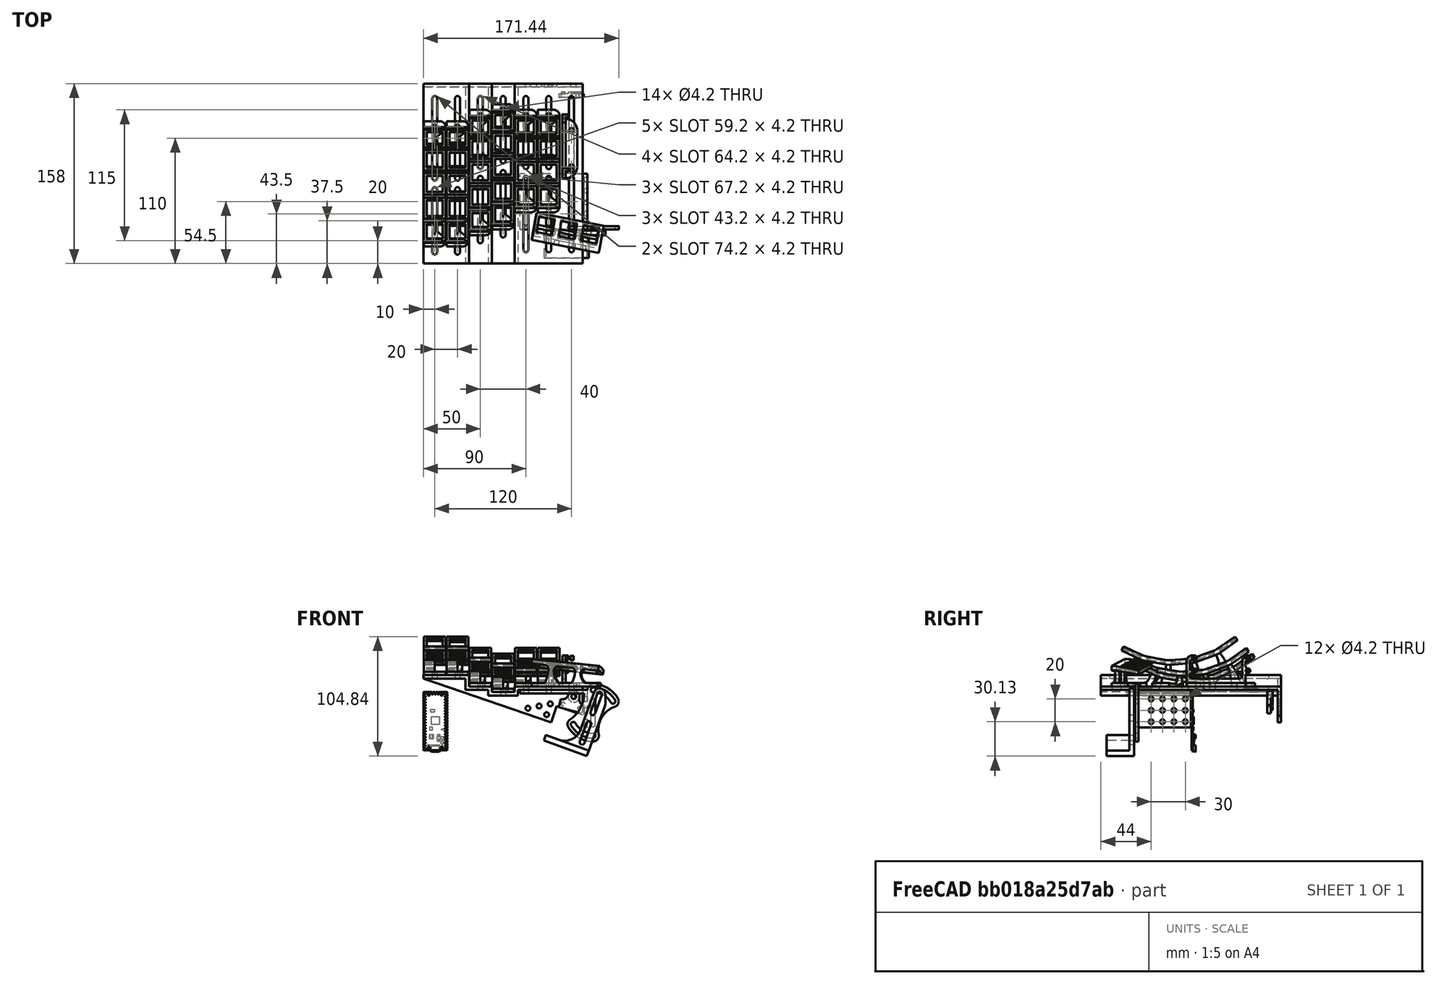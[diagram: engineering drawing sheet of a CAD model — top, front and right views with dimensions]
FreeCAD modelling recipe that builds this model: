
FCSTD DOCUMENT  (FreeCAD 0.20RUnknown)
Label: Dactyl Chimera V3
License: All rights reserved
LicenseURL: http://en.wikipedia.org/wiki/All_rights_reserved
objects: Sketcher::SketchObject×60, PartDesign::Pad×39, PartDesign::Pocket×21, PartDesign::Body×14, Part::Feature×14, App::Part×3, PartDesign::Plane×3, App::Link×3, App::DocumentObjectGroup×2, Part::Mirroring×2, Spreadsheet::Sheet×1, PartDesign::Line×1, Mesh::Feature×1
note: 214 computed .brp shape members not serialized (recipe doc carries the construction recipe); baked Part::Feature solids carry a one-line shape summary decoded from their .brp

FEATURE [Spreadsheet::Sheet] Spreadsheet
  cells = A1=Name; B1=Value; C1=Notes; A2=ModRowKey; B2(ModRowKey)==5mm; C2=The height of the keycaps in the row closest to you; A3=ZRowKey; B3(ZRowKey)==5mm; A4=ARowKey; B4(ARowKey)==5mm; A5=QRowKey; B5(QRowKey)==5mm; A6=TopRowKey; B6(TopRowKey)==5mm; A7=NutR; B7(NutR)==5mm; C7=The radius of the nut plus any clearance you want for your wrench.; A8=ScrewD; B8(ScrewD)==4.2mm; C8=The diameter of the screw shaft plus a bit extra so it fits nicely.; A9=Wiring; B9(Wiring)==6mm; C9=Minimum space under keys for hotswap sockets, PCBs, RGB, etc.; A10=ArchLength; B10(ArchLength)==45mm; C10=Set the distance of the screws in the arch feet. 
FEATURE [Sketcher::SketchObject] Sketch
  FullyConstrained = true
  MapMode = 5
  Placement = pos=(0,0,0) rot=(0.57735,0.57735,0.57735;2.0944rad)
  Support = -> [YZ_Plane]
  expr: Constraints[147] = <<Spreadsheet>>.ARowKey
  expr: Constraints[148] = <<Spreadsheet>>.ZRowKey
  expr: Constraints[155] = <<Spreadsheet>>.QRowKey
  expr: Constraints[159] = <<Spreadsheet>>.ModRowKey
  expr: Constraints[165] = <<Spreadsheet>>.TopRowKey
  expr: Constraints[171] = <<Spreadsheet>>.Wiring
  sketch-geometry (61):
    g0: LineSegment StartX=-50 StartY=9 StartZ=0 EndX=-50 EndY=3 EndZ=0
    g1: LineSegment StartX=-9.46385 StartY=12.9848 StartZ=0 EndX=0 EndY=13.8128 EndZ=0
    g2: LineSegment StartX=0 StartY=13.8128 StartZ=0 EndX=9.46385 EndY=14.6407 EndZ=0
    g3: LineSegment StartX=9.46385 StartY=14.6407 StartZ=0 EndX=11.8732 EndY=15.1749 EndZ=0
    g4: LineSegment StartX=11.8732 StartY=15.1749 StartZ=0 EndX=20.8002 EndY=18.4241 EndZ=0
    g5: LineSegment StartX=20.8002 StartY=18.4241 StartZ=0 EndX=29.7273 EndY=21.6733 EndZ=0
    g6: LineSegment StartX=29.7273 StartY=21.6733 StartZ=0 EndX=31.9163 EndY=22.8128 EndZ=0
    g7: LineSegment StartX=31.9163 StartY=22.8128 StartZ=0 EndX=39.6982 EndY=28.2617 EndZ=0
    g8: LineSegment StartX=39.6982 StartY=28.2617 StartZ=0 EndX=47.4802 EndY=33.7107 EndZ=0
    g9: LineSegment StartX=47.4802 StartY=33.7107 StartZ=0 EndX=49.7745 EndY=30.4341 EndZ=0
    g10: LineSegment StartX=49.7745 StartY=30.4341 StartZ=0 EndX=34.2106 EndY=19.5362 EndZ=0
    g11: LineSegment StartX=34.2106 StartY=19.5362 StartZ=0 EndX=31.0954 EndY=17.9145 EndZ=0
    g12: LineSegment StartX=31.0954 StartY=17.9145 StartZ=0 EndX=13.2412 EndY=11.4161 EndZ=0
    g13: LineSegment StartX=13.2412 StartY=11.4161 StartZ=0 EndX=9.81247 EndY=10.656 EndZ=0
    g14: LineSegment StartX=9.81247 StartY=10.656 StartZ=0 EndX=-9.11523 EndY=9 EndZ=0
    g15: LineSegment StartX=-9.11523 StartY=9 StartZ=0 EndX=-12.6239 EndY=9.15319 EndZ=0
    g16: LineSegment StartX=-12.6239 StartY=9.15319 StartZ=0 EndX=-31.3353 EndY=12.4525 EndZ=0
    g17: LineSegment StartX=-31.3353 StartY=12.4525 StartZ=0 EndX=-34.6847 EndY=13.5086 EndZ=0
    g18: LineSegment StartX=-34.6847 StartY=13.5086 StartZ=0 EndX=-51.9046 EndY=21.5383 EndZ=0
    g19: LineSegment StartX=-51.9046 StartY=21.5383 StartZ=0 EndX=-50.2141 EndY=25.1636 EndZ=0
    g20: LineSegment StartX=-50.2141 StartY=25.1636 StartZ=0 EndX=-41.6042 EndY=21.1487 EndZ=0
    g21: LineSegment StartX=-41.6042 StartY=21.1487 StartZ=0 EndX=-32.9942 EndY=17.1338 EndZ=0
    g22: LineSegment StartX=-32.9942 StartY=17.1338 StartZ=0 EndX=-30.6407 EndY=16.3917 EndZ=0
    g23: LineSegment StartX=-30.6407 StartY=16.3917 StartZ=0 EndX=-21.285 EndY=14.7421 EndZ=0
    g24: LineSegment StartX=-21.285 StartY=14.7421 StartZ=0 EndX=-11.9293 EndY=13.0924 EndZ=0
    g25: LineSegment StartX=-11.9293 StartY=13.0924 StartZ=0 EndX=-9.46385 EndY=12.9848 EndZ=0
    g26: LineSegment StartX=-34.6847 StartY=13.5086 StartZ=0 EndX=-32.9942 EndY=17.1338 EndZ=0
    g27: LineSegment StartX=-30.6407 StartY=16.3917 StartZ=0 EndX=-31.3353 EndY=12.4525 EndZ=0
    g28: LineSegment StartX=-12.6239 StartY=9.15319 StartZ=0 EndX=-11.9293 EndY=13.0924 EndZ=0
    g29: LineSegment StartX=-9.46385 StartY=12.9848 StartZ=0 EndX=-9.11523 EndY=9 EndZ=0
    g30: LineSegment StartX=9.46385 StartY=14.6407 StartZ=0 EndX=9.81247 EndY=10.656 EndZ=0
    g31: LineSegment StartX=11.8732 StartY=15.1749 StartZ=0 EndX=13.2412 EndY=11.4161 EndZ=0
    g32: LineSegment StartX=29.7273 StartY=21.6733 StartZ=0 EndX=31.0954 EndY=17.9145 EndZ=0
    g33: LineSegment StartX=31.9163 StartY=22.8128 StartZ=0 EndX=34.2106 EndY=19.5362 EndZ=0
    g34: LineSegment StartX=-41.6042 StartY=21.1487 StartZ=0 EndX=-39.4911 EndY=25.6802 EndZ=0
    g35: LineSegment StartX=-21.285 StartY=14.7421 StartZ=0 EndX=-20.4167 EndY=19.6661 EndZ=0
    g36: LineSegment StartX=0 StartY=13.8128 StartZ=0 EndX=-0.435779 EndY=18.7937 EndZ=0
    g37: LineSegment StartX=20.8002 StartY=18.4241 StartZ=0 EndX=19.0901 EndY=23.1225 EndZ=0
    g38: LineSegment StartX=39.6982 StartY=28.2617 StartZ=0 EndX=36.8304 EndY=32.3575 EndZ=0
    g39: LineSegment StartX=-39.4911 StartY=25.6802 StartZ=0 EndX=-36.7722 EndY=24.4124 EndZ=0
    g40: LineSegment StartX=-36.7722 StartY=24.4124 StartZ=0 EndX=-32.546 EndY=33.4755 EndZ=0
    g41: LineSegment StartX=-21.6347 StartY=30.0351 StartZ=0 EndX=-23.3712 EndY=20.1871 EndZ=0
    g42: LineSegment StartX=-23.3712 StartY=20.1871 StartZ=0 EndX=-20.4167 EndY=19.6661 EndZ=0
    g43: LineSegment StartX=-20.4167 StartY=19.6661 StartZ=0 EndX=-17.4623 EndY=19.1452 EndZ=0
    g44: LineSegment StartX=-17.4623 StartY=19.1452 StartZ=0 EndX=-15.7258 EndY=28.9933 EndZ=0
    g45: LineSegment StartX=-4.29592 StartY=28.4942 StartZ=0 EndX=-3.42436 EndY=18.5323 EndZ=0
    g46: LineSegment StartX=-3.42436 StartY=18.5323 StartZ=0 EndX=-0.435779 EndY=18.7937 EndZ=0
    g47: LineSegment StartX=-0.435779 StartY=18.7937 StartZ=0 EndX=2.55281 EndY=19.0552 EndZ=0
    g48: LineSegment StartX=2.55281 StartY=19.0552 StartZ=0 EndX=1.68125 EndY=29.0171 EndZ=0
    g49: LineSegment StartX=12.8509 StartY=31.4934 StartZ=0 EndX=16.2711 EndY=22.0965 EndZ=0
    g50: LineSegment StartX=16.2711 StartY=22.0965 StartZ=0 EndX=19.0901 EndY=23.1225 EndZ=0
    g51: LineSegment StartX=19.0901 StartY=23.1225 StartZ=0 EndX=21.9092 EndY=24.1486 EndZ=0
    g52: LineSegment StartX=21.9092 StartY=24.1486 StartZ=0 EndX=18.489 EndY=33.5455 EndZ=0
    g53: LineSegment StartX=28.6371 StartY=38.8283 StartZ=0 EndX=34.3729 EndY=30.6368 EndZ=0
    g54: LineSegment StartX=34.3729 StartY=30.6368 StartZ=0 EndX=36.8304 EndY=32.3575 EndZ=0
    g55: ArcOfCircle CenterX=-14.0244 CenterY=73.195 CenterZ=0 NormalX=0 NormalY=0 NormalZ=1 AngleXU=0 Radius=43.8257 StartAngle=4.27606 EndAngle=4.53786
    g56: ArcOfCircle CenterX=-8.11558 CenterY=72.1532 CenterZ=0 NormalX=0 NormalY=0 NormalZ=1 AngleXU=0 Radius=43.8257 StartAngle=4.53786 EndAngle=4.79966
    g57: ArcOfCircle CenterX=-2.13841 CenterY=72.6761 CenterZ=0 NormalX=0 NormalY=0 NormalZ=1 AngleXU=0 Radius=43.8257 StartAngle=4.79966 EndAngle=5.06145
    g58: ArcOfCircle CenterX=3.49974 CenterY=74.7282 CenterZ=0 NormalX=0 NormalY=0 NormalZ=1 AngleXU=0 Radius=43.8257 StartAngle=5.06145 EndAngle=5.32325
    g59: LineSegment StartX=-50 StartY=9 StartZ=0 EndX=-70 EndY=9 EndZ=0
    g60: LineSegment StartX=-50 StartY=9 StartZ=0 EndX=50 EndY=9 EndZ=0
  constraints (176):
    c: Vertical(g0)
    c: Coincident(g1,g2)
    c: Coincident(g2,g3)
    c: Coincident(g3,g4)
    c: Coincident(g4,g5)
    c: Coincident(g5,g6)
    c: Coincident(g6,g7)
    c: Coincident(g7,g8)
    c: Coincident(g8,g9)
    c: Coincident(g9,g10)
    c: Coincident(g10,g11)
    c: Coincident(g11,g12)
    c: Coincident(g12,g13)
    c: Coincident(g13,g14)
    c: Coincident(g14,g15)
    c: Coincident(g15,g16)
    c: Coincident(g16,g17)
    c: Coincident(g17,g18)
    c: Coincident(g18,g19)
    c: Coincident(g19,g20)
    c: Coincident(g20,g21)
    c: Coincident(g21,g22)
    c: Coincident(g22,g23)
    c: Coincident(g23,g24)
    c: Coincident(g24,g25)
    c: Coincident(g25,g1)
    c: Coincident(g26,g17)
    c: Coincident(g26,g21)
    c: Coincident(g27,g22)
    c: Coincident(g27,g16)
    c: Coincident(g28,g15)
    c: Coincident(g28,g24)
    c: Coincident(g29,g1)
    c: Coincident(g29,g14)
    c: Coincident(g30,g2)
    c: Coincident(g30,g13)
    c: Coincident(g31,g3)
    c: Coincident(g31,g12)
    c: Coincident(g32,g5)
    c: Coincident(g32,g11)
    c: Coincident(g33,g6)
    c: Coincident(g33,g10)
    c: Coincident(g34,g20)
    c: Coincident(g35,g23)
    c: Coincident(g36,g1)
    c: Coincident(g37,g4)
    c: Coincident(g38,g7)
    c: Parallel(g1,g2)
    c: Parallel(g4,g5)
    c: Parallel(g8,g7)
    c: Parallel(g21,g20)
    c: Parallel(g23,g24)
    c: Equal(g5,g4)
    c: Equal(g7,g8)
    c: Equal(g2,g1)
    c: Equal(g24,g23)
    c: Equal(g21,g20)
    c: Equal(g14,g16)
    c: Equal(g14,g12)
    c: Equal(g14,g10)
    c: Equal(g14,g18)
    c: Perpendicular(g26,g21)
    c: Perpendicular(g18,g26)
    c: Perpendicular(g19,g18)
    c: Perpendicular(g28,g24)
    c: Perpendicular(g16,g28)
    c: Perpendicular(g27,g16)
    c: Perpendicular(g14,g30)
    c: Perpendicular(g29,g14)
    c: Perpendicular(g31,g4)
    c: Perpendicular(g12,g31)
    c: Perpendicular(g32,g12)
    c: Perpendicular(g33,g7)
    c: Perpendicular(g10,g33)
    c: Perpendicular(g9,g10)
    c: Perpendicular(g8,g38)
    c: Perpendicular(g5,g37)
    c: Perpendicular(g1,g36)
    c: Perpendicular(g23,g35)
    c: Perpendicular(g20,g34)
    c: Equal(g29,g28)
    c: Equal(g27,g26)
    c: Equal(g30,g31)
    c: Equal(g32,g33)
    c: Coincident(g39,g40)
    c: Coincident(g41,g42)
    c: Coincident(g42,g35)
    c: Coincident(g42,g43)
    c: Coincident(g43,g44)
    c: Coincident(g45,g46)
    c: Coincident(g46,g36)
    c: Coincident(g46,g47)
    c: Coincident(g47,g48)
    c: Coincident(g49,g50)
    c: Coincident(g50,g37)
    c: Coincident(g50,g51)
    c: Coincident(g51,g52)
    c: Coincident(g53,g54)
    c: Coincident(g54,g38)
    c: Perpendicular(g54,g53)
    c: Perpendicular(g38,g54)
    c: Perpendicular(g51,g52)
    c: Perpendicular(g37,g51)
    c: Perpendicular(g50,g37)
    c: Perpendicular(g49,g50)
    c: Perpendicular(g47,g48)
    c: Perpendicular(g36,g47)
    c: Perpendicular(g46,g36)
    c: Perpendicular(g45,g46)
    c: Perpendicular(g43,g44)
    c: Perpendicular(g35,g43)
    c: Perpendicular(g42,g35)
    c: Perpendicular(g41,g42)
    c: Perpendicular(g39,g40)
    c: Perpendicular(g34,g39)
    c: Coincident(g55,g41)
    c: Coincident(g55,g40)
    c: Coincident(g56,g44)
    c: Coincident(g56,g45)
    c: Coincident(g57,g48)
    c: Coincident(g57,g49)
    c: Coincident(g58,g52)
    c: Coincident(g58,g53)
    c: Equal(g46,g47)
    c: Equal(g47,g50)
    c: Equal(g50,g51)
    c: Equal(g51,g54)
    c: Equal(g39,g42)
    c: Equal(g42,g43)
    c: Equal(g43,g46)
    c: Coincident(g39,g34)
    c: Distance(g14) = 19
    c: Distance(g35,g36) = 20
    c: Perpendicular(g56,g44)
    c: Perpendicular(g57,g48)
    c: Perpendicular(g57,g49)
    c: Angle(g35,g36) = 0.261799
    c: Perpendicular(g56,g45)
    c: Perpendicular(g58,g53)
    c: Perpendicular(g58,g52)
    c: Perpendicular(g55,g41)
    c: Perpendicular(g55,g40)
    c: Distance(g44) = 10
    c: Distance(g45) = 10
    c: Coincident(g59,g0)
    c: Horizontal(g59)
    c: Angle(g59,g36) = 1.65806
    c: Distance(g36) = 5
    c: Distance(g35) = 5
    c: Distance(g41) = 10
    c: Distance(g40) = 10
    c: Distance(g53) = 10
    c: Distance(g52) = 10
    c: Angle(g36,g37) = 0.261799
    c: Distance(g49) = 10
    c: Distance(g37) = 5
    c: Distance(g48) = 10
    c: Distance(g50) = 3
    c: Distance(g37,g36) = 20
    c: Distance(g34) = 5
    c: Angle(g34,g35) = 0.261799
    c: Distance(g35,g34) = 20
    c: Distance(g37,g38) = 20
    c: DistanceX(g0,g-1) = 50
    c: DistanceX(g59,g59) = 20
    c: Distance(g38) = 5
    c: Angle(g37,g38) = 0.261799
    c: Distance(g29) = 4
    c: Equal(g30,g29)
    c: Coincident(g60,g0)
    c: Horizontal(g60)
    c: DistanceY(g0,g0) = 6
    c: DistanceX(g60,g60) = 100
    c: DistanceY(g-1,g0) = 3
    c: PointOnObject(g14,g60)
    c: PointOnObject(g1,g-2)
FEATURE [PartDesign::Pad] Pad  label="OArch"
  Direction = (1,-2e-16,3e-16)
  Length = 19
  Length2 = 100
  Midplane = true
  Placement = pos=(0,0,0) rot=(0.57735,0.57735,0.57735;2.0944rad)
  Profile = -> Sketch
  Type = 0
FEATURE [Sketcher::SketchObject] Sketch001
  ExternalGeometry = -> [Pad]
  FullyConstrained = true
  MapMode = 5
  Placement = pos=(0,0,0) rot=(0.57735,0.57735,0.57735;2.0944rad)
  Support = -> [YZ_Plane]
  expr: Constraints[103] = <<Spreadsheet>>.Wiring
  expr: Constraints[104] = Spreadsheet.Wiring
  expr: Constraints[106] = <<Spreadsheet>>.Wiring
  expr: Constraints[107] = <<Spreadsheet>>.Wiring
  expr: Constraints[108] = <<Spreadsheet>>.Wiring
  expr: Constraints[109] = <<Spreadsheet>>.Wiring
  expr: Constraints[110] = <<Spreadsheet>>.Wiring
  expr: Constraints[111] = <<Spreadsheet>>.ArchLength * 2 - 10mm
  expr: Constraints[21] = <<Spreadsheet>>.ArchLength
  expr: Constraints[34] = <<Spreadsheet>>.ArchLength
  expr: Constraints[8] = <<Spreadsheet>>.Wiring + 4mm
  expr: Constraints[99] = <<Spreadsheet>>.Wiring
  sketch-geometry (44):
    g0: LineSegment StartX=-30.6407 StartY=16.3917 StartZ=0 EndX=-32.9942 EndY=17.1338 EndZ=0
    g1: LineSegment StartX=-11.9293 StartY=13.0924 StartZ=0 EndX=-9.46385 EndY=12.9848 EndZ=0
    g2: LineSegment StartX=11.8732 StartY=15.1749 StartZ=0 EndX=9.46385 EndY=14.6407 EndZ=0
    g3: LineSegment StartX=31.9163 StartY=22.8128 StartZ=0 EndX=29.7273 EndY=21.6733 EndZ=0
    g4: LineSegment StartX=-30.6407 StartY=16.3917 StartZ=0 EndX=-32.3771 EndY=6.54366 EndZ=0
    g5: LineSegment StartX=-11.9293 StartY=13.0924 StartZ=0 EndX=-13.6658 EndY=3.24435 EndZ=0
    g6: LineSegment StartX=-9.46385 StartY=12.9848 StartZ=0 EndX=-8.59229 EndY=3.02283 EndZ=0
    g7: LineSegment StartX=10.3354 StartY=4.67879 StartZ=0 EndX=9.46385 EndY=14.6407 EndZ=0
    g8: LineSegment StartX=11.8732 StartY=15.1749 StartZ=0 EndX=15.2934 EndY=5.77795 EndZ=0
    g9: LineSegment StartX=33.1475 StartY=12.2763 StartZ=0 EndX=29.7273 EndY=21.6733 EndZ=0
    g10: LineSegment StartX=31.9163 StartY=22.8128 StartZ=0 EndX=37.6521 EndY=14.6213 EndZ=0
    g11: LineSegment StartX=-37.2204 StartY=8.07075 StartZ=0 EndX=-32.9942 EndY=17.1338 EndZ=0
    g12: LineSegment StartX=-13.6658 StartY=0 StartZ=0 EndX=-8.59229 EndY=0 EndZ=0
    g13: LineSegment StartX=-45 StartY=3 StartZ=0 EndX=-45 EndY=0 EndZ=0
    g14: LineSegment StartX=-45 StartY=0 StartZ=0 EndX=-35 EndY=0 EndZ=0
    g15: LineSegment StartX=35 StartY=0 StartZ=0 EndX=45 EndY=0 EndZ=0
    g16: LineSegment StartX=45 StartY=3 StartZ=0 EndX=45 EndY=0 EndZ=0
    g17: LineSegment StartX=10.3354 StartY=0 StartZ=0 EndX=15.2934 EndY=0 EndZ=0
    g18: LineSegment StartX=-32.3771 StartY=6.54366 StartZ=0 EndX=-35 EndY=0 EndZ=0
    g19: LineSegment StartX=35 StartY=0 StartZ=0 EndX=33.1475 EndY=12.2763 EndZ=0
    g20-g23: Circle x4 (B-spline internal-alignment scaffolding for g24; pole/knot coordinates omitted)
    g24: BSplineCurve PolesCount=4 KnotsCount=2 Degree=3 IsPeriodic=0
    g25: GeomPoint X=-37.2204 Y=8.07075 Z=0
    g26: GeomPoint X=-45 Y=3 Z=0
    g27-g30: Circle x4 (B-spline internal-alignment scaffolding for g31; pole/knot coordinates omitted)
    g31: BSplineCurve PolesCount=4 KnotsCount=2 Degree=3 IsPeriodic=0
    g32: GeomPoint X=37.6521 Y=14.6213 Z=0
    g33: GeomPoint X=45 Y=3 Z=0
    g34: LineSegment StartX=45 StartY=3 StartZ=0 EndX=40 EndY=3 EndZ=0
    g35: LineSegment StartX=-45 StartY=3 StartZ=0 EndX=-40 EndY=3 EndZ=0
    g36: LineSegment StartX=42.2622 StartY=8.03741 StartZ=0 EndX=37.6521 EndY=14.6213 EndZ=0
    g37: LineSegment StartX=-37.2204 StartY=8.07075 StartZ=0 EndX=-39.0097 EndY=4.23371 EndZ=0
    g38: LineSegment StartX=-39.0097 StartY=0 StartZ=0 EndX=-39.0097 EndY=4.23371 EndZ=0
    g39: LineSegment StartX=42.2622 StartY=8.03741 StartZ=0 EndX=42.2622 EndY=0 EndZ=0
    g40: LineSegment StartX=-13.6658 StartY=3.24435 StartZ=0 EndX=-13.6658 EndY=0 EndZ=0
    g41: LineSegment StartX=-8.59229 StartY=3.02283 StartZ=0 EndX=-8.59229 EndY=0 EndZ=0
    g42: LineSegment StartX=10.3354 StartY=4.67879 StartZ=0 EndX=10.3354 EndY=0 EndZ=0
    g43: LineSegment StartX=15.2934 StartY=5.77795 StartZ=0 EndX=15.2934 EndY=0 EndZ=0
  constraints (107):
    c: Coincident(g-6,g2)
    c: Coincident(g2,g-6)
    c: Coincident(g0,g-10)
    c: Coincident(g0,g-10)
    c: Coincident(g1,g-7)
    c: Coincident(g1,g-7)
    c: Coincident(g-3,g3)
    c: Coincident(g3,g-3)
    c: Distance(g0,g11) = 10
    c: Coincident(g4,g0)
    c: Coincident(g5,g1)
    c: Coincident(g6,g1)
    c: Coincident(g8,g2)
    c: Coincident(g9,g3)
    c: Coincident(g10,g3)
    c: Coincident(g11,g0)
    c: Equal(g11,g4)
    c: Equal(g9,g10)
    c: Coincident(g7,g2)
    c: PointOnObject(g12,g-1)
    c: PointOnObject(g12,g-1)
    c: DistanceX(g-11,g16) = 45
    c: PointOnObject(g13,g-1)
    c: Vertical(g13)
    c: Coincident(g13,g14)
    c: Horizontal(g14)
    c: DistanceY(g13,g13) = 3
    c: PointOnObject(g17,g-1)
    c: Horizontal(g15)
    c: Coincident(g16,g15)
    c: Vertical(g16)
    c: Equal(g13,g16)
    c: PointOnObject(g15,g-1)
    c: Horizontal(g17)
    c: DistanceX(g13,g-11) = 45
    c: Coincident(g18,g4)
    c: Coincident(g18,g14)
    c: Coincident(g19,g15)
    c: Coincident(g19,g9)
    c: Coincident(g24,g11)
    c: Weight(g20) = 1
    c: Equal(g20,g21)
    c: Equal(g20,g22)
    c: Equal(g20,g23)
    c: Coincident(g24,g13)
    c: InternalAlignment(g20-g23 -> g24) x4
    c: InternalAlignment(g25,g24)
    c: InternalAlignment(g26,g24)
    c: Coincident(g31,g10)
    c: Weight(g27) = 1
    c: Equal(g27,g28)
    c: Equal(g27,g29)
    c: Equal(g27,g30)
    c: Coincident(g31,g16)
    c: InternalAlignment(g27-g30 -> g31) x4
    c: InternalAlignment(g32,g31)
    c: InternalAlignment(g33,g31)
    c: Coincident(g34,g29)
    c: Coincident(g35,g13)
    c: Coincident(g35,g22)
    c: Coincident(g36,g28)
    c: Coincident(g36,g10)
    c: Coincident(g37,g11)
    c: Coincident(g37,g21)
    c: PointOnObject(g38,g-1)
    c: Coincident(g38,g21)
    c: Equal(g37,g38)
    c: Parallel(g37,g11)
    c: DistanceX(g35,g35) = 5
    c: Coincident(g34,g16)
    c: Equal(g34,g35)
    c: Coincident(g39,g28)
    c: PointOnObject(g39,g-1)
    c: Equal(g36,g39)
    c: Parallel(g36,g10)
    c: Vertical(g38)
    c: Vertical(g39)
    c: Equal(g15,g14)
    c: DistanceX(g14,g14) = 10
    c: Distance(g10) = 10
    c: Equal(g9,g4)
    c: Coincident(g40,g5)
    c: Coincident(g40,g12)
    c: Coincident(g41,g6)
    c: Coincident(g41,g12)
    c: Vertical(g41)
    c: Vertical(g40)
    c: Coincident(g42,g7)
    c: Coincident(g42,g17)
    c: Coincident(g43,g8)
    c: Coincident(g43,g17)
    c: Vertical(g43)
    c: Vertical(g42)
    c: Distance(g-8,g5) = 6
    c: Equal(g6,g5)
    c: Equal(g5,g7)
    c: Equal(g7,g8)
    c: Distance(g-9,g11) = 6
    c: Distance(g-9,g4) = 6
    c: Equal(g5,g11)
    c: Distance(g-5,g7) = 6
    c: Distance(g-5,g8) = 6
    c: Distance(g-4,g9) = 6
    c: Distance(g10,g-4) = 6
    c: Distance(g6,g-8) = 6
    c: DistanceX(g22,g29) = 80
    c: Horizontal(g35)
FEATURE [PartDesign::Pad] Pad001  label="OLegs"
  BaseFeature = -> Pad
  Direction = (1,-2e-16,3e-16)
  Length = 9.5
  Length2 = 100
  Placement = pos=(0,0,0) rot=(0.57735,0.57735,0.57735;2.0944rad)
  Profile = -> Sketch001
  Reversed = true
  Type = 0
FEATURE [Sketcher::SketchObject] Sketch002
  ExternalGeometry = -> [Sketch001]
  FullyConstrained = true
  MapMode = 5
  Support = -> [XY_Plane]
  expr: Constraints[14] = <<Spreadsheet>>.NutR
  expr: Constraints[15] = <<Spreadsheet>>.NutR
  expr: Constraints[26] = <<Spreadsheet>>.ScrewD
  expr: Constraints[27] = <<Spreadsheet>>.NutR
  expr: Constraints[28] = Spreadsheet.NutR
  expr: Constraints[8] = <<Spreadsheet>>.ScrewD
  sketch-geometry (22):
    g0: LineSegment StartX=-1e-14 StartY=-45 StartZ=0 EndX=-9.5 EndY=-45 EndZ=0
    g1: LineSegment StartX=-9.5 StartY=-45 StartZ=0 EndX=-9.5 EndY=-55 EndZ=0
    g2: LineSegment StartX=-9.5 StartY=-55 StartZ=0 EndX=4.5 EndY=-55 EndZ=0
    g3: LineSegment StartX=-1e-14 StartY=-45 StartZ=0 EndX=-1e-14 EndY=-40 EndZ=0
    g4: Circle CenterX=0 CenterY=-50 CenterZ=0 NormalX=0 NormalY=0 NormalZ=1 AngleXU=0 Radius=2.1
    g5: ArcOfCircle CenterX=4.5 CenterY=-50 CenterZ=0 NormalX=0 NormalY=0 NormalZ=1 AngleXU=0 Radius=5 StartAngle=4.71239 EndAngle=7.17949
    g6: LineSegment StartX=0 StartY=-50 StartZ=0 EndX=4.5 EndY=-50 EndZ=0
    g7: LineSegment StartX=9.8e-15 StartY=40 StartZ=0 EndX=9.8e-15 EndY=45 EndZ=0
    g8: LineSegment StartX=9.8e-15 StartY=45 StartZ=0 EndX=-9.5 EndY=45 EndZ=0
    g9: LineSegment StartX=-9.5 StartY=45 StartZ=0 EndX=-9.5 EndY=55 EndZ=0
    g10: LineSegment StartX=-9.5 StartY=55 StartZ=0 EndX=4.5 EndY=55 EndZ=0
    g11: ArcOfCircle CenterX=4.5 CenterY=50 CenterZ=0 NormalX=0 NormalY=0 NormalZ=1 AngleXU=0 Radius=5 StartAngle=5.38688 EndAngle=7.85398
    g12: Circle CenterX=0 CenterY=50 CenterZ=0 NormalX=0 NormalY=0 NormalZ=1 AngleXU=0 Radius=2.1
    g13: LineSegment StartX=0 StartY=50 StartZ=0 EndX=4.5 EndY=50 EndZ=0
    g14: LineSegment StartX=7.6225 StartY=46.0949 StartZ=0 EndX=9.8e-15 EndY=40 EndZ=0
    g15: LineSegment StartX=-1e-14 StartY=-40 StartZ=0 EndX=7.6225 EndY=-46.0949 EndZ=0
    g16: LineSegment StartX=9.5 StartY=55 StartZ=0 EndX=9.5 EndY=50 EndZ=0
    g17: LineSegment StartX=-9.5 StartY=55 StartZ=0 EndX=0 EndY=50 EndZ=0
    g18: LineSegment StartX=9.5 StartY=55 StartZ=0 EndX=0 EndY=50 EndZ=0
    g19: LineSegment StartX=9.5 StartY=-50 StartZ=0 EndX=9.5 EndY=-55 EndZ=0
    g20: LineSegment StartX=9.5 StartY=-55 StartZ=0 EndX=0 EndY=-50 EndZ=0
    g21: LineSegment StartX=0 StartY=-50 StartZ=0 EndX=-9.5 EndY=-55 EndZ=0
  constraints (58):
    c: Coincident(g0,g-3)
    c: Horizontal(g0)
    c: Coincident(g1,g0)
    c: Vertical(g1)
    c: Coincident(g2,g1)
    c: Horizontal(g2)
    c: Coincident(g3,g0)
    c: DistanceY(g3,g3) = 5
    c: Diameter(g4) = 4.2
    c: Tangent(g5,g2) = -1.5708
    c: Coincident(g6,g4)
    c: Coincident(g6,g5)
    c: Horizontal(g6)
    c: PointOnObject(g4,g-2)
    c: DistanceY(g4,g0) = 5
    c: DistanceY(g1,g4) = 5
    c: Vertical(g7)
    c: Coincident(g7,g8)
    c: Horizontal(g8)
    c: Coincident(g8,g9)
    c: Vertical(g9)
    c: Coincident(g9,g10)
    c: Horizontal(g10)
    c: Tangent(g11,g10) = 1.5708
    c: DistanceY(g7,g7) = 5
    c: PointOnObject(g12,g-2)
    c: Diameter(g12) = 4.2
    c: DistanceY(g8,g12) = 5
    c: DistanceY(g12,g9) = 5
    c: Coincident(g13,g12)
    c: Coincident(g13,g11)
    c: Horizontal(g13)
    c: Coincident(g14,g7)
    c: Vertical(g3)
    c: Coincident(g15,g3)
    c: Coincident(g7,g-4)
    c: Tangent(g14,g11) = 1.5708
    c: Vertical(g16)
    c: Tangent(g16,g11)
    c: PointOnObject(g16,g11)
    c: Horizontal(g16,g10)
    c: DistanceX(g9,g16) = 19
    c: Coincident(g17,g9)
    c: Coincident(g17,g12)
    c: Coincident(g18,g16)
    c: Coincident(g18,g12)
    c: Equal(g18,g17)
    c: Tangent(g15,g5) = 1.5708
    c: Vertical(g19)
    c: Tangent(g19,g5)
    c: Coincident(g19,g20)
    c: Coincident(g20,g4)
    c: Coincident(g20,g21)
    c: Coincident(g21,g1)
    c: Horizontal(g19,g2)
    c: PointOnObject(g19,g5)
    c: Equal(g20,g21)
    c: DistanceX(g1,g19) = 19
FEATURE [PartDesign::Pad] Pad002  label="OFeet"
  BaseFeature = -> Pad001
  Direction = (0,0,1)
  Length = 3
  Length2 = 100
  Placement = pos=(0,0,0) rot=(0.57735,0.57735,0.57735;2.0944rad)
  Profile = -> Sketch002
  Type = 0
FEATURE [Sketcher::SketchObject] Sketch003
  ExternalGeometry = -> [Sketch]
  FullyConstrained = true
  MapMode = 5
  Placement = pos=(0,0,0) rot=(0.57735,0.57735,0.57735;2.0944rad)
  Support = -> [YZ_Plane]
  sketch-geometry (75):
    g0: LineSegment StartX=-41.6042 StartY=21.1487 StartZ=0 EndX=-47.9483 EndY=24.107 EndZ=0
    g1: LineSegment StartX=-41.6042 StartY=21.1487 StartZ=0 EndX=-35.26 EndY=18.1904 EndZ=0
    g2: LineSegment StartX=-41.6042 StartY=21.1487 StartZ=0 EndX=-43.2946 EndY=17.5235 EndZ=0
    g3: LineSegment StartX=-35.7723 StartY=14.0157 StartZ=0 EndX=-43.2946 EndY=17.5235 EndZ=0
    g4: LineSegment StartX=-43.2946 StartY=17.5235 StartZ=0 EndX=-50.817 EndY=21.0312 EndZ=0
    g5: LineSegment StartX=-50.817 StartY=21.0312 StartZ=0 EndX=-49.7182 EndY=23.3876 EndZ=0
    g6: LineSegment StartX=-47.9483 StartY=24.107 StartZ=0 EndX=-49.6388 EndY=20.4818 EndZ=0
    g7: LineSegment StartX=-49.7182 StartY=23.3876 StartZ=0 EndX=-48.54 EndY=22.8382 EndZ=0
    g8: LineSegment StartX=-48.54 StartY=22.8382 StartZ=0 EndX=-47.9483 EndY=24.107 EndZ=0
    g9: LineSegment StartX=-35.26 StartY=18.1904 StartZ=0 EndX=-35.8517 EndY=16.9215 EndZ=0
    g10: LineSegment StartX=-35.8517 StartY=16.9215 StartZ=0 EndX=-34.6735 EndY=16.3721 EndZ=0
    g11: LineSegment StartX=-35.7723 StartY=14.0157 StartZ=0 EndX=-34.6735 EndY=16.3721 EndZ=0
    g12: LineSegment StartX=-35.26 StartY=18.1904 StartZ=0 EndX=-36.9505 EndY=14.5651 EndZ=0
    g13: LineSegment StartX=-35.7723 StartY=14.0157 StartZ=0 EndX=-34.0818 EndY=17.641 EndZ=0
    g14: LineSegment StartX=-21.285 StartY=14.7421 StartZ=0 EndX=-21.9796 EndY=10.8028 EndZ=0
    g15: LineSegment StartX=0 StartY=13.8128 StartZ=0 EndX=0.348623 EndY=9.82798 EndZ=0
    g16: LineSegment StartX=20.8002 StartY=18.4241 StartZ=0 EndX=22.1683 EndY=14.6653 EndZ=0
    g17: LineSegment StartX=39.6982 StartY=28.2617 StartZ=0 EndX=41.9925 EndY=24.9851 EndZ=0
    g18: LineSegment StartX=-28.1786 StartY=15.9576 StartZ=0 EndX=-21.285 EndY=14.7421 EndZ=0
    g19: LineSegment StartX=-21.285 StartY=14.7421 StartZ=0 EndX=-14.3913 EndY=13.5265 EndZ=0
    g20: LineSegment StartX=-6.97336 StartY=13.2027 StartZ=0 EndX=0 EndY=13.8128 EndZ=0
    g21: LineSegment StartX=0 StartY=13.8128 StartZ=0 EndX=6.97336 EndY=14.4228 EndZ=0
    g22: LineSegment StartX=14.2224 StartY=16.0299 StartZ=0 EndX=20.8002 EndY=18.4241 EndZ=0
    g23: LineSegment StartX=20.8002 StartY=18.4241 StartZ=0 EndX=27.3781 EndY=20.8182 EndZ=0
    g24: LineSegment StartX=33.9642 StartY=24.2467 StartZ=0 EndX=39.6982 EndY=28.2617 EndZ=0
    g25: LineSegment StartX=39.6982 StartY=28.2617 StartZ=0 EndX=45.4323 EndY=32.2768 EndZ=0
    g26: LineSegment StartX=-30.1535 StartY=12.2441 StartZ=0 EndX=-21.9796 EndY=10.8028 EndZ=0
    g27: LineSegment StartX=-21.9796 StartY=10.8028 StartZ=0 EndX=-13.8057 EndY=9.36157 EndZ=0
    g28: LineSegment StartX=-7.91979 StartY=9.10459 StartZ=0 EndX=0.348623 EndY=9.82798 EndZ=0
    g29: LineSegment StartX=0.348623 StartY=9.82798 StartZ=0 EndX=8.61704 EndY=10.5514 EndZ=0
    g30: LineSegment StartX=14.3689 StartY=11.8265 StartZ=0 EndX=22.1683 EndY=14.6653 EndZ=0
    g31: LineSegment StartX=22.1683 StartY=14.6653 StartZ=0 EndX=29.9678 EndY=17.5041 EndZ=0
    g32: LineSegment StartX=-28.1786 StartY=15.9576 StartZ=0 EndX=-28.8732 EndY=12.0184 EndZ=0
    g33: LineSegment StartX=-14.3913 StartY=13.5265 StartZ=0 EndX=-15.0859 EndY=9.58731 EndZ=0
    g34: LineSegment StartX=-13.8057 StartY=9.36157 StartZ=0 EndX=-13.1111 EndY=13.3008 EndZ=0
    g35: LineSegment StartX=-6.97336 StartY=13.2027 StartZ=0 EndX=-6.62474 EndY=9.21789 EndZ=0
    g36: LineSegment StartX=-7.91979 StartY=9.10459 StartZ=0 EndX=-8.26842 EndY=13.0894 EndZ=0
    g37: LineSegment StartX=6.97336 StartY=14.4228 StartZ=0 EndX=7.32199 EndY=10.4381 EndZ=0
    g38: LineSegment StartX=8.61704 StartY=10.5514 StartZ=0 EndX=8.26842 EndY=14.5362 EndZ=0
    g39: LineSegment StartX=14.3689 StartY=11.8265 StartZ=0 EndX=13.0008 EndY=15.5853 EndZ=0
    g40: LineSegment StartX=14.2224 StartY=16.0299 StartZ=0 EndX=15.5905 EndY=12.2711 EndZ=0
    g41: LineSegment StartX=27.3781 StartY=20.8182 StartZ=0 EndX=28.7462 EndY=17.0594 EndZ=0
    g42: LineSegment StartX=29.9678 StartY=17.5041 StartZ=0 EndX=28.5997 EndY=21.2628 EndZ=0
    g43: LineSegment StartX=35.1936 StartY=20.2244 StartZ=0 EndX=32.8993 EndY=23.5011 EndZ=0
    g44: LineSegment StartX=33.9642 StartY=24.2467 StartZ=0 EndX=36.2585 EndY=20.9701 EndZ=0
    g45: LineSegment StartX=45.4323 StartY=32.2768 StartZ=0 EndX=47.7266 EndY=29.0002 EndZ=0
    g46: LineSegment StartX=48.7915 StartY=29.7458 StartZ=0 EndX=46.4972 EndY=33.0224 EndZ=0
    g47: LineSegment StartX=-30.1535 StartY=12.2441 StartZ=0 EndX=-29.4589 EndY=16.1834 EndZ=0
    g48: LineSegment StartX=-30.1535 StartY=12.2441 StartZ=0 EndX=-29.702 EndY=14.8046 EndZ=0
    g49: LineSegment StartX=-29.702 StartY=14.8046 StartZ=0 EndX=-28.4218 EndY=14.5789 EndZ=0
    g50: LineSegment StartX=-28.4218 StartY=14.5789 StartZ=0 EndX=-28.1786 EndY=15.9576 EndZ=0
    g51: LineSegment StartX=-13.8057 StartY=9.36157 StartZ=0 EndX=-13.3542 EndY=11.9221 EndZ=0
    g52: LineSegment StartX=-13.3542 StartY=11.9221 StartZ=0 EndX=-14.6344 EndY=12.1478 EndZ=0
    g53: LineSegment StartX=-14.6344 StartY=12.1478 StartZ=0 EndX=-14.3913 EndY=13.5265 EndZ=0
    g54: LineSegment StartX=-7.91979 StartY=9.10459 StartZ=0 EndX=-8.14639 EndY=11.6947 EndZ=0
    g55: LineSegment StartX=-8.14639 StartY=11.6947 StartZ=0 EndX=-6.85134 EndY=11.808 EndZ=0
    g56: LineSegment StartX=-6.85134 StartY=11.808 StartZ=0 EndX=-6.97336 EndY=13.2027 EndZ=0
    g57: LineSegment StartX=6.97336 StartY=14.4228 StartZ=0 EndX=7.09538 EndY=13.0282 EndZ=0
    g58: LineSegment StartX=7.09538 StartY=13.0282 StartZ=0 EndX=8.39044 EndY=13.1415 EndZ=0
    g59: LineSegment StartX=8.39044 StartY=13.1415 StartZ=0 EndX=8.61704 EndY=10.5514 EndZ=0
    g60: LineSegment StartX=14.3689 StartY=11.8265 StartZ=0 EndX=13.4796 EndY=14.2697 EndZ=0
    g61: LineSegment StartX=13.4796 StartY=14.2697 StartZ=0 EndX=14.7012 EndY=14.7144 EndZ=0
    g62: LineSegment StartX=14.7012 StartY=14.7144 StartZ=0 EndX=14.2224 EndY=16.0299 EndZ=0
    g63: LineSegment StartX=29.9678 StartY=17.5041 StartZ=0 EndX=29.0785 EndY=19.9473 EndZ=0
    g64: LineSegment StartX=29.0785 StartY=19.9473 StartZ=0 EndX=27.8569 EndY=19.5026 EndZ=0
    g65: LineSegment StartX=27.8569 StartY=19.5026 StartZ=0 EndX=27.3781 EndY=20.8182 EndZ=0
    g66: LineSegment StartX=35.1936 StartY=20.2244 StartZ=0 EndX=33.7023 EndY=22.3542 EndZ=0
    g67: LineSegment StartX=33.7023 StartY=22.3542 StartZ=0 EndX=34.7672 EndY=23.0999 EndZ=0
    g68: LineSegment StartX=34.7672 StartY=23.0999 StartZ=0 EndX=33.9642 EndY=24.2467 EndZ=0
    g69: LineSegment StartX=48.7915 StartY=29.7458 StartZ=0 EndX=47.3002 EndY=31.8756 EndZ=0
    g70: LineSegment StartX=47.3002 StartY=31.8756 StartZ=0 EndX=46.2353 EndY=31.13 EndZ=0
    g71: LineSegment StartX=46.2353 StartY=31.13 StartZ=0 EndX=45.4323 EndY=32.2768 EndZ=0
    g72: LineSegment StartX=-50.817 StartY=21.0312 StartZ=0 EndX=-49.1265 EndY=24.6564 EndZ=0
    g73: LineSegment StartX=48.7915 StartY=29.7458 StartZ=0 EndX=42.5661 EndY=24.166 EndZ=0
    g74: LineSegment StartX=42.5661 StartY=24.166 StartZ=0 EndX=35.1936 EndY=20.2244 EndZ=0
  constraints (216):
    c: Coincident(g0,g-10)
    c: PointOnObject(g0,g-9)
    c: Coincident(g1,g0)
    c: PointOnObject(g1,g-10)
    c: Distance(g0,g1) = 14
    c: Equal(g1,g0)
    c: Coincident(g2,g0)
    c: PointOnObject(g2,g-11)
    c: Perpendicular(g2,g0)
    c: Coincident(g3,g2)
    c: Coincident(g3,g4)
    c: PointOnObject(g4,g-11)
    c: PointOnObject(g3,g-11)
    c: Equal(g3,g4)
    c: Distance(g3,g4) = 16.6
    c: Coincident(g5,g4)
    c: Coincident(g6,g0)
    c: PointOnObject(g6,g4)
    c: Perpendicular(g0,g6)
    c: Distance(g5) = 2.6
    c: Coincident(g5,g7)
    c: Coincident(g7,g8)
    c: Coincident(g8,g0)
    c: Distance(g8) = 1.4
    c: Distance(g7,g6) = 2.6
    c: Coincident(g9,g1)
    c: Coincident(g10,g9)
    c: Coincident(g11,g3)
    c: Coincident(g10,g11)
    c: Coincident(g12,g1)
    c: PointOnObject(g12,g3)
    c: Coincident(g13,g3)
    c: PointOnObject(g13,g-10)
    c: Perpendicular(g1,g12)
    c: Perpendicular(g3,g13)
    c: Distance(g9,g12) = 2.6
    c: Distance(g10,g13) = 1.4
    c: Distance(g9) = 1.4
    c: Distance(g11) = 2.6
    c: Coincident(g14,g-13)
    c: PointOnObject(g14,g-17)
    c: Coincident(g15,g-15)
    c: PointOnObject(g15,g-16)
    c: Coincident(g16,g-5)
    c: PointOnObject(g16,g-3)
    c: Coincident(g17,g-8)
    c: PointOnObject(g17,g-6)
    c: PointOnObject(g18,g-12)
    c: Coincident(g18,g14)
    c: Coincident(g18,g19)
    c: PointOnObject(g19,g-13)
    c: PointOnObject(g20,g-14)
    c: Coincident(g20,g15)
    c: Coincident(g20,g21)
    c: PointOnObject(g21,g-15)
    c: PointOnObject(g22,g-4)
    c: Coincident(g22,g23)
    c: PointOnObject(g24,g-7)
    c: Coincident(g24,g17)
    c: Coincident(g24,g25)
    c: PointOnObject(g25,g-8)
    c: Coincident(g22,g16)
    c: PointOnObject(g23,g-5)
    c: Equal(g18,g19)
    c: Equal(g21,g20)
    c: Equal(g22,g23)
    c: Equal(g24,g25)
    c: Perpendicular(g14,g18)
    c: Perpendicular(g15,g20)
    c: Perpendicular(g22,g16)
    c: Perpendicular(g24,g17)
    c: Distance(g18,g19) = 14
    c: Distance(g20,g21) = 14
    c: Distance(g22,g23) = 14
    c: Distance(g24,g25) = 14
    c: PointOnObject(g26,g-17)
    c: Coincident(g26,g14)
    c: Coincident(g26,g27)
    c: PointOnObject(g27,g-17)
    c: PointOnObject(g28,g-16)
    c: Coincident(g28,g15)
    c: Coincident(g28,g29)
    c: PointOnObject(g29,g-16)
    c: PointOnObject(g30,g-3)
    c: Coincident(g30,g16)
    c: Coincident(g30,g31)
    c: PointOnObject(g31,g-3)
    c: PointOnObject(g46,g-6)
    c: PointOnObject(g43,g-6)
    c: Distance(g26,g27) = 16.6
    c: Equal(g27,g26)
    c: Equal(g28,g29)
    c: Equal(g30,g31)
    c: Distance(g28,g29) = 16.6
    c: Distance(g30,g31) = 16.6
    c: Distance(g43,g46) = 16.6
    c: Coincident(g32,g18)
    c: PointOnObject(g32,g26)
    c: Coincident(g33,g19)
    c: PointOnObject(g33,g27)
    c: Coincident(g34,g27)
    c: PointOnObject(g34,g-13)
    c: Coincident(g35,g20)
    c: PointOnObject(g35,g28)
    c: Coincident(g36,g28)
    c: PointOnObject(g36,g-14)
    c: Coincident(g37,g21)
    c: PointOnObject(g37,g29)
    c: Coincident(g38,g29)
    c: PointOnObject(g38,g-15)
    c: Coincident(g39,g30)
    c: PointOnObject(g39,g-4)
    c: Coincident(g41,g23)
    c: PointOnObject(g41,g31)
    c: Coincident(g42,g31)
    c: PointOnObject(g42,g-5)
    c: PointOnObject(g43,g-7)
    c: Coincident(g44,g24)
    c: Coincident(g45,g25)
    c: Coincident(g47,g26)
    c: PointOnObject(g47,g-12)
    c: Perpendicular(g26,g47)
    c: Perpendicular(g32,g18)
    c: Perpendicular(g33,g19)
    c: Perpendicular(g34,g27)
    c: Perpendicular(g28,g36)
    c: Perpendicular(g20,g35)
    c: Perpendicular(g21,g37)
    c: Perpendicular(g38,g29)
    c: Perpendicular(g30,g39)
    c: Perpendicular(g22,g40)
    c: Perpendicular(g23,g41)
    c: Perpendicular(g31,g42)
    c: Perpendicular(g24,g44)
    c: Perpendicular(g25,g45)
    c: Coincident(g26,g48)
    c: Coincident(g48,g49)
    c: Coincident(g49,g50)
    c: Coincident(g50,g18)
    c: Coincident(g27,g51)
    c: Coincident(g51,g52)
    c: Coincident(g52,g53)
    c: Coincident(g53,g19)
    c: Coincident(g54,g55)
    c: Coincident(g55,g56)
    c: Coincident(g56,g20)
    c: Coincident(g21,g57)
    c: Coincident(g57,g58)
    c: Coincident(g58,g59)
    c: Coincident(g59,g29)
    c: PointOnObject(g40,g30)
    c: Coincident(g40,g22)
    c: Coincident(g30,g60)
    c: Coincident(g60,g61)
    c: Coincident(g61,g62)
    c: Coincident(g62,g22)
    c: Coincident(g31,g63)
    c: Coincident(g63,g64)
    c: Coincident(g64,g65)
    c: Coincident(g65,g23)
    c: Coincident(g66,g67)
    c: Coincident(g67,g68)
    c: Coincident(g68,g24)
    c: Coincident(g69,g70)
    c: Coincident(g70,g71)
    c: Coincident(g71,g25)
    c: Distance(g50) = 1.4
    c: Distance(g53) = 1.4
    c: Distance(g56) = 1.4
    c: Distance(g57) = 1.4
    c: Distance(g62) = 1.4
    c: Distance(g65) = 1.4
    c: Distance(g68) = 1.4
    c: Distance(g71) = 1.4
    c: Distance(g69) = 2.6
    c: Distance(g66) = 2.6
    c: Distance(g63) = 2.6
    c: Distance(g60) = 2.6
    c: Distance(g59) = 2.6
    c: Distance(g54) = 2.6
    c: Distance(g51) = 2.6
    c: Distance(g48) = 2.6
    c: Distance(g48,g47) = 1.4
    c: Distance(g51,g34) = 1.4
    c: Distance(g54,g36) = 1.4
    c: Distance(g38,g58) = 1.4
    c: Distance(g60,g39) = 1.4
    c: Distance(g63,g42) = 1.4
    c: Distance(g66,g43) = 1.4
    c: PointOnObject(g46,g-8)
    c: Distance(g69,g46) = 1.4
    c: Distance(g70,g45) = 2.6
    c: Distance(g67,g44) = 2.6
    c: Distance(g64,g41) = 2.6
    c: Distance(g61,g40) = 2.6
    c: Distance(g57,g37) = 2.6
    c: Distance(g55,g28) = 2.6
    c: Distance(g52,g27) = 2.6
    c: Distance(g49,g26) = 2.6
    c: Coincident(g54,g28)
    c: Coincident(g72,g4)
    c: PointOnObject(g72,g-9)
    c: Distance(g5,g72) = 1.4
    c: Perpendicular(g72,g4)
    c: Coincident(g69,g73)
    c: Coincident(g73,g74)
    c: Coincident(g74,g66)
    c: Distance(g17,g73) = 1
    c: Distance(g73,g24) = 5
    c: PointOnObject(g44,g-6)
    c: Perpendicular(g-6,g43)
    c: Coincident(g66,g43)
    c: Perpendicular(g-6,g46)
    c: Coincident(g69,g46)
    c: Equal(g73,g74)
    c: PointOnObject(g45,g-6)
FEATURE [PartDesign::Pocket] Pocket  label="OMX sockets"
  BaseFeature = -> Pad002
  Direction = (-1,2e-16,-3e-16)
  Length = 14
  Length2 = 100
  Midplane = true
  Placement = pos=(0,0,0) rot=(0.57735,0.57735,0.57735;2.0944rad)
  Profile = -> Sketch003
  Type = 0
FEATURE [Sketcher::SketchObject] Sketch004
  ExternalGeometry = -> [Sketch003]
  FullyConstrained = true
  MapMode = 5
  Placement = pos=(0,0,0) rot=(0.57735,0.57735,0.57735;2.0944rad)
  Support = -> [YZ_Plane]
  sketch-geometry (40):
    g0: LineSegment StartX=-48.4555 StartY=23.0195 StartZ=0 EndX=-35.7672 EndY=17.1028 EndZ=0
    g1: LineSegment StartX=-35.7672 StartY=17.1028 StartZ=0 EndX=-35.8517 EndY=16.9215 EndZ=0
    g2: LineSegment StartX=-34.6735 StartY=16.3721 StartZ=0 EndX=-35.0116 EndY=15.6471 EndZ=0
    g3: LineSegment StartX=-35.0116 StartY=15.6471 StartZ=0 EndX=-50.0563 EndY=22.6626 EndZ=0
    g4: LineSegment StartX=-50.0563 StartY=22.6626 StartZ=0 EndX=-49.7182 EndY=23.3876 EndZ=0
    g5: LineSegment StartX=-48.54 StartY=22.8382 StartZ=0 EndX=-48.4555 EndY=23.0195 EndZ=0
    g6: LineSegment StartX=-49.7182 StartY=23.3876 StartZ=0 EndX=-48.54 EndY=22.8382 EndZ=0
    g7: LineSegment StartX=-34.6735 StartY=16.3721 StartZ=0 EndX=-35.8517 EndY=16.9215 EndZ=0
    g8: LineSegment StartX=-29.702 StartY=14.8046 StartZ=0 EndX=-29.8409 EndY=14.0168 EndZ=0
    g9: LineSegment StartX=-29.8409 StartY=14.0168 StartZ=0 EndX=-13.4931 EndY=11.1342 EndZ=0
    g10: LineSegment StartX=-13.4931 StartY=11.1342 StartZ=0 EndX=-13.3542 EndY=11.9221 EndZ=0
    g11: LineSegment StartX=-13.3542 StartY=11.9221 StartZ=0 EndX=-14.6344 EndY=12.1478 EndZ=0
    g12: LineSegment StartX=-14.6344 StartY=12.1478 StartZ=0 EndX=-14.5997 EndY=12.3448 EndZ=0
    g13: LineSegment StartX=-14.5997 StartY=12.3448 StartZ=0 EndX=-28.387 EndY=14.7759 EndZ=0
    g14: LineSegment StartX=-28.387 StartY=14.7759 StartZ=0 EndX=-28.4218 EndY=14.5789 EndZ=0
    g15: LineSegment StartX=-6.86877 StartY=12.0072 StartZ=0 EndX=-6.85134 EndY=11.808 EndZ=0
    g16: LineSegment StartX=-6.85134 StartY=11.808 StartZ=0 EndX=-8.14639 EndY=11.6947 EndZ=0
    g17: LineSegment StartX=-8.14639 StartY=11.6947 StartZ=0 EndX=-8.07666 EndY=10.8977 EndZ=0
    g18: LineSegment StartX=-8.07666 StartY=10.8977 StartZ=0 EndX=8.46017 EndY=12.3445 EndZ=0
    g19: LineSegment StartX=8.46017 StartY=12.3445 StartZ=0 EndX=8.39044 EndY=13.1415 EndZ=0
    g20: LineSegment StartX=8.39044 StartY=13.1415 StartZ=0 EndX=7.09538 EndY=13.0282 EndZ=0
    g21: LineSegment StartX=7.09538 StartY=13.0282 StartZ=0 EndX=7.07795 EndY=13.2274 EndZ=0
    g22: LineSegment StartX=7.07795 StartY=13.2274 StartZ=0 EndX=-6.86877 EndY=12.0072 EndZ=0
    g23: LineSegment StartX=14.6328 StartY=14.9023 StartZ=0 EndX=14.7012 EndY=14.7144 EndZ=0
    g24: LineSegment StartX=14.7012 StartY=14.7144 StartZ=0 EndX=13.4796 EndY=14.2697 EndZ=0
    g25: LineSegment StartX=13.4796 StartY=14.2697 StartZ=0 EndX=13.7533 EndY=13.518 EndZ=0
    g26: LineSegment StartX=13.7533 StartY=13.518 StartZ=0 EndX=29.3521 EndY=19.1955 EndZ=0
    g27: LineSegment StartX=29.3521 StartY=19.1955 StartZ=0 EndX=29.0785 EndY=19.9473 EndZ=0
    g28: LineSegment StartX=29.0785 StartY=19.9473 StartZ=0 EndX=27.8569 EndY=19.5026 EndZ=0
    g29: LineSegment StartX=27.8569 StartY=19.5026 StartZ=0 EndX=27.7885 EndY=19.6906 EndZ=0
    g30: LineSegment StartX=27.7885 StartY=19.6906 StartZ=0 EndX=14.6328 EndY=14.9023 EndZ=0
    g31: LineSegment StartX=34.7672 StartY=23.0999 StartZ=0 EndX=33.7023 EndY=22.3542 EndZ=0
    g32: LineSegment StartX=33.7023 StartY=22.3542 StartZ=0 EndX=34.1612 EndY=21.6989 EndZ=0
    g33: LineSegment StartX=34.1612 StartY=21.6989 StartZ=0 EndX=47.7591 EndY=31.2203 EndZ=0
    g34: LineSegment StartX=47.7591 StartY=31.2203 StartZ=0 EndX=47.3002 EndY=31.8756 EndZ=0
    g35: LineSegment StartX=47.3002 StartY=31.8756 StartZ=0 EndX=46.2353 EndY=31.13 EndZ=0
    g36: LineSegment StartX=46.2353 StartY=31.13 StartZ=0 EndX=46.1206 EndY=31.2938 EndZ=0
    g37: LineSegment StartX=46.1206 StartY=31.2938 StartZ=0 EndX=34.6525 EndY=23.2637 EndZ=0
    g38: LineSegment StartX=34.6525 StartY=23.2637 StartZ=0 EndX=34.7672 EndY=23.0999 EndZ=0
    g39: LineSegment StartX=-29.702 StartY=14.8046 StartZ=0 EndX=-28.4218 EndY=14.5789 EndZ=0
  constraints (100):
    c: Coincident(g0,g1)
    c: Coincident(g5,g0)
    c: Distance(g5) = 0.2
    c: Distance(g1) = 0.2
    c: Coincident(g3,g2)
    c: Coincident(g4,g3)
    c: Distance(g4) = 0.8
    c: Distance(g2) = 0.8
    c: Coincident(g6,g4)
    c: Coincident(g6,g5)
    c: Coincident(g7,g2)
    c: Coincident(g7,g1)
    c: Coincident(g8,g9)
    c: Coincident(g9,g10)
    c: Coincident(g10,g11)
    c: Coincident(g11,g12)
    c: Coincident(g12,g13)
    c: Coincident(g13,g14)
    c: Coincident(g15,g16)
    c: Coincident(g16,g17)
    c: Coincident(g17,g18)
    c: Coincident(g18,g19)
    c: Coincident(g19,g20)
    c: Coincident(g20,g21)
    c: Coincident(g21,g22)
    c: Coincident(g22,g15)
    c: Coincident(g23,g24)
    c: Coincident(g25,g26)
    c: Coincident(g26,g27)
    c: Coincident(g27,g28)
    c: Coincident(g28,g29)
    c: Coincident(g29,g30)
    c: Coincident(g30,g23)
    c: Coincident(g31,g32)
    c: Coincident(g32,g33)
    c: Coincident(g33,g34)
    c: Coincident(g35,g36)
    c: Coincident(g36,g37)
    c: Coincident(g37,g38)
    c: Coincident(g39,g8)
    c: Coincident(g39,g14)
    c: Distance(g14) = 0.2
    c: Distance(g12) = 0.2
    c: Distance(g15) = 0.2
    c: Distance(g21) = 0.2
    c: Distance(g23) = 0.2
    c: Distance(g29) = 0.2
    c: Distance(g36) = 0.2
    c: Distance(g34) = 0.8
    c: Distance(g32) = 0.8
    c: Distance(g27) = 0.8
    c: Distance(g19) = 0.8
    c: Distance(g17) = 0.8
    c: Distance(g10) = 0.8
    c: Distance(g8) = 0.8
    c: Distance(g26,g-18) = 1.8
    c: Distance(g18,g-14) = 1.8
    c: Distance(g17,g-12) = 1.8
    c: Distance(g9,g-10) = 1.8
    c: Distance(g-8,g8) = 1.8
    c: Distance(g13,g-7) = 1.2
    c: Distance(g12,g-9) = 1.2
    c: Distance(g15,g-11) = 1.2
    c: Distance(g21,g-13) = 1.2
    c: Distance(g23,g-16) = 1.2
    c: Distance(g29,g-17) = 1.2
    c: Distance(g2,g-4) = 1.8
    c: Distance(g3,g-3) = 1.8
    c: Distance(g-5,g0) = 1.2
    c: Distance(g0,g-6) = 1.2
    c: Coincident(g28,g-17)
    c: Coincident(g27,g-18)
    c: Coincident(g24,g-15)
    c: Coincident(g24,g25)
    c: Distance(g25) = 0.8
    c: Distance(g25,g-15) = 1.8
    c: Coincident(g23,g-16)
    c: Coincident(g19,g-14)
    c: Coincident(g20,g-13)
    c: Coincident(g16,g-12)
    c: Coincident(g15,g-11)
    c: Coincident(g11,g-9)
    c: Coincident(g10,g-10)
    c: Coincident(g8,g-8)
    c: Coincident(g14,g-7)
    c: Coincident(g1,g-6)
    c: Coincident(g2,g-4)
    c: Coincident(g4,g-3)
    c: Coincident(g5,g-5)
    c: Coincident(g34,g-21)
    c: Coincident(g35,g-20)
    c: Coincident(g35,g34)
    c: Distance(g33,g-21) = 1.8
    c: Distance(g36,g-20) = 1.2
    c: Distance(g38) = 0.2
    c: Distance(g37,g-22) = 1.2
    c: Coincident(g31,g-22)
    c: Coincident(g31,g-19)
    c: Distance(g32,g-19) = 1.8
    c: Coincident(g38,g31)
FEATURE [PartDesign::Pocket] Pocket001  label="OChoc sockets"
  BaseFeature = -> Pocket
  Direction = (-1,2e-16,-3e-16)
  Length = 14.6
  Length2 = 100
  Midplane = true
  Placement = pos=(0,0,0) rot=(0.57735,0.57735,0.57735;2.0944rad)
  Profile = -> Sketch004
  Type = 0
FEATURE [Sketcher::SketchObject] Sketch006
  FullyConstrained = true
  MapMode = 5
  Placement = pos=(0,0,0) rot=(0.57735,0.57735,0.57735;2.0944rad)
  Support = -> [YZ_Plane001]
  expr: Constraints[124] = <<Spreadsheet>>.ModRowKey
  expr: Constraints[125] = <<Spreadsheet>>.ZRowKey
  expr: Constraints[132] = <<Spreadsheet>>.ARowKey
  expr: Constraints[157] = <<Spreadsheet>>.QRowKey
  expr: Constraints[158] = <<Spreadsheet>>.TopRowKey
  expr: Constraints[169] = <<Spreadsheet>>.Wiring
  sketch-geometry (61):
    g0: LineSegment StartX=-32.9942 StartY=17.1338 StartZ=0 EndX=-30.6407 EndY=16.3917 EndZ=0
    g1: LineSegment StartX=-11.9293 StartY=13.0924 StartZ=0 EndX=-9.46385 EndY=12.9848 EndZ=0
    g2: LineSegment StartX=9.46385 StartY=14.6407 StartZ=0 EndX=11.8732 EndY=15.1749 EndZ=0
    g3: LineSegment StartX=29.7273 StartY=21.6733 StartZ=0 EndX=31.9163 EndY=22.8128 EndZ=0
    g4: LineSegment StartX=47.4802 StartY=33.7107 StartZ=0 EndX=49.7745 EndY=30.4341 EndZ=0
    g5: LineSegment StartX=49.7745 StartY=30.4341 StartZ=0 EndX=34.2106 EndY=19.5362 EndZ=0
    g6: LineSegment StartX=34.2106 StartY=19.5362 StartZ=0 EndX=31.0954 EndY=17.9145 EndZ=0
    g7: LineSegment StartX=31.0954 StartY=17.9145 StartZ=0 EndX=13.2412 EndY=11.4161 EndZ=0
    g8: LineSegment StartX=13.2412 StartY=11.4161 StartZ=0 EndX=9.81247 EndY=10.656 EndZ=0
    g9: LineSegment StartX=9.81247 StartY=10.656 StartZ=0 EndX=-9.11523 EndY=9 EndZ=0
    g10: LineSegment StartX=-9.11523 StartY=9 StartZ=0 EndX=-12.6239 EndY=9.15319 EndZ=0
    g11: LineSegment StartX=-12.6239 StartY=9.15319 StartZ=0 EndX=-31.3353 EndY=12.4525 EndZ=0
    g12: LineSegment StartX=-31.3353 StartY=12.4525 StartZ=0 EndX=-34.6847 EndY=13.5086 EndZ=0
    g13: LineSegment StartX=-34.6847 StartY=13.5086 StartZ=0 EndX=-51.9046 EndY=21.5383 EndZ=0
    g14: LineSegment StartX=-51.9046 StartY=21.5383 StartZ=0 EndX=-50.2141 EndY=25.1636 EndZ=0
    g15: LineSegment StartX=47.4802 StartY=33.7107 StartZ=0 EndX=39.6982 EndY=28.2617 EndZ=0
    g16: LineSegment StartX=39.6982 StartY=28.2617 StartZ=0 EndX=31.9163 EndY=22.8128 EndZ=0
    g17: LineSegment StartX=29.7273 StartY=21.6733 StartZ=0 EndX=20.8002 EndY=18.4241 EndZ=0
    g18: LineSegment StartX=20.8002 StartY=18.4241 StartZ=0 EndX=11.8732 EndY=15.1749 EndZ=0
    g19: LineSegment StartX=9.46385 StartY=14.6407 StartZ=0 EndX=0 EndY=13.8128 EndZ=0
    g20: LineSegment StartX=0 StartY=13.8128 StartZ=0 EndX=-9.46385 EndY=12.9848 EndZ=0
    g21: LineSegment StartX=-11.9293 StartY=13.0924 StartZ=0 EndX=-21.285 EndY=14.7421 EndZ=0
    g22: LineSegment StartX=-21.285 StartY=14.7421 StartZ=0 EndX=-30.6407 EndY=16.3917 EndZ=0
    g23: LineSegment StartX=-32.9942 StartY=17.1338 StartZ=0 EndX=-41.6042 EndY=21.1487 EndZ=0
    g24: LineSegment StartX=-41.6042 StartY=21.1487 StartZ=0 EndX=-50.2141 EndY=25.1636 EndZ=0
    g25: LineSegment StartX=-41.6042 StartY=21.1487 StartZ=0 EndX=-39.4911 EndY=25.6802 EndZ=0
    g26: LineSegment StartX=-39.4911 StartY=25.6802 StartZ=0 EndX=-36.7722 EndY=24.4124 EndZ=0
    g27: LineSegment StartX=-36.7722 StartY=24.4124 StartZ=0 EndX=-32.546 EndY=33.4755 EndZ=0
    g28: LineSegment StartX=-21.6347 StartY=30.0351 StartZ=0 EndX=-23.3712 EndY=20.1871 EndZ=0
    g29: LineSegment StartX=-23.3712 StartY=20.1871 StartZ=0 EndX=-20.4167 EndY=19.6661 EndZ=0
    g30: LineSegment StartX=-20.4167 StartY=19.6661 StartZ=0 EndX=-21.285 EndY=14.7421 EndZ=0
    g31: LineSegment StartX=-20.4167 StartY=19.6661 StartZ=0 EndX=-17.4623 EndY=19.1452 EndZ=0
    g32: LineSegment StartX=-17.4623 StartY=19.1452 StartZ=0 EndX=-15.7258 EndY=28.9933 EndZ=0
    g33: LineSegment StartX=-4.29592 StartY=28.4942 StartZ=0 EndX=-3.42436 EndY=18.5323 EndZ=0
    g34: LineSegment StartX=-3.42436 StartY=18.5323 StartZ=0 EndX=-0.435779 EndY=18.7937 EndZ=0
    g35: LineSegment StartX=-0.435779 StartY=18.7937 StartZ=0 EndX=0 EndY=13.8128 EndZ=0
    g36: LineSegment StartX=-0.435779 StartY=18.7937 StartZ=0 EndX=2.55281 EndY=19.0552 EndZ=0
    g37: LineSegment StartX=2.55281 StartY=19.0552 StartZ=0 EndX=1.68125 EndY=29.0171 EndZ=0
    g38: LineSegment StartX=12.8509 StartY=31.4934 StartZ=0 EndX=16.2711 EndY=22.0965 EndZ=0
    g39: LineSegment StartX=16.2711 StartY=22.0965 StartZ=0 EndX=19.0901 EndY=23.1225 EndZ=0
    g40: LineSegment StartX=19.0901 StartY=23.1225 StartZ=0 EndX=20.8002 EndY=18.4241 EndZ=0
    g41: LineSegment StartX=19.0901 StartY=23.1225 StartZ=0 EndX=21.9092 EndY=24.1486 EndZ=0
    g42: LineSegment StartX=21.9092 StartY=24.1486 StartZ=0 EndX=18.489 EndY=33.5455 EndZ=0
    g43: LineSegment StartX=28.6371 StartY=38.8283 StartZ=0 EndX=34.3729 EndY=30.6368 EndZ=0
    g44: LineSegment StartX=34.3729 StartY=30.6368 StartZ=0 EndX=36.8304 EndY=32.3575 EndZ=0
    g45: LineSegment StartX=36.8304 StartY=32.3575 StartZ=0 EndX=39.6982 EndY=28.2617 EndZ=0
    g46: ArcOfCircle CenterX=-14.0244 CenterY=73.195 CenterZ=0 NormalX=0 NormalY=0 NormalZ=1 AngleXU=0 Radius=43.8257 StartAngle=4.27606 EndAngle=4.53786
    g47: ArcOfCircle CenterX=-8.11558 CenterY=72.1532 CenterZ=0 NormalX=0 NormalY=0 NormalZ=1 AngleXU=0 Radius=43.8257 StartAngle=4.53786 EndAngle=4.79966
    g48: ArcOfCircle CenterX=-2.13841 CenterY=72.6761 CenterZ=0 NormalX=0 NormalY=0 NormalZ=1 AngleXU=0 Radius=43.8257 StartAngle=4.79966 EndAngle=5.06145
    g49: ArcOfCircle CenterX=3.49974 CenterY=74.7282 CenterZ=0 NormalX=0 NormalY=0 NormalZ=1 AngleXU=0 Radius=43.8257 StartAngle=5.06145 EndAngle=5.32325
    g50: LineSegment StartX=-32.9942 StartY=17.1338 StartZ=0 EndX=-34.6847 EndY=13.5086 EndZ=0
    g51: LineSegment StartX=-30.6407 StartY=16.3917 StartZ=0 EndX=-31.3353 EndY=12.4525 EndZ=0
    g52: LineSegment StartX=-12.6239 StartY=9.15319 StartZ=0 EndX=-11.9293 EndY=13.0924 EndZ=0
    g53: LineSegment StartX=-9.46385 StartY=12.9848 StartZ=0 EndX=-9.11523 EndY=9 EndZ=0
    g54: LineSegment StartX=9.46385 StartY=14.6407 StartZ=0 EndX=9.81247 EndY=10.656 EndZ=0
    g55: LineSegment StartX=11.8732 StartY=15.1749 StartZ=0 EndX=13.2412 EndY=11.4161 EndZ=0
    g56: LineSegment StartX=31.9163 StartY=22.8128 StartZ=0 EndX=34.2106 EndY=19.5362 EndZ=0
    g57: LineSegment StartX=29.7273 StartY=21.6733 StartZ=0 EndX=31.0954 EndY=17.9145 EndZ=0
    g58: LineSegment StartX=-50 StartY=3 StartZ=0 EndX=-50 EndY=9 EndZ=0
    g59: LineSegment StartX=-50 StartY=9 StartZ=0 EndX=-70 EndY=9 EndZ=0
    g60: LineSegment StartX=-50 StartY=9 StartZ=0 EndX=50 EndY=9 EndZ=0
  constraints (176):
    c: Coincident(g4,g5)
    c: Coincident(g5,g6)
    c: Coincident(g6,g7)
    c: Coincident(g7,g8)
    c: Coincident(g8,g9)
    c: Coincident(g9,g10)
    c: Coincident(g10,g11)
    c: Coincident(g11,g12)
    c: Coincident(g12,g13)
    c: Coincident(g13,g14)
    c: Coincident(g4,g15)
    c: Coincident(g15,g16)
    c: Coincident(g16,g3)
    c: Coincident(g3,g17)
    c: Coincident(g17,g18)
    c: Coincident(g18,g2)
    c: Coincident(g2,g19)
    c: Coincident(g19,g20)
    c: Coincident(g20,g1)
    c: Coincident(g1,g21)
    c: Coincident(g21,g22)
    c: Coincident(g22,g0)
    c: Coincident(g0,g23)
    c: Coincident(g23,g24)
    c: Coincident(g24,g14)
    c: Coincident(g23,g25)
    c: Coincident(g25,g26)
    c: Coincident(g26,g27)
    c: Coincident(g28,g29)
    c: Coincident(g29,g30)
    c: Coincident(g30,g21)
    c: Coincident(g29,g31)
    c: Coincident(g31,g32)
    c: Coincident(g33,g34)
    c: Coincident(g34,g35)
    c: Coincident(g35,g19)
    c: Coincident(g34,g36)
    c: Coincident(g36,g37)
    c: Coincident(g38,g39)
    c: Coincident(g39,g40)
    c: Coincident(g40,g17)
    c: Coincident(g39,g41)
    c: Coincident(g41,g42)
    c: Coincident(g43,g44)
    c: Coincident(g44,g45)
    c: Coincident(g45,g15)
    c: Coincident(g46,g27)
    c: Coincident(g46,g28)
    c: Coincident(g47,g32)
    c: Coincident(g47,g33)
    c: Coincident(g48,g37)
    c: Coincident(g48,g38)
    c: Coincident(g49,g42)
    c: Coincident(g49,g43)
    c: Distance(g9) = 19
    c: Perpendicular(g13,g14)
    c: Equal(g9,g11)
    c: Equal(g11,g13)
    c: Equal(g13,g7)
    c: Equal(g7,g5)
    c: Distance(g43) = 10
    c: Distance(g42) = 10
    c: Distance(g38) = 10
    c: Distance(g37) = 10
    c: Distance(g32) = 10
    c: Distance(g28) = 10
    c: Distance(g27) = 10
    c: Perpendicular(g46,g27)
    c: Perpendicular(g46,g28)
    c: Perpendicular(g47,g32)
    c: Perpendicular(g47,g33)
    c: Perpendicular(g48,g37)
    c: Perpendicular(g48,g38)
    c: Perpendicular(g49,g42)
    c: Perpendicular(g49,g43)
    c: Coincident(g50,g0)
    c: Coincident(g50,g12)
    c: Coincident(g51,g0)
    c: Coincident(g51,g11)
    c: Coincident(g52,g10)
    c: Coincident(g52,g1)
    c: Coincident(g53,g1)
    c: Coincident(g53,g9)
    c: Distance(g33) = 10
    c: Equal(g24,g23)
    c: Equal(g22,g21)
    c: Equal(g20,g19)
    c: Equal(g18,g17)
    c: Equal(g16,g15)
    c: Parallel(g24,g23)
    c: Parallel(g22,g21)
    c: Parallel(g20,g19)
    c: Parallel(g18,g17)
    c: Parallel(g16,g15)
    c: Coincident(g54,g2)
    c: Coincident(g54,g8)
    c: Coincident(g55,g7)
    c: Coincident(g2,g55)
    c: Coincident(g56,g3)
    c: Coincident(g56,g5)
    c: Coincident(g57,g3)
    c: Coincident(g57,g6)
    c: Perpendicular(g23,g50)
    c: Perpendicular(g13,g50)
    c: Perpendicular(g11,g51)
    c: Perpendicular(g52,g11)
    c: Perpendicular(g21,g52)
    c: Perpendicular(g53,g9)
    c: Perpendicular(g9,g54)
    c: Perpendicular(g35,g20)
    c: Equal(g54,g53)
    c: Distance(g25,g29) = 20
    c: Distance(g29,g34) = 20
    c: Distance(g34,g39) = 20
    c: Distance(g39,g44) = 20
    c: Perpendicular(g26,g27)
    c: Perpendicular(g29,g28)
    c: Perpendicular(g31,g32)
    c: Perpendicular(g36,g37)
    c: Perpendicular(g38,g39)
    c: Perpendicular(g41,g42)
    c: Perpendicular(g43,g44)
    c: Perpendicular(g24,g25)
    c: Perpendicular(g22,g30)
    c: Distance(g25) = 5
    c: Distance(g30) = 5
    c: Perpendicular(g26,g25)
    c: Perpendicular(g30,g31)
    c: Perpendicular(g30,g29)
    c: Equal(g53,g52)
    c: Equal(g50,g51)
    c: Equal(g55,g54)
    c: Distance(g35) = 5
    c: Perpendicular(g36,g35)
    c: Distance(g53) = 4
    c: Perpendicular(g34,g35)
    c: Perpendicular(g33,g34)
    c: Perpendicular(g18,g40)
    c: Equal(g57,g56)
    c: Perpendicular(g55,g7)
    c: Perpendicular(g55,g18)
    c: Perpendicular(g17,g57)
    c: Perpendicular(g40,g41)
    c: Perpendicular(g56,g5)
    c: Perpendicular(g15,g4)
    c: Perpendicular(g5,g4)
    c: Perpendicular(g16,g45)
    c: Equal(g26,g29)
    c: Equal(g31,g29)
    c: Equal(g34,g36)
    c: Equal(g31,g34)
    c: Equal(g36,g39)
    c: Perpendicular(g40,g39)
    c: Equal(g44,g41)
    c: Angle(g25,g30) = 0.261799
    c: Angle(g30,g35) = 0.261799
    c: Angle(g35,g40) = 0.261799
    c: Distance(g40) = 5
    c: Distance(g45) = 5
    c: Perpendicular(g44,g45)
    c: Angle(g40,g45) = 0.261799
    c: Vertical(g58)
    c: Coincident(g59,g58)
    c: Horizontal(g59)
    c: Coincident(g60,g58)
    c: Horizontal(g60)
    c: DistanceX(g59,g59) = 20
    c: DistanceX(g58,g-1) = 50
    c: DistanceX(g60,g60) = 100
    c: DistanceY(g58,g58) = 6
    c: DistanceY(g-1,g58) = 3
    c: Angle(g59,g35) = 1.65806
    c: Equal(g39,g41)
    c: Distance(g39) = 3
    c: PointOnObject(g19,g-2)
    c: PointOnObject(g9,g60)
FEATURE [PartDesign::Pad] Pad004  label="PArch"
  Direction = (1,-2e-16,3e-16)
  Length = 19
  Length2 = 100
  Midplane = true
  Placement = pos=(0,0,0) rot=(0.57735,0.57735,0.57735;2.0944rad)
  Profile = -> Sketch006
  Type = 0
FEATURE [Sketcher::SketchObject] Sketch007
  ExternalGeometry = -> [Sketch006]
  FullyConstrained = true
  MapMode = 5
  Placement = pos=(0,0,0) rot=(0.57735,0.57735,0.57735;2.0944rad)
  Support = -> [YZ_Plane001]
  sketch-geometry (85):
    g0: LineSegment StartX=-49.1265 StartY=24.6564 StartZ=0 EndX=-50.817 EndY=21.0312 EndZ=0
    g1: LineSegment StartX=-49.6388 StartY=20.4818 StartZ=0 EndX=-47.9483 EndY=24.107 EndZ=0
    g2: LineSegment StartX=-41.6042 StartY=21.1487 StartZ=0 EndX=-43.2946 EndY=17.5235 EndZ=0
    g3: LineSegment StartX=-35.26 StartY=18.1904 StartZ=0 EndX=-36.9505 EndY=14.5651 EndZ=0
    g4: LineSegment StartX=-35.7723 StartY=14.0157 StartZ=0 EndX=-34.0818 EndY=17.641 EndZ=0
    g5: LineSegment StartX=-29.4589 StartY=16.1834 StartZ=0 EndX=-30.1535 EndY=12.2441 EndZ=0
    g6: LineSegment StartX=-28.8732 StartY=12.0184 StartZ=0 EndX=-28.1786 EndY=15.9576 EndZ=0
    g7: LineSegment StartX=-21.285 StartY=14.7421 StartZ=0 EndX=-21.9796 EndY=10.8028 EndZ=0
    g8: LineSegment StartX=-15.0859 StartY=9.58731 StartZ=0 EndX=-14.3913 EndY=13.5265 EndZ=0
    g9: LineSegment StartX=-13.1111 StartY=13.3008 StartZ=0 EndX=-13.8057 EndY=9.36157 EndZ=0
    g10: LineSegment StartX=-8.26842 StartY=13.0894 StartZ=0 EndX=-7.91979 EndY=9.10459 EndZ=0
    g11: LineSegment StartX=-6.62474 StartY=9.21789 StartZ=0 EndX=-6.97336 EndY=13.2027 EndZ=0
    g12: LineSegment StartX=0 StartY=13.8128 StartZ=0 EndX=0.348623 EndY=9.82798 EndZ=0
    g13: LineSegment StartX=7.32199 StartY=10.4381 StartZ=0 EndX=6.97336 EndY=14.4228 EndZ=0
    g14: LineSegment StartX=8.26842 StartY=14.5362 StartZ=0 EndX=8.61704 EndY=10.5514 EndZ=0
    g15: LineSegment StartX=14.3689 StartY=11.8265 StartZ=0 EndX=13.0008 EndY=15.5853 EndZ=0
    g16: LineSegment StartX=14.2224 StartY=16.0299 StartZ=0 EndX=15.5905 EndY=12.2711 EndZ=0
    g17: LineSegment StartX=20.8002 StartY=18.4241 StartZ=0 EndX=22.1683 EndY=14.6653 EndZ=0
    g18: LineSegment StartX=28.7462 StartY=17.0594 StartZ=0 EndX=27.3781 EndY=20.8182 EndZ=0
    g19: LineSegment StartX=28.5997 StartY=21.2628 StartZ=0 EndX=29.9678 EndY=17.5041 EndZ=0
    g20: LineSegment StartX=35.1936 StartY=20.2244 StartZ=0 EndX=32.8993 EndY=23.5011 EndZ=0
    g21: LineSegment StartX=33.9642 StartY=24.2467 StartZ=0 EndX=36.2585 EndY=20.9701 EndZ=0
    g22: LineSegment StartX=39.6982 StartY=28.2617 StartZ=0 EndX=41.9925 EndY=24.9851 EndZ=0
    g23: LineSegment StartX=45.4323 StartY=32.2768 StartZ=0 EndX=47.7266 EndY=29.0002 EndZ=0
    g24: LineSegment StartX=48.7915 StartY=29.7458 StartZ=0 EndX=46.4972 EndY=33.0224 EndZ=0
    g25: LineSegment StartX=-47.9483 StartY=24.107 StartZ=0 EndX=-41.6042 EndY=21.1487 EndZ=0
    g26: LineSegment StartX=-41.6042 StartY=21.1487 StartZ=0 EndX=-35.26 EndY=18.1904 EndZ=0
    g27: LineSegment StartX=-35.26 StartY=18.1904 StartZ=0 EndX=-35.8517 EndY=16.9215 EndZ=0
    g28: LineSegment StartX=-35.8517 StartY=16.9215 StartZ=0 EndX=-34.6735 EndY=16.3721 EndZ=0
    g29: LineSegment StartX=-34.6735 StartY=16.3721 StartZ=0 EndX=-36.9505 EndY=14.5651 EndZ=0
    g30: LineSegment StartX=-49.6388 StartY=20.4818 StartZ=0 EndX=-49.7182 EndY=23.3876 EndZ=0
    g31: LineSegment StartX=-49.7182 StartY=23.3876 StartZ=0 EndX=-48.54 EndY=22.8382 EndZ=0
    g32: LineSegment StartX=-48.54 StartY=22.8382 StartZ=0 EndX=-47.9483 EndY=24.107 EndZ=0
    g33: LineSegment StartX=-29.702 StartY=14.8046 StartZ=0 EndX=-28.4217 EndY=14.5789 EndZ=0
    g34: LineSegment StartX=-28.4217 StartY=14.5789 StartZ=0 EndX=-28.1786 EndY=15.9576 EndZ=0
    g35: LineSegment StartX=-28.1786 StartY=15.9576 StartZ=0 EndX=-21.285 EndY=14.7421 EndZ=0
    g36: LineSegment StartX=-21.285 StartY=14.7421 StartZ=0 EndX=-14.3913 EndY=13.5265 EndZ=0
    g37: LineSegment StartX=-14.3913 StartY=13.5265 StartZ=0 EndX=-14.6344 EndY=12.1478 EndZ=0
    g38: LineSegment StartX=-14.6344 StartY=12.1478 StartZ=0 EndX=-13.3542 EndY=11.9221 EndZ=0
    g39: LineSegment StartX=-13.3542 StartY=11.9221 StartZ=0 EndX=-15.0859 EndY=9.58731 EndZ=0
    g40: LineSegment StartX=-15.0859 StartY=9.58731 StartZ=0 EndX=-21.9796 EndY=10.8028 EndZ=0
    g41: LineSegment StartX=-21.9796 StartY=10.8028 StartZ=0 EndX=-28.8732 EndY=12.0184 EndZ=0
    g42: LineSegment StartX=-28.8732 StartY=12.0184 StartZ=0 EndX=-29.702 EndY=14.8046 EndZ=0
    g43: LineSegment StartX=-6.62474 StartY=9.21789 StartZ=0 EndX=-8.14638 EndY=11.6947 EndZ=0
    g44: LineSegment StartX=-8.14638 StartY=11.6947 StartZ=0 EndX=-6.85133 EndY=11.808 EndZ=0
    g45: LineSegment StartX=-6.85133 StartY=11.808 StartZ=0 EndX=-6.97336 EndY=13.2027 EndZ=0
    g46: LineSegment StartX=-6.97336 StartY=13.2027 StartZ=0 EndX=0 EndY=13.8128 EndZ=0
    g47: LineSegment StartX=0 StartY=13.8128 StartZ=0 EndX=6.97336 EndY=14.4228 EndZ=0
    g48: LineSegment StartX=6.97336 StartY=14.4228 StartZ=0 EndX=7.0954 EndY=13.0282 EndZ=0
    g49: LineSegment StartX=7.0954 StartY=13.0282 StartZ=0 EndX=8.39044 EndY=13.1415 EndZ=0
    g50: LineSegment StartX=8.39044 StartY=13.1415 StartZ=0 EndX=7.32199 EndY=10.4381 EndZ=0
    g51: LineSegment StartX=7.32199 StartY=10.4381 StartZ=0 EndX=0.348623 EndY=9.82798 EndZ=0
    g52: LineSegment StartX=0.348623 StartY=9.82798 StartZ=0 EndX=-6.62474 EndY=9.21789 EndZ=0
    g53: LineSegment StartX=15.5905 StartY=12.2711 StartZ=0 EndX=13.4796 EndY=14.2697 EndZ=0
    g54: LineSegment StartX=13.4796 StartY=14.2697 StartZ=0 EndX=14.7012 EndY=14.7144 EndZ=0
    g55: LineSegment StartX=14.7012 StartY=14.7144 StartZ=0 EndX=14.2224 EndY=16.0299 EndZ=0
    g56: LineSegment StartX=14.2224 StartY=16.0299 StartZ=0 EndX=20.8002 EndY=18.4241 EndZ=0
    g57: LineSegment StartX=20.8002 StartY=18.4241 StartZ=0 EndX=27.3781 EndY=20.8182 EndZ=0
    g58: LineSegment StartX=27.3781 StartY=20.8182 StartZ=0 EndX=27.8569 EndY=19.5026 EndZ=0
    g59: LineSegment StartX=27.8569 StartY=19.5026 StartZ=0 EndX=29.0785 EndY=19.9473 EndZ=0
    g60: LineSegment StartX=29.0785 StartY=19.9473 StartZ=0 EndX=28.7462 EndY=17.0594 EndZ=0
    g61: LineSegment StartX=28.7462 StartY=17.0594 StartZ=0 EndX=22.1683 EndY=14.6653 EndZ=0
    g62: LineSegment StartX=22.1683 StartY=14.6653 StartZ=0 EndX=15.5905 EndY=12.2711 EndZ=0
    g63: LineSegment StartX=33.7023 StartY=22.3542 StartZ=0 EndX=34.7672 EndY=23.0999 EndZ=0
    g64: LineSegment StartX=34.7672 StartY=23.0999 StartZ=0 EndX=33.9642 EndY=24.2467 EndZ=0
    g65: LineSegment StartX=33.9642 StartY=24.2467 StartZ=0 EndX=39.6982 EndY=28.2617 EndZ=0
    g66: LineSegment StartX=39.6982 StartY=28.2617 StartZ=0 EndX=45.4323 EndY=32.2768 EndZ=0
    g67: LineSegment StartX=45.4323 StartY=32.2768 StartZ=0 EndX=46.2353 EndY=31.13 EndZ=0
    g68: LineSegment StartX=46.2353 StartY=31.13 StartZ=0 EndX=47.3002 EndY=31.8756 EndZ=0
    g69: LineSegment StartX=47.7266 StartY=29.0002 StartZ=0 EndX=41.9925 EndY=24.9851 EndZ=0
    g70: LineSegment StartX=41.9925 StartY=24.9851 StartZ=0 EndX=36.2585 EndY=20.9701 EndZ=0
    g71: LineSegment StartX=-49.6388 StartY=20.4818 StartZ=0 EndX=-43.2946 EndY=17.5235 EndZ=0
    g72: LineSegment StartX=-43.2946 StartY=17.5235 StartZ=0 EndX=-36.9505 EndY=14.5651 EndZ=0
    g73: LineSegment StartX=48.7915 StartY=29.7458 StartZ=0 EndX=47.7266 EndY=29.0002 EndZ=0
    g74: LineSegment StartX=36.2585 StartY=20.9701 StartZ=0 EndX=35.1936 EndY=20.2244 EndZ=0
    g75: LineSegment StartX=47.3002 StartY=31.8756 StartZ=0 EndX=47.7266 EndY=29.0002 EndZ=0
    g76: LineSegment StartX=33.7023 StartY=22.3542 StartZ=0 EndX=36.2585 EndY=20.9701 EndZ=0
    g77: LineSegment StartX=29.9678 StartY=17.5041 StartZ=0 EndX=28.7462 EndY=17.0594 EndZ=0
    g78: LineSegment StartX=15.5905 StartY=12.2711 StartZ=0 EndX=14.3689 EndY=11.8265 EndZ=0
    g79: LineSegment StartX=-6.62474 StartY=9.21789 StartZ=0 EndX=-7.91979 EndY=9.10459 EndZ=0
    g80: LineSegment StartX=7.32199 StartY=10.4381 StartZ=0 EndX=8.61704 EndY=10.5514 EndZ=0
    g81: LineSegment StartX=-30.1535 StartY=12.2441 StartZ=0 EndX=-28.8732 EndY=12.0184 EndZ=0
    g82: LineSegment StartX=-15.0859 StartY=9.58731 StartZ=0 EndX=-13.8057 EndY=9.36157 EndZ=0
    g83: LineSegment StartX=-50.817 StartY=21.0312 StartZ=0 EndX=-49.6388 EndY=20.4818 EndZ=0
    g84: LineSegment StartX=-36.9505 StartY=14.5651 StartZ=0 EndX=-35.7723 EndY=14.0157 EndZ=0
  constraints (235):
    c: PointOnObject(g0,g-3)
    c: PointOnObject(g0,g-5)
    c: PointOnObject(g1,g-5)
    c: PointOnObject(g1,g-3)
    c: Coincident(g2,g-4)
    c: PointOnObject(g2,g-5)
    c: PointOnObject(g3,g-4)
    c: PointOnObject(g3,g-5)
    c: PointOnObject(g4,g-5)
    c: PointOnObject(g4,g-4)
    c: PointOnObject(g5,g-6)
    c: PointOnObject(g5,g-8)
    c: PointOnObject(g6,g-8)
    c: PointOnObject(g6,g-6)
    c: Coincident(g7,g-7)
    c: PointOnObject(g7,g-8)
    c: PointOnObject(g8,g-8)
    c: PointOnObject(g8,g-7)
    c: PointOnObject(g9,g-7)
    c: PointOnObject(g9,g-8)
    c: PointOnObject(g10,g-9)
    c: PointOnObject(g10,g-11)
    c: PointOnObject(g11,g-11)
    c: PointOnObject(g11,g-9)
    c: Coincident(g12,g-10)
    c: PointOnObject(g12,g-11)
    c: PointOnObject(g13,g-11)
    c: PointOnObject(g13,g-10)
    c: PointOnObject(g14,g-10)
    c: PointOnObject(g14,g-11)
    c: PointOnObject(g15,g-12)
    c: PointOnObject(g15,g-14)
    c: PointOnObject(g16,g-14)
    c: PointOnObject(g16,g-12)
    c: Coincident(g17,g-14)
    c: PointOnObject(g17,g-12)
    c: PointOnObject(g18,g-12)
    c: PointOnObject(g18,g-13)
    c: PointOnObject(g19,g-13)
    c: PointOnObject(g19,g-12)
    c: PointOnObject(g20,g-17)
    c: PointOnObject(g20,g-15)
    c: PointOnObject(g21,g-15)
    c: PointOnObject(g21,g-17)
    c: Coincident(g22,g-16)
    c: PointOnObject(g22,g-17)
    c: PointOnObject(g23,g-16)
    c: PointOnObject(g23,g-17)
    c: PointOnObject(g24,g-17)
    c: PointOnObject(g24,g-16)
    c: Perpendicular(g-16,g23)
    c: Perpendicular(g-15,g22)
    c: Perpendicular(g-15,g21)
    c: Perpendicular(g-17,g20)
    c: Perpendicular(g-12,g19)
    c: Perpendicular(g-13,g18)
    c: Perpendicular(g-14,g17)
    c: Perpendicular(g-14,g16)
    c: Perpendicular(g-12,g15)
    c: Perpendicular(g-11,g14)
    c: Perpendicular(g-10,g13)
    c: Perpendicular(g-9,g12)
    c: Perpendicular(g-9,g11)
    c: Perpendicular(g-11,g10)
    c: Perpendicular(g-8,g9)
    c: Perpendicular(g-7,g8)
    c: Perpendicular(g-6,g7)
    c: Perpendicular(g-6,g6)
    c: Perpendicular(g-8,g5)
    c: Perpendicular(g-5,g4)
    c: Perpendicular(g-4,g3)
    c: Perpendicular(g-3,g2)
    c: Perpendicular(g-5,g0)
    c: Perpendicular(g-3,g1)
    c: Coincident(g1,g25)
    c: Coincident(g25,g2)
    c: Coincident(g25,g26)
    c: Coincident(g26,g3)
    c: Coincident(g26,g27)
    c: Coincident(g27,g28)
    c: Coincident(g28,g29)
    c: Coincident(g30,g31)
    c: Coincident(g31,g32)
    c: Coincident(g32,g25)
    c: Coincident(g33,g34)
    c: Coincident(g34,g6)
    c: Coincident(g34,g35)
    c: Coincident(g35,g7)
    c: Coincident(g35,g36)
    c: Coincident(g36,g8)
    c: Coincident(g36,g37)
    c: Coincident(g37,g38)
    c: Coincident(g38,g39)
    c: Coincident(g40,g7)
    c: Coincident(g40,g41)
    c: Coincident(g42,g33)
    c: Coincident(g43,g44)
    c: Coincident(g44,g45)
    c: Coincident(g45,g11)
    c: Coincident(g45,g46)
    c: Coincident(g46,g12)
    c: Coincident(g46,g47)
    c: Coincident(g47,g13)
    c: Coincident(g47,g48)
    c: Coincident(g48,g49)
    c: Coincident(g49,g50)
    c: Coincident(g51,g12)
    c: Coincident(g51,g52)
    c: Coincident(g53,g54)
    c: Coincident(g54,g55)
    c: Coincident(g55,g16)
    c: Coincident(g55,g56)
    c: Coincident(g56,g17)
    c: Coincident(g56,g57)
    c: Coincident(g57,g18)
    c: Coincident(g57,g58)
    c: Coincident(g58,g59)
    c: Coincident(g59,g60)
    c: Coincident(g61,g17)
    c: Coincident(g61,g62)
    c: Coincident(g63,g64)
    c: Coincident(g64,g21)
    c: Coincident(g64,g65)
    c: Coincident(g65,g22)
    c: Coincident(g65,g66)
    c: Coincident(g66,g23)
    c: Coincident(g66,g67)
    c: Coincident(g67,g68)
    c: Coincident(g69,g22)
    c: Coincident(g69,g70)
    c: Distance(g67) = 1.4
    c: Distance(g64) = 1.4
    c: Distance(g58) = 1.4
    c: Distance(g55) = 1.4
    c: Distance(g48) = 1.4
    c: Distance(g45) = 1.4
    c: Distance(g37) = 1.4
    c: Distance(g34) = 1.4
    c: Distance(g27) = 1.4
    c: Distance(g32) = 1.4
    c: Distance(g25,g26) = 14
    c: Distance(g34,g36) = 14
    c: Distance(g45,g47) = 14
    c: Distance(g55,g57) = 14
    c: Distance(g64,g66) = 14
    c: Equal(g25,g26)
    c: Equal(g35,g36)
    c: Equal(g46,g47)
    c: Equal(g56,g57)
    c: Equal(g65,g66)
    c: Coincident(g71,g2)
    c: Coincident(g71,g72)
    c: Distance(g30,g0) = 1.4
    c: Distance(g28,g4) = 1.4
    c: Distance(g33,g5) = 1.4
    c: Distance(g38,g9) = 1.4
    c: Distance(g43,g10) = 1.4
    c: Distance(g49,g14) = 1.4
    c: Distance(g53,g15) = 1.4
    c: Distance(g59,g19) = 1.4
    c: Distance(g63,g20) = 1.4
    c: Distance(g68,g24) = 1.4
    c: Distance(g24,g20) = 16.6
    c: Distance(g63,g21) = 2.6
    c: Distance(g63,g20) = 2.6
    c: Coincident(g73,g24)
    c: Coincident(g73,g69)
    c: Coincident(g74,g70)
    c: Coincident(g74,g20)
    c: Equal(g74,g73)
    c: Coincident(g70,g21)
    c: Perpendicular(g-17,g24)
    c: Coincident(g69,g23)
    c: Coincident(g75,g68)
    c: Coincident(g75,g69)
    c: Distance(g68,g24) = 2.6
    c: Distance(g67,g69) = 2.6
    c: Coincident(g76,g63)
    c: Coincident(g76,g70)
    c: Distance(g54,g16) = 2.6
    c: Distance(g58,g18) = 2.6
    c: Coincident(g61,g18)
    c: Coincident(g62,g16)
    c: Coincident(g77,g19)
    c: Coincident(g77,g61)
    c: Coincident(g78,g62)
    c: Coincident(g78,g15)
    c: Coincident(g60,g61)
    c: Distance(g59,g19) = 2.6
    c: Coincident(g53,g62)
    c: Equal(g78,g77)
    c: Distance(g15,g19) = 16.6
    c: Distance(g15,g53) = 2.6
    c: Coincident(g52,g43)
    c: Coincident(g52,g11)
    c: Coincident(g50,g13)
    c: Coincident(g50,g51)
    c: Distance(g49,g14) = 2.6
    c: Distance(g48,g50) = 2.6
    c: Distance(g14,g10) = 16.6
    c: Coincident(g79,g43)
    c: Coincident(g79,g10)
    c: Coincident(g80,g50)
    c: Coincident(g80,g14)
    c: Equal(g80,g79)
    c: Distance(g44,g43) = 2.6
    c: Distance(g43,g10) = 2.6
    c: Coincident(g8,g40)
    c: Coincident(g8,g39)
    c: Coincident(g41,g6)
    c: Coincident(g41,g42)
    c: Coincident(g81,g5)
    c: Coincident(g81,g41)
    c: Coincident(g82,g39)
    c: Coincident(g82,g9)
    c: Equal(g81,g82)
    c: Distance(g5,g9) = 16.6
    c: Distance(g38,g9) = 2.6
    c: Distance(g37,g39) = 2.6
    c: Distance(g33,g41) = 2.6
    c: Distance(g33,g5) = 2.6
    c: Coincident(g71,g1)
    c: Coincident(g71,g30)
    c: Coincident(g3,g72)
    c: Coincident(g3,g29)
    c: Coincident(g83,g0)
    c: Coincident(g83,g30)
    c: Coincident(g84,g29)
    c: Coincident(g84,g4)
    c: Distance(g30,g0) = 2.6
    c: Distance(g31,g30) = 2.6
    c: Distance(g0,g4) = 16.6
    c: Distance(g4,g28) = 2.6
    c: Distance(g27,g29) = 2.6
    c: Equal(g84,g83)
FEATURE [PartDesign::Pocket] Pocket002  label="PMX Sockets"
  BaseFeature = -> Pad004
  Direction = (-1,2e-16,-3e-16)
  Length = 14
  Length2 = 100
  Midplane = true
  Placement = pos=(0,0,0) rot=(0.57735,0.57735,0.57735;2.0944rad)
  Profile = -> Sketch007
  Type = 0
FEATURE [Sketcher::SketchObject] Sketch008
  ExternalGeometry = -> [Sketch007]
  FullyConstrained = true
  MapMode = 5
  Placement = pos=(0,0,0) rot=(0.57735,0.57735,0.57735;2.0944rad)
  Support = -> [YZ_Plane001]
  sketch-geometry (20):
    g0: LineSegment StartX=-35.7672 StartY=17.1028 StartZ=0 EndX=-36.1898 EndY=16.1965 EndZ=0
    g1: LineSegment StartX=-36.1898 StartY=16.1965 StartZ=0 EndX=-48.8781 EndY=22.1132 EndZ=0
    g2: LineSegment StartX=-48.8781 StartY=22.1132 StartZ=0 EndX=-48.4555 EndY=23.0195 EndZ=0
    g3: LineSegment StartX=-48.4555 StartY=23.0195 StartZ=0 EndX=-35.7672 EndY=17.1028 EndZ=0
    g4: LineSegment StartX=-28.387 StartY=14.7758 StartZ=0 EndX=-28.5607 EndY=13.791 EndZ=0
    g5: LineSegment StartX=-28.5607 StartY=13.791 StartZ=0 EndX=-14.7734 EndY=11.36 EndZ=0
    g6: LineSegment StartX=-14.7734 StartY=11.36 StartZ=0 EndX=-14.5997 EndY=12.3448 EndZ=0
    g7: LineSegment StartX=-14.5997 StartY=12.3448 StartZ=0 EndX=-28.387 EndY=14.7758 EndZ=0
    g8: LineSegment StartX=-6.86876 StartY=12.0072 StartZ=0 EndX=-6.78161 EndY=11.011 EndZ=0
    g9: LineSegment StartX=-6.78161 StartY=11.011 StartZ=0 EndX=7.16511 EndY=12.2312 EndZ=0
    g10: LineSegment StartX=7.16511 StartY=12.2312 StartZ=0 EndX=7.07796 EndY=13.2274 EndZ=0
    g11: LineSegment StartX=7.07796 StartY=13.2274 StartZ=0 EndX=-6.86876 EndY=12.0072 EndZ=0
    g12: LineSegment StartX=14.6328 StartY=14.9023 StartZ=0 EndX=14.9748 EndY=13.9626 EndZ=0
    g13: LineSegment StartX=14.9748 StartY=13.9626 StartZ=0 EndX=28.1305 EndY=18.7509 EndZ=0
    g14: LineSegment StartX=28.1305 StartY=18.7509 StartZ=0 EndX=27.7885 EndY=19.6906 EndZ=0
    g15: LineSegment StartX=27.7885 StartY=19.6906 StartZ=0 EndX=14.6328 EndY=14.9023 EndZ=0
    g16: LineSegment StartX=34.6525 StartY=23.2637 StartZ=0 EndX=35.226 EndY=22.4446 EndZ=0
    g17: LineSegment StartX=35.226 StartY=22.4446 StartZ=0 EndX=46.6942 EndY=30.4746 EndZ=0
    g18: LineSegment StartX=46.6942 StartY=30.4746 StartZ=0 EndX=46.1206 EndY=31.2938 EndZ=0
    g19: LineSegment StartX=46.1206 StartY=31.2938 StartZ=0 EndX=34.6525 EndY=23.2637 EndZ=0
  constraints (60):
    c: Coincident(g0,g1)
    c: Coincident(g2,g1)
    c: Distance(g0,g-20) = 1.8
    c: Distance(g1,g-19) = 1.8
    c: Distance(g-22,g2) = 0.2
    c: Distance(g2,g-22) = 1.2
    c: Distance(g-22,g1) = 0.8
    c: Distance(g-21,g0) = 0.2
    c: Distance(g-21,g0) = 0.8
    c: Distance(g0,g-21) = 1.2
    c: Coincident(g3,g2)
    c: Coincident(g3,g0)
    c: Coincident(g4,g5)
    c: Coincident(g5,g6)
    c: Coincident(g6,g7)
    c: Coincident(g7,g4)
    c: Coincident(g8,g9)
    c: Coincident(g9,g10)
    c: Coincident(g10,g11)
    c: Coincident(g11,g8)
    c: Coincident(g12,g13)
    c: Coincident(g13,g14)
    c: Coincident(g14,g15)
    c: Coincident(g15,g12)
    c: Coincident(g16,g17)
    c: Coincident(g17,g18)
    c: Coincident(g18,g19)
    c: Coincident(g19,g16)
    c: Distance(g-6,g4) = 0.2
    c: Distance(g-6,g4) = 1.2
    c: Distance(g4,g-5) = 1.8
    c: Distance(g4,g-6) = 0.8
    c: Distance(g6,g-3) = 1.2
    c: Distance(g6,g-3) = 0.2
    c: Distance(g5,g-4) = 1.8
    c: Distance(g-3,g5) = 0.8
    c: Distance(g8,g-10) = 1.2
    c: Distance(g8,g-10) = 0.2
    c: Distance(g8,g-9) = 1.8
    c: Distance(g8,g-10) = 0.8
    c: Distance(g10,g-7) = 1.2
    c: Distance(g10,g-7) = 0.2
    c: Distance(g9,g-8) = 1.8
    c: Distance(g-7,g9) = 0.8
    c: Distance(g12,g-12) = 1.2
    c: Distance(g12,g-12) = 0.2
    c: Distance(g12,g-13) = 1.8
    c: Distance(g12,g-12) = 0.8
    c: Distance(g14,g-11) = 1.2
    c: Distance(g14,g-11) = 0.2
    c: Distance(g13,g-14) = 1.8
    c: Distance(g13,g-11) = 0.8
    c: Distance(g18,g-17) = 0.2
    c: Distance(g17,g-17) = 0.8
    c: Distance(g17,g-18) = 1.8
    c: Distance(g18,g-17) = 1.2
    c: Distance(g-15,g16) = 1.8
    c: Distance(g16,g-16) = 0.8
    c: Distance(g16,g-16) = 0.2
    c: Distance(g16,g-16) = 1.2
FEATURE [PartDesign::Pocket] Pocket003  label="PChoc Sockets"
  BaseFeature = -> Pocket002
  Direction = (-1,2e-16,-3e-16)
  Length = 14.6
  Length2 = 100
  Midplane = true
  Placement = pos=(0,0,0) rot=(0.57735,0.57735,0.57735;2.0944rad)
  Profile = -> Sketch008
  Type = 0
FEATURE [Sketcher::SketchObject] Sketch009
  ExternalGeometry = -> [Sketch006]
  FullyConstrained = true
  MapMode = 5
  Placement = pos=(0,0,0) rot=(0.57735,0.57735,0.57735;2.0944rad)
  Support = -> [YZ_Plane001]
  expr: Constraints[24] = <<Spreadsheet>>.Wiring
  expr: Constraints[25] = <<Spreadsheet>>.Wiring
  expr: Constraints[26] = <<Spreadsheet>>.Wiring
  expr: Constraints[27] = <<Spreadsheet>>.Wiring
  sketch-geometry (12):
    g0: LineSegment StartX=-11.9293 StartY=13.0924 StartZ=0 EndX=-9.46385 EndY=12.9848 EndZ=0
    g1: LineSegment StartX=-9.46385 StartY=12.9848 StartZ=0 EndX=-8.59231 EndY=3.02283 EndZ=0
    g2: LineSegment StartX=-8.59231 StartY=3.02283 StartZ=0 EndX=-8.59231 EndY=0 EndZ=0
    g3: LineSegment StartX=-8.59231 StartY=0 StartZ=0 EndX=-13.6658 EndY=0 EndZ=0
    g4: LineSegment StartX=-13.6658 StartY=0 StartZ=0 EndX=-13.6658 EndY=3.24435 EndZ=0
    g5: LineSegment StartX=-13.6658 StartY=3.24435 StartZ=0 EndX=-11.9293 EndY=13.0924 EndZ=0
    g6: LineSegment StartX=9.46385 StartY=14.6407 StartZ=0 EndX=11.8732 EndY=15.1749 EndZ=0
    g7: LineSegment StartX=11.8732 StartY=15.1749 StartZ=0 EndX=15.2933 EndY=5.77794 EndZ=0
    g8: LineSegment StartX=15.2933 StartY=5.77794 StartZ=0 EndX=15.2933 EndY=0 EndZ=0
    g9: LineSegment StartX=15.2933 StartY=0 StartZ=0 EndX=10.3354 EndY=0 EndZ=0
    g10: LineSegment StartX=10.3354 StartY=0 StartZ=0 EndX=10.3354 EndY=4.67879 EndZ=0
    g11: LineSegment StartX=10.3354 StartY=4.67879 StartZ=0 EndX=9.46385 EndY=14.6407 EndZ=0
  constraints (32):
    c: Coincident(g0,g-6)
    c: Coincident(g0,g-6)
    c: Coincident(g0,g1)
    c: Coincident(g1,g2)
    c: PointOnObject(g2,g-1)
    c: Vertical(g2)
    c: Coincident(g2,g3)
    c: Horizontal(g3)
    c: Coincident(g3,g4)
    c: Vertical(g4)
    c: Coincident(g4,g5)
    c: Coincident(g5,g0)
    c: Coincident(g-4,g6)
    c: Coincident(g6,g-4)
    c: Coincident(g6,g7)
    c: Coincident(g7,g8)
    c: PointOnObject(g8,g-1)
    c: Vertical(g8)
    c: Coincident(g8,g9)
    c: Horizontal(g9)
    c: Coincident(g9,g10)
    c: Vertical(g10)
    c: Coincident(g10,g11)
    c: Coincident(g11,g6)
    c: Distance(g-3,g7) = 6
    c: Distance(g-3,g10) = 6
    c: Distance(g-5,g1) = 6
    c: Distance(g-5,g4) = 6
    c: Equal(g5,g1)
    c: Equal(g1,g11)
    c: Equal(g11,g7)
    c: Distance(g5) = 10
FEATURE [PartDesign::Pad] Pad005  label="PInner Legs"
  BaseFeature = -> Pocket003
  Direction = (1,-2e-16,3e-16)
  Length = 4.1
  Length2 = 9.5
  Placement = pos=(0,0,0) rot=(0.57735,0.57735,0.57735;2.0944rad)
  Profile = -> Sketch009
  Type = 4
  expr: Length = <<Spreadsheet>>.ScrewD / 2 + 2mm
FEATURE [Sketcher::SketchObject] Sketch010
  ExternalGeometry = -> [Sketch006]
  FullyConstrained = true
  MapMode = 5
  Placement = pos=(0,0,0) rot=(0.57735,0.57735,0.57735;2.0944rad)
  Support = -> [YZ_Plane001]
  expr: Constraints[11] = <<Spreadsheet>>.Wiring + 4mm
  expr: Constraints[12] = <<Spreadsheet>>.Wiring
  expr: Constraints[13] = <<Spreadsheet>>.Wiring
  expr: Constraints[14] = <<Spreadsheet>>.Wiring
  expr: Constraints[15] = <<Spreadsheet>>.Wiring
  expr: Constraints[76] = <<Spreadsheet>>.ArchLength
  expr: Constraints[77] = <<Spreadsheet>>.ArchLength
  expr: Constraints[78] = <<Spreadsheet>>.ArchLength * 2 - 10mm
  sketch-geometry (32):
    g0: LineSegment StartX=-37.2205 StartY=8.07076 StartZ=0 EndX=-32.9942 EndY=17.1338 EndZ=0
    g1: LineSegment StartX=-32.9942 StartY=17.1338 StartZ=0 EndX=-30.6407 EndY=16.3917 EndZ=0
    g2: LineSegment StartX=-30.6407 StartY=16.3917 StartZ=0 EndX=-32.3772 EndY=6.54366 EndZ=0
    g3: LineSegment StartX=33.1475 StartY=12.2763 StartZ=0 EndX=29.7273 EndY=21.6733 EndZ=0
    g4: LineSegment StartX=29.7273 StartY=21.6733 StartZ=0 EndX=31.9163 EndY=22.8128 EndZ=0
    g5: LineSegment StartX=31.9163 StartY=22.8128 StartZ=0 EndX=37.6521 EndY=14.6212 EndZ=0
    g6: LineSegment StartX=37.6521 StartY=14.6212 StartZ=0 EndX=42.2621 EndY=8.03739 EndZ=0
    g7: LineSegment StartX=42.2621 StartY=8.03739 StartZ=0 EndX=42.2621 EndY=0 EndZ=0
    g8: LineSegment StartX=-37.2205 StartY=8.07076 StartZ=0 EndX=-39.0097 EndY=4.23371 EndZ=0
    g9: LineSegment StartX=-39.0097 StartY=4.23371 StartZ=0 EndX=-39.0097 EndY=0 EndZ=0
    g10: LineSegment StartX=-32.3772 StartY=6.54366 StartZ=0 EndX=-35 EndY=0 EndZ=0
    g11: LineSegment StartX=-35 StartY=0 StartZ=0 EndX=-45 EndY=0 EndZ=0
    g12: LineSegment StartX=-45 StartY=0 StartZ=0 EndX=-45 EndY=3 EndZ=0
    g13: LineSegment StartX=-45 StartY=3 StartZ=0 EndX=-40 EndY=3 EndZ=0
    g14-g17: Circle x4 (B-spline internal-alignment scaffolding for g18; pole/knot coordinates omitted)
    g18: BSplineCurve PolesCount=4 KnotsCount=2 Degree=3 IsPeriodic=0
    g19: GeomPoint X=-37.2205 Y=8.07076 Z=0
    g20: GeomPoint X=-45 Y=3 Z=0
    g21: LineSegment StartX=33.1475 StartY=12.2763 StartZ=0 EndX=35 EndY=0 EndZ=0
    g22: LineSegment StartX=35 StartY=0 StartZ=0 EndX=45 EndY=0 EndZ=0
    g23: LineSegment StartX=45 StartY=0 StartZ=0 EndX=45 EndY=3 EndZ=0
    g24: LineSegment StartX=45 StartY=3 StartZ=0 EndX=40 EndY=3 EndZ=0
    g25-g28: Circle x4 (B-spline internal-alignment scaffolding for g29; pole/knot coordinates omitted)
    g29: BSplineCurve PolesCount=4 KnotsCount=2 Degree=3 IsPeriodic=0
    g30: GeomPoint X=37.6521 Y=14.6212 Z=0
    g31: GeomPoint X=45 Y=3 Z=0
  constraints (74):
    c: Coincident(g0,g-5)
    c: Coincident(g0,g1)
    c: Coincident(g1,g-5)
    c: Coincident(g1,g2)
    c: Coincident(g3,g-4)
    c: Coincident(g3,g4)
    c: Coincident(g4,g-4)
    c: Coincident(g4,g5)
    c: Equal(g2,g0)
    c: Equal(g0,g3)
    c: Equal(g3,g5)
    c: Distance(g0) = 10
    c: Distance(g-6,g0) = 6
    c: Distance(g-6,g2) = 6
    c: Distance(g-3,g3) = 6
    c: Distance(g-3,g5) = 6
    c: Coincident(g5,g6)
    c: Coincident(g6,g7)
    c: Vertical(g7)
    c: Coincident(g0,g8)
    c: Coincident(g8,g9)
    c: Vertical(g9)
    c: Parallel(g6,g5)
    c: Parallel(g0,g8)
    c: Equal(g8,g9)
    c: Equal(g7,g6)
    c: PointOnObject(g7,g-1)
    c: PointOnObject(g9,g-1)
    c: Coincident(g2,g10)
    c: PointOnObject(g10,g-1)
    c: Coincident(g10,g11)
    c: PointOnObject(g11,g-1)
    c: Coincident(g11,g12)
    c: Vertical(g12)
    c: Coincident(g13,g12)
    c: Horizontal(g13)
    c: DistanceY(g12,g12) = 3
    c: Coincident(g18,g0)
    c: Weight(g14) = 1
    c: Equal(g14,g15)
    c: Coincident(g15,g8)
    c: Equal(g14,g16)
    c: Coincident(g16,g13)
    c: Equal(g14,g17)
    c: Coincident(g18,g12)
    c: InternalAlignment(g14-g17 -> g18) x4
    c: InternalAlignment(g19,g18)
    c: InternalAlignment(g20,g18)
    c: Coincident(g3,g21)
    c: PointOnObject(g21,g-1)
    c: Coincident(g21,g22)
    c: Horizontal(g22)
    c: Coincident(g22,g23)
    c: Vertical(g23)
    c: DistanceY(g23,g23) = 3
    c: Coincident(g24,g23)
    c: Horizontal(g24)
    c: Coincident(g29,g5)
    c: Weight(g25) = 1
    c: Equal(g25,g26)
    c: Coincident(g26,g6)
    c: Equal(g25,g27)
    c: Coincident(g27,g24)
    c: Equal(g25,g28)
    c: Coincident(g29,g23)
    c: InternalAlignment(g25-g28 -> g29) x4
    c: InternalAlignment(g30,g29)
    c: InternalAlignment(g31,g29)
    c: Equal(g22,g11)
    c: DistanceX(g11,g11) = 10
    c: DistanceX(g-7,g22) = 45
    c: DistanceX(g11,g-7) = 45
    c: DistanceX(g13,g24) = 80
    c: Equal(g24,g13)
FEATURE [PartDesign::Pad] Pad006  label="POuter Legs"
  BaseFeature = -> Pad005
  Direction = (1,-2e-16,3e-16)
  Length = 9.5
  Length2 = 100
  Placement = pos=(0,0,0) rot=(0.57735,0.57735,0.57735;2.0944rad)
  Profile = -> Sketch010
  Reversed = true
  Type = 0
FEATURE [Sketcher::SketchObject] Sketch011
  ExternalGeometry = -> [Sketch010]
  FullyConstrained = true
  MapMode = 5
  Support = -> [XY_Plane001]
  expr: Constraints[25] = <<Spreadsheet>>.NutR
  expr: Constraints[26] = <<Spreadsheet>>.NutR
  expr: Constraints[27] = <<Spreadsheet>>.ScrewD
  expr: Constraints[40] = <<Spreadsheet>>.ScrewD
  expr: Constraints[54] = <<Spreadsheet>>.NutR
  expr: Constraints[55] = <<Spreadsheet>>.NutR
  sketch-geometry (22):
    g0: LineSegment StartX=9.8e-15 StartY=45 StartZ=0 EndX=-9.5 EndY=45 EndZ=0
    g1: LineSegment StartX=-9.5 StartY=45 StartZ=0 EndX=-9.5 EndY=55 EndZ=0
    g2: LineSegment StartX=-9.5 StartY=55 StartZ=0 EndX=4.5 EndY=55 EndZ=0
    g3: ArcOfCircle CenterX=4.5 CenterY=50 CenterZ=0 NormalX=0 NormalY=0 NormalZ=1 AngleXU=0 Radius=5 StartAngle=5.38688 EndAngle=7.85398
    g4: LineSegment StartX=7.6225 StartY=46.0949 StartZ=0 EndX=9.8e-15 EndY=40 EndZ=0
    g5: LineSegment StartX=9.8e-15 StartY=40 StartZ=0 EndX=9.8e-15 EndY=45 EndZ=0
    g6: Circle CenterX=0 CenterY=50 CenterZ=0 NormalX=0 NormalY=0 NormalZ=1 AngleXU=0 Radius=2.1
    g7: LineSegment StartX=0 StartY=50 StartZ=0 EndX=4.5 EndY=50 EndZ=0
    g8: LineSegment StartX=9.5 StartY=50 StartZ=0 EndX=9.5 EndY=55 EndZ=0
    g9: LineSegment StartX=-9.5 StartY=55 StartZ=0 EndX=0 EndY=50 EndZ=0
    g10: LineSegment StartX=0 StartY=50 StartZ=0 EndX=9.5 EndY=55 EndZ=0
    g11: LineSegment StartX=-9.8e-15 StartY=-40 StartZ=0 EndX=-9.8e-15 EndY=-45 EndZ=0
    g12: LineSegment StartX=-9.8e-15 StartY=-45 StartZ=0 EndX=-9.5 EndY=-45 EndZ=0
    g13: LineSegment StartX=-9.5 StartY=-45 StartZ=0 EndX=-9.5 EndY=-55 EndZ=0
    g14: LineSegment StartX=-9.5 StartY=-55 StartZ=0 EndX=4.5 EndY=-55 EndZ=0
    g15: ArcOfCircle CenterX=4.5 CenterY=-50 CenterZ=0 NormalX=0 NormalY=0 NormalZ=1 AngleXU=0 Radius=5 StartAngle=4.71239 EndAngle=7.17949
    g16: LineSegment StartX=7.6225 StartY=-46.0949 StartZ=0 EndX=-9.8e-15 EndY=-40 EndZ=0
    g17: Circle CenterX=0 CenterY=-50 CenterZ=0 NormalX=0 NormalY=0 NormalZ=1 AngleXU=0 Radius=2.1
    g18: LineSegment StartX=9.5 StartY=-50 StartZ=0 EndX=9.5 EndY=-55 EndZ=0
    g19: LineSegment StartX=9.5 StartY=-55 StartZ=0 EndX=0 EndY=-50 EndZ=0
    g20: LineSegment StartX=0 StartY=-50 StartZ=0 EndX=-9.5 EndY=-55 EndZ=0
    g21: LineSegment StartX=0 StartY=-50 StartZ=0 EndX=4.5 EndY=-50 EndZ=0
  constraints (58):
    c: Coincident(g0,g-3)
    c: Horizontal(g0)
    c: Coincident(g0,g1)
    c: Vertical(g1)
    c: Coincident(g1,g2)
    c: Horizontal(g2)
    c: Tangent(g2,g3) = 1.5708
    c: Tangent(g3,g4) = 1.5708
    c: Coincident(g4,g5)
    c: Coincident(g5,g0)
    c: Vertical(g5)
    c: PointOnObject(g6,g-2)
    c: Coincident(g7,g6)
    c: Coincident(g7,g3)
    c: PointOnObject(g8,g3)
    c: Vertical(g8)
    c: Horizontal(g2,g8)
    c: Coincident(g1,g9)
    c: Coincident(g9,g7)
    c: Coincident(g9,g10)
    c: Coincident(g10,g8)
    c: Horizontal(g7)
    c: Equal(g10,g9)
    c: DistanceX(g9,g8) = 19
    c: DistanceY(g5,g5) = 5
    c: DistanceY(g7,g9) = 5
    c: DistanceY(g0,g7) = 5
    c: Diameter(g6) = 4.2
    c: Tangent(g8,g3)
    c: Vertical(g11)
    c: Coincident(g11,g12)
    c: Horizontal(g12)
    c: Coincident(g12,g13)
    c: Vertical(g13)
    c: Coincident(g13,g14)
    c: Horizontal(g14)
    c: Tangent(g14,g15) = -1.5708
    c: Tangent(g15,g16) = -1.5708
    c: DistanceY(g11,g11) = 5
    c: PointOnObject(g17,g-2)
    c: Diameter(g17) = 4.2
    c: PointOnObject(g18,g15)
    c: Vertical(g18)
    c: Tangent(g18,g15)
    c: Coincident(g18,g19)
    c: Coincident(g19,g17)
    c: Coincident(g19,g20)
    c: Coincident(g20,g13)
    c: DistanceX(g20,g18) = 19
    c: Equal(g19,g20)
    c: Horizontal(g18,g14)
    c: Coincident(g21,g19)
    c: Coincident(g21,g15)
    c: Horizontal(g21)
    c: DistanceY(g20,g19) = 5
    c: DistanceY(g19,g12) = 5
    c: Coincident(g16,g11)
    c: Coincident(g11,g-4)
FEATURE [PartDesign::Pad] Pad007  label="PFeet"
  BaseFeature = -> Pad006
  Direction = (0,0,1)
  Length = 3
  Length2 = 100
  Placement = pos=(0,0,0) rot=(0.57735,0.57735,0.57735;2.0944rad)
  Profile = -> Sketch011
  Type = 0
FEATURE [PartDesign::Body] Body001  label="PinkieArch"
  Group = -> [Sketch006,Pad004,Sketch007,Pocket002,Sketch008,Pocket003,Sketch009,Pad005,Sketch010,Pad006,Sketch011,Pad007]
  Origin = -> Origin001
  Placement = pos=(30,-10,15) rot=(0,0,1;0rad)
  Tip = -> Pad007
  expr: .Placement.Base.y = <<OuterArch>>.Placement.Base.y
  expr: .Placement.Base.z = <<OuterArch>>.Placement.Base.z
FEATURE [Sketcher::SketchObject] Sketch012
  FullyConstrained = true
  MapMode = 5
  Placement = pos=(0,0,0) rot=(0.57735,0.57735,0.57735;2.0944rad)
  Support = -> [YZ_Plane002]
  expr: Constraints[147] = <<Spreadsheet>>.ModRowKey
  expr: Constraints[148] = <<Spreadsheet>>.ZRowKey
  expr: Constraints[149] = <<Spreadsheet>>.ARowKey
  expr: Constraints[150] = <<Spreadsheet>>.QRowKey
  expr: Constraints[151] = <<Spreadsheet>>.TopRowKey
  expr: Constraints[161] = <<Spreadsheet>>.Wiring
  sketch-geometry (61):
    g0: LineSegment StartX=-50.2141 StartY=25.1636 StartZ=0 EndX=-41.6042 EndY=21.1487 EndZ=0
    g1: LineSegment StartX=-41.6042 StartY=21.1487 StartZ=0 EndX=-32.9942 EndY=17.1338 EndZ=0
    g2: LineSegment StartX=-32.9942 StartY=17.1338 StartZ=0 EndX=-30.6407 EndY=16.3917 EndZ=0
    g3: LineSegment StartX=-30.6407 StartY=16.3917 StartZ=0 EndX=-21.285 EndY=14.7421 EndZ=0
    g4: LineSegment StartX=-21.285 StartY=14.7421 StartZ=0 EndX=-11.9293 EndY=13.0924 EndZ=0
    g5: LineSegment StartX=-11.9293 StartY=13.0924 StartZ=0 EndX=-9.46385 EndY=12.9848 EndZ=0
    g6: LineSegment StartX=-9.46385 StartY=12.9848 StartZ=0 EndX=0 EndY=13.8128 EndZ=0
    g7: LineSegment StartX=0 StartY=13.8128 StartZ=0 EndX=9.46385 EndY=14.6407 EndZ=0
    g8: LineSegment StartX=9.46385 StartY=14.6407 StartZ=0 EndX=11.8732 EndY=15.1749 EndZ=0
    g9: LineSegment StartX=11.8732 StartY=15.1749 StartZ=0 EndX=20.8002 EndY=18.4241 EndZ=0
    g10: LineSegment StartX=20.8002 StartY=18.4241 StartZ=0 EndX=29.7273 EndY=21.6733 EndZ=0
    g11: LineSegment StartX=29.7273 StartY=21.6733 StartZ=0 EndX=31.9163 EndY=22.8128 EndZ=0
    g12: LineSegment StartX=31.9163 StartY=22.8128 StartZ=0 EndX=39.6982 EndY=28.2617 EndZ=0
    g13: LineSegment StartX=39.6982 StartY=28.2617 StartZ=0 EndX=47.4802 EndY=33.7107 EndZ=0
    g14: LineSegment StartX=47.4802 StartY=33.7107 StartZ=0 EndX=49.7745 EndY=30.4341 EndZ=0
    g15: LineSegment StartX=49.7745 StartY=30.4341 StartZ=0 EndX=34.2106 EndY=19.5362 EndZ=0
    g16: LineSegment StartX=34.2106 StartY=19.5362 StartZ=0 EndX=31.0954 EndY=17.9145 EndZ=0
    g17: LineSegment StartX=31.0954 StartY=17.9145 StartZ=0 EndX=13.2412 EndY=11.4161 EndZ=0
    g18: LineSegment StartX=13.2412 StartY=11.4161 StartZ=0 EndX=9.81247 EndY=10.656 EndZ=0
    g19: LineSegment StartX=9.81247 StartY=10.656 StartZ=0 EndX=-9.11523 EndY=9 EndZ=0
    g20: LineSegment StartX=-9.11523 StartY=9 StartZ=0 EndX=-12.6239 EndY=9.15319 EndZ=0
    g21: LineSegment StartX=-12.6239 StartY=9.15319 StartZ=0 EndX=-31.3353 EndY=12.4525 EndZ=0
    g22: LineSegment StartX=-31.3353 StartY=12.4525 StartZ=0 EndX=-34.6847 EndY=13.5086 EndZ=0
    g23: LineSegment StartX=-34.6847 StartY=13.5086 StartZ=0 EndX=-51.9046 EndY=21.5383 EndZ=0
    g24: LineSegment StartX=-51.9046 StartY=21.5383 StartZ=0 EndX=-50.2141 EndY=25.1636 EndZ=0
    g25: LineSegment StartX=-34.6847 StartY=13.5086 StartZ=0 EndX=-32.9942 EndY=17.1338 EndZ=0
    g26: LineSegment StartX=-30.6407 StartY=16.3917 StartZ=0 EndX=-31.3353 EndY=12.4525 EndZ=0
    g27: LineSegment StartX=-11.9293 StartY=13.0924 StartZ=0 EndX=-12.6239 EndY=9.15319 EndZ=0
    g28: LineSegment StartX=-9.11523 StartY=9 StartZ=0 EndX=-9.46385 EndY=12.9848 EndZ=0
    g29: LineSegment StartX=9.46385 StartY=14.6407 StartZ=0 EndX=9.81247 EndY=10.656 EndZ=0
    g30: LineSegment StartX=13.2412 StartY=11.4161 StartZ=0 EndX=11.8732 EndY=15.1749 EndZ=0
    g31: LineSegment StartX=29.7273 StartY=21.6733 StartZ=0 EndX=31.0954 EndY=17.9145 EndZ=0
    g32: LineSegment StartX=34.2106 StartY=19.5362 StartZ=0 EndX=31.9163 EndY=22.8128 EndZ=0
    g33: LineSegment StartX=-41.6042 StartY=21.1487 StartZ=0 EndX=-39.4911 EndY=25.6802 EndZ=0
    g34: LineSegment StartX=-39.4911 StartY=25.6802 StartZ=0 EndX=-36.7722 EndY=24.4124 EndZ=0
    g35: LineSegment StartX=-36.7722 StartY=24.4124 StartZ=0 EndX=-32.546 EndY=33.4755 EndZ=0
    g36: LineSegment StartX=-21.6347 StartY=30.0351 StartZ=0 EndX=-23.3712 EndY=20.1871 EndZ=0
    g37: LineSegment StartX=-23.3712 StartY=20.1871 StartZ=0 EndX=-20.4167 EndY=19.6661 EndZ=0
    g38: LineSegment StartX=-20.4167 StartY=19.6661 StartZ=0 EndX=-17.4623 EndY=19.1452 EndZ=0
    g39: LineSegment StartX=-17.4623 StartY=19.1452 StartZ=0 EndX=-15.7258 EndY=28.9933 EndZ=0
    g40: LineSegment StartX=-4.29592 StartY=28.4942 StartZ=0 EndX=-3.42436 EndY=18.5323 EndZ=0
    g41: LineSegment StartX=-3.42436 StartY=18.5323 StartZ=0 EndX=-0.435779 EndY=18.7937 EndZ=0
    g42: LineSegment StartX=-0.435779 StartY=18.7937 StartZ=0 EndX=2.55281 EndY=19.0552 EndZ=0
    g43: LineSegment StartX=2.55281 StartY=19.0552 StartZ=0 EndX=1.68125 EndY=29.0171 EndZ=0
    g44: LineSegment StartX=12.8509 StartY=31.4934 StartZ=0 EndX=16.2711 EndY=22.0965 EndZ=0
    g45: LineSegment StartX=16.2711 StartY=22.0965 StartZ=0 EndX=19.0901 EndY=23.1225 EndZ=0
    g46: LineSegment StartX=19.0901 StartY=23.1225 StartZ=0 EndX=21.9092 EndY=24.1486 EndZ=0
    g47: LineSegment StartX=21.9092 StartY=24.1486 StartZ=0 EndX=18.489 EndY=33.5455 EndZ=0
    g48: LineSegment StartX=28.6371 StartY=38.8283 StartZ=0 EndX=34.3729 EndY=30.6368 EndZ=0
    g49: LineSegment StartX=34.3729 StartY=30.6368 StartZ=0 EndX=36.8304 EndY=32.3575 EndZ=0
    g50: ArcOfCircle CenterX=3.49974 CenterY=74.7282 CenterZ=0 NormalX=0 NormalY=0 NormalZ=1 AngleXU=0 Radius=43.8257 StartAngle=5.06145 EndAngle=5.32325
    g51: ArcOfCircle CenterX=-2.13841 CenterY=72.6761 CenterZ=0 NormalX=0 NormalY=0 NormalZ=1 AngleXU=0 Radius=43.8257 StartAngle=4.79966 EndAngle=5.06145
    g52: ArcOfCircle CenterX=-8.11558 CenterY=72.1532 CenterZ=0 NormalX=0 NormalY=0 NormalZ=1 AngleXU=0 Radius=43.8257 StartAngle=4.53786 EndAngle=4.79966
    g53: ArcOfCircle CenterX=-14.0244 CenterY=73.195 CenterZ=0 NormalX=0 NormalY=0 NormalZ=1 AngleXU=0 Radius=43.8257 StartAngle=4.27606 EndAngle=4.53786
    g54: LineSegment StartX=-20.4167 StartY=19.6661 StartZ=0 EndX=-21.285 EndY=14.7421 EndZ=0
    g55: LineSegment StartX=0 StartY=13.8128 StartZ=0 EndX=-0.435779 EndY=18.7937 EndZ=0
    g56: LineSegment StartX=19.0901 StartY=23.1225 StartZ=0 EndX=20.8002 EndY=18.4241 EndZ=0
    g57: LineSegment StartX=36.8304 StartY=32.3575 StartZ=0 EndX=39.6982 EndY=28.2617 EndZ=0
    g58: LineSegment StartX=-50 StartY=9 StartZ=0 EndX=-50 EndY=3 EndZ=0
    g59: LineSegment StartX=-50 StartY=9 StartZ=0 EndX=50 EndY=9 EndZ=0
    g60: LineSegment StartX=-70 StartY=9 StartZ=0 EndX=-50 EndY=9 EndZ=0
  constraints (176):
    c: Coincident(g0,g1)
    c: Coincident(g1,g2)
    c: Coincident(g2,g3)
    c: Coincident(g3,g4)
    c: Coincident(g4,g5)
    c: Coincident(g5,g6)
    c: Coincident(g6,g7)
    c: Coincident(g7,g8)
    c: Coincident(g8,g9)
    c: Coincident(g9,g10)
    c: Coincident(g10,g11)
    c: Coincident(g11,g12)
    c: Coincident(g12,g13)
    c: Coincident(g13,g14)
    c: Coincident(g14,g15)
    c: Coincident(g15,g16)
    c: Coincident(g16,g17)
    c: Coincident(g17,g18)
    c: Coincident(g18,g19)
    c: Coincident(g19,g20)
    c: Coincident(g20,g21)
    c: Coincident(g21,g22)
    c: Coincident(g22,g23)
    c: Coincident(g23,g24)
    c: Coincident(g24,g0)
    c: Coincident(g25,g22)
    c: Coincident(g25,g1)
    c: Coincident(g26,g2)
    c: Coincident(g26,g21)
    c: Coincident(g27,g4)
    c: Coincident(g27,g20)
    c: Coincident(g28,g19)
    c: Coincident(g28,g5)
    c: Coincident(g29,g7)
    c: Coincident(g29,g18)
    c: Coincident(g30,g17)
    c: Coincident(g30,g8)
    c: Coincident(g31,g10)
    c: Coincident(g31,g16)
    c: Coincident(g32,g15)
    c: Coincident(g32,g11)
    c: Equal(g32,g31)
    c: Equal(g30,g29)
    c: Equal(g28,g27)
    c: Equal(g26,g25)
    c: Perpendicular(g24,g23)
    c: Perpendicular(g23,g25)
    c: Perpendicular(g21,g26)
    c: Perpendicular(g27,g21)
    c: Perpendicular(g19,g28)
    c: Perpendicular(g29,g19)
    c: Perpendicular(g17,g30)
    c: Perpendicular(g31,g17)
    c: Perpendicular(g15,g32)
    c: Perpendicular(g14,g15)
    c: Perpendicular(g24,g0)
    c: Perpendicular(g26,g3)
    c: Perpendicular(g28,g6)
    c: Perpendicular(g30,g9)
    c: Perpendicular(g32,g12)
    c: Parallel(g13,g12)
    c: Parallel(g10,g9)
    c: Parallel(g7,g6)
    c: Parallel(g4,g3)
    c: Parallel(g1,g0)
    c: Coincident(g0,g33)
    c: Coincident(g33,g34)
    c: Coincident(g34,g35)
    c: Coincident(g36,g37)
    c: Coincident(g37,g38)
    c: Coincident(g38,g39)
    c: Coincident(g40,g41)
    c: Coincident(g41,g42)
    c: Coincident(g42,g43)
    c: Coincident(g44,g45)
    c: Coincident(g45,g46)
    c: Coincident(g46,g47)
    c: Coincident(g48,g49)
    c: Coincident(g50,g47)
    c: Coincident(g50,g48)
    c: Coincident(g51,g43)
    c: Coincident(g51,g44)
    c: Coincident(g52,g39)
    c: Coincident(g52,g40)
    c: Coincident(g53,g35)
    c: Coincident(g53,g36)
    c: Coincident(g54,g37)
    c: Coincident(g54,g3)
    c: Coincident(g55,g6)
    c: Coincident(g55,g41)
    c: Coincident(g56,g45)
    c: Coincident(g56,g9)
    c: Coincident(g57,g49)
    c: Coincident(g57,g12)
    c: Equal(g34,g37)
    c: Equal(g37,g38)
    c: Equal(g38,g41)
    c: Equal(g41,g42)
    c: Equal(g42,g45)
    c: Equal(g45,g46)
    c: Equal(g46,g49)
    c: Perpendicular(g1,g33)
    c: Perpendicular(g4,g54)
    c: Perpendicular(g7,g55)
    c: Perpendicular(g10,g56)
    c: Perpendicular(g13,g57)
    c: Perpendicular(g49,g57)
    c: Perpendicular(g46,g56)
    c: Perpendicular(g56,g45)
    c: Perpendicular(g55,g42)
    c: Perpendicular(g41,g55)
    c: Perpendicular(g54,g38)
    c: Perpendicular(g37,g54)
    c: Perpendicular(g33,g34)
    c: Perpendicular(g35,g34)
    c: Perpendicular(g53,g35)
    c: Perpendicular(g53,g36)
    c: Perpendicular(g37,g36)
    c: Perpendicular(g39,g38)
    c: Perpendicular(g52,g39)
    c: Perpendicular(g52,g40)
    c: Perpendicular(g41,g40)
    c: Perpendicular(g43,g42)
    c: Perpendicular(g51,g43)
    c: Perpendicular(g51,g44)
    c: Perpendicular(g45,g44)
    c: Perpendicular(g47,g46)
    c: Perpendicular(g50,g47)
    c: Perpendicular(g50,g48)
    c: Perpendicular(g49,g48)
    c: Distance(g33,g37) = 20
    c: Distance(g41,g37) = 20
    c: Distance(g41,g45) = 20
    c: Distance(g49,g45) = 20
    c: Equal(g13,g12)
    c: Equal(g10,g9)
    c: Equal(g7,g6)
    c: Equal(g4,g3)
    c: Equal(g1,g0)
    c: Distance(g35) = 10
    c: Distance(g36) = 10
    c: Distance(g39) = 10
    c: Distance(g40) = 10
    c: Distance(g43) = 10
    c: Distance(g44) = 10
    c: Distance(g47) = 10
    c: Distance(g48) = 10
    c: Distance(g33) = 5
    c: Distance(g54) = 5
    c: Distance(g55) = 5
    c: Distance(g56) = 5
    c: Distance(g57) = 5
    c: Distance(g19) = 19
    c: Distance(g28) = 4
    c: Equal(g23,g21)
    c: Equal(g21,g19)
    c: Equal(g19,g17)
    c: Equal(g17,g15)
    c: Vertical(g58)
    c: Coincident(g59,g58)
    c: Horizontal(g59)
    c: DistanceY(g58,g58) = 6
    c: DistanceX(g59,g59) = 100
    c: DistanceX(g58,g-1) = 50
    c: DistanceY(g-1,g58) = 3
    c: Distance(g42) = 3
    c: Horizontal(g60)
    c: Angle(g60,g55) = 1.65806
    c: Coincident(g60,g58)
    c: DistanceX(g60,g60) = 20
    c: Angle(g56,g57) = 0.261799
    c: Angle(g55,g56) = 0.261799
    c: Angle(g54,g55) = 0.261799
    c: Angle(g33,g54) = 0.261799
    c: PointOnObject(g6,g-2)
    c: PointOnObject(g19,g59)
FEATURE [PartDesign::Pad] Pad008  label="RArch"
  Direction = (1,-2e-16,3e-16)
  Length = 19
  Length2 = 100
  Midplane = true
  Placement = pos=(0,0,0) rot=(0.57735,0.57735,0.57735;2.0944rad)
  Profile = -> Sketch012
  ReferenceAxis = -> Sketch012 [N_Axis]
  Type = 0
FEATURE [Sketcher::SketchObject] Sketch013
  ExternalGeometry = -> [Sketch012]
  FullyConstrained = true
  MapMode = 5
  Placement = pos=(0,0,0) rot=(0.57735,0.57735,0.57735;2.0944rad)
  Support = -> [YZ_Plane002]
  sketch-geometry (75):
    g0: LineSegment StartX=-49.1265 StartY=24.6564 StartZ=0 EndX=-50.817 EndY=21.0312 EndZ=0
    g1: LineSegment StartX=-49.6388 StartY=20.4818 StartZ=0 EndX=-47.9483 EndY=24.107 EndZ=0
    g2: LineSegment StartX=-35.26 StartY=18.1904 StartZ=0 EndX=-36.9505 EndY=14.5651 EndZ=0
    g3: LineSegment StartX=-35.7723 StartY=14.0157 StartZ=0 EndX=-34.0818 EndY=17.641 EndZ=0
    g4: LineSegment StartX=-41.6042 StartY=21.1487 StartZ=0 EndX=-43.2946 EndY=17.5235 EndZ=0
    g5: LineSegment StartX=-29.4589 StartY=16.1834 StartZ=0 EndX=-30.1535 EndY=12.2441 EndZ=0
    g6: LineSegment StartX=-28.8732 StartY=12.0184 StartZ=0 EndX=-28.1786 EndY=15.9576 EndZ=0
    g7: LineSegment StartX=-21.285 StartY=14.7421 StartZ=0 EndX=-21.9796 EndY=10.8028 EndZ=0
    g8: LineSegment StartX=-15.0859 StartY=9.58731 StartZ=0 EndX=-14.3913 EndY=13.5265 EndZ=0
    g9: LineSegment StartX=-13.1111 StartY=13.3008 StartZ=0 EndX=-13.8057 EndY=9.36157 EndZ=0
    g10: LineSegment StartX=-8.26842 StartY=13.0894 StartZ=0 EndX=-7.91979 EndY=9.10459 EndZ=0
    g11: LineSegment StartX=-6.62474 StartY=9.21789 StartZ=0 EndX=-6.97336 EndY=13.2027 EndZ=0
    g12: LineSegment StartX=0 StartY=13.8128 StartZ=0 EndX=0.348623 EndY=9.82798 EndZ=0
    g13: LineSegment StartX=7.32199 StartY=10.4381 StartZ=0 EndX=6.97336 EndY=14.4228 EndZ=0
    g14: LineSegment StartX=8.26842 StartY=14.5362 StartZ=0 EndX=8.61704 EndY=10.5514 EndZ=0
    g15: LineSegment StartX=14.3689 StartY=11.8265 StartZ=0 EndX=13.0008 EndY=15.5853 EndZ=0
    g16: LineSegment StartX=14.2224 StartY=16.0299 StartZ=0 EndX=15.5905 EndY=12.2711 EndZ=0
    g17: LineSegment StartX=22.1683 StartY=14.6653 StartZ=0 EndX=20.8002 EndY=18.4241 EndZ=0
    g18: LineSegment StartX=27.3781 StartY=20.8182 StartZ=0 EndX=28.7462 EndY=17.0594 EndZ=0
    g19: LineSegment StartX=29.9678 StartY=17.5041 StartZ=0 EndX=28.5997 EndY=21.2628 EndZ=0
    g20: LineSegment StartX=32.8993 StartY=23.5011 StartZ=0 EndX=35.1936 EndY=20.2244 EndZ=0
    g21: LineSegment StartX=36.2585 StartY=20.9701 StartZ=0 EndX=33.9642 EndY=24.2467 EndZ=0
    g22: LineSegment StartX=39.6982 StartY=28.2617 StartZ=0 EndX=41.9925 EndY=24.9851 EndZ=0
    g23: LineSegment StartX=47.7266 StartY=29.0002 StartZ=0 EndX=45.4323 EndY=32.2768 EndZ=0
    g24: LineSegment StartX=46.4972 StartY=33.0224 StartZ=0 EndX=48.7915 EndY=29.7458 EndZ=0
    g25: LineSegment StartX=45.4323 StartY=32.2768 StartZ=0 EndX=39.6982 EndY=28.2617 EndZ=0
    g26: LineSegment StartX=39.6982 StartY=28.2617 StartZ=0 EndX=33.9642 EndY=24.2467 EndZ=0
    g27: LineSegment StartX=33.9642 StartY=24.2467 StartZ=0 EndX=34.7672 EndY=23.0999 EndZ=0
    g28: LineSegment StartX=34.7672 StartY=23.0999 StartZ=0 EndX=33.7023 EndY=22.3542 EndZ=0
    g29: LineSegment StartX=33.7023 StartY=22.3542 StartZ=0 EndX=35.1936 EndY=20.2244 EndZ=0
    g30: LineSegment StartX=35.1936 StartY=20.2244 StartZ=0 EndX=41.9925 EndY=24.9851 EndZ=0
    g31: LineSegment StartX=41.9925 StartY=24.9851 StartZ=0 EndX=48.7915 EndY=29.7458 EndZ=0
    g32: LineSegment StartX=48.7915 StartY=29.7458 StartZ=0 EndX=47.3002 EndY=31.8756 EndZ=0
    g33: LineSegment StartX=47.3002 StartY=31.8756 StartZ=0 EndX=46.2353 EndY=31.13 EndZ=0
    g34: LineSegment StartX=46.2353 StartY=31.13 StartZ=0 EndX=45.4323 EndY=32.2768 EndZ=0
    g35: LineSegment StartX=27.3781 StartY=20.8182 StartZ=0 EndX=20.8002 EndY=18.4241 EndZ=0
    g36: LineSegment StartX=20.8002 StartY=18.4241 StartZ=0 EndX=14.2224 EndY=16.0299 EndZ=0
    g37: LineSegment StartX=14.2224 StartY=16.0299 StartZ=0 EndX=14.7012 EndY=14.7144 EndZ=0
    g38: LineSegment StartX=14.7012 StartY=14.7144 StartZ=0 EndX=13.4796 EndY=14.2697 EndZ=0
    g39: LineSegment StartX=13.4796 StartY=14.2697 StartZ=0 EndX=14.3689 EndY=11.8265 EndZ=0
    g40: LineSegment StartX=14.3689 StartY=11.8265 StartZ=0 EndX=22.1683 EndY=14.6653 EndZ=0
    g41: LineSegment StartX=22.1683 StartY=14.6653 StartZ=0 EndX=29.9678 EndY=17.5041 EndZ=0
    g42: LineSegment StartX=29.9678 StartY=17.5041 StartZ=0 EndX=29.0785 EndY=19.9473 EndZ=0
    g43: LineSegment StartX=29.0785 StartY=19.9473 StartZ=0 EndX=27.8569 EndY=19.5026 EndZ=0
    g44: LineSegment StartX=27.8569 StartY=19.5026 StartZ=0 EndX=27.3781 EndY=20.8182 EndZ=0
    g45: LineSegment StartX=-6.97336 StartY=13.2027 StartZ=0 EndX=-6.85134 EndY=11.808 EndZ=0
    g46: LineSegment StartX=-6.85134 StartY=11.808 StartZ=0 EndX=-8.14639 EndY=11.6947 EndZ=0
    g47: LineSegment StartX=-8.14639 StartY=11.6947 StartZ=0 EndX=-7.91979 EndY=9.10459 EndZ=0
    g48: LineSegment StartX=8.61704 StartY=10.5514 StartZ=0 EndX=8.39044 EndY=13.1415 EndZ=0
    g49: LineSegment StartX=8.39044 StartY=13.1415 StartZ=0 EndX=7.09538 EndY=13.0282 EndZ=0
    g50: LineSegment StartX=7.09538 StartY=13.0282 StartZ=0 EndX=6.97336 EndY=14.4228 EndZ=0
    g51: LineSegment StartX=6.97336 StartY=14.4228 StartZ=0 EndX=0 EndY=13.8128 EndZ=0
    g52: LineSegment StartX=0 StartY=13.8128 StartZ=0 EndX=-6.97336 EndY=13.2027 EndZ=0
    g53: LineSegment StartX=-7.91979 StartY=9.10459 StartZ=0 EndX=0.348623 EndY=9.82798 EndZ=0
    g54: LineSegment StartX=0.348623 StartY=9.82798 StartZ=0 EndX=8.61704 EndY=10.5514 EndZ=0
    g55: LineSegment StartX=-21.285 StartY=14.7421 StartZ=0 EndX=-28.1786 EndY=15.9576 EndZ=0
    g56: LineSegment StartX=-28.1786 StartY=15.9576 StartZ=0 EndX=-28.4218 EndY=14.5789 EndZ=0
    g57: LineSegment StartX=-28.4218 StartY=14.5789 StartZ=0 EndX=-29.702 EndY=14.8046 EndZ=0
    g58: LineSegment StartX=-29.702 StartY=14.8046 StartZ=0 EndX=-30.1535 EndY=12.2441 EndZ=0
    g59: LineSegment StartX=-30.1535 StartY=12.2441 StartZ=0 EndX=-21.9796 EndY=10.8028 EndZ=0
    g60: LineSegment StartX=-21.9796 StartY=10.8028 StartZ=0 EndX=-13.8057 EndY=9.36157 EndZ=0
    g61: LineSegment StartX=-13.8057 StartY=9.36157 StartZ=0 EndX=-13.3542 EndY=11.9221 EndZ=0
    g62: LineSegment StartX=-13.3542 StartY=11.9221 StartZ=0 EndX=-14.6345 EndY=12.1478 EndZ=0
    g63: LineSegment StartX=-14.6345 StartY=12.1478 StartZ=0 EndX=-14.3913 EndY=13.5265 EndZ=0
    g64: LineSegment StartX=-14.3913 StartY=13.5265 StartZ=0 EndX=-21.285 EndY=14.7421 EndZ=0
    g65: LineSegment StartX=-41.6042 StartY=21.1487 StartZ=0 EndX=-47.9483 EndY=24.107 EndZ=0
    g66: LineSegment StartX=-47.9483 StartY=24.107 StartZ=0 EndX=-48.54 EndY=22.8382 EndZ=0
    g67: LineSegment StartX=-48.54 StartY=22.8382 StartZ=0 EndX=-49.7182 EndY=23.3876 EndZ=0
    g68: LineSegment StartX=-49.7182 StartY=23.3876 StartZ=0 EndX=-50.817 EndY=21.0312 EndZ=0
    g69: LineSegment StartX=-50.817 StartY=21.0312 StartZ=0 EndX=-43.2946 EndY=17.5235 EndZ=0
    g70: LineSegment StartX=-43.2946 StartY=17.5235 StartZ=0 EndX=-35.7723 EndY=14.0157 EndZ=0
    g71: LineSegment StartX=-35.7723 StartY=14.0157 StartZ=0 EndX=-34.6735 EndY=16.3721 EndZ=0
    g72: LineSegment StartX=-34.6735 StartY=16.3721 StartZ=0 EndX=-35.8517 EndY=16.9215 EndZ=0
    g73: LineSegment StartX=-35.8517 StartY=16.9215 StartZ=0 EndX=-35.26 EndY=18.1904 EndZ=0
    g74: LineSegment StartX=-35.26 StartY=18.1904 StartZ=0 EndX=-41.6042 EndY=21.1487 EndZ=0
  constraints (215):
    c: PointOnObject(g0,g-16)
    c: PointOnObject(g0,g-17)
    c: PointOnObject(g1,g-17)
    c: PointOnObject(g1,g-16)
    c: PointOnObject(g2,g-15)
    c: PointOnObject(g2,g-17)
    c: PointOnObject(g3,g-17)
    c: PointOnObject(g3,g-15)
    c: Coincident(g4,g-16)
    c: PointOnObject(g4,g-17)
    c: PointOnObject(g5,g-14)
    c: PointOnObject(g5,g-12)
    c: PointOnObject(g6,g-12)
    c: PointOnObject(g6,g-14)
    c: Coincident(g7,g-14)
    c: PointOnObject(g7,g-12)
    c: PointOnObject(g8,g-12)
    c: PointOnObject(g8,g-13)
    c: PointOnObject(g9,g-13)
    c: PointOnObject(g9,g-12)
    c: PointOnObject(g10,g-10)
    c: PointOnObject(g10,g-11)
    c: PointOnObject(g11,g-11)
    c: PointOnObject(g11,g-10)
    c: Coincident(g12,g-10)
    c: PointOnObject(g12,g-11)
    c: PointOnObject(g13,g-9)
    c: PointOnObject(g14,g-9)
    c: PointOnObject(g14,g-11)
    c: PointOnObject(g15,g-6)
    c: PointOnObject(g15,g-8)
    c: PointOnObject(g16,g-8)
    c: PointOnObject(g16,g-6)
    c: PointOnObject(g17,g-6)
    c: Coincident(g17,g-8)
    c: PointOnObject(g18,g-7)
    c: PointOnObject(g18,g-6)
    c: PointOnObject(g19,g-6)
    c: PointOnObject(g19,g-7)
    c: PointOnObject(g20,g-4)
    c: PointOnObject(g20,g-5)
    c: PointOnObject(g21,g-5)
    c: PointOnObject(g21,g-4)
    c: Coincident(g22,g-4)
    c: PointOnObject(g22,g-5)
    c: PointOnObject(g23,g-5)
    c: PointOnObject(g23,g-3)
    c: PointOnObject(g24,g-3)
    c: PointOnObject(g24,g-5)
    c: Perpendicular(g-3,g24)
    c: Perpendicular(g23,g-3)
    c: Perpendicular(g22,g-5)
    c: Perpendicular(g21,g-4)
    c: Perpendicular(g20,g-4)
    c: Perpendicular(g-7,g19)
    c: Perpendicular(g-6,g17)
    c: Perpendicular(g-8,g16)
    c: Perpendicular(g15,g-8)
    c: Perpendicular(g-9,g14)
    c: Perpendicular(g13,g-9)
    c: Perpendicular(g12,g-11)
    c: Perpendicular(g-10,g11)
    c: Perpendicular(g-10,g10)
    c: Perpendicular(g-13,g9)
    c: Perpendicular(g-13,g8)
    c: Perpendicular(g-12,g7)
    c: Perpendicular(g-14,g6)
    c: Perpendicular(g-14,g5)
    c: Perpendicular(g-15,g3)
    c: Perpendicular(g2,g-15)
    c: Perpendicular(g-17,g4)
    c: Perpendicular(g-16,g1)
    c: Perpendicular(g-16,g0)
    c: Distance(g2,g1) = 14
    c: Distance(g3,g0) = 16.6
    c: Distance(g6,g8) = 14
    c: Distance(g9,g5) = 16.6
    c: Distance(g13,g11) = 14
    c: Distance(g14,g10) = 16.6
    c: Distance(g15,g19) = 16.6
    c: Distance(g16,g18) = 14
    c: Perpendicular(g-7,g18)
    c: Distance(g24,g20) = 16.6
    c: Distance(g23,g21) = 14
    c: Coincident(g23,g25)
    c: Coincident(g25,g22)
    c: Coincident(g25,g26)
    c: Coincident(g26,g21)
    c: Coincident(g26,g27)
    c: Coincident(g27,g28)
    c: Coincident(g28,g29)
    c: Coincident(g29,g20)
    c: Coincident(g29,g30)
    c: Coincident(g30,g22)
    c: Coincident(g30,g31)
    c: Coincident(g31,g24)
    c: Coincident(g31,g32)
    c: Coincident(g32,g33)
    c: Coincident(g33,g34)
    c: Coincident(g34,g25)
    c: Equal(g25,g26)
    c: Equal(g31,g30)
    c: Distance(g26,g27) = 1.4
    c: Distance(g27,g21) = 2.6
    c: Distance(g29,g28) = 2.6
    c: Distance(g28,g20) = 1.4
    c: Distance(g33,g25) = 1.4
    c: Distance(g32,g24) = 1.4
    c: Distance(g32,g31) = 2.6
    c: Distance(g33,g23) = 2.6
    c: Coincident(g18,g35)
    c: Coincident(g35,g17)
    c: Coincident(g35,g36)
    c: Coincident(g36,g16)
    c: Coincident(g36,g37)
    c: Coincident(g37,g38)
    c: Coincident(g38,g39)
    c: Coincident(g39,g15)
    c: Coincident(g39,g40)
    c: Coincident(g40,g17)
    c: Coincident(g40,g41)
    c: Coincident(g41,g19)
    c: Coincident(g41,g42)
    c: Coincident(g42,g43)
    c: Coincident(g43,g44)
    c: Coincident(g44,g35)
    c: Coincident(g45,g46)
    c: Coincident(g46,g47)
    c: Coincident(g47,g10)
    c: Coincident(g48,g49)
    c: Coincident(g49,g50)
    c: Coincident(g50,g51)
    c: Coincident(g51,g12)
    c: Coincident(g51,g52)
    c: Coincident(g52,g45)
    c: Equal(g52,g51)
    c: Coincident(g45,g11)
    c: Coincident(g50,g13)
    c: Distance(g50,g49) = 1.4
    c: Distance(g13,g49) = 2.6
    c: Distance(g14,g48) = 1.4
    c: Distance(g48,g14) = 2.6
    c: Coincident(g47,g53)
    c: Coincident(g53,g12)
    c: Coincident(g53,g54)
    c: Coincident(g54,g48)
    c: Coincident(g48,g14)
    c: Equal(g54,g53)
    c: PointOnObject(g13,g-11)
    c: Distance(g45,g45) = 1.4
    c: Distance(g45,g11) = 2.6
    c: Distance(g10,g46) = 1.4
    c: Distance(g46,g47) = 2.6
    c: Coincident(g7,g55)
    c: Coincident(g55,g56)
    c: Coincident(g56,g57)
    c: Coincident(g57,g58)
    c: Coincident(g58,g5)
    c: Coincident(g58,g59)
    c: Coincident(g59,g60)
    c: Coincident(g60,g9)
    c: Coincident(g60,g61)
    c: Coincident(g61,g62)
    c: Coincident(g62,g63)
    c: Coincident(g63,g8)
    c: Coincident(g63,g64)
    c: Coincident(g64,g55)
    c: Coincident(g55,g6)
    c: Equal(g55,g64)
    c: Coincident(g59,g7)
    c: Equal(g59,g60)
    c: Distance(g61,g60) = 2.6
    c: Distance(g62,g8) = 2.6
    c: Distance(g57,g5) = 1.4
    c: Distance(g55,g56) = 1.4
    c: Distance(g6,g56) = 2.6
    c: Distance(g57,g58) = 2.6
    c: Distance(g62,g63) = 1.4
    c: Distance(g61,g9) = 1.4
    c: Coincident(g4,g65)
    c: Coincident(g65,g1)
    c: Coincident(g65,g66)
    c: Coincident(g66,g67)
    c: Coincident(g67,g68)
    c: Coincident(g68,g0)
    c: Coincident(g68,g69)
    c: Coincident(g69,g4)
    c: Coincident(g69,g70)
    c: Coincident(g70,g3)
    c: Coincident(g70,g71)
    c: Coincident(g71,g72)
    c: Coincident(g72,g73)
    c: Coincident(g73,g2)
    c: Coincident(g73,g74)
    c: Coincident(g74,g65)
    c: Equal(g74,g65)
    c: Equal(g70,g69)
    c: Distance(g73,g72) = 1.4
    c: Distance(g71,g3) = 1.4
    c: Distance(g72,g2) = 2.6
    c: Distance(g70,g71) = 2.6
    c: Distance(g66,g65) = 1.4
    c: Distance(g0,g67) = 1.4
    c: Distance(g67,g68) = 2.6
    c: Distance(g66,g1) = 2.6
    c: Equal(g36,g35)
    c: Equal(g41,g40)
    c: Distance(g41,g42) = 2.6
    c: Distance(g42,g19) = 1.4
    c: Distance(g43,g35) = 1.4
    c: Distance(g43,g18) = 2.6
    c: Distance(g37,g36) = 1.4
    c: Distance(g38,g15) = 1.4
    c: Distance(g38,g39) = 2.6
    c: Distance(g37,g16) = 2.6
FEATURE [PartDesign::Pocket] Pocket004  label="RMX sockets"
  BaseFeature = -> Pad008
  Direction = (-1,2e-16,-3e-16)
  Length = 14
  Length2 = 100
  Midplane = true
  Placement = pos=(0,0,0) rot=(0.57735,0.57735,0.57735;2.0944rad)
  Profile = -> Sketch013
  Type = 0
FEATURE [Sketcher::SketchObject] Sketch014
  ExternalGeometry = -> [Sketch013]
  FullyConstrained = true
  MapMode = 5
  Placement = pos=(0,0,0) rot=(0.57735,0.57735,0.57735;2.0944rad)
  Support = -> [YZ_Plane002]
  sketch-geometry (55):
    g0: LineSegment StartX=27.8569 StartY=19.5026 StartZ=0 EndX=27.7885 EndY=19.6906 EndZ=0
    g1: LineSegment StartX=27.7885 StartY=19.6906 StartZ=0 EndX=14.6328 EndY=14.9023 EndZ=0
    g2: LineSegment StartX=14.6328 StartY=14.9023 StartZ=0 EndX=14.7012 EndY=14.7144 EndZ=0
    g3: LineSegment StartX=14.7012 StartY=14.7144 StartZ=0 EndX=13.4796 EndY=14.2697 EndZ=0
    g4: LineSegment StartX=13.4796 StartY=14.2697 StartZ=0 EndX=13.7532 EndY=13.518 EndZ=0
    g5: LineSegment StartX=13.7532 StartY=13.518 StartZ=0 EndX=29.3521 EndY=19.1955 EndZ=0
    g6: LineSegment StartX=29.3521 StartY=19.1955 StartZ=0 EndX=29.0785 EndY=19.9473 EndZ=0
    g7: LineSegment StartX=29.0785 StartY=19.9473 StartZ=0 EndX=27.8569 EndY=19.5026 EndZ=0
    g8: LineSegment StartX=7.07795 StartY=13.2274 StartZ=0 EndX=7.09538 EndY=13.0282 EndZ=0
    g9: LineSegment StartX=7.09538 StartY=13.0282 StartZ=0 EndX=8.39044 EndY=13.1415 EndZ=0
    g10: LineSegment StartX=8.39044 StartY=13.1415 StartZ=0 EndX=8.46016 EndY=12.3445 EndZ=0
    g11: LineSegment StartX=8.46016 StartY=12.3445 StartZ=0 EndX=-8.07667 EndY=10.8977 EndZ=0
    g12: LineSegment StartX=-8.07667 StartY=10.8977 StartZ=0 EndX=-8.14639 EndY=11.6947 EndZ=0
    g13: LineSegment StartX=-8.14639 StartY=11.6947 StartZ=0 EndX=-6.85134 EndY=11.808 EndZ=0
    g14: LineSegment StartX=-6.85134 StartY=11.808 StartZ=0 EndX=-6.86877 EndY=12.0072 EndZ=0
    g15: LineSegment StartX=-6.86877 StartY=12.0072 StartZ=0 EndX=7.07795 EndY=13.2274 EndZ=0
    g16: LineSegment StartX=0 StartY=13.8128 StartZ=0 EndX=0.104587 EndY=12.6173 EndZ=0
    g17: LineSegment StartX=0.104587 StartY=12.6173 StartZ=0 EndX=0.191743 EndY=11.6211 EndZ=0
    g18: LineSegment StartX=0.191743 StartY=11.6211 StartZ=0 EndX=0.348623 EndY=9.82798 EndZ=0
    g19: LineSegment StartX=20.8002 StartY=18.4241 StartZ=0 EndX=21.2107 EndY=17.2964 EndZ=0
    g20: LineSegment StartX=21.2107 StartY=17.2964 StartZ=0 EndX=21.5527 EndY=16.3567 EndZ=0
    g21: LineSegment StartX=21.5527 StartY=16.3567 StartZ=0 EndX=22.1683 EndY=14.6653 EndZ=0
    g22: LineSegment StartX=39.6982 StartY=28.2617 StartZ=0 EndX=40.3865 EndY=27.2788 EndZ=0
    g23: LineSegment StartX=40.3865 StartY=27.2788 StartZ=0 EndX=40.9601 EndY=26.4596 EndZ=0
    g24: LineSegment StartX=40.9601 StartY=26.4596 StartZ=0 EndX=41.9925 EndY=24.9851 EndZ=0
    g25: LineSegment StartX=34.6525 StartY=23.2637 StartZ=0 EndX=46.1206 EndY=31.2938 EndZ=0
    g26: LineSegment StartX=46.1206 StartY=31.2938 StartZ=0 EndX=46.2353 EndY=31.13 EndZ=0
    g27: LineSegment StartX=46.2353 StartY=31.13 StartZ=0 EndX=47.3002 EndY=31.8756 EndZ=0
    g28: LineSegment StartX=47.3002 StartY=31.8756 StartZ=0 EndX=47.7591 EndY=31.2203 EndZ=0
    g29: LineSegment StartX=47.7591 StartY=31.2203 StartZ=0 EndX=34.1611 EndY=21.6989 EndZ=0
    g30: LineSegment StartX=34.1611 StartY=21.6989 StartZ=0 EndX=33.7023 EndY=22.3542 EndZ=0
    g31: LineSegment StartX=33.7023 StartY=22.3542 StartZ=0 EndX=34.7672 EndY=23.0999 EndZ=0
    g32: LineSegment StartX=34.7672 StartY=23.0999 StartZ=0 EndX=34.6525 EndY=23.2637 EndZ=0
    g33: LineSegment StartX=-48.54 StartY=22.8382 StartZ=0 EndX=-49.7182 EndY=23.3876 EndZ=0
    g34: LineSegment StartX=-49.7182 StartY=23.3876 StartZ=0 EndX=-50.0563 EndY=22.6626 EndZ=0
    g35: LineSegment StartX=-50.0563 StartY=22.6626 StartZ=0 EndX=-35.0116 EndY=15.6471 EndZ=0
    g36: LineSegment StartX=-35.0116 StartY=15.6471 StartZ=0 EndX=-34.6735 EndY=16.3721 EndZ=0
    g37: LineSegment StartX=-34.6735 StartY=16.3721 StartZ=0 EndX=-35.8517 EndY=16.9215 EndZ=0
    g38: LineSegment StartX=-35.8517 StartY=16.9215 StartZ=0 EndX=-35.7672 EndY=17.1028 EndZ=0
    g39: LineSegment StartX=-35.7672 StartY=17.1028 StartZ=0 EndX=-48.4555 EndY=23.0195 EndZ=0
    g40: LineSegment StartX=-48.4555 StartY=23.0195 StartZ=0 EndX=-48.54 EndY=22.8382 EndZ=0
    g41: LineSegment StartX=-41.6042 StartY=21.1487 StartZ=0 EndX=-42.1113 EndY=20.0611 EndZ=0
    g42: LineSegment StartX=-42.1113 StartY=20.0611 StartZ=0 EndX=-42.5339 EndY=19.1548 EndZ=0
    g43: LineSegment StartX=-42.5339 StartY=19.1548 StartZ=0 EndX=-43.2946 EndY=17.5235 EndZ=0
    g44: LineSegment StartX=-28.387 StartY=14.7758 StartZ=0 EndX=-28.4218 EndY=14.5789 EndZ=0
    g45: LineSegment StartX=-28.4218 StartY=14.5789 StartZ=0 EndX=-29.702 EndY=14.8046 EndZ=0
    g46: LineSegment StartX=-29.702 StartY=14.8046 StartZ=0 EndX=-29.8409 EndY=14.0168 EndZ=0
    g47: LineSegment StartX=-29.8409 StartY=14.0168 StartZ=0 EndX=-13.4931 EndY=11.1342 EndZ=0
    g48: LineSegment StartX=-13.4931 StartY=11.1342 StartZ=0 EndX=-13.3542 EndY=11.9221 EndZ=0
    g49: LineSegment StartX=-13.3542 StartY=11.9221 StartZ=0 EndX=-14.6345 EndY=12.1478 EndZ=0
    g50: LineSegment StartX=-14.6345 StartY=12.1478 StartZ=0 EndX=-14.5997 EndY=12.3448 EndZ=0
    g51: LineSegment StartX=-14.5997 StartY=12.3448 StartZ=0 EndX=-28.387 EndY=14.7758 EndZ=0
    g52: LineSegment StartX=-21.285 StartY=14.7421 StartZ=0 EndX=-21.4934 EndY=13.5603 EndZ=0
    g53: LineSegment StartX=-21.4934 StartY=13.5603 StartZ=0 EndX=-21.667 EndY=12.5755 EndZ=0
    g54: LineSegment StartX=-21.667 StartY=12.5755 StartZ=0 EndX=-21.9796 EndY=10.8028 EndZ=0
  constraints (140):
    c: Coincident(g-3,g0)
    c: Coincident(g0,g1)
    c: Coincident(g1,g2)
    c: Coincident(g2,g3)
    c: Coincident(g3,g4)
    c: Coincident(g4,g5)
    c: Coincident(g5,g6)
    c: Coincident(g6,g-4)
    c: Coincident(g6,g7)
    c: Coincident(g7,g0)
    c: Coincident(g3,g-6)
    c: Coincident(g2,g-5)
    c: Coincident(g8,g-7)
    c: Coincident(g8,g9)
    c: Coincident(g9,g-8)
    c: Coincident(g9,g10)
    c: Coincident(g10,g11)
    c: Coincident(g11,g12)
    c: Coincident(g12,g-9)
    c: Coincident(g12,g13)
    c: Coincident(g13,g-10)
    c: Coincident(g13,g14)
    c: Coincident(g14,g15)
    c: Coincident(g15,g8)
    c: PointOnObject(g10,g-8)
    c: PointOnObject(g1,g-5)
    c: PointOnObject(g0,g-3)
    c: PointOnObject(g5,g-4)
    c: PointOnObject(g4,g-6)
    c: PointOnObject(g8,g-7)
    c: PointOnObject(g11,g-9)
    c: PointOnObject(g14,g-10)
    c: Coincident(g16,g-11)
    c: PointOnObject(g16,g15)
    c: Coincident(g17,g16)
    c: PointOnObject(g17,g11)
    c: Coincident(g18,g-12)
    c: Angle(g16,g17) = 3.14159
    c: Angle(g17,g18) = 3.14159
    c: Coincident(g17,g18)
    c: Perpendicular(g16,g15)
    c: Perpendicular(g18,g11)
    c: Distance(g16) = 1.2
    c: Distance(g18) = 1.8
    c: Coincident(g19,g-13)
    c: PointOnObject(g19,g1)
    c: Coincident(g19,g20)
    c: PointOnObject(g20,g5)
    c: Coincident(g20,g21)
    c: Coincident(g21,g-14)
    c: Angle(g21,g20) = 3.14159
    c: Angle(g19,g20) = 3.14159
    c: Perpendicular(g21,g5)
    c: Perpendicular(g1,g19)
    c: Distance(g19) = 1.2
    c: Distance(g21) = 1.8
    c: Coincident(g22,g-16)
    c: Coincident(g22,g23)
    c: Coincident(g23,g24)
    c: Coincident(g24,g-15)
    c: PointOnObject(g25,g-17)
    c: PointOnObject(g25,g-20)
    c: Coincident(g25,g26)
    c: Coincident(g26,g-20)
    c: Coincident(g26,g27)
    c: Coincident(g27,g-19)
    c: Coincident(g27,g28)
    c: PointOnObject(g28,g-19)
    c: Coincident(g28,g29)
    c: PointOnObject(g29,g-18)
    c: Coincident(g29,g30)
    c: Coincident(g30,g-18)
    c: Coincident(g30,g31)
    c: Coincident(g31,g-17)
    c: Coincident(g31,g32)
    c: Coincident(g32,g25)
    c: PointOnObject(g22,g25)
    c: PointOnObject(g23,g29)
    c: Angle(g23,g24) = 3.14159
    c: Angle(g23,g22) = 3.14159
    c: Distance(g22) = 1.2
    c: Distance(g24) = 1.8
    c: Perpendicular(g23,g29)
    c: Perpendicular(g23,g25)
    c: Coincident(g-29,g33)
    c: Coincident(g33,g-30)
    c: Coincident(g33,g34)
    c: PointOnObject(g34,g-30)
    c: Coincident(g34,g35)
    c: PointOnObject(g35,g-27)
    c: Coincident(g35,g36)
    c: Coincident(g36,g-27)
    c: Coincident(g36,g37)
    c: Coincident(g37,g-28)
    c: Coincident(g37,g38)
    c: PointOnObject(g38,g-28)
    c: Coincident(g38,g39)
    c: PointOnObject(g39,g-29)
    c: Coincident(g39,g40)
    c: Coincident(g40,g33)
    c: Coincident(g-32,g41)
    c: PointOnObject(g41,g39)
    c: Coincident(g41,g42)
    c: PointOnObject(g42,g35)
    c: Coincident(g42,g43)
    c: Coincident(g-31,g43)
    c: Angle(g42,g41) = 3.14159
    c: Angle(g43,g42) = 3.14159
    c: Distance(g41) = 1.2
    c: Distance(g42) = 1
    c: Perpendicular(g42,g39)
    c: Perpendicular(g43,g35)
    c: PointOnObject(g44,g-24)
    c: Coincident(g44,g-24)
    c: Coincident(g44,g45)
    c: Coincident(g45,g-25)
    c: Coincident(g45,g46)
    c: PointOnObject(g46,g-25)
    c: Coincident(g46,g47)
    c: PointOnObject(g47,g-22)
    c: Coincident(g47,g48)
    c: Coincident(g48,g49)
    c: Coincident(g49,g-23)
    c: Coincident(g49,g50)
    c: Coincident(g50,g51)
    c: Coincident(g51,g44)
    c: Coincident(g-22,g48)
    c: PointOnObject(g50,g-23)
    c: Coincident(g-26,g52)
    c: PointOnObject(g52,g51)
    c: Coincident(g52,g53)
    c: PointOnObject(g53,g47)
    c: Coincident(g53,g54)
    c: Coincident(g54,g-21)
    c: Angle(g52,g53) = 3.14159
    c: Angle(g54,g53) = 3.14159
    c: Distance(g52) = 1.2
    c: Distance(g53) = 1
    c: Perpendicular(g51,g52)
    c: Perpendicular(g47,g54)
FEATURE [PartDesign::Pocket] Pocket005  label="RChoc sockets"
  BaseFeature = -> Pocket004
  Direction = (-1,2e-16,-3e-16)
  Length = 14.6
  Length2 = 100
  Midplane = true
  Placement = pos=(0,0,0) rot=(0.57735,0.57735,0.57735;2.0944rad)
  Profile = -> Sketch014
  Type = 0
FEATURE [Sketcher::SketchObject] Sketch017
  ExternalGeometry = -> [Sketch012]
  FullyConstrained = true
  MapMode = 5
  Placement = pos=(0,0,0) rot=(0.57735,0.57735,0.57735;2.0944rad)
  Support = -> [YZ_Plane002]
  expr: Constraints[39] = <<Spreadsheet>>.Wiring
  sketch-geometry (16):
    g0: LineSegment StartX=-13.6658 StartY=3.24435 StartZ=0 EndX=-12.6239 EndY=9.15319 EndZ=0
    g1: LineSegment StartX=-12.6239 StartY=9.15319 StartZ=0 EndX=-11.9293 EndY=13.0924 EndZ=0
    g2: LineSegment StartX=-11.9293 StartY=13.0924 StartZ=0 EndX=-9.46385 EndY=12.9848 EndZ=0
    g3: LineSegment StartX=-9.46385 StartY=12.9848 StartZ=0 EndX=-9.11523 EndY=9 EndZ=0
    g4: LineSegment StartX=-9.11523 StartY=9 StartZ=0 EndX=-8.59229 EndY=3.02283 EndZ=0
    g5: LineSegment StartX=-8.59229 StartY=3.02283 StartZ=0 EndX=-8.59229 EndY=0 EndZ=0
    g6: LineSegment StartX=-8.59229 StartY=0 StartZ=0 EndX=-13.6658 EndY=0 EndZ=0
    g7: LineSegment StartX=-13.6658 StartY=0 StartZ=0 EndX=-13.6658 EndY=3.24435 EndZ=0
    g8: LineSegment StartX=15.2934 StartY=0 StartZ=0 EndX=10.3354 EndY=0 EndZ=0
    g9: LineSegment StartX=10.3354 StartY=0 StartZ=0 EndX=10.3354 EndY=4.67879 EndZ=0
    g10: LineSegment StartX=10.3354 StartY=4.67879 StartZ=0 EndX=9.81247 EndY=10.656 EndZ=0
    g11: LineSegment StartX=9.81247 StartY=10.656 StartZ=0 EndX=9.46385 EndY=14.6407 EndZ=0
    g12: LineSegment StartX=9.46385 StartY=14.6407 StartZ=0 EndX=11.8732 EndY=15.1749 EndZ=0
    g13: LineSegment StartX=11.8732 StartY=15.1749 StartZ=0 EndX=13.2412 EndY=11.4161 EndZ=0
    g14: LineSegment StartX=13.2412 StartY=11.4161 StartZ=0 EndX=15.2934 EndY=5.77794 EndZ=0
    g15: LineSegment StartX=15.2934 StartY=5.77794 StartZ=0 EndX=15.2934 EndY=0 EndZ=0
  constraints (40):
    c: Coincident(g0,g-4)
    c: Coincident(g0,g1)
    c: Coincident(g1,g-3)
    c: Coincident(g1,g2)
    c: Coincident(g2,g-3)
    c: Coincident(g2,g3)
    c: Coincident(g3,g-4)
    c: Coincident(g3,g4)
    c: Coincident(g4,g5)
    c: PointOnObject(g5,g-1)
    c: Vertical(g5)
    c: Coincident(g5,g6)
    c: PointOnObject(g6,g-1)
    c: Coincident(g6,g7)
    c: Coincident(g7,g0)
    c: Vertical(g7)
    c: Angle(g4,g3) = 3.14159
    c: Angle(g1,g0) = 3.14159
    c: PointOnObject(g8,g-1)
    c: PointOnObject(g8,g-1)
    c: Coincident(g8,g9)
    c: Vertical(g9)
    c: Coincident(g9,g10)
    c: Coincident(g10,g-6)
    c: Coincident(g10,g11)
    c: Coincident(g11,g-5)
    c: Coincident(g11,g12)
    c: Coincident(g12,g-5)
    c: Coincident(g12,g13)
    c: Coincident(g13,g-6)
    c: Coincident(g13,g14)
    c: Coincident(g14,g15)
    c: Coincident(g15,g8)
    c: Vertical(g15)
    c: Equal(g0,g4)
    c: Equal(g4,g10)
    c: Equal(g10,g14)
    c: Angle(g11,g10) = 3.14159
    c: Angle(g13,g14) = 3.14159
    c: Distance(g0) = 6
FEATURE [PartDesign::Pad] Pad009  label="RInner legs"
  BaseFeature = -> Pocket005
  Direction = (1,-2e-16,3e-16)
  Length = 4.1
  Length2 = 9.5
  Placement = pos=(0,0,0) rot=(0.57735,0.57735,0.57735;2.0944rad)
  Profile = -> Sketch017
  Type = 4
  expr: Length = <<Spreadsheet>>.ScrewD / 2 + 2mm
FEATURE [Sketcher::SketchObject] Sketch018
  ExternalGeometry = -> [Sketch012]
  FullyConstrained = true
  MapMode = 5
  Placement = pos=(0,0,0) rot=(0.57735,0.57735,0.57735;2.0944rad)
  Support = -> [YZ_Plane002]
  expr: Constraints[53] = <<Spreadsheet>>.ArchLength
  expr: Constraints[54] = <<Spreadsheet>>.ArchLength - 5mm
  expr: Constraints[56] = <<Spreadsheet>>.ArchLength - 10mm
  expr: Constraints[57] = <<Spreadsheet>>.ArchLength
  expr: Constraints[58] = <<Spreadsheet>>.ArchLength - 5mm
  expr: Constraints[73] = <<Spreadsheet>>.ArchLength - 10mm
  sketch-geometry (36):
    g0: LineSegment StartX=-37.2204 StartY=8.07075 StartZ=0 EndX=-34.6847 EndY=13.5086 EndZ=0
    g1: LineSegment StartX=-34.6847 StartY=13.5086 StartZ=0 EndX=-32.9942 EndY=17.1338 EndZ=0
    g2: LineSegment StartX=-32.9942 StartY=17.1338 StartZ=0 EndX=-30.6407 EndY=16.3917 EndZ=0
    g3: LineSegment StartX=-30.6407 StartY=16.3917 StartZ=0 EndX=-31.3353 EndY=12.4525 EndZ=0
    g4: LineSegment StartX=-31.3353 StartY=12.4525 StartZ=0 EndX=-32.3771 EndY=6.54366 EndZ=0
    g5: LineSegment StartX=33.1475 StartY=12.2763 StartZ=0 EndX=31.0954 EndY=17.9145 EndZ=0
    g6: LineSegment StartX=31.0954 StartY=17.9145 StartZ=0 EndX=29.7273 EndY=21.6733 EndZ=0
    g7: LineSegment StartX=29.7273 StartY=21.6733 StartZ=0 EndX=31.9163 EndY=22.8128 EndZ=0
    g8: LineSegment StartX=31.9163 StartY=22.8128 StartZ=0 EndX=34.2106 EndY=19.5362 EndZ=0
    g9: LineSegment StartX=34.2106 StartY=19.5362 StartZ=0 EndX=37.6521 EndY=14.6212 EndZ=0
    g10: LineSegment StartX=-37.2204 StartY=8.07075 StartZ=0 EndX=-39.0097 EndY=4.23371 EndZ=0
    g11: LineSegment StartX=-39.0097 StartY=4.23371 StartZ=0 EndX=-39.0097 EndY=0 EndZ=0
    g12: LineSegment StartX=37.6521 StartY=14.6212 StartZ=0 EndX=42.2621 EndY=8.03739 EndZ=0
    g13: LineSegment StartX=42.2621 StartY=8.03739 StartZ=0 EndX=42.2621 EndY=0 EndZ=0
    g14: LineSegment StartX=-32.3771 StartY=6.54366 StartZ=0 EndX=-35 EndY=0 EndZ=0
    g15: LineSegment StartX=-35 StartY=0 StartZ=0 EndX=-45 EndY=0 EndZ=0
    g16: LineSegment StartX=-45 StartY=0 StartZ=0 EndX=-45 EndY=3 EndZ=0
    g17: LineSegment StartX=-45 StartY=3 StartZ=0 EndX=-40 EndY=3 EndZ=0
    g18: LineSegment StartX=40 StartY=3 StartZ=0 EndX=45 EndY=3 EndZ=0
    g19: LineSegment StartX=45 StartY=3 StartZ=0 EndX=45 EndY=0 EndZ=0
    g20: LineSegment StartX=45 StartY=0 StartZ=0 EndX=35 EndY=0 EndZ=0
    g21: LineSegment StartX=35 StartY=0 StartZ=0 EndX=33.1475 EndY=12.2763 EndZ=0
    g22-g25: Circle x4 (B-spline internal-alignment scaffolding for g26; pole/knot coordinates omitted)
    g26: BSplineCurve PolesCount=4 KnotsCount=2 Degree=3 IsPeriodic=0
    g27: GeomPoint X=-37.2204 Y=8.07075 Z=0
    g28: GeomPoint X=-45 Y=3 Z=0
    g29-g32: Circle x4 (B-spline internal-alignment scaffolding for g33; pole/knot coordinates omitted)
    g33: BSplineCurve PolesCount=4 KnotsCount=2 Degree=3 IsPeriodic=0
    g34: GeomPoint X=37.6521 Y=14.6212 Z=0
    g35: GeomPoint X=45 Y=3 Z=0
  constraints (82):
    c: Coincident(g0,g-6)
    c: Coincident(g0,g1)
    c: Coincident(g1,g-5)
    c: Coincident(g1,g2)
    c: Coincident(g2,g-5)
    c: Coincident(g2,g3)
    c: Coincident(g3,g-6)
    c: Coincident(g3,g4)
    c: Coincident(g5,g-3)
    c: Coincident(g5,g6)
    c: Coincident(g6,g-4)
    c: Coincident(g6,g7)
    c: Coincident(g7,g-4)
    c: Coincident(g7,g8)
    c: Coincident(g8,g-3)
    c: Coincident(g8,g9)
    c: Angle(g9,g8) = 3.14159
    c: Angle(g5,g6) = 3.14159
    c: Distance(g9) = 6
    c: Equal(g9,g5)
    c: Equal(g5,g4)
    c: Equal(g4,g0)
    c: Angle(g3,g4) = 3.14159
    c: Angle(g1,g0) = 3.14159
    c: Coincident(g10,g0)
    c: Coincident(g11,g10)
    c: PointOnObject(g11,g-1)
    c: Vertical(g11)
    c: Coincident(g12,g9)
    c: Coincident(g13,g12)
    c: PointOnObject(g13,g-1)
    c: Vertical(g13)
    c: Equal(g12,g13)
    c: Equal(g10,g11)
    c: Angle(g0,g10) = 3.14159
    c: Angle(g12,g9) = 3.14159
    c: Coincident(g4,g14)
    c: PointOnObject(g14,g-1)
    c: Coincident(g14,g15)
    c: PointOnObject(g15,g-1)
    c: Coincident(g15,g16)
    c: Vertical(g16)
    c: DistanceY(g16,g16) = 3
    c: Coincident(g17,g16)
    c: Horizontal(g17)
    c: Horizontal(g18)
    c: Coincident(g18,g19)
    c: PointOnObject(g19,g-1)
    c: Vertical(g19)
    c: Coincident(g19,g20)
    c: PointOnObject(g20,g-1)
    c: Coincident(g20,g21)
    c: Coincident(g21,g5)
    c: DistanceX(g-7,g19) = 45
    c: DistanceX(g-7,g18) = 40
    c: Equal(g19,g16)
    c: DistanceX(g14,g-7) = 35
    c: DistanceX(g16,g-7) = 45
    c: DistanceX(g17,g-7) = 40
    c: Coincident(g26,g0)
    c: Weight(g22) = 1
    c: Equal(g22,g23)
    c: Coincident(g23,g10)
    c: Equal(g22,g24)
    c: Coincident(g24,g17)
    c: Equal(g22,g25)
    c: Coincident(g26,g16)
    c: InternalAlignment(g22-g25 -> g26) x4
    c: InternalAlignment(g27,g26)
    c: InternalAlignment(g28,g26)
    c: DistanceX(g-7,g20) = 35
    c: Coincident(g33,g9)
    c: Weight(g29) = 1
    c: Equal(g29,g30)
    c: Coincident(g30,g12)
    c: Equal(g29,g31)
    c: Coincident(g31,g18)
    c: Equal(g29,g32)
    c: Coincident(g33,g19)
    c: InternalAlignment(g29-g32 -> g33) x4
    c: InternalAlignment(g34,g33)
    c: InternalAlignment(g35,g33)
FEATURE [PartDesign::Pad] Pad010  label="ROuter Legs"
  BaseFeature = -> Pad009
  Direction = (1,-2e-16,3e-16)
  Length = 9.5
  Length2 = 100
  Placement = pos=(0,0,0) rot=(0.57735,0.57735,0.57735;2.0944rad)
  Profile = -> Sketch018
  Reversed = true
  Type = 0
FEATURE [Sketcher::SketchObject] Sketch019
  ExternalGeometry = -> [Sketch018]
  FullyConstrained = true
  MapMode = 5
  Support = -> [XY_Plane002]
  expr: Constraints[15] = <<Spreadsheet>>.NutR
  expr: Constraints[16] = <<Spreadsheet>>.NutR
  expr: Constraints[28] = <<Spreadsheet>>.ScrewD
  expr: Constraints[53] = <<Spreadsheet>>.NutR
  expr: Constraints[54] = <<Spreadsheet>>.NutR
  expr: Constraints[57] = <<Spreadsheet>>.ScrewD
  sketch-geometry (22):
    g0: LineSegment StartX=7.6225 StartY=46.0949 StartZ=0 EndX=0 EndY=40 EndZ=0
    g1: LineSegment StartX=0 StartY=40 StartZ=0 EndX=1e-14 EndY=45 EndZ=0
    g2: LineSegment StartX=1e-14 StartY=45 StartZ=0 EndX=-9.5 EndY=45 EndZ=0
    g3: LineSegment StartX=-9.5 StartY=45 StartZ=0 EndX=-9.5 EndY=55 EndZ=0
    g4: LineSegment StartX=-9.5 StartY=55 StartZ=0 EndX=4.5 EndY=55 EndZ=0
    g5: ArcOfCircle CenterX=4.5 CenterY=50 CenterZ=0 NormalX=0 NormalY=0 NormalZ=1 AngleXU=0 Radius=5 StartAngle=5.38688 EndAngle=7.85398
    g6: LineSegment StartX=4.5 StartY=50 StartZ=0 EndX=0 EndY=50 EndZ=0
    g7: Circle CenterX=0 CenterY=50 CenterZ=0 NormalX=0 NormalY=0 NormalZ=1 AngleXU=0 Radius=2.1
    g8: LineSegment StartX=9.5 StartY=50 StartZ=0 EndX=9.5 EndY=55 EndZ=0
    g9: LineSegment StartX=9.5 StartY=55 StartZ=0 EndX=0 EndY=50 EndZ=0
    g10: LineSegment StartX=-9.5 StartY=55 StartZ=0 EndX=0 EndY=50 EndZ=0
    g11: LineSegment StartX=-1.07e-14 StartY=-45 StartZ=0 EndX=0 EndY=-40 EndZ=0
    g12: LineSegment StartX=0 StartY=-40 StartZ=0 EndX=7.6225 EndY=-46.0949 EndZ=0
    g13: ArcOfCircle CenterX=4.5 CenterY=-50 CenterZ=0 NormalX=0 NormalY=0 NormalZ=1 AngleXU=0 Radius=5 StartAngle=4.71239 EndAngle=7.17949
    g14: LineSegment StartX=4.5 StartY=-55 StartZ=0 EndX=-9.5 EndY=-55 EndZ=0
    g15: LineSegment StartX=-9.5 StartY=-55 StartZ=0 EndX=-9.5 EndY=-45 EndZ=0
    g16: LineSegment StartX=-9.5 StartY=-45 StartZ=0 EndX=-1.07e-14 EndY=-45 EndZ=0
    g17: LineSegment StartX=-9.5 StartY=-55 StartZ=0 EndX=0 EndY=-50 EndZ=0
    g18: LineSegment StartX=0 StartY=-50 StartZ=0 EndX=9.5 EndY=-55 EndZ=0
    g19: LineSegment StartX=9.5 StartY=-55 StartZ=0 EndX=9.5 EndY=-50 EndZ=0
    g20: LineSegment StartX=4.5 StartY=-50 StartZ=0 EndX=0 EndY=-50 EndZ=0
    g21: Circle CenterX=0 CenterY=-50 CenterZ=0 NormalX=0 NormalY=0 NormalZ=1 AngleXU=0 Radius=2.1
  constraints (58):
    c: PointOnObject(g0,g-2)
    c: Coincident(g0,g1)
    c: Coincident(g1,g-3)
    c: Coincident(g1,g2)
    c: Horizontal(g2)
    c: Coincident(g2,g3)
    c: Vertical(g3)
    c: Coincident(g3,g4)
    c: Horizontal(g4)
    c: Tangent(g4,g5) = 1.5708
    c: Tangent(g5,g0) = 1.5708
    c: Coincident(g6,g5)
    c: PointOnObject(g6,g-2)
    c: Horizontal(g6)
    c: Coincident(g7,g6)
    c: DistanceY(g7,g3) = 5
    c: DistanceY(g2,g7) = 5
    c: PointOnObject(g8,g5)
    c: Vertical(g8)
    c: Horizontal(g8,g5)
    c: Coincident(g9,g8)
    c: Coincident(g9,g7)
    c: Coincident(g10,g3)
    c: Coincident(g10,g7)
    c: Equal(g10,g9)
    c: Horizontal(g8,g4)
    c: DistanceX(g3,g8) = 19
    c: DistanceY(g1,g1) = 5
    c: Diameter(g7) = 4.2
    c: Coincident(g11,g-4)
    c: PointOnObject(g11,g-2)
    c: Coincident(g11,g12)
    c: Tangent(g12,g13) = 1.5708
    c: Tangent(g13,g14) = 1.5708
    c: Coincident(g14,g15)
    c: Vertical(g15)
    c: Coincident(g15,g16)
    c: Coincident(g16,g11)
    c: Horizontal(g16)
    c: Horizontal(g14)
    c: Equal(g11,g1)
    c: Coincident(g14,g17)
    c: PointOnObject(g17,g-2)
    c: Coincident(g17,g18)
    c: Coincident(g18,g19)
    c: PointOnObject(g19,g13)
    c: Vertical(g19)
    c: Coincident(g20,g13)
    c: Horizontal(g20)
    c: Coincident(g17,g20)
    c: Horizontal(g18,g13)
    c: DistanceX(g14,g18) = 19
    c: Equal(g18,g17)
    c: DistanceY(g17,g15) = 5
    c: DistanceY(g14,g17) = 5
    c: Horizontal(g19,g13)
    c: Coincident(g21,g17)
    c: Diameter(g21) = 4.2
FEATURE [PartDesign::Pad] Pad011  label="RFeet"
  BaseFeature = -> Pad010
  Direction = (0,0,1)
  Length = 3
  Length2 = 100
  Placement = pos=(0,0,0) rot=(0.57735,0.57735,0.57735;2.0944rad)
  Profile = -> Sketch019
  Type = 0
FEATURE [PartDesign::Body] Body002  label="RingArch"
  Group = -> [Sketch012,Pad008,Sketch013,Pocket004,Sketch014,Pocket005,Sketch017,Pad009,Sketch018,Pad010,Sketch019,Pad011]
  Origin = -> Origin002
  Placement = pos=(50,0,5) rot=(0,0,1;0rad)
  Tip = -> Pad011
FEATURE [Sketcher::SketchObject] Sketch020
  FullyConstrained = true
  MapMode = 5
  Placement = pos=(0,0,0) rot=(0.57735,0.57735,0.57735;2.0944rad)
  Support = -> [YZ_Plane003]
  expr: Constraints[114] = <<Spreadsheet>>.ARowKey
  expr: Constraints[115] = <<Spreadsheet>>.ZRowKey
  expr: Constraints[134] = <<Spreadsheet>>.QRowKey
  expr: Constraints[153] = <<Spreadsheet>>.TopRowKey
  expr: Constraints[172] = <<Spreadsheet>>.Wiring
  expr: Constraints[90] = <<Spreadsheet>>.ModRowKey
  sketch-geometry (62):
    g0: LineSegment StartX=-50.2141 StartY=25.1636 StartZ=0 EndX=-41.6042 EndY=21.1487 EndZ=0
    g1: LineSegment StartX=-41.6042 StartY=21.1487 StartZ=0 EndX=-32.9942 EndY=17.1338 EndZ=0
    g2: LineSegment StartX=-32.9942 StartY=17.1338 StartZ=0 EndX=-30.6407 EndY=16.3917 EndZ=0
    g3: LineSegment StartX=-30.6407 StartY=16.3917 StartZ=0 EndX=-21.285 EndY=14.7421 EndZ=0
    g4: LineSegment StartX=-21.285 StartY=14.7421 StartZ=0 EndX=-11.9293 EndY=13.0924 EndZ=0
    g5: LineSegment StartX=-11.9293 StartY=13.0924 StartZ=0 EndX=-9.46385 EndY=12.9848 EndZ=0
    g6: LineSegment StartX=-9.46385 StartY=12.9848 StartZ=0 EndX=0 EndY=13.8128 EndZ=0
    g7: LineSegment StartX=-1e-16 StartY=13.8128 StartZ=0 EndX=9.46385 EndY=14.6407 EndZ=0
    g8: LineSegment StartX=9.46385 StartY=14.6407 StartZ=0 EndX=11.8732 EndY=15.1749 EndZ=0
    g9: LineSegment StartX=11.8732 StartY=15.1749 StartZ=0 EndX=20.8002 EndY=18.4241 EndZ=0
    g10: LineSegment StartX=20.8002 StartY=18.4241 StartZ=0 EndX=29.7273 EndY=21.6733 EndZ=0
    g11: LineSegment StartX=29.7273 StartY=21.6733 StartZ=0 EndX=31.9163 EndY=22.8128 EndZ=0
    g12: LineSegment StartX=31.9163 StartY=22.8128 StartZ=0 EndX=39.6982 EndY=28.2617 EndZ=0
    g13: LineSegment StartX=39.6982 StartY=28.2617 StartZ=0 EndX=47.4802 EndY=33.7107 EndZ=0
    g14: LineSegment StartX=47.4802 StartY=33.7107 StartZ=0 EndX=49.7745 EndY=30.4341 EndZ=0
    g15: LineSegment StartX=49.7745 StartY=30.4341 StartZ=0 EndX=34.2106 EndY=19.5362 EndZ=0
    g16: LineSegment StartX=34.2106 StartY=19.5362 StartZ=0 EndX=31.0954 EndY=17.9145 EndZ=0
    g17: LineSegment StartX=31.0954 StartY=17.9145 StartZ=0 EndX=13.2412 EndY=11.4161 EndZ=0
    g18: LineSegment StartX=13.2412 StartY=11.4161 StartZ=0 EndX=9.81247 EndY=10.656 EndZ=0
    g19: LineSegment StartX=9.81247 StartY=10.656 StartZ=0 EndX=-9.11523 EndY=9 EndZ=0
    g20: LineSegment StartX=-9.11523 StartY=9 StartZ=0 EndX=-12.6239 EndY=9.15319 EndZ=0
    g21: LineSegment StartX=-12.6239 StartY=9.15319 StartZ=0 EndX=-31.3353 EndY=12.4525 EndZ=0
    g22: LineSegment StartX=-31.3353 StartY=12.4525 StartZ=0 EndX=-34.6847 EndY=13.5086 EndZ=0
    g23: LineSegment StartX=-34.6847 StartY=13.5086 StartZ=0 EndX=-51.9046 EndY=21.5383 EndZ=0
    g24: LineSegment StartX=-51.9046 StartY=21.5383 StartZ=0 EndX=-50.2141 EndY=25.1636 EndZ=0
    g25: LineSegment StartX=-32.9942 StartY=17.1338 StartZ=0 EndX=-34.6847 EndY=13.5086 EndZ=0
    g26: LineSegment StartX=-31.3353 StartY=12.4525 StartZ=0 EndX=-30.6407 EndY=16.3917 EndZ=0
    g27: LineSegment StartX=-11.9293 StartY=13.0924 StartZ=0 EndX=-12.6239 EndY=9.15319 EndZ=0
    g28: LineSegment StartX=-9.11523 StartY=9 StartZ=0 EndX=-9.46385 EndY=12.9848 EndZ=0
    g29: LineSegment StartX=9.46385 StartY=14.6407 StartZ=0 EndX=9.81247 EndY=10.656 EndZ=0
    g30: LineSegment StartX=13.2412 StartY=11.4161 StartZ=0 EndX=11.8732 EndY=15.1749 EndZ=0
    g31: LineSegment StartX=29.7273 StartY=21.6733 StartZ=0 EndX=31.0954 EndY=17.9145 EndZ=0
    g32: LineSegment StartX=34.2106 StartY=19.5362 StartZ=0 EndX=31.9163 EndY=22.8128 EndZ=0
    g33: LineSegment StartX=36.8304 StartY=32.3575 StartZ=0 EndX=34.3729 EndY=30.6368 EndZ=0
    g34: LineSegment StartX=34.3729 StartY=30.6368 StartZ=0 EndX=28.6371 EndY=38.8283 EndZ=0
    g35: LineSegment StartX=18.489 StartY=33.5455 StartZ=0 EndX=21.9092 EndY=24.1486 EndZ=0
    g36: LineSegment StartX=21.9092 StartY=24.1486 StartZ=0 EndX=19.0901 EndY=23.1225 EndZ=0
    g37: LineSegment StartX=19.0901 StartY=23.1225 StartZ=0 EndX=16.2711 EndY=22.0965 EndZ=0
    g38: LineSegment StartX=16.2711 StartY=22.0965 StartZ=0 EndX=12.8509 EndY=31.4934 EndZ=0
    g39: LineSegment StartX=1.68125 StartY=29.0171 StartZ=0 EndX=2.55281 EndY=19.0552 EndZ=0
    g40: LineSegment StartX=2.55281 StartY=19.0552 StartZ=0 EndX=-0.435779 EndY=18.7937 EndZ=0
    g41: LineSegment StartX=-3.42436 StartY=18.5323 StartZ=0 EndX=-0.435779 EndY=18.7937 EndZ=0
    g42: LineSegment StartX=-15.7258 StartY=28.9933 StartZ=0 EndX=-17.4623 EndY=19.1452 EndZ=0
    g43: LineSegment StartX=-17.4623 StartY=19.1452 StartZ=0 EndX=-20.4167 EndY=19.6661 EndZ=0
    g44: LineSegment StartX=-20.4167 StartY=19.6661 StartZ=0 EndX=-23.3712 EndY=20.1871 EndZ=0
    g45: LineSegment StartX=-23.3712 StartY=20.1871 StartZ=0 EndX=-21.6347 EndY=30.0351 EndZ=0
    g46: LineSegment StartX=-32.546 StartY=33.4755 StartZ=0 EndX=-36.7722 EndY=24.4124 EndZ=0
    g47: LineSegment StartX=-36.7722 StartY=24.4124 StartZ=0 EndX=-39.4911 EndY=25.6802 EndZ=0
    g48: LineSegment StartX=-39.4911 StartY=25.6802 StartZ=0 EndX=-41.6042 EndY=21.1487 EndZ=0
    g49: LineSegment StartX=-20.4167 StartY=19.6661 StartZ=0 EndX=-21.285 EndY=14.7421 EndZ=0
    g50: LineSegment StartX=-0.435779 StartY=18.7937 StartZ=0 EndX=-1e-16 EndY=13.8128 EndZ=0
    g51: LineSegment StartX=20.8002 StartY=18.4241 StartZ=0 EndX=19.0901 EndY=23.1225 EndZ=0
    g52: ArcOfCircle CenterX=-14.0244 CenterY=73.195 CenterZ=0 NormalX=0 NormalY=0 NormalZ=1 AngleXU=0 Radius=43.8257 StartAngle=4.27606 EndAngle=4.53786
    g53: ArcOfCircle CenterX=-2.13841 CenterY=72.6761 CenterZ=0 NormalX=0 NormalY=0 NormalZ=1 AngleXU=0 Radius=43.8257 StartAngle=4.79966 EndAngle=5.06145
    g54: ArcOfCircle CenterX=3.49974 CenterY=74.7282 CenterZ=0 NormalX=0 NormalY=0 NormalZ=1 AngleXU=0 Radius=43.8257 StartAngle=5.06145 EndAngle=5.32325
    g55: LineSegment StartX=-3.42436 StartY=18.5323 StartZ=0 EndX=-4.29592 EndY=28.4942 EndZ=0
    g56: ArcOfCircle CenterX=-8.11558 CenterY=72.1532 CenterZ=0 NormalX=0 NormalY=0 NormalZ=1 AngleXU=0 Radius=43.8257 StartAngle=4.53786 EndAngle=4.79966
    g57: LineSegment StartX=36.8304 StartY=32.3575 StartZ=0 EndX=39.6982 EndY=28.2617 EndZ=0
    g58: LineSegment StartX=-50 StartY=3 StartZ=0 EndX=-70 EndY=3 EndZ=0
    g59: LineSegment StartX=-50 StartY=0 StartZ=0 EndX=-50 EndY=3 EndZ=0
    g60: LineSegment StartX=-50 StartY=3 StartZ=0 EndX=-50 EndY=9 EndZ=0
    g61: LineSegment StartX=-50 StartY=9 StartZ=0 EndX=50 EndY=9 EndZ=0
  constraints (179):
    c: Coincident(g0,g1)
    c: Coincident(g1,g2)
    c: Coincident(g2,g3)
    c: Coincident(g3,g4)
    c: Coincident(g4,g5)
    c: Coincident(g5,g6)
    c: Coincident(g8,g9)
    c: Coincident(g9,g10)
    c: Coincident(g10,g11)
    c: Coincident(g11,g12)
    c: Coincident(g13,g14)
    c: Coincident(g14,g15)
    c: Coincident(g15,g16)
    c: Coincident(g16,g17)
    c: Coincident(g17,g18)
    c: Coincident(g18,g19)
    c: Coincident(g19,g20)
    c: Coincident(g20,g21)
    c: Coincident(g21,g22)
    c: Coincident(g22,g23)
    c: Coincident(g23,g24)
    c: Coincident(g24,g0)
    c: Coincident(g25,g1)
    c: Coincident(g25,g22)
    c: Coincident(g26,g21)
    c: Coincident(g26,g2)
    c: Coincident(g27,g4)
    c: Coincident(g27,g20)
    c: Coincident(g28,g19)
    c: Coincident(g28,g5)
    c: Coincident(g29,g18)
    c: Coincident(g30,g17)
    c: Coincident(g30,g8)
    c: Coincident(g31,g10)
    c: Coincident(g31,g16)
    c: Coincident(g32,g15)
    c: Coincident(g32,g11)
    c: Coincident(g33,g34)
    c: Coincident(g35,g36)
    c: Coincident(g36,g37)
    c: Coincident(g37,g38)
    c: Coincident(g39,g40)
    c: Coincident(g42,g43)
    c: Coincident(g43,g44)
    c: Coincident(g44,g45)
    c: Coincident(g46,g47)
    c: Coincident(g47,g48)
    c: Coincident(g48,g0)
    c: Coincident(g49,g3)
    c: Coincident(g50,g40)
    c: Coincident(g50,g6)
    c: Coincident(g51,g9)
    c: Coincident(g51,g36)
    c: Coincident(g7,g29)
    c: Coincident(g49,g43)
    c: Coincident(g52,g46)
    c: Coincident(g52,g45)
    c: Coincident(g53,g39)
    c: Coincident(g53,g38)
    c: Perpendicular(g43,g42)
    c: Parallel(g3,g4)
    c: Equal(g1,g0)
    c: Perpendicular(g1,g48)
    c: Parallel(g1,g0)
    c: Distance(g47,g43) = 20
    c: Perpendicular(g4,g49)
    c: Perpendicular(g49,g43)
    c: Coincident(g7,g6)
    c: Coincident(g41,g40)
    c: Parallel(g13,g12)
    c: Distance(g36,g40) = 20
    c: Distance(g19) = 19
    c: Distance(g40,g43) = 20
    c: Equal(g4,g3)
    c: Perpendicular(g6,g50)
    c: Parallel(g7,g6)
    c: Equal(g6,g7)
    c: Coincident(g55,g41)
    c: Coincident(g56,g42)
    c: Coincident(g56,g55)
    c: Perpendicular(g49,g44)
    c: Perpendicular(g1,g25)
    c: Perpendicular(g23,g25)
    c: Perpendicular(g23,g24)
    c: Equal(g23,g21)
    c: Equal(g19,g21)
    c: Perpendicular(g26,g3)
    c: Perpendicular(g21,g27)
    c: Perpendicular(g27,g4)
    c: Perpendicular(g29,g7)
    c: Distance(g48) = 5
    c: Distance(g46) = 10
    c: Distance(g45) = 10
    c: Equal(g44,g43)
    c: Equal(g41,g43)
    c: Equal(g40,g41)
    c: Equal(g37,g36)
    c: Equal(g36,g40)
    c: Equal(g36,g33)
    c: Perpendicular(g51,g36)
    c: Perpendicular(g51,g37)
    c: Perpendicular(g50,g40)
    c: Perpendicular(g52,g45)
    c: Perpendicular(g52,g46)
    c: Equal(g26,g25)
    c: Perpendicular(g45,g44)
    c: Perpendicular(g47,g46)
    c: Perpendicular(g48,g47)
    c: Equal(g28,g27)
    c: Perpendicular(g6,g28)
    c: Distance(g28) = 4
    c: Distance(g42) = 10
    c: Distance(g55) = 10
    c: Distance(g39) = 10
    c: Distance(g50) = 5
    c: Distance(g49) = 5
    c: Perpendicular(g56,g42)
    c: Equal(g47,g44)
    c: Distance(g41) = 3
    c: Perpendicular(g50,g41)
    c: Perpendicular(g41,g55)
    c: Perpendicular(g56,g55)
    c: Perpendicular(g40,g39)
    c: Perpendicular(g19,g29)
    c: Coincident(g8,g7)
    c: Parallel(g9,g10)
    c: Equal(g9,g10)
    c: Equal(g17,g19)
    c: Perpendicular(g17,g31)
    c: Perpendicular(g17,g30)
    c: Perpendicular(g9,g30)
    c: Equal(g29,g30)
    c: Perpendicular(g51,g9)
    c: Distance(g38) = 10
    c: Distance(g51) = 5
    c: Perpendicular(g37,g38)
    c: Distance(g35) = 10
    c: Coincident(g35,g54)
    c: Perpendicular(g54,g35)
    c: Coincident(g34,g54)
    c: Perpendicular(g54,g34)
    c: Perpendicular(g34,g33)
    c: Coincident(g57,g33)
    c: Coincident(g57,g12)
    c: Perpendicular(g14,g15)
    c: Equal(g32,g31)
    c: Coincident(g13,g12)
    c: Equal(g12,g13)
    c: Perpendicular(g13,g14)
    c: Perpendicular(g33,g57)
    c: Perpendicular(g12,g32)
    c: Equal(g15,g17)
    c: Distance(g34) = 10
    c: Distance(g57) = 5
    c: Distance(g36,g33) = 20
    c: Perpendicular(g36,g35)
    c: Perpendicular(g53,g38)
    c: Perpendicular(g53,g39)
    c: Perpendicular(g57,g12)
    c: Angle(g51,g57) = 0.261799
    c: Angle(g50,g51) = 0.261799
    c: Angle(g49,g50) = 0.261799
    c: Angle(g48,g49) = 0.261799
    c: Angle(g58,g50) = 1.65806
    c: Horizontal(g58)
    c: PointOnObject(g59,g-1)
    c: Vertical(g59)
    c: Coincident(g60,g59)
    c: Vertical(g60)
    c: Coincident(g61,g60)
    c: Horizontal(g61)
    c: Coincident(g58,g59)
    c: DistanceY(g60,g60) = 6
    c: DistanceY(g59,g59) = 3
    c: DistanceX(g58,g58) = 20
    c: DistanceX(g61,g61) = 100
    c: DistanceX(g59,g-1) = 50
    c: PointOnObject(g6,g-2)
    c: PointOnObject(g19,g61)
FEATURE [PartDesign::Pad] Pad012  label="MArch"
  Direction = (1,-2e-16,3e-16)
  Length = 19
  Length2 = 100
  Midplane = true
  Placement = pos=(0,0,0) rot=(0.57735,0.57735,0.57735;2.0944rad)
  Profile = -> Sketch020
  Type = 0
FEATURE [Sketcher::SketchObject] Sketch021
  ExternalGeometry = -> [Sketch020]
  FullyConstrained = true
  MapMode = 5
  Placement = pos=(0,0,0) rot=(0.57735,0.57735,0.57735;2.0944rad)
  Support = -> [YZ_Plane003]
  sketch-geometry (75):
    g0: LineSegment StartX=-47.9483 StartY=24.107 StartZ=0 EndX=-41.6042 EndY=21.1487 EndZ=0
    g1: LineSegment StartX=-41.6042 StartY=21.1487 StartZ=0 EndX=-35.26 EndY=18.1904 EndZ=0
    g2: LineSegment StartX=-35.26 StartY=18.1904 StartZ=0 EndX=-35.8517 EndY=16.9215 EndZ=0
    g3: LineSegment StartX=-35.8517 StartY=16.9215 StartZ=0 EndX=-34.6735 EndY=16.3721 EndZ=0
    g4: LineSegment StartX=-34.6735 StartY=16.3721 StartZ=0 EndX=-35.7723 EndY=14.0157 EndZ=0
    g5: LineSegment StartX=-50.817 StartY=21.0312 StartZ=0 EndX=-49.7182 EndY=23.3876 EndZ=0
    g6: LineSegment StartX=-49.7182 StartY=23.3876 StartZ=0 EndX=-48.54 EndY=22.8382 EndZ=0
    g7: LineSegment StartX=-48.54 StartY=22.8382 StartZ=0 EndX=-47.9483 EndY=24.107 EndZ=0
    g8: LineSegment StartX=-35.8517 StartY=16.9215 StartZ=0 EndX=-36.9505 EndY=14.5651 EndZ=0
    g9: LineSegment StartX=-48.54 StartY=22.8382 StartZ=0 EndX=-49.6388 EndY=20.4818 EndZ=0
    g10: LineSegment StartX=-49.7182 StartY=23.3876 StartZ=0 EndX=-49.1265 EndY=24.6564 EndZ=0
    g11: LineSegment StartX=-34.6735 StartY=16.3721 StartZ=0 EndX=-34.0818 EndY=17.641 EndZ=0
    g12: LineSegment StartX=-50.817 StartY=21.0312 StartZ=0 EndX=-43.2946 EndY=17.5235 EndZ=0
    g13: LineSegment StartX=-43.2946 StartY=17.5235 StartZ=0 EndX=-35.7723 EndY=14.0157 EndZ=0
    g14: LineSegment StartX=-41.6042 StartY=21.1487 StartZ=0 EndX=-43.2946 EndY=17.5235 EndZ=0
    g15: LineSegment StartX=-30.1535 StartY=12.2441 StartZ=0 EndX=-29.702 EndY=14.8046 EndZ=0
    g16: LineSegment StartX=-29.702 StartY=14.8046 StartZ=0 EndX=-28.4217 EndY=14.5789 EndZ=0
    g17: LineSegment StartX=-28.4217 StartY=14.5789 StartZ=0 EndX=-28.1786 EndY=15.9576 EndZ=0
    g18: LineSegment StartX=-28.1786 StartY=15.9576 StartZ=0 EndX=-21.285 EndY=14.7421 EndZ=0
    g19: LineSegment StartX=-21.285 StartY=14.7421 StartZ=0 EndX=-14.3913 EndY=13.5265 EndZ=0
    g20: LineSegment StartX=-14.3913 StartY=13.5265 StartZ=0 EndX=-14.6344 EndY=12.1478 EndZ=0
    g21: LineSegment StartX=-14.6344 StartY=12.1478 StartZ=0 EndX=-13.3542 EndY=11.9221 EndZ=0
    g22: LineSegment StartX=-13.3542 StartY=11.9221 StartZ=0 EndX=-13.8057 EndY=9.36157 EndZ=0
    g23: LineSegment StartX=-13.8057 StartY=9.36157 StartZ=0 EndX=-21.9796 EndY=10.8028 EndZ=0
    g24: LineSegment StartX=-21.9796 StartY=10.8028 StartZ=0 EndX=-30.1535 EndY=12.2441 EndZ=0
    g25: LineSegment StartX=-29.702 StartY=14.8046 StartZ=0 EndX=-29.4589 EndY=16.1834 EndZ=0
    g26: LineSegment StartX=-21.285 StartY=14.7421 StartZ=0 EndX=-21.9796 EndY=10.8028 EndZ=0
    g27: LineSegment StartX=-13.3542 StartY=11.9221 StartZ=0 EndX=-13.1111 EndY=13.3008 EndZ=0
    g28: LineSegment StartX=-14.6344 StartY=12.1478 StartZ=0 EndX=-15.0859 EndY=9.58731 EndZ=0
    g29: LineSegment StartX=-28.8732 StartY=12.0184 StartZ=0 EndX=-28.4217 EndY=14.5789 EndZ=0
    g30: LineSegment StartX=-8.1464 StartY=11.6947 StartZ=0 EndX=-6.85134 EndY=11.808 EndZ=0
    g31: LineSegment StartX=-6.85134 StartY=11.808 StartZ=0 EndX=-6.97336 EndY=13.2027 EndZ=0
    g32: LineSegment StartX=-6.97336 StartY=13.2027 StartZ=0 EndX=0 EndY=13.8128 EndZ=0
    g33: LineSegment StartX=0 StartY=13.8128 StartZ=0 EndX=6.97336 EndY=14.4228 EndZ=0
    g34: LineSegment StartX=6.97336 StartY=14.4228 StartZ=0 EndX=7.09538 EndY=13.0282 EndZ=0
    g35: LineSegment StartX=7.09538 StartY=13.0282 StartZ=0 EndX=8.39043 EndY=13.1415 EndZ=0
    g36: LineSegment StartX=8.39043 StartY=13.1415 StartZ=0 EndX=8.61704 EndY=10.5514 EndZ=0
    g37: LineSegment StartX=8.61704 StartY=10.5514 StartZ=0 EndX=0.348623 EndY=9.82798 EndZ=0
    g38: LineSegment StartX=0.348623 StartY=9.82798 StartZ=0 EndX=-7.91979 EndY=9.10459 EndZ=0
    g39: LineSegment StartX=-7.91979 StartY=9.10459 StartZ=0 EndX=-8.1464 EndY=11.6947 EndZ=0
    g40: LineSegment StartX=-8.1464 StartY=11.6947 StartZ=0 EndX=-8.26842 EndY=13.0894 EndZ=0
    g41: LineSegment StartX=0 StartY=13.8128 StartZ=0 EndX=0.348623 EndY=9.82798 EndZ=0
    g42: LineSegment StartX=7.32199 StartY=10.4381 StartZ=0 EndX=7.09538 EndY=13.0282 EndZ=0
    g43: LineSegment StartX=8.39043 StartY=13.1415 StartZ=0 EndX=8.26842 EndY=14.5362 EndZ=0
    g44: LineSegment StartX=-6.85134 StartY=11.808 StartZ=0 EndX=-6.62474 EndY=9.21789 EndZ=0
    g45: LineSegment StartX=14.2224 StartY=16.0299 StartZ=0 EndX=20.8002 EndY=18.4241 EndZ=0
    g46: LineSegment StartX=20.8002 StartY=18.4241 StartZ=0 EndX=27.3781 EndY=20.8182 EndZ=0
    g47: LineSegment StartX=27.3781 StartY=20.8182 StartZ=0 EndX=27.8569 EndY=19.5026 EndZ=0
    g48: LineSegment StartX=27.8569 StartY=19.5026 StartZ=0 EndX=29.0785 EndY=19.9473 EndZ=0
    g49: LineSegment StartX=29.0785 StartY=19.9473 StartZ=0 EndX=29.9678 EndY=17.5041 EndZ=0
    g50: LineSegment StartX=29.9678 StartY=17.5041 StartZ=0 EndX=22.1683 EndY=14.6653 EndZ=0
    g51: LineSegment StartX=22.1683 StartY=14.6653 StartZ=0 EndX=14.3689 EndY=11.8265 EndZ=0
    g52: LineSegment StartX=14.3689 StartY=11.8265 StartZ=0 EndX=13.4796 EndY=14.2697 EndZ=0
    g53: LineSegment StartX=13.4796 StartY=14.2697 StartZ=0 EndX=14.7012 EndY=14.7144 EndZ=0
    g54: LineSegment StartX=14.7012 StartY=14.7144 StartZ=0 EndX=14.2224 EndY=16.0299 EndZ=0
    g55: LineSegment StartX=20.8002 StartY=18.4241 StartZ=0 EndX=22.1683 EndY=14.6653 EndZ=0
    g56: LineSegment StartX=29.0785 StartY=19.9473 StartZ=0 EndX=28.5997 EndY=21.2628 EndZ=0
    g57: LineSegment StartX=27.8569 StartY=19.5026 StartZ=0 EndX=28.7462 EndY=17.0594 EndZ=0
    g58: LineSegment StartX=14.7012 StartY=14.7144 StartZ=0 EndX=15.5905 EndY=12.2711 EndZ=0
    g59: LineSegment StartX=13.4796 StartY=14.2697 StartZ=0 EndX=13.0008 EndY=15.5853 EndZ=0
    g60: LineSegment StartX=33.7023 StartY=22.3542 StartZ=0 EndX=34.7672 EndY=23.0999 EndZ=0
    g61: LineSegment StartX=34.7672 StartY=23.0999 StartZ=0 EndX=33.9642 EndY=24.2467 EndZ=0
    g62: LineSegment StartX=33.9642 StartY=24.2467 StartZ=0 EndX=39.6982 EndY=28.2617 EndZ=0
    g63: LineSegment StartX=39.6982 StartY=28.2617 StartZ=0 EndX=45.4323 EndY=32.2768 EndZ=0
    g64: LineSegment StartX=45.4323 StartY=32.2768 StartZ=0 EndX=46.2353 EndY=31.13 EndZ=0
    g65: LineSegment StartX=46.2353 StartY=31.13 StartZ=0 EndX=47.3002 EndY=31.8756 EndZ=0
    g66: LineSegment StartX=47.3002 StartY=31.8756 StartZ=0 EndX=48.7915 EndY=29.7458 EndZ=0
    g67: LineSegment StartX=48.7915 StartY=29.7458 StartZ=0 EndX=41.9925 EndY=24.9851 EndZ=0
    g68: LineSegment StartX=41.9925 StartY=24.9851 StartZ=0 EndX=35.1936 EndY=20.2244 EndZ=0
    g69: LineSegment StartX=35.1936 StartY=20.2244 StartZ=0 EndX=33.7023 EndY=22.3542 EndZ=0
    g70: LineSegment StartX=33.7023 StartY=22.3542 StartZ=0 EndX=32.8993 EndY=23.5011 EndZ=0
    g71: LineSegment StartX=46.4972 StartY=33.0224 StartZ=0 EndX=47.3002 EndY=31.8756 EndZ=0
    g72: LineSegment StartX=39.6982 StartY=28.2617 StartZ=0 EndX=41.9925 EndY=24.9851 EndZ=0
    g73: LineSegment StartX=36.2585 StartY=20.9701 StartZ=0 EndX=34.7672 EndY=23.0999 EndZ=0
    g74: LineSegment StartX=46.2353 StartY=31.13 StartZ=0 EndX=47.7266 EndY=29.0002 EndZ=0
  constraints (215):
    c: PointOnObject(g0,g-4)
    c: Coincident(g0,g-4)
    c: Coincident(g0,g1)
    c: PointOnObject(g1,g-3)
    c: Coincident(g1,g2)
    c: Coincident(g2,g3)
    c: Coincident(g3,g4)
    c: PointOnObject(g4,g-5)
    c: PointOnObject(g5,g-5)
    c: Coincident(g5,g6)
    c: Coincident(g6,g7)
    c: Coincident(g7,g0)
    c: Perpendicular(g-5,g5)
    c: Perpendicular(g-5,g4)
    c: Coincident(g8,g2)
    c: Coincident(g9,g6)
    c: Coincident(g10,g5)
    c: PointOnObject(g10,g-4)
    c: Coincident(g11,g3)
    c: PointOnObject(g11,g-3)
    c: Angle(g4,g11) = 3.14159
    c: Angle(g8,g2) = 3.14159
    c: Angle(g9,g7) = 3.14159
    c: Angle(g5,g10) = 3.14159
    c: Perpendicular(g-3,g2)
    c: Perpendicular(g-4,g7)
    c: Equal(g11,g2)
    c: Equal(g2,g7)
    c: Equal(g7,g10)
    c: Distance(g2) = 1.4
    c: Distance(g0,g1) = 14
    c: Equal(g0,g1)
    c: Coincident(g5,g12)
    c: PointOnObject(g12,g-5)
    c: Coincident(g12,g13)
    c: Coincident(g13,g4)
    c: Coincident(g14,g0)
    c: Coincident(g14,g12)
    c: Perpendicular(g-5,g14)
    c: Equal(g12,g13)
    c: Distance(g4,g5) = 16.6
    c: PointOnObject(g8,g-5)
    c: PointOnObject(g9,g-5)
    c: PointOnObject(g15,g-8)
    c: Coincident(g15,g16)
    c: Coincident(g16,g17)
    c: PointOnObject(g17,g-6)
    c: Coincident(g17,g18)
    c: Coincident(g18,g-7)
    c: Coincident(g18,g19)
    c: PointOnObject(g19,g-7)
    c: Coincident(g19,g20)
    c: Coincident(g20,g21)
    c: Coincident(g21,g22)
    c: PointOnObject(g22,g-8)
    c: Coincident(g22,g23)
    c: PointOnObject(g23,g-8)
    c: Coincident(g23,g24)
    c: Coincident(g15,g24)
    c: Coincident(g25,g15)
    c: PointOnObject(g25,g-6)
    c: Coincident(g26,g18)
    c: Coincident(g26,g23)
    c: Coincident(g27,g21)
    c: PointOnObject(g27,g-7)
    c: Coincident(g28,g20)
    c: PointOnObject(g28,g23)
    c: PointOnObject(g29,g24)
    c: Coincident(g29,g16)
    c: Angle(g25,g15) = 3.14159
    c: Angle(g17,g29) = 3.14159
    c: Angle(g20,g28) = 3.14159
    c: Angle(g22,g27) = 3.14159
    c: Perpendicular(g-7,g20)
    c: Perpendicular(g-8,g22)
    c: Perpendicular(g-8,g15)
    c: Perpendicular(g17,g-6)
    c: Perpendicular(g-8,g26)
    c: Equal(g23,g24)
    c: Equal(g18,g19)
    c: Equal(g27,g20)
    c: Equal(g20,g17)
    c: Equal(g17,g25)
    c: Distance(g20) = 1.4
    c: Distance(g19,g17) = 14
    c: Distance(g22,g15) = 16.6
    c: Coincident(g30,g31)
    c: PointOnObject(g31,g-9)
    c: Coincident(g31,g32)
    c: Coincident(g32,g-10)
    c: Coincident(g32,g33)
    c: PointOnObject(g33,g-10)
    c: Coincident(g33,g34)
    c: Coincident(g34,g35)
    c: Coincident(g35,g36)
    c: PointOnObject(g36,g-11)
    c: Coincident(g36,g37)
    c: PointOnObject(g37,g-11)
    c: Coincident(g37,g38)
    c: PointOnObject(g38,g-11)
    c: Coincident(g38,g39)
    c: Coincident(g39,g30)
    c: Coincident(g40,g30)
    c: PointOnObject(g40,g-9)
    c: Coincident(g41,g32)
    c: Coincident(g41,g37)
    c: PointOnObject(g42,g37)
    c: Coincident(g42,g34)
    c: Coincident(g43,g35)
    c: PointOnObject(g43,g-10)
    c: Angle(g36,g43) = 3.14159
    c: Angle(g42,g34) = 3.14159
    c: Angle(g39,g40) = 3.14159
    c: Coincident(g44,g30)
    c: PointOnObject(g44,g38)
    c: Angle(g31,g44) = 3.14159
    c: Equal(g40,g31)
    c: Equal(g31,g34)
    c: Equal(g34,g43)
    c: Perpendicular(g-10,g43)
    c: Perpendicular(g-10,g34)
    c: Perpendicular(g-9,g31)
    c: Perpendicular(g-9,g40)
    c: Perpendicular(g-11,g41)
    c: Distance(g33,g31) = 14
    c: Distance(g38,g36) = 16.6
    c: Distance(g34) = 1.4
    c: Equal(g33,g32)
    c: Equal(g38,g37)
    c: PointOnObject(g45,g-13)
    c: Coincident(g45,g-14)
    c: Coincident(g45,g46)
    c: PointOnObject(g46,g-14)
    c: Coincident(g46,g47)
    c: Coincident(g47,g48)
    c: Coincident(g48,g49)
    c: PointOnObject(g49,g-12)
    c: Coincident(g49,g50)
    c: PointOnObject(g50,g-12)
    c: Coincident(g50,g51)
    c: PointOnObject(g51,g-12)
    c: Coincident(g51,g52)
    c: Coincident(g52,g53)
    c: Coincident(g53,g54)
    c: Coincident(g54,g45)
    c: Coincident(g55,g45)
    c: Coincident(g55,g50)
    c: Coincident(g56,g48)
    c: PointOnObject(g56,g-14)
    c: Coincident(g57,g47)
    c: PointOnObject(g57,g50)
    c: Coincident(g58,g53)
    c: PointOnObject(g58,g51)
    c: PointOnObject(g59,g-13)
    c: Coincident(g59,g52)
    c: Angle(g52,g59) = 3.14159
    c: Angle(g58,g54) = 3.14159
    c: Angle(g47,g57) = 3.14159
    c: Angle(g56,g49) = 3.14159
    c: Distance(g46,g45) = 14
    c: Distance(g51,g49) = 16.6
    c: Distance(g47) = 1.4
    c: Equal(g56,g47)
    c: Equal(g47,g54)
    c: Equal(g54,g59)
    c: Equal(g45,g46)
    c: Equal(g51,g50)
    c: Perpendicular(g-12,g55)
    c: Perpendicular(g-12,g52)
    c: Perpendicular(g-13,g54)
    c: Perpendicular(g-14,g47)
    c: Perpendicular(g49,g-12)
    c: Coincident(g60,g61)
    c: PointOnObject(g61,g-15)
    c: Coincident(g61,g62)
    c: Coincident(g62,g-17)
    c: Coincident(g62,g63)
    c: PointOnObject(g63,g-17)
    c: Coincident(g63,g64)
    c: Coincident(g64,g65)
    c: Coincident(g65,g66)
    c: PointOnObject(g66,g-16)
    c: Coincident(g66,g67)
    c: PointOnObject(g67,g-16)
    c: Coincident(g67,g68)
    c: PointOnObject(g68,g-16)
    c: Coincident(g68,g69)
    c: Coincident(g69,g60)
    c: Coincident(g70,g60)
    c: PointOnObject(g70,g-15)
    c: PointOnObject(g71,g-17)
    c: Coincident(g71,g65)
    c: Coincident(g72,g62)
    c: Coincident(g72,g67)
    c: PointOnObject(g73,g68)
    c: Coincident(g73,g60)
    c: PointOnObject(g74,g67)
    c: Coincident(g64,g74)
    c: Angle(g66,g71) = 3.14159
    c: Angle(g74,g64) = 3.14159
    c: Angle(g61,g73) = 3.14159
    c: Angle(g70,g69) = 3.14159
    c: Perpendicular(g-16,g69)
    c: Perpendicular(g-15,g61)
    c: Perpendicular(g-17,g64)
    c: Perpendicular(g-16,g66)
    c: Equal(g64,g71)
    c: Equal(g71,g61)
    c: Equal(g61,g70)
    c: Equal(g62,g63)
    c: Equal(g67,g68)
    c: Perpendicular(g-15,g72)
    c: Distance(g64) = 1.4
    c: Distance(g63,g61) = 14
    c: Distance(g66,g68) = 16.6
FEATURE [PartDesign::Pocket] Pocket006  label="MMX Sockets"
  BaseFeature = -> Pad012
  Direction = (-1,2e-16,-3e-16)
  Length = 14
  Length2 = 100
  Midplane = true
  Placement = pos=(0,0,0) rot=(0.57735,0.57735,0.57735;2.0944rad)
  Profile = -> Sketch021
  Type = 0
FEATURE [Sketcher::SketchObject] Sketch022
  ExternalGeometry = -> [Sketch021]
  FullyConstrained = true
  MapMode = 5
  Placement = pos=(0,0,0) rot=(0.57735,0.57735,0.57735;2.0944rad)
  Support = -> [YZ_Plane003]
  sketch-geometry (55):
    g0: LineSegment StartX=-48.4555 StartY=23.0195 StartZ=0 EndX=-35.7672 EndY=17.1028 EndZ=0
    g1: LineSegment StartX=-35.7672 StartY=17.1028 StartZ=0 EndX=-35.8517 EndY=16.9215 EndZ=0
    g2: LineSegment StartX=-35.8517 StartY=16.9215 StartZ=0 EndX=-34.6735 EndY=16.3721 EndZ=0
    g3: LineSegment StartX=-34.6735 StartY=16.3721 StartZ=0 EndX=-35.0116 EndY=15.6471 EndZ=0
    g4: LineSegment StartX=-35.0116 StartY=15.6471 StartZ=0 EndX=-50.0563 EndY=22.6626 EndZ=0
    g5: LineSegment StartX=-50.0563 StartY=22.6626 StartZ=0 EndX=-49.7182 EndY=23.3876 EndZ=0
    g6: LineSegment StartX=-49.7182 StartY=23.3876 StartZ=0 EndX=-48.54 EndY=22.8382 EndZ=0
    g7: LineSegment StartX=-48.54 StartY=22.8382 StartZ=0 EndX=-48.4555 EndY=23.0195 EndZ=0
    g8: LineSegment StartX=-41.6042 StartY=21.1487 StartZ=0 EndX=-42.1113 EndY=20.0611 EndZ=0
    g9: LineSegment StartX=-42.1113 StartY=20.0611 StartZ=0 EndX=-42.5339 EndY=19.1548 EndZ=0
    g10: LineSegment StartX=-42.5339 StartY=19.1548 StartZ=0 EndX=-43.2946 EndY=17.5235 EndZ=0
    g11: LineSegment StartX=-28.387 StartY=14.7758 StartZ=0 EndX=-14.5997 EndY=12.3448 EndZ=0
    g12: LineSegment StartX=-14.5997 StartY=12.3448 StartZ=0 EndX=-14.6344 EndY=12.1478 EndZ=0
    g13: LineSegment StartX=-14.6344 StartY=12.1478 StartZ=0 EndX=-13.3542 EndY=11.9221 EndZ=0
    g14: LineSegment StartX=-13.3542 StartY=11.9221 StartZ=0 EndX=-13.4931 EndY=11.1342 EndZ=0
    g15: LineSegment StartX=-13.4931 StartY=11.1342 StartZ=0 EndX=-29.8409 EndY=14.0168 EndZ=0
    g16: LineSegment StartX=-29.8409 StartY=14.0168 StartZ=0 EndX=-29.702 EndY=14.8046 EndZ=0
    g17: LineSegment StartX=-29.702 StartY=14.8046 StartZ=0 EndX=-28.4217 EndY=14.5789 EndZ=0
    g18: LineSegment StartX=-28.4217 StartY=14.5789 StartZ=0 EndX=-28.387 EndY=14.7758 EndZ=0
    g19: LineSegment StartX=-21.285 StartY=14.7421 StartZ=0 EndX=-21.4934 EndY=13.5603 EndZ=0
    g20: LineSegment StartX=-21.667 StartY=12.5755 StartZ=0 EndX=-21.4934 EndY=13.5603 EndZ=0
    g21: LineSegment StartX=-21.667 StartY=12.5755 StartZ=0 EndX=-21.9796 EndY=10.8028 EndZ=0
    g22: LineSegment StartX=-6.86878 StartY=12.0072 StartZ=0 EndX=7.07795 EndY=13.2274 EndZ=0
    g23: LineSegment StartX=7.07795 StartY=13.2274 StartZ=0 EndX=7.09538 EndY=13.0282 EndZ=0
    g24: LineSegment StartX=7.09538 StartY=13.0282 StartZ=0 EndX=8.39043 EndY=13.1415 EndZ=0
    g25: LineSegment StartX=8.39043 StartY=13.1415 StartZ=0 EndX=8.46016 EndY=12.3445 EndZ=0
    g26: LineSegment StartX=8.46016 StartY=12.3445 StartZ=0 EndX=-8.07667 EndY=10.8977 EndZ=0
    g27: LineSegment StartX=-8.07667 StartY=10.8977 StartZ=0 EndX=-8.1464 EndY=11.6947 EndZ=0
    g28: LineSegment StartX=-8.1464 StartY=11.6947 StartZ=0 EndX=-6.85134 EndY=11.808 EndZ=0
    g29: LineSegment StartX=-6.85134 StartY=11.808 StartZ=0 EndX=-6.86878 EndY=12.0072 EndZ=0
    g30: LineSegment StartX=5.8389e-12 StartY=13.8128 StartZ=0 EndX=0.104587 EndY=12.6173 EndZ=0
    g31: LineSegment StartX=0.104587 StartY=12.6173 StartZ=0 EndX=0.191743 EndY=11.6211 EndZ=0
    g32: LineSegment StartX=0.191743 StartY=11.6211 StartZ=0 EndX=0.348623 EndY=9.82798 EndZ=0
    g33: LineSegment StartX=14.6328 StartY=14.9023 StartZ=0 EndX=27.7885 EndY=19.6906 EndZ=0
    g34: LineSegment StartX=27.7885 StartY=19.6906 StartZ=0 EndX=27.8569 EndY=19.5026 EndZ=0
    g35: LineSegment StartX=27.8569 StartY=19.5026 StartZ=0 EndX=29.0785 EndY=19.9473 EndZ=0
    g36: LineSegment StartX=29.0785 StartY=19.9473 StartZ=0 EndX=29.3521 EndY=19.1955 EndZ=0
    g37: LineSegment StartX=29.3521 StartY=19.1955 StartZ=0 EndX=13.7532 EndY=13.518 EndZ=0
    g38: LineSegment StartX=13.7532 StartY=13.518 StartZ=0 EndX=13.4796 EndY=14.2697 EndZ=0
    g39: LineSegment StartX=13.4796 StartY=14.2697 StartZ=0 EndX=14.7012 EndY=14.7144 EndZ=0
    g40: LineSegment StartX=14.7012 StartY=14.7144 StartZ=0 EndX=14.6328 EndY=14.9023 EndZ=0
    g41: LineSegment StartX=20.8002 StartY=18.4241 StartZ=0 EndX=21.2107 EndY=17.2964 EndZ=0
    g42: LineSegment StartX=21.2107 StartY=17.2964 StartZ=0 EndX=21.5527 EndY=16.3567 EndZ=0
    g43: LineSegment StartX=21.5527 StartY=16.3567 StartZ=0 EndX=22.1683 EndY=14.6653 EndZ=0
    g44: LineSegment StartX=34.6525 StartY=23.2637 StartZ=0 EndX=46.1206 EndY=31.2938 EndZ=0
    g45: LineSegment StartX=46.1206 StartY=31.2938 StartZ=0 EndX=46.2353 EndY=31.13 EndZ=0
    g46: LineSegment StartX=46.2353 StartY=31.13 StartZ=0 EndX=47.3002 EndY=31.8756 EndZ=0
    g47: LineSegment StartX=47.3002 StartY=31.8756 StartZ=0 EndX=47.7591 EndY=31.2203 EndZ=0
    g48: LineSegment StartX=47.7591 StartY=31.2203 StartZ=0 EndX=34.1611 EndY=21.6989 EndZ=0
    g49: LineSegment StartX=34.1611 StartY=21.6989 StartZ=0 EndX=33.7023 EndY=22.3542 EndZ=0
    g50: LineSegment StartX=33.7023 StartY=22.3542 StartZ=0 EndX=34.7672 EndY=23.0999 EndZ=0
    g51: LineSegment StartX=34.7672 StartY=23.0999 StartZ=0 EndX=34.6525 EndY=23.2637 EndZ=0
    g52: LineSegment StartX=39.6982 StartY=28.2617 StartZ=0 EndX=40.3865 EndY=27.2788 EndZ=0
    g53: LineSegment StartX=40.3865 StartY=27.2788 StartZ=0 EndX=40.9601 EndY=26.4596 EndZ=0
    g54: LineSegment StartX=40.9601 StartY=26.4596 StartZ=0 EndX=41.9925 EndY=24.9851 EndZ=0
  constraints (140):
    c: PointOnObject(g0,g-5)
    c: Coincident(g0,g1)
    c: Coincident(g1,g-5)
    c: Coincident(g1,g2)
    c: Coincident(g2,g-6)
    c: Coincident(g2,g3)
    c: PointOnObject(g3,g-6)
    c: Coincident(g3,g4)
    c: PointOnObject(g4,g-4)
    c: Coincident(g4,g5)
    c: Coincident(g5,g-4)
    c: Coincident(g5,g6)
    c: Coincident(g6,g-3)
    c: Coincident(g6,g7)
    c: Coincident(g7,g0)
    c: PointOnObject(g0,g-3)
    c: Coincident(g8,g-23)
    c: PointOnObject(g8,g0)
    c: Coincident(g8,g9)
    c: PointOnObject(g9,g4)
    c: Coincident(g9,g10)
    c: Coincident(g10,g-24)
    c: Angle(g9,g8) = 3.14159
    c: Distance(g8) = 1.2
    c: Distance(g9) = 1
    c: Perpendicular(g0,g8)
    c: Perpendicular(g9,g4)
    c: Angle(g9,g10) = 3.14159
    c: PointOnObject(g11,g-7)
    c: PointOnObject(g11,g-9)
    c: Coincident(g11,g12)
    c: Coincident(g12,g-9)
    c: Coincident(g12,g13)
    c: Coincident(g13,g14)
    c: PointOnObject(g14,g-10)
    c: Coincident(g14,g15)
    c: PointOnObject(g15,g-8)
    c: Coincident(g15,g16)
    c: Coincident(g16,g-8)
    c: Coincident(g16,g17)
    c: Coincident(g17,g-7)
    c: Coincident(g17,g18)
    c: Coincident(g18,g11)
    c: Coincident(g-10,g13)
    c: Coincident(g19,g-25)
    c: PointOnObject(g19,g11)
    c: PointOnObject(g20,g15)
    c: Coincident(g20,g19)
    c: Coincident(g21,g-26)
    c: Coincident(g21,g20)
    c: Angle(g21,g20) = 3.14159
    c: Angle(g19,g20) = 3.14159
    c: Distance(g19) = 1.2
    c: Distance(g20) = 1
    c: Perpendicular(g19,g11)
    c: Perpendicular(g21,g15)
    c: PointOnObject(g22,g-11)
    c: PointOnObject(g22,g-13)
    c: Coincident(g22,g23)
    c: Coincident(g23,g-13)
    c: Coincident(g23,g24)
    c: Coincident(g24,g-14)
    c: Coincident(g24,g25)
    c: PointOnObject(g25,g-14)
    c: Coincident(g25,g26)
    c: PointOnObject(g26,g-12)
    c: Coincident(g26,g27)
    c: Coincident(g27,g-12)
    c: Coincident(g27,g28)
    c: Coincident(g28,g-11)
    c: Coincident(g28,g29)
    c: Coincident(g29,g22)
    c: Coincident(g-28,g30)
    c: PointOnObject(g30,g22)
    c: Coincident(g30,g31)
    c: PointOnObject(g31,g26)
    c: Coincident(g31,g32)
    c: Angle(g32,g31) = 3.14159
    c: Angle(g31,g30) = 3.14159
    c: Perpendicular(g22,g31)
    c: Perpendicular(g26,g31)
    c: Distance(g30) = 1.2
    c: Distance(g31) = 1
    c: Coincident(g32,g-27)
    c: PointOnObject(g33,g-16)
    c: PointOnObject(g33,g-17)
    c: Coincident(g33,g34)
    c: Coincident(g34,g-17)
    c: Coincident(g34,g35)
    c: Coincident(g35,g-18)
    c: Coincident(g35,g36)
    c: PointOnObject(g36,g-18)
    c: Coincident(g36,g37)
    c: PointOnObject(g37,g-15)
    c: Coincident(g37,g38)
    c: Coincident(g38,g-15)
    c: Coincident(g38,g39)
    c: Coincident(g39,g-16)
    c: Coincident(g39,g40)
    c: Coincident(g40,g33)
    c: Coincident(g41,g-29)
    c: PointOnObject(g41,g33)
    c: Coincident(g41,g42)
    c: PointOnObject(g42,g37)
    c: Coincident(g42,g43)
    c: Coincident(g43,g-30)
    c: Angle(g42,g43) = 3.14159
    c: Angle(g41,g42) = 3.14159
    c: Distance(g41) = 1.2
    c: Distance(g42) = 1
    c: Perpendicular(g41,g33)
    c: Perpendicular(g42,g37)
    c: PointOnObject(g44,g-20)
    c: PointOnObject(g44,g-21)
    c: Coincident(g44,g45)
    c: Coincident(g45,g-21)
    c: Coincident(g45,g46)
    c: Coincident(g46,g-22)
    c: Coincident(g46,g47)
    c: PointOnObject(g47,g-22)
    c: Coincident(g47,g48)
    c: PointOnObject(g48,g-19)
    c: Coincident(g48,g49)
    c: Coincident(g49,g-19)
    c: Coincident(g49,g50)
    c: Coincident(g50,g-20)
    c: Coincident(g50,g51)
    c: Coincident(g51,g44)
    c: Coincident(g52,g-31)
    c: PointOnObject(g52,g44)
    c: Coincident(g52,g53)
    c: PointOnObject(g53,g48)
    c: Coincident(g53,g54)
    c: Coincident(g54,g-32)
    c: Angle(g53,g54) = 3.14159
    c: Angle(g53,g52) = 3.14159
    c: Distance(g52) = 1.2
    c: Distance(g53) = 1
    c: Perpendicular(g52,g44)
    c: Perpendicular(g48,g53)
FEATURE [PartDesign::Pocket] Pocket007  label="MChoc Sockets"
  BaseFeature = -> Pocket006
  Direction = (-1,2e-16,-3e-16)
  Length = 14.6
  Length2 = 100
  Midplane = true
  Placement = pos=(0,0,0) rot=(0.57735,0.57735,0.57735;2.0944rad)
  Profile = -> Sketch022
  Type = 0
FEATURE [Sketcher::SketchObject] Sketch023
  ExternalGeometry = -> [Sketch020]
  FullyConstrained = true
  MapMode = 5
  Placement = pos=(0,0,0) rot=(0.57735,0.57735,0.57735;2.0944rad)
  Support = -> [YZ_Plane003]
  expr: Constraints[39] = <<Spreadsheet>>.Wiring
  sketch-geometry (16):
    g0: LineSegment StartX=-11.9293 StartY=13.0924 StartZ=0 EndX=-9.46385 EndY=12.9848 EndZ=0
    g1: LineSegment StartX=-9.46385 StartY=12.9848 StartZ=0 EndX=-9.11523 EndY=9 EndZ=0
    g2: LineSegment StartX=-9.11523 StartY=9 StartZ=0 EndX=-8.59229 EndY=3.02283 EndZ=0
    g3: LineSegment StartX=-8.59229 StartY=3.02283 StartZ=0 EndX=-8.59229 EndY=0 EndZ=0
    g4: LineSegment StartX=-8.59229 StartY=0 StartZ=0 EndX=-13.6658 EndY=0 EndZ=0
    g5: LineSegment StartX=-13.6658 StartY=0 StartZ=0 EndX=-13.6658 EndY=3.24435 EndZ=0
    g6: LineSegment StartX=-13.6658 StartY=3.24435 StartZ=0 EndX=-12.6239 EndY=9.15319 EndZ=0
    g7: LineSegment StartX=-12.6239 StartY=9.15319 StartZ=0 EndX=-11.9293 EndY=13.0924 EndZ=0
    g8: LineSegment StartX=9.81247 StartY=10.656 StartZ=0 EndX=9.46385 EndY=14.6407 EndZ=0
    g9: LineSegment StartX=9.46385 StartY=14.6407 StartZ=0 EndX=11.8732 EndY=15.1749 EndZ=0
    g10: LineSegment StartX=11.8732 StartY=15.1749 StartZ=0 EndX=13.2412 EndY=11.4161 EndZ=0
    g11: LineSegment StartX=13.2412 StartY=11.4161 StartZ=0 EndX=15.2934 EndY=5.77794 EndZ=0
    g12: LineSegment StartX=15.2934 StartY=5.77794 StartZ=0 EndX=15.2934 EndY=0 EndZ=0
    g13: LineSegment StartX=15.2934 StartY=0 StartZ=0 EndX=10.3354 EndY=0 EndZ=0
    g14: LineSegment StartX=10.3354 StartY=0 StartZ=0 EndX=10.3354 EndY=4.67879 EndZ=0
    g15: LineSegment StartX=10.3354 StartY=4.67879 StartZ=0 EndX=9.81247 EndY=10.656 EndZ=0
  constraints (40):
    c: Coincident(g-3,g0)
    c: Coincident(g0,g-3)
    c: Coincident(g0,g1)
    c: Coincident(g1,g-4)
    c: Coincident(g1,g2)
    c: Coincident(g2,g3)
    c: PointOnObject(g3,g-1)
    c: Vertical(g3)
    c: Coincident(g3,g4)
    c: PointOnObject(g4,g-1)
    c: Coincident(g4,g5)
    c: Vertical(g5)
    c: Coincident(g5,g6)
    c: Coincident(g6,g-4)
    c: Coincident(g6,g7)
    c: Coincident(g7,g0)
    c: Angle(g1,g2) = 3.14159
    c: Angle(g6,g7) = 3.14159
    c: Coincident(g-6,g8)
    c: Coincident(g8,g-5)
    c: Coincident(g8,g9)
    c: Coincident(g9,g-5)
    c: Coincident(g9,g10)
    c: Coincident(g10,g-6)
    c: Coincident(g10,g11)
    c: Coincident(g11,g12)
    c: PointOnObject(g12,g-1)
    c: Coincident(g12,g13)
    c: PointOnObject(g13,g-1)
    c: Coincident(g13,g14)
    c: Vertical(g14)
    c: Coincident(g14,g15)
    c: Coincident(g15,g8)
    c: Vertical(g12)
    c: Angle(g10,g11) = 3.14159
    c: Angle(g8,g15) = 3.14159
    c: Equal(g11,g15)
    c: Equal(g15,g2)
    c: Equal(g2,g6)
    c: Distance(g6) = 6
FEATURE [PartDesign::Pad] Pad013  label="MInner Legs"
  BaseFeature = -> Pocket007
  Direction = (1,-2e-16,3e-16)
  Length = 4.1
  Length2 = 9.5
  Placement = pos=(0,0,0) rot=(0.57735,0.57735,0.57735;2.0944rad)
  Profile = -> Sketch023
  ReferenceAxis = -> Sketch023 [N_Axis]
  Type = 4
  expr: Length = <<Spreadsheet>>.ScrewD / 2 + 2mm
FEATURE [Sketcher::SketchObject] Sketch024
  ExternalGeometry = -> [Sketch020]
  FullyConstrained = true
  MapMode = 5
  Placement = pos=(0,0,0) rot=(0.57735,0.57735,0.57735;2.0944rad)
  Support = -> [YZ_Plane003]
  expr: Constraints[27] = <<Spreadsheet>>.Wiring
  expr: Constraints[36] = <<Spreadsheet>>.ArchLength - 5mm
  expr: Constraints[37] = <<Spreadsheet>>.ArchLength
  expr: Constraints[38] = <<Spreadsheet>>.ArchLength - 5mm
  expr: Constraints[39] = <<Spreadsheet>>.ArchLength
  expr: Constraints[40] = <<Spreadsheet>>.ArchLength - 10mm
  expr: Constraints[41] = <<Spreadsheet>>.ArchLength - 10mm
  sketch-geometry (36):
    g0: LineSegment StartX=-35 StartY=0 StartZ=0 EndX=-32.3771 EndY=6.54366 EndZ=0
    g1: LineSegment StartX=-32.3771 StartY=6.54366 StartZ=0 EndX=-31.3353 EndY=12.4525 EndZ=0
    g2: LineSegment StartX=-31.3353 StartY=12.4525 StartZ=0 EndX=-30.6407 EndY=16.3917 EndZ=0
    g3: LineSegment StartX=-30.6407 StartY=16.3917 StartZ=0 EndX=-32.9942 EndY=17.1338 EndZ=0
    g4: LineSegment StartX=-32.9942 StartY=17.1338 StartZ=0 EndX=-34.6847 EndY=13.5086 EndZ=0
    g5: LineSegment StartX=-34.6847 StartY=13.5086 StartZ=0 EndX=-37.2204 EndY=8.07075 EndZ=0
    g6: LineSegment StartX=45 StartY=3 StartZ=0 EndX=45 EndY=0 EndZ=0
    g7: LineSegment StartX=45 StartY=0 StartZ=0 EndX=35 EndY=0 EndZ=0
    g8: LineSegment StartX=35 StartY=0 StartZ=0 EndX=33.1475 EndY=12.2763 EndZ=0
    g9: LineSegment StartX=33.1475 StartY=12.2763 StartZ=0 EndX=31.0954 EndY=17.9145 EndZ=0
    g10: LineSegment StartX=31.0954 StartY=17.9145 StartZ=0 EndX=29.7273 EndY=21.6733 EndZ=0
    g11: LineSegment StartX=29.7273 StartY=21.6733 StartZ=0 EndX=31.9163 EndY=22.8128 EndZ=0
    g12: LineSegment StartX=31.9163 StartY=22.8128 StartZ=0 EndX=34.2106 EndY=19.5362 EndZ=0
    g13: LineSegment StartX=34.2106 StartY=19.5362 StartZ=0 EndX=37.6521 EndY=14.6212 EndZ=0
    g14: LineSegment StartX=-35 StartY=0 StartZ=0 EndX=-45 EndY=0 EndZ=0
    g15: LineSegment StartX=-45 StartY=0 StartZ=0 EndX=-45 EndY=3 EndZ=0
    g16: LineSegment StartX=-45 StartY=3 StartZ=0 EndX=-40 EndY=3 EndZ=0
    g17: LineSegment StartX=40 StartY=3 StartZ=0 EndX=45 EndY=3 EndZ=0
    g18: LineSegment StartX=37.6521 StartY=14.6212 StartZ=0 EndX=42.2621 EndY=8.03739 EndZ=0
    g19: LineSegment StartX=42.2621 StartY=8.03739 StartZ=0 EndX=42.2621 EndY=0 EndZ=0
    g20: LineSegment StartX=-37.2204 StartY=8.07075 StartZ=0 EndX=-39.0097 EndY=4.23371 EndZ=0
    g21: LineSegment StartX=-39.0097 StartY=4.23371 StartZ=0 EndX=-39.0097 EndY=0 EndZ=0
    g22-g25: Circle x4 (B-spline internal-alignment scaffolding for g26; pole/knot coordinates omitted)
    g26: BSplineCurve PolesCount=4 KnotsCount=2 Degree=3 IsPeriodic=0
    g27: GeomPoint X=-37.2204 Y=8.07075 Z=0
    g28: GeomPoint X=-45 Y=3 Z=0
    g29-g32: Circle x4 (B-spline internal-alignment scaffolding for g33; pole/knot coordinates omitted)
    g33: BSplineCurve PolesCount=4 KnotsCount=2 Degree=3 IsPeriodic=0
    g34: GeomPoint X=37.6521 Y=14.6212 Z=0
    g35: GeomPoint X=45 Y=3 Z=0
  constraints (82):
    c: PointOnObject(g0,g-1)
    c: Coincident(g0,g1)
    c: Coincident(g1,g-5)
    c: Coincident(g1,g2)
    c: Coincident(g2,g-6)
    c: Coincident(g2,g3)
    c: Coincident(g3,g-6)
    c: Coincident(g3,g4)
    c: Coincident(g4,g-5)
    c: Coincident(g4,g5)
    c: PointOnObject(g6,g-1)
    c: Vertical(g6)
    c: Coincident(g6,g7)
    c: PointOnObject(g7,g-1)
    c: Coincident(g7,g8)
    c: Coincident(g8,g9)
    c: Coincident(g9,g-4)
    c: Coincident(g9,g10)
    c: Coincident(g10,g-3)
    c: Coincident(g10,g11)
    c: Coincident(g11,g-3)
    c: Coincident(g11,g12)
    c: Coincident(g12,g-4)
    c: Coincident(g12,g13)
    c: Equal(g13,g9)
    c: Equal(g9,g1)
    c: Equal(g1,g5)
    c: Distance(g5) = 6
    c: Coincident(g14,g0)
    c: PointOnObject(g14,g-1)
    c: Coincident(g15,g14)
    c: Vertical(g15)
    c: Coincident(g16,g15)
    c: Horizontal(g16)
    c: Coincident(g17,g6)
    c: Horizontal(g17)
    c: DistanceX(g-7,g17) = 40
    c: DistanceX(g-7,g6) = 45
    c: DistanceX(g16,g-7) = 40
    c: DistanceX(g15,g-7) = 45
    c: DistanceX(g-7,g7) = 35
    c: DistanceX(g0,g-7) = 35
    c: Angle(g1,g2) = 3.14159
    c: Angle(g5,g4) = 3.14159
    c: Angle(g13,g12) = 3.14159
    c: Angle(g9,g10) = 3.14159
    c: Coincident(g13,g18)
    c: Coincident(g18,g19)
    c: PointOnObject(g19,g-1)
    c: Vertical(g19)
    c: Coincident(g5,g20)
    c: Coincident(g20,g21)
    c: PointOnObject(g21,g-1)
    c: Vertical(g21)
    c: Equal(g20,g21)
    c: Equal(g18,g19)
    c: Angle(g18,g13) = 3.14159
    c: DistanceY(g6,g6) = 3
    c: Equal(g15,g6)
    c: Angle(g5,g20) = 3.14159
    c: Coincident(g26,g5)
    c: Weight(g22) = 1
    c: Equal(g22,g23)
    c: Coincident(g23,g20)
    c: Equal(g22,g24)
    c: Coincident(g24,g16)
    c: Equal(g22,g25)
    c: Coincident(g26,g15)
    c: InternalAlignment(g22-g25 -> g26) x4
    c: InternalAlignment(g27,g26)
    c: InternalAlignment(g28,g26)
    c: Coincident(g33,g13)
    c: Weight(g29) = 1
    c: Equal(g29,g30)
    c: Coincident(g30,g18)
    c: Equal(g29,g31)
    c: Coincident(g31,g17)
    c: Equal(g29,g32)
    c: Coincident(g33,g6)
    c: InternalAlignment(g29-g32 -> g33) x4
    c: InternalAlignment(g34,g33)
    c: InternalAlignment(g35,g33)
FEATURE [PartDesign::Pad] Pad014  label="MOuterLegs"
  BaseFeature = -> Pad013
  Direction = (1,-2e-16,3e-16)
  Length = 9.5
  Length2 = 100
  Placement = pos=(0,0,0) rot=(0.57735,0.57735,0.57735;2.0944rad)
  Profile = -> Sketch024
  Reversed = true
  Type = 0
FEATURE [Sketcher::SketchObject] Sketch025
  ExternalGeometry = -> [Sketch024]
  FullyConstrained = true
  MapMode = 5
  Support = -> [XY_Plane003]
  expr: Constraints[21] = <<Spreadsheet>>.NutR
  expr: Constraints[22] = <<Spreadsheet>>.NutR
  expr: Constraints[28] = <<Spreadsheet>>.ScrewD
  expr: Constraints[54] = <<Spreadsheet>>.NutR
  expr: Constraints[55] = <<Spreadsheet>>.NutR
  expr: Constraints[57] = <<Spreadsheet>>.ScrewD
  sketch-geometry (22):
    g0: LineSegment StartX=1.33e-14 StartY=45 StartZ=0 EndX=-9.5 EndY=45 EndZ=0
    g1: LineSegment StartX=-9.5 StartY=45 StartZ=0 EndX=-9.5 EndY=55 EndZ=0
    g2: LineSegment StartX=-9.5 StartY=55 StartZ=0 EndX=4.5 EndY=55 EndZ=0
    g3: ArcOfCircle CenterX=4.5 CenterY=50 CenterZ=0 NormalX=0 NormalY=0 NormalZ=1 AngleXU=0 Radius=5 StartAngle=5.38688 EndAngle=7.85398
    g4: LineSegment StartX=9.5 StartY=50 StartZ=0 EndX=9.5 EndY=55 EndZ=0
    g5: LineSegment StartX=9.5 StartY=55 StartZ=0 EndX=0 EndY=50 EndZ=0
    g6: LineSegment StartX=0 StartY=50 StartZ=0 EndX=-9.5 EndY=55 EndZ=0
    g7: LineSegment StartX=1.33e-14 StartY=45 StartZ=0 EndX=9e-16 EndY=40 EndZ=0
    g8: LineSegment StartX=7.6225 StartY=46.0949 StartZ=0 EndX=9e-16 EndY=40 EndZ=0
    g9: Circle CenterX=0 CenterY=50 CenterZ=0 NormalX=0 NormalY=0 NormalZ=1 AngleXU=0 Radius=2.1
    g10: LineSegment StartX=0 StartY=50 StartZ=0 EndX=9.5 EndY=50 EndZ=0
    g11: LineSegment StartX=-9.8e-15 StartY=-45 StartZ=0 EndX=-9.5 EndY=-45 EndZ=0
    g12: LineSegment StartX=-9.5 StartY=-45 StartZ=0 EndX=-9.5 EndY=-55 EndZ=0
    g13: LineSegment StartX=-9.5 StartY=-55 StartZ=0 EndX=4.5 EndY=-55 EndZ=0
    g14: ArcOfCircle CenterX=4.5 CenterY=-50 CenterZ=0 NormalX=0 NormalY=0 NormalZ=1 AngleXU=0 Radius=5 StartAngle=4.71239 EndAngle=7.17949
    g15: LineSegment StartX=7.6225 StartY=-46.0949 StartZ=0 EndX=-9.8e-15 EndY=-40 EndZ=0
    g16: LineSegment StartX=-9.8e-15 StartY=-40 StartZ=0 EndX=-9.8e-15 EndY=-45 EndZ=0
    g17: LineSegment StartX=9.5 StartY=-50 StartZ=0 EndX=9.5 EndY=-55 EndZ=0
    g18: LineSegment StartX=9.5 StartY=-55 StartZ=0 EndX=0 EndY=-50 EndZ=0
    g19: LineSegment StartX=0 StartY=-50 StartZ=0 EndX=-9.5 EndY=-55 EndZ=0
    g20: LineSegment StartX=0 StartY=-50 StartZ=0 EndX=9.5 EndY=-50 EndZ=0
    g21: Circle CenterX=0 CenterY=-50 CenterZ=0 NormalX=0 NormalY=0 NormalZ=1 AngleXU=0 Radius=2.1
  constraints (58):
    c: Coincident(g0,g-3)
    c: Horizontal(g0)
    c: Coincident(g0,g1)
    c: Vertical(g1)
    c: Coincident(g1,g2)
    c: Tangent(g2,g3) = 1.5708
    c: Horizontal(g2)
    c: PointOnObject(g4,g3)
    c: Vertical(g4)
    c: Coincident(g4,g5)
    c: PointOnObject(g5,g-2)
    c: Coincident(g5,g6)
    c: Coincident(g6,g1)
    c: Coincident(g7,g0)
    c: PointOnObject(g7,g-2)
    c: Coincident(g8,g7)
    c: Tangent(g8,g3) = 1.5708
    c: Equal(g5,g6)
    c: Horizontal(g4,g2)
    c: DistanceX(g1,g4) = 19
    c: Coincident(g9,g5)
    c: DistanceY(g9,g1) = 5
    c: DistanceY(g0,g9) = 5
    c: DistanceY(g7,g7) = 5
    c: Coincident(g10,g9)
    c: Coincident(g10,g4)
    c: Horizontal(g10)
    c: PointOnObject(g3,g10)
    c: Diameter(g9) = 4.2
    c: Coincident(g11,g-4)
    c: Horizontal(g11)
    c: Coincident(g11,g12)
    c: Vertical(g12)
    c: Coincident(g12,g13)
    c: Horizontal(g13)
    c: Tangent(g13,g14) = -1.5708
    c: Tangent(g14,g15) = -1.5708
    c: Coincident(g15,g16)
    c: Coincident(g16,g11)
    c: Vertical(g16)
    c: DistanceY(g16,g16) = 5
    c: PointOnObject(g17,g14)
    c: Coincident(g17,g18)
    c: PointOnObject(g18,g-2)
    c: Coincident(g18,g19)
    c: Coincident(g19,g12)
    c: Equal(g19,g18)
    c: Vertical(g17)
    c: DistanceX(g12,g17) = 19
    c: Horizontal(g17,g13)
    c: Coincident(g20,g18)
    c: Coincident(g20,g17)
    c: Horizontal(g20)
    c: PointOnObject(g14,g20)
    c: DistanceY(g18,g11) = 5
    c: DistanceY(g12,g18) = 5
    c: Coincident(g21,g18)
    c: Diameter(g21) = 4.2
FEATURE [PartDesign::Pad] Pad015  label="Mfeet"
  BaseFeature = -> Pad014
  Direction = (0,0,1)
  Length = 3
  Length2 = 100
  Placement = pos=(0,0,0) rot=(0.57735,0.57735,0.57735;2.0944rad)
  Profile = -> Sketch025
  Type = 0
FEATURE [PartDesign::Body] Body003  label="MiddleArch"
  Group = -> [Sketch020,Pad012,Sketch021,Pocket006,Sketch022,Pocket007,Sketch023,Pad013,Sketch024,Pad014,Sketch025,Pad015]
  Origin = -> Origin003
  Placement = pos=(70,5,0) rot=(0,0,1;0rad)
  Tip = -> Pad015
FEATURE [Sketcher::SketchObject] Sketch026
  FullyConstrained = true
  MapMode = 5
  Placement = pos=(0,0,0) rot=(0.57735,0.57735,0.57735;2.0944rad)
  Support = -> [YZ_Plane004]
  expr: Constraints[136] = <<Spreadsheet>>.Wiring
  expr: Constraints[56] = <<Spreadsheet>>.ZRowKey
  expr: Constraints[57] = <<Spreadsheet>>.ARowKey
  expr: Constraints[58] = <<Spreadsheet>>.QRowKey
  expr: Constraints[59] = <<Spreadsheet>>.TopRowKey
  sketch-geometry (49):
    g0: LineSegment StartX=47.4802 StartY=33.7107 StartZ=0 EndX=39.6982 EndY=28.2617 EndZ=0
    g1: LineSegment StartX=39.6982 StartY=28.2617 StartZ=0 EndX=31.9163 EndY=22.8128 EndZ=0
    g2: LineSegment StartX=31.9163 StartY=22.8128 StartZ=0 EndX=29.7273 EndY=21.6733 EndZ=0
    g3: LineSegment StartX=29.7273 StartY=21.6733 StartZ=0 EndX=20.8002 EndY=18.4241 EndZ=0
    g4: LineSegment StartX=20.8002 StartY=18.4241 StartZ=0 EndX=11.8732 EndY=15.1749 EndZ=0
    g5: LineSegment StartX=11.8732 StartY=15.1749 StartZ=0 EndX=9.46385 EndY=14.6407 EndZ=0
    g6: LineSegment StartX=9.46385 StartY=14.6407 StartZ=0 EndX=0 EndY=13.8128 EndZ=0
    g7: LineSegment StartX=0 StartY=13.8128 StartZ=0 EndX=-9.46385 EndY=12.9848 EndZ=0
    g8: LineSegment StartX=-9.46385 StartY=12.9848 StartZ=0 EndX=-11.9293 EndY=13.0924 EndZ=0
    g9: LineSegment StartX=-11.9293 StartY=13.0924 StartZ=0 EndX=-21.285 EndY=14.7421 EndZ=0
    g10: LineSegment StartX=-21.285 StartY=14.7421 StartZ=0 EndX=-30.6407 EndY=16.3917 EndZ=0
    g11: LineSegment StartX=-30.6407 StartY=16.3917 StartZ=0 EndX=-31.3353 EndY=12.4525 EndZ=0
    g12: LineSegment StartX=-31.3353 StartY=12.4525 StartZ=0 EndX=-12.6239 EndY=9.15319 EndZ=0
    g13: LineSegment StartX=-12.6239 StartY=9.15319 StartZ=0 EndX=-9.11523 EndY=9 EndZ=0
    g14: LineSegment StartX=13.2412 StartY=11.4161 StartZ=0 EndX=31.0954 EndY=17.9145 EndZ=0
    g15: LineSegment StartX=31.0954 StartY=17.9145 StartZ=0 EndX=34.2106 EndY=19.5362 EndZ=0
    g16: LineSegment StartX=-9.11523 StartY=9 StartZ=0 EndX=9.81247 EndY=10.656 EndZ=0
    g17: LineSegment StartX=9.81247 StartY=10.656 StartZ=0 EndX=13.2412 EndY=11.4161 EndZ=0
    g18: LineSegment StartX=34.2106 StartY=19.5362 StartZ=0 EndX=49.7745 EndY=30.4341 EndZ=0
    g19: LineSegment StartX=49.7745 StartY=30.4341 StartZ=0 EndX=47.4802 EndY=33.7107 EndZ=0
    g20: LineSegment StartX=31.9163 StartY=22.8128 StartZ=0 EndX=34.2106 EndY=19.5362 EndZ=0
    g21: LineSegment StartX=29.7273 StartY=21.6733 StartZ=0 EndX=31.0954 EndY=17.9145 EndZ=0
    g22: LineSegment StartX=11.8732 StartY=15.1749 StartZ=0 EndX=13.2412 EndY=11.4161 EndZ=0
    g23: LineSegment StartX=9.81247 StartY=10.656 StartZ=0 EndX=9.46385 EndY=14.6407 EndZ=0
    g24: LineSegment StartX=-9.46385 StartY=12.9848 StartZ=0 EndX=-9.11523 EndY=9 EndZ=0
    g25: LineSegment StartX=-12.6239 StartY=9.15319 StartZ=0 EndX=-11.9293 EndY=13.0924 EndZ=0
    g26: LineSegment StartX=-21.285 StartY=14.7421 StartZ=0 EndX=-20.4167 EndY=19.6661 EndZ=0
    g27: LineSegment StartX=-20.4167 StartY=19.6661 StartZ=0 EndX=-17.4623 EndY=19.1452 EndZ=0
    g28: LineSegment StartX=-17.4623 StartY=19.1452 StartZ=0 EndX=-15.7258 EndY=28.9933 EndZ=0
    g29: LineSegment StartX=-4.29592 StartY=28.4942 StartZ=0 EndX=-3.42436 EndY=18.5323 EndZ=0
    g30: LineSegment StartX=-3.42436 StartY=18.5323 StartZ=0 EndX=-0.435779 EndY=18.7937 EndZ=0
    g31: LineSegment StartX=-0.435779 StartY=18.7937 StartZ=0 EndX=0 EndY=13.8128 EndZ=0
    g32: LineSegment StartX=-0.435779 StartY=18.7937 StartZ=0 EndX=2.55281 EndY=19.0552 EndZ=0
    g33: LineSegment StartX=2.55281 StartY=19.0552 StartZ=0 EndX=1.68125 EndY=29.0171 EndZ=0
    g34: LineSegment StartX=12.8509 StartY=31.4934 StartZ=0 EndX=16.2711 EndY=22.0965 EndZ=0
    g35: LineSegment StartX=16.2711 StartY=22.0965 StartZ=0 EndX=19.0901 EndY=23.1225 EndZ=0
    g36: LineSegment StartX=19.0901 StartY=23.1225 StartZ=0 EndX=20.8002 EndY=18.4241 EndZ=0
    g37: LineSegment StartX=19.0901 StartY=23.1225 StartZ=0 EndX=21.9092 EndY=24.1486 EndZ=0
    g38: LineSegment StartX=21.9092 StartY=24.1486 StartZ=0 EndX=18.489 EndY=33.5455 EndZ=0
    g39: LineSegment StartX=28.6371 StartY=38.8283 StartZ=0 EndX=34.3729 EndY=30.6368 EndZ=0
    g40: LineSegment StartX=34.3729 StartY=30.6368 StartZ=0 EndX=36.8304 EndY=32.3575 EndZ=0
    g41: LineSegment StartX=36.8304 StartY=32.3575 StartZ=0 EndX=39.6982 EndY=28.2617 EndZ=0
    g42: ArcOfCircle CenterX=-8.11558 CenterY=72.1532 CenterZ=0 NormalX=0 NormalY=0 NormalZ=1 AngleXU=0 Radius=43.8257 StartAngle=4.53786 EndAngle=4.79966
    g43: ArcOfCircle CenterX=-2.13841 CenterY=72.6761 CenterZ=0 NormalX=0 NormalY=0 NormalZ=1 AngleXU=0 Radius=43.8257 StartAngle=4.79966 EndAngle=5.06145
    g44: ArcOfCircle CenterX=3.49974 CenterY=74.7282 CenterZ=0 NormalX=0 NormalY=0 NormalZ=1 AngleXU=0 Radius=43.8257 StartAngle=5.06145 EndAngle=5.32325
    g45: LineSegment StartX=-50 StartY=3 StartZ=0 EndX=-70 EndY=3 EndZ=0
    g46: LineSegment StartX=-50 StartY=3 StartZ=0 EndX=-50 EndY=9 EndZ=0
    g47: LineSegment StartX=-50 StartY=3 StartZ=0 EndX=-50 EndY=0 EndZ=0
    g48: LineSegment StartX=-50 StartY=9 StartZ=0 EndX=50 EndY=9 EndZ=0
  constraints (142):
    c: Coincident(g0,g1)
    c: Coincident(g1,g2)
    c: Coincident(g2,g3)
    c: Coincident(g3,g4)
    c: Coincident(g4,g5)
    c: Coincident(g5,g6)
    c: Coincident(g6,g7)
    c: Coincident(g7,g8)
    c: Coincident(g8,g9)
    c: Coincident(g9,g10)
    c: Coincident(g10,g11)
    c: Coincident(g11,g12)
    c: Coincident(g12,g13)
    c: Coincident(g14,g15)
    c: Coincident(g13,g16)
    c: Coincident(g16,g17)
    c: Coincident(g17,g14)
    c: Coincident(g15,g18)
    c: Coincident(g18,g19)
    c: Coincident(g19,g0)
    c: Coincident(g20,g1)
    c: Coincident(g20,g15)
    c: Coincident(g21,g2)
    c: Coincident(g21,g14)
    c: Coincident(g22,g4)
    c: Coincident(g22,g14)
    c: Coincident(g23,g16)
    c: Coincident(g23,g5)
    c: Coincident(g24,g7)
    c: Coincident(g24,g13)
    c: Coincident(g25,g12)
    c: Coincident(g25,g8)
    c: Coincident(g9,g26)
    c: Coincident(g26,g27)
    c: Coincident(g27,g28)
    c: Coincident(g29,g30)
    c: Coincident(g30,g31)
    c: Coincident(g31,g6)
    c: Coincident(g30,g32)
    c: Coincident(g32,g33)
    c: Coincident(g34,g35)
    c: Coincident(g35,g36)
    c: Coincident(g36,g3)
    c: Coincident(g35,g37)
    c: Coincident(g37,g38)
    c: Coincident(g39,g40)
    c: Coincident(g40,g41)
    c: Coincident(g0,g41)
    c: Angle(g41,g19) = 0
    c: Angle(g41,g20) = 0
    c: Angle(g21,g36) = 0
    c: Angle(g22,g36) = 0
    c: Angle(g23,g31) = 0
    c: Angle(g24,g31) = 0
    c: Angle(g26,g25) = 0
    c: Angle(g11,g26) = 0
    c: Distance(g26) = 5
    c: Distance(g31) = 5
    c: Distance(g36) = 5
    c: Distance(g41) = 5
    c: Angle(g1,g0) = 3.14159
    c: Angle(g3,g4) = 3.14159
    c: Angle(g6,g7) = 3.14159
    c: Angle(g10,g9) = 3.14159
    c: Perpendicular(g31,g30)
    c: Perpendicular(g30,g29)
    c: Perpendicular(g31,g32)
    c: Perpendicular(g33,g32)
    c: Distance(g16) = 19
    c: Distance(g30,g26) = 20
    c: Distance(g30,g35) = 20
    c: Distance(g35,g40) = 20
    c: Equal(g16,g12)
    c: Equal(g12,g14)
    c: Equal(g14,g18)
    c: Equal(g7,g6)
    c: Equal(g9,g10)
    c: Equal(g3,g4)
    c: Equal(g0,g1)
    c: Distance(g24) = 4
    c: Perpendicular(g31,g7)
    c: Perpendicular(g9,g26)
    c: Perpendicular(g1,g41)
    c: Equal(g20,g21)
    c: Equal(g22,g23)
    c: Equal(g25,g24)
    c: Perpendicular(g24,g16)
    c: Perpendicular(g14,g22)
    c: Perpendicular(g22,g4)
    c: Perpendicular(g20,g18)
    c: Angle(g35,g37) = 3.14159
    c: Perpendicular(g36,g37)
    c: Perpendicular(g37,g38)
    c: Perpendicular(g34,g35)
    c: Perpendicular(g26,g27)
    c: Coincident(g42,g28)
    c: Coincident(g42,g29)
    c: Coincident(g43,g33)
    c: Coincident(g43,g34)
    c: Coincident(g44,g38)
    c: Coincident(g44,g39)
    c: Perpendicular(g44,g38)
    c: Perpendicular(g44,g39)
    c: Perpendicular(g43,g34)
    c: Perpendicular(g43,g33)
    c: Perpendicular(g42,g29)
    c: Perpendicular(g42,g28)
    c: Perpendicular(g27,g28)
    c: Perpendicular(g12,g25)
    c: Equal(g27,g30)
    c: Equal(g30,g32)
    c: Equal(g32,g35)
    c: Equal(g35,g37)
    c: Equal(g37,g40)
    c: Perpendicular(g41,g40)
    c: Distance(g32) = 3
    c: Perpendicular(g39,g40)
    c: Distance(g28) = 10
    c: Distance(g29) = 10
    c: Distance(g33) = 10
    c: Distance(g34) = 10
    c: Distance(g38) = 10
    c: Distance(g39) = 10
    c: Angle(g26,g31) = 0.261799
    c: Angle(g31,g36) = 0.261799
    c: Angle(g36,g41) = 0.261799
    c: Angle(g45,g31) = 1.65806
    c: Coincident(g46,g45)
    c: Vertical(g46)
    c: Coincident(g47,g45)
    c: PointOnObject(g47,g-1)
    c: Vertical(g47)
    c: Coincident(g48,g46)
    c: Horizontal(g48)
    c: Horizontal(g45)
    c: DistanceY(g47,g47) = 3
    c: DistanceY(g46,g46) = 6
    c: DistanceX(g45,g45) = 20
    c: DistanceX(g47,g-1) = 50
    c: DistanceX(g48,g48) = 100
    c: PointOnObject(g6,g-2)
    c: PointOnObject(g13,g48)
FEATURE [PartDesign::Pad] Pad016  label="IArch"
  Direction = (1,-2e-16,3e-16)
  Length = 19
  Length2 = 10
  Midplane = true
  Placement = pos=(0,0,0) rot=(0.57735,0.57735,0.57735;2.0944rad)
  Profile = -> Sketch026
  ReferenceAxis = -> Sketch026 [N_Axis]
  Type = 0
FEATURE [Sketcher::SketchObject] Sketch027
  ExternalGeometry = -> [Sketch026]
  FullyConstrained = true
  MapMode = 5
  Placement = pos=(0,0,0) rot=(0.57735,0.57735,0.57735;2.0944rad)
  Support = -> [YZ_Plane004]
  sketch-geometry (60):
    g0: LineSegment StartX=-21.285 StartY=14.7421 StartZ=0 EndX=-21.9796 EndY=10.8028 EndZ=0
    g1: LineSegment StartX=0 StartY=13.8128 StartZ=0 EndX=0.348623 EndY=9.82798 EndZ=0
    g2: LineSegment StartX=20.8002 StartY=18.4241 StartZ=0 EndX=22.1683 EndY=14.6653 EndZ=0
    g3: LineSegment StartX=39.6982 StartY=28.2617 StartZ=0 EndX=41.9925 EndY=24.9851 EndZ=0
    g4: LineSegment StartX=-28.1786 StartY=15.9576 StartZ=0 EndX=-21.285 EndY=14.7421 EndZ=0
    g5: LineSegment StartX=-21.285 StartY=14.7421 StartZ=0 EndX=-14.3913 EndY=13.5265 EndZ=0
    g6: LineSegment StartX=-14.3913 StartY=13.5265 StartZ=0 EndX=-14.6344 EndY=12.1478 EndZ=0
    g7: LineSegment StartX=-14.6344 StartY=12.1478 StartZ=0 EndX=-13.3542 EndY=11.9221 EndZ=0
    g8: LineSegment StartX=-13.3542 StartY=11.9221 StartZ=0 EndX=-13.8057 EndY=9.36157 EndZ=0
    g9: LineSegment StartX=-13.8057 StartY=9.36157 StartZ=0 EndX=-21.9796 EndY=10.8028 EndZ=0
    g10: LineSegment StartX=-21.9796 StartY=10.8028 StartZ=0 EndX=-30.1535 EndY=12.2441 EndZ=0
    g11: LineSegment StartX=-30.1535 StartY=12.2441 StartZ=0 EndX=-29.702 EndY=14.8046 EndZ=0
    g12: LineSegment StartX=-29.702 StartY=14.8046 StartZ=0 EndX=-28.4217 EndY=14.5789 EndZ=0
    g13: LineSegment StartX=-28.4217 StartY=14.5789 StartZ=0 EndX=-28.1786 EndY=15.9576 EndZ=0
    g14: LineSegment StartX=-29.702 StartY=14.8046 StartZ=0 EndX=-29.4589 EndY=16.1834 EndZ=0
    g15: LineSegment StartX=-13.3542 StartY=11.9221 StartZ=0 EndX=-13.1111 EndY=13.3008 EndZ=0
    g16: LineSegment StartX=-14.6344 StartY=12.1478 StartZ=0 EndX=-15.0859 EndY=9.58731 EndZ=0
    g17: LineSegment StartX=-28.4217 StartY=14.5789 StartZ=0 EndX=-28.8732 EndY=12.0184 EndZ=0
    g18: LineSegment StartX=-6.97336 StartY=13.2027 StartZ=0 EndX=0 EndY=13.8128 EndZ=0
    g19: LineSegment StartX=0 StartY=13.8128 StartZ=0 EndX=6.97336 EndY=14.4228 EndZ=0
    g20: LineSegment StartX=6.97336 StartY=14.4228 StartZ=0 EndX=7.09538 EndY=13.0282 EndZ=0
    g21: LineSegment StartX=7.09538 StartY=13.0282 StartZ=0 EndX=8.39043 EndY=13.1415 EndZ=0
    g22: LineSegment StartX=8.39043 StartY=13.1415 StartZ=0 EndX=8.61704 EndY=10.5514 EndZ=0
    g23: LineSegment StartX=8.61704 StartY=10.5514 StartZ=0 EndX=0.348623 EndY=9.82798 EndZ=0
    g24: LineSegment StartX=0.348623 StartY=9.82798 StartZ=0 EndX=-7.91979 EndY=9.10459 EndZ=0
    g25: LineSegment StartX=-7.91979 StartY=9.10459 StartZ=0 EndX=-8.1464 EndY=11.6947 EndZ=0
    g26: LineSegment StartX=-8.1464 StartY=11.6947 StartZ=0 EndX=-6.85134 EndY=11.808 EndZ=0
    g27: LineSegment StartX=-6.85134 StartY=11.808 StartZ=0 EndX=-6.97336 EndY=13.2027 EndZ=0
    g28: LineSegment StartX=14.2224 StartY=16.0299 StartZ=0 EndX=20.8002 EndY=18.4241 EndZ=0
    g29: LineSegment StartX=20.8002 StartY=18.4241 StartZ=0 EndX=27.3781 EndY=20.8182 EndZ=0
    g30: LineSegment StartX=27.3781 StartY=20.8182 StartZ=0 EndX=27.8569 EndY=19.5026 EndZ=0
    g31: LineSegment StartX=27.8569 StartY=19.5026 StartZ=0 EndX=29.0785 EndY=19.9473 EndZ=0
    g32: LineSegment StartX=29.0785 StartY=19.9473 StartZ=0 EndX=29.9678 EndY=17.5041 EndZ=0
    g33: LineSegment StartX=29.9678 StartY=17.5041 StartZ=0 EndX=22.1683 EndY=14.6653 EndZ=0
    g34: LineSegment StartX=22.1683 StartY=14.6653 StartZ=0 EndX=14.3689 EndY=11.8265 EndZ=0
    g35: LineSegment StartX=14.3689 StartY=11.8265 StartZ=0 EndX=13.4796 EndY=14.2697 EndZ=0
    g36: LineSegment StartX=13.4796 StartY=14.2697 StartZ=0 EndX=14.7012 EndY=14.7144 EndZ=0
    g37: LineSegment StartX=14.7012 StartY=14.7144 StartZ=0 EndX=14.2224 EndY=16.0299 EndZ=0
    g38: LineSegment StartX=33.9642 StartY=24.2467 StartZ=0 EndX=39.6982 EndY=28.2617 EndZ=0
    g39: LineSegment StartX=39.6982 StartY=28.2617 StartZ=0 EndX=45.4323 EndY=32.2768 EndZ=0
    g40: LineSegment StartX=45.4323 StartY=32.2768 StartZ=0 EndX=46.2353 EndY=31.13 EndZ=0
    g41: LineSegment StartX=46.2353 StartY=31.13 StartZ=0 EndX=47.3002 EndY=31.8756 EndZ=0
    g42: LineSegment StartX=47.3002 StartY=31.8756 StartZ=0 EndX=48.7915 EndY=29.7458 EndZ=0
    g43: LineSegment StartX=48.7915 StartY=29.7458 StartZ=0 EndX=41.9925 EndY=24.9851 EndZ=0
    g44: LineSegment StartX=41.9925 StartY=24.9851 StartZ=0 EndX=35.1936 EndY=20.2244 EndZ=0
    g45: LineSegment StartX=35.1936 StartY=20.2244 StartZ=0 EndX=33.7023 EndY=22.3542 EndZ=0
    g46: LineSegment StartX=33.7023 StartY=22.3542 StartZ=0 EndX=34.7672 EndY=23.0999 EndZ=0
    g47: LineSegment StartX=34.7672 StartY=23.0999 StartZ=0 EndX=33.9642 EndY=24.2467 EndZ=0
    g48: LineSegment StartX=-8.1464 StartY=11.6947 StartZ=0 EndX=-8.26842 EndY=13.0894 EndZ=0
    g49: LineSegment StartX=-6.85134 StartY=11.808 StartZ=0 EndX=-6.62474 EndY=9.21789 EndZ=0
    g50: LineSegment StartX=7.09538 StartY=13.0282 StartZ=0 EndX=7.32199 EndY=10.4381 EndZ=0
    g51: LineSegment StartX=8.39043 StartY=13.1415 StartZ=0 EndX=8.26842 EndY=14.5362 EndZ=0
    g52: LineSegment StartX=14.7012 StartY=14.7144 StartZ=0 EndX=15.5905 EndY=12.2711 EndZ=0
    g53: LineSegment StartX=13.4796 StartY=14.2697 StartZ=0 EndX=13.0008 EndY=15.5853 EndZ=0
    g54: LineSegment StartX=27.8569 StartY=19.5026 StartZ=0 EndX=28.7462 EndY=17.0594 EndZ=0
    g55: LineSegment StartX=29.0785 StartY=19.9473 StartZ=0 EndX=28.5997 EndY=21.2628 EndZ=0
    g56: LineSegment StartX=34.7672 StartY=23.0999 StartZ=0 EndX=36.2585 EndY=20.9701 EndZ=0
    g57: LineSegment StartX=33.7023 StartY=22.3542 StartZ=0 EndX=32.8993 EndY=23.5011 EndZ=0
    g58: LineSegment StartX=46.2353 StartY=31.13 StartZ=0 EndX=47.7266 EndY=29.0002 EndZ=0
    g59: LineSegment StartX=47.3002 StartY=31.8756 StartZ=0 EndX=46.4972 EndY=33.0224 EndZ=0
  constraints (172):
    c: Coincident(g0,g-4)
    c: PointOnObject(g0,g-5)
    c: Coincident(g1,g-8)
    c: PointOnObject(g1,g-6)
    c: Coincident(g2,g-10)
    c: PointOnObject(g2,g-11)
    c: Coincident(g3,g-14)
    c: PointOnObject(g3,g-12)
    c: Perpendicular(g-12,g3)
    c: Perpendicular(g-11,g2)
    c: Perpendicular(g-6,g1)
    c: Perpendicular(g-5,g0)
    c: PointOnObject(g4,g-3)
    c: Coincident(g4,g0)
    c: Coincident(g4,g5)
    c: PointOnObject(g5,g-4)
    c: Coincident(g5,g6)
    c: Coincident(g6,g7)
    c: Coincident(g7,g8)
    c: PointOnObject(g8,g-5)
    c: Coincident(g8,g9)
    c: Coincident(g9,g0)
    c: Coincident(g9,g10)
    c: PointOnObject(g10,g-5)
    c: Coincident(g10,g11)
    c: Coincident(g11,g12)
    c: Coincident(g12,g13)
    c: Coincident(g13,g4)
    c: Coincident(g14,g11)
    c: PointOnObject(g14,g-3)
    c: Coincident(g15,g7)
    c: PointOnObject(g15,g-4)
    c: Coincident(g16,g6)
    c: PointOnObject(g16,g9)
    c: Coincident(g17,g12)
    c: PointOnObject(g17,g10)
    c: Angle(g15,g8) = 3.14159
    c: Angle(g16,g6) = 3.14159
    c: Angle(g17,g13) = 3.14159
    c: Angle(g11,g14) = 3.14159
    c: Distance(g8,g10) = 16.6
    c: Distance(g4,g5) = 14
    c: Equal(g5,g4)
    c: Equal(g9,g10)
    c: Perpendicular(g4,g13)
    c: Distance(g13) = 1.4
    c: Equal(g14,g13)
    c: Equal(g13,g6)
    c: Equal(g6,g15)
    c: Perpendicular(g10,g11)
    c: Perpendicular(g5,g6)
    c: Perpendicular(g9,g8)
    c: PointOnObject(g18,g-7)
    c: Coincident(g18,g1)
    c: Coincident(g18,g19)
    c: PointOnObject(g19,g-8)
    c: Coincident(g19,g20)
    c: Coincident(g20,g21)
    c: Coincident(g21,g22)
    c: PointOnObject(g22,g-6)
    c: Coincident(g22,g23)
    c: Coincident(g23,g1)
    c: Coincident(g23,g24)
    c: PointOnObject(g24,g-6)
    c: Coincident(g24,g25)
    c: Coincident(g25,g26)
    c: Coincident(g26,g27)
    c: Coincident(g27,g18)
    c: PointOnObject(g28,g-9)
    c: Coincident(g28,g2)
    c: Coincident(g28,g29)
    c: PointOnObject(g29,g-10)
    c: Coincident(g29,g30)
    c: Coincident(g30,g31)
    c: Coincident(g31,g32)
    c: PointOnObject(g32,g-11)
    c: Coincident(g32,g33)
    c: Coincident(g33,g2)
    c: Coincident(g33,g34)
    c: PointOnObject(g34,g-11)
    c: Coincident(g34,g35)
    c: Coincident(g35,g36)
    c: Coincident(g36,g37)
    c: Coincident(g37,g28)
    c: Coincident(g38,g3)
    c: Coincident(g38,g39)
    c: PointOnObject(g39,g-13)
    c: Coincident(g39,g40)
    c: Coincident(g40,g41)
    c: Coincident(g41,g42)
    c: PointOnObject(g42,g-12)
    c: Coincident(g42,g43)
    c: Coincident(g43,g3)
    c: Coincident(g43,g44)
    c: PointOnObject(g44,g-12)
    c: Coincident(g44,g45)
    c: Coincident(g45,g46)
    c: Coincident(g46,g47)
    c: Coincident(g47,g38)
    c: PointOnObject(g38,g-14)
    c: Equal(g19,g18)
    c: Equal(g28,g29)
    c: Equal(g38,g39)
    c: Equal(g24,g23)
    c: Equal(g34,g33)
    c: Equal(g44,g43)
    c: Distance(g24,g22) = 16.6
    c: Distance(g34,g32) = 16.6
    c: Distance(g44,g42) = 16.6
    c: Distance(g39,g38) = 14
    c: Distance(g29,g28) = 14
    c: Distance(g19,g18) = 14
    c: Coincident(g48,g25)
    c: PointOnObject(g48,g-7)
    c: Coincident(g49,g26)
    c: PointOnObject(g49,g24)
    c: Coincident(g50,g20)
    c: Coincident(g51,g21)
    c: PointOnObject(g51,g-8)
    c: Coincident(g52,g36)
    c: PointOnObject(g52,g34)
    c: Coincident(g53,g35)
    c: PointOnObject(g53,g-9)
    c: PointOnObject(g54,g33)
    c: Coincident(g55,g31)
    c: PointOnObject(g55,g-10)
    c: Coincident(g56,g46)
    c: PointOnObject(g56,g44)
    c: Coincident(g57,g45)
    c: PointOnObject(g57,g-14)
    c: Coincident(g58,g40)
    c: PointOnObject(g58,g43)
    c: Coincident(g59,g41)
    c: PointOnObject(g59,g-13)
    c: Coincident(g54,g30)
    c: Angle(g32,g55) = 3.14159
    c: Angle(g25,g48) = 3.14159
    c: Angle(g27,g49) = 3.14159
    c: Angle(g50,g20) = 3.14159
    c: Angle(g22,g51) = 3.14159
    c: Angle(g35,g53) = 3.14159
    c: Angle(g52,g37) = 3.14159
    c: Angle(g54,g30) = 3.14159
    c: Angle(g45,g57) = 3.14159
    c: Angle(g47,g56) = 3.14159
    c: Angle(g58,g40) = 3.14159
    c: Angle(g42,g59) = 3.14159
    c: Perpendicular(g24,g25)
    c: Perpendicular(g18,g27)
    c: Perpendicular(g19,g20)
    c: Perpendicular(g23,g22)
    c: Perpendicular(g28,g37)
    c: Perpendicular(g34,g35)
    c: Perpendicular(g29,g30)
    c: Perpendicular(g33,g32)
    c: Perpendicular(g44,g45)
    c: Perpendicular(g39,g40)
    c: Perpendicular(g43,g42)
    c: Equal(g59,g40)
    c: Equal(g40,g47)
    c: Equal(g47,g57)
    c: Equal(g55,g30)
    c: Equal(g30,g37)
    c: Equal(g37,g53)
    c: Equal(g51,g20)
    c: Equal(g20,g27)
    c: Equal(g27,g48)
    c: Distance(g48) = 1.4
    c: PointOnObject(g50,g23)
    c: Distance(g53) = 1.4
    c: Distance(g57) = 1.4
    c: Perpendicular(g38,g47)
FEATURE [PartDesign::Pocket] Pocket008  label="IMX Sockets"
  BaseFeature = -> Pad016
  Direction = (-1,2e-16,-3e-16)
  Length = 14
  Length2 = 5
  Midplane = true
  Placement = pos=(0,0,0) rot=(0.57735,0.57735,0.57735;2.0944rad)
  Profile = -> Sketch027
  ReferenceAxis = -> Sketch027 [N_Axis]
  Type = 0
FEATURE [Sketcher::SketchObject] Sketch028
  ExternalGeometry = -> [Sketch027]
  FullyConstrained = true
  MapMode = 5
  Placement = pos=(0,0,0) rot=(0.57735,0.57735,0.57735;2.0944rad)
  Support = -> [YZ_Plane004]
  sketch-geometry (44):
    g0: LineSegment StartX=-21.285 StartY=14.7421 StartZ=0 EndX=-21.4934 EndY=13.5603 EndZ=0
    g1: LineSegment StartX=-21.4934 StartY=13.5603 StartZ=0 EndX=-21.667 EndY=12.5755 EndZ=0
    g2: LineSegment StartX=-21.667 StartY=12.5755 StartZ=0 EndX=-21.9796 EndY=10.8028 EndZ=0
    g3: LineSegment StartX=0 StartY=13.8128 StartZ=0 EndX=0.104587 EndY=12.6173 EndZ=0
    g4: LineSegment StartX=0.104587 StartY=12.6173 StartZ=0 EndX=0.191743 EndY=11.6211 EndZ=0
    g5: LineSegment StartX=0.191743 StartY=11.6211 StartZ=0 EndX=0.348623 EndY=9.82798 EndZ=0
    g6: LineSegment StartX=39.6982 StartY=28.2617 StartZ=0 EndX=40.3865 EndY=27.2788 EndZ=0
    g7: LineSegment StartX=40.3865 StartY=27.2788 StartZ=0 EndX=40.9601 EndY=26.4596 EndZ=0
    g8: LineSegment StartX=40.9601 StartY=26.4596 StartZ=0 EndX=41.9925 EndY=24.9851 EndZ=0
    g9: LineSegment StartX=22.1683 StartY=14.6653 StartZ=0 EndX=21.5527 EndY=16.3567 EndZ=0
    g10: LineSegment StartX=21.5527 StartY=16.3567 StartZ=0 EndX=21.2107 EndY=17.2964 EndZ=0
    g11: LineSegment StartX=21.2107 StartY=17.2964 StartZ=0 EndX=20.8002 EndY=18.4241 EndZ=0
    g12: LineSegment StartX=-28.387 StartY=14.7758 StartZ=0 EndX=-14.5997 EndY=12.3448 EndZ=0
    g13: LineSegment StartX=-14.5997 StartY=12.3448 StartZ=0 EndX=-14.6344 EndY=12.1478 EndZ=0
    g14: LineSegment StartX=-14.6344 StartY=12.1478 StartZ=0 EndX=-13.3542 EndY=11.9221 EndZ=0
    g15: LineSegment StartX=-13.3542 StartY=11.9221 StartZ=0 EndX=-13.4931 EndY=11.1342 EndZ=0
    g16: LineSegment StartX=-13.4931 StartY=11.1342 StartZ=0 EndX=-29.8409 EndY=14.0168 EndZ=0
    g17: LineSegment StartX=-29.8409 StartY=14.0168 StartZ=0 EndX=-29.702 EndY=14.8046 EndZ=0
    g18: LineSegment StartX=-29.702 StartY=14.8046 StartZ=0 EndX=-28.4217 EndY=14.5789 EndZ=0
    g19: LineSegment StartX=-28.4217 StartY=14.5789 StartZ=0 EndX=-28.387 EndY=14.7758 EndZ=0
    g20: LineSegment StartX=-6.86878 StartY=12.0072 StartZ=0 EndX=7.07795 EndY=13.2274 EndZ=0
    g21: LineSegment StartX=7.07795 StartY=13.2274 StartZ=0 EndX=7.09538 EndY=13.0282 EndZ=0
    g22: LineSegment StartX=7.09538 StartY=13.0282 StartZ=0 EndX=8.39043 EndY=13.1415 EndZ=0
    g23: LineSegment StartX=8.39043 StartY=13.1415 StartZ=0 EndX=8.46016 EndY=12.3445 EndZ=0
    g24: LineSegment StartX=8.46016 StartY=12.3445 StartZ=0 EndX=-8.07667 EndY=10.8977 EndZ=0
    g25: LineSegment StartX=-8.07667 StartY=10.8977 StartZ=0 EndX=-8.1464 EndY=11.6947 EndZ=0
    g26: LineSegment StartX=-8.1464 StartY=11.6947 StartZ=0 EndX=-6.85134 EndY=11.808 EndZ=0
    g27: LineSegment StartX=-6.85134 StartY=11.808 StartZ=0 EndX=-6.86878 EndY=12.0072 EndZ=0
    g28: LineSegment StartX=14.6328 StartY=14.9023 StartZ=0 EndX=27.7885 EndY=19.6906 EndZ=0
    g29: LineSegment StartX=27.7885 StartY=19.6906 StartZ=0 EndX=27.8569 EndY=19.5026 EndZ=0
    g30: LineSegment StartX=27.8569 StartY=19.5026 StartZ=0 EndX=29.0785 EndY=19.9473 EndZ=0
    g31: LineSegment StartX=29.0785 StartY=19.9473 StartZ=0 EndX=29.3521 EndY=19.1955 EndZ=0
    g32: LineSegment StartX=29.3521 StartY=19.1955 StartZ=0 EndX=13.7532 EndY=13.518 EndZ=0
    g33: LineSegment StartX=13.7532 StartY=13.518 StartZ=0 EndX=13.4796 EndY=14.2697 EndZ=0
    g34: LineSegment StartX=13.4796 StartY=14.2697 StartZ=0 EndX=14.7012 EndY=14.7144 EndZ=0
    g35: LineSegment StartX=14.7012 StartY=14.7144 StartZ=0 EndX=14.6328 EndY=14.9023 EndZ=0
    g36: LineSegment StartX=34.6525 StartY=23.2637 StartZ=0 EndX=46.1206 EndY=31.2938 EndZ=0
    g37: LineSegment StartX=46.1206 StartY=31.2938 StartZ=0 EndX=46.2353 EndY=31.13 EndZ=0
    g38: LineSegment StartX=46.2353 StartY=31.13 StartZ=0 EndX=47.3002 EndY=31.8756 EndZ=0
    g39: LineSegment StartX=47.3002 StartY=31.8756 StartZ=0 EndX=47.7591 EndY=31.2203 EndZ=0
    g40: LineSegment StartX=47.7591 StartY=31.2203 StartZ=0 EndX=34.1611 EndY=21.6989 EndZ=0
    g41: LineSegment StartX=34.1611 StartY=21.6989 StartZ=0 EndX=33.7023 EndY=22.3542 EndZ=0
    g42: LineSegment StartX=33.7023 StartY=22.3542 StartZ=0 EndX=34.7672 EndY=23.0999 EndZ=0
    g43: LineSegment StartX=34.7672 StartY=23.0999 StartZ=0 EndX=34.6525 EndY=23.2637 EndZ=0
  constraints (112):
    c: Coincident(g-21,g0)
    c: Coincident(g0,g1)
    c: Coincident(g1,g2)
    c: Coincident(g2,g-24)
    c: Coincident(g-16,g3)
    c: Coincident(g3,g4)
    c: Coincident(g4,g5)
    c: Coincident(g5,g-15)
    c: Coincident(g-6,g6)
    c: Coincident(g6,g7)
    c: Coincident(g7,g8)
    c: Coincident(g8,g-3)
    c: Coincident(g-10,g9)
    c: Coincident(g9,g10)
    c: Coincident(g10,g11)
    c: Coincident(g11,g-9)
    c: Angle(g6,g7) = 3.14159
    c: Angle(g8,g7) = 3.14159
    c: Angle(g11,g10) = 3.14159
    c: Angle(g9,g10) = 3.14159
    c: Angle(g3,g4) = 3.14159
    c: Angle(g5,g4) = 3.14159
    c: Angle(g0,g1) = 3.14159
    c: Angle(g2,g1) = 3.14159
    c: PointOnObject(g12,g-26)
    c: PointOnObject(g12,g-22)
    c: Coincident(g12,g13)
    c: Coincident(g13,g-22)
    c: Coincident(g13,g14)
    c: Coincident(g14,g-23)
    c: Coincident(g14,g15)
    c: PointOnObject(g15,g-23)
    c: Coincident(g15,g16)
    c: PointOnObject(g16,g-25)
    c: Coincident(g16,g17)
    c: Coincident(g17,g-25)
    c: Coincident(g17,g18)
    c: Coincident(g18,g-26)
    c: Coincident(g18,g19)
    c: Coincident(g19,g12)
    c: PointOnObject(g20,g-17)
    c: PointOnObject(g20,g-19)
    c: Coincident(g20,g21)
    c: Coincident(g21,g-19)
    c: Coincident(g21,g22)
    c: Coincident(g22,g-20)
    c: Coincident(g22,g23)
    c: PointOnObject(g23,g-20)
    c: Coincident(g23,g24)
    c: PointOnObject(g24,g-18)
    c: Coincident(g24,g25)
    c: Coincident(g25,g-18)
    c: Coincident(g25,g26)
    c: Coincident(g26,g-17)
    c: Coincident(g26,g27)
    c: Coincident(g27,g20)
    c: PointOnObject(g28,g-14)
    c: PointOnObject(g28,g-12)
    c: Coincident(g28,g29)
    c: Coincident(g29,g-12)
    c: Coincident(g29,g30)
    c: Coincident(g30,g-11)
    c: Coincident(g30,g31)
    c: PointOnObject(g31,g-11)
    c: Coincident(g31,g32)
    c: Coincident(g32,g33)
    c: Coincident(g33,g-13)
    c: Coincident(g33,g34)
    c: Coincident(g34,g-14)
    c: Coincident(g34,g35)
    c: Coincident(g35,g28)
    c: PointOnObject(g36,g-7)
    c: PointOnObject(g36,g-4)
    c: Coincident(g36,g37)
    c: Coincident(g37,g-4)
    c: Coincident(g37,g38)
    c: Coincident(g38,g-5)
    c: Coincident(g38,g39)
    c: PointOnObject(g39,g-5)
    c: Coincident(g39,g40)
    c: PointOnObject(g40,g-8)
    c: Coincident(g40,g41)
    c: Coincident(g41,g-8)
    c: Coincident(g41,g42)
    c: Coincident(g42,g-7)
    c: Coincident(g42,g43)
    c: Coincident(g43,g36)
    c: PointOnObject(g32,g-13)
    c: PointOnObject(g1,g16)
    c: PointOnObject(g0,g12)
    c: PointOnObject(g3,g20)
    c: PointOnObject(g4,g24)
    c: PointOnObject(g10,g28)
    c: PointOnObject(g9,g32)
    c: PointOnObject(g6,g36)
    c: PointOnObject(g7,g40)
    c: Perpendicular(g36,g6)
    c: Perpendicular(g8,g40)
    c: Perpendicular(g9,g32)
    c: Perpendicular(g11,g28)
    c: Perpendicular(g3,g20)
    c: Perpendicular(g5,g24)
    c: Perpendicular(g2,g16)
    c: Perpendicular(g0,g12)
    c: Equal(g7,g10)
    c: Equal(g10,g4)
    c: Equal(g4,g1)
    c: Equal(g0,g3)
    c: Equal(g3,g11)
    c: Equal(g11,g6)
    c: Distance(g4) = 1
    c: Distance(g3) = 1.2
FEATURE [PartDesign::Pocket] Pocket009  label="IChoc Sockets"
  BaseFeature = -> Pocket008
  Direction = (-1,2e-16,-3e-16)
  Length = 14.6
  Length2 = 5
  Midplane = true
  Placement = pos=(0,0,0) rot=(0.57735,0.57735,0.57735;2.0944rad)
  Profile = -> Sketch028
  ReferenceAxis = -> Sketch028 [N_Axis]
  Type = 0
FEATURE [Sketcher::SketchObject] Sketch029
  ExternalGeometry = -> [Sketch026]
  FullyConstrained = true
  MapMode = 5
  Placement = pos=(0,0,0) rot=(0.57735,0.57735,0.57735;2.0944rad)
  Support = -> [YZ_Plane004]
  expr: Constraints[18] = <<Spreadsheet>>.Wiring
  sketch-geometry (8):
    g0: LineSegment StartX=9.46385 StartY=14.6407 StartZ=0 EndX=9.81247 EndY=10.656 EndZ=0
    g1: LineSegment StartX=9.81247 StartY=10.656 StartZ=0 EndX=10.3354 EndY=4.67879 EndZ=0
    g2: LineSegment StartX=10.3354 StartY=4.67879 StartZ=0 EndX=10.3354 EndY=0 EndZ=0
    g3: LineSegment StartX=10.3354 StartY=0 StartZ=0 EndX=15.2934 EndY=0 EndZ=0
    g4: LineSegment StartX=15.2934 StartY=0 StartZ=0 EndX=15.2934 EndY=5.77794 EndZ=0
    g5: LineSegment StartX=15.2934 StartY=5.77794 StartZ=0 EndX=13.2412 EndY=11.4161 EndZ=0
    g6: LineSegment StartX=13.2412 StartY=11.4161 StartZ=0 EndX=11.8732 EndY=15.1749 EndZ=0
    g7: LineSegment StartX=9.46385 StartY=14.6407 StartZ=0 EndX=11.8732 EndY=15.1749 EndZ=0
  constraints (20):
    c: Coincident(g-3,g0)
    c: Coincident(g0,g-4)
    c: Coincident(g0,g1)
    c: Coincident(g1,g2)
    c: PointOnObject(g2,g-1)
    c: Vertical(g2)
    c: Coincident(g2,g3)
    c: PointOnObject(g3,g-1)
    c: Coincident(g3,g4)
    c: Vertical(g4)
    c: Coincident(g4,g5)
    c: Coincident(g5,g-4)
    c: Coincident(g5,g6)
    c: Coincident(g6,g-3)
    c: Coincident(g7,g-3)
    c: Coincident(g7,g-3)
    c: Angle(g0,g1) = 3.14159
    c: Angle(g5,g6) = 3.14159
    c: Distance(g1) = 6
    c: Equal(g5,g1)
FEATURE [PartDesign::Pad] Pad017  label="IInner Legs"
  BaseFeature = -> Pocket009
  Direction = (1,-2e-16,3e-16)
  Length = 4.1
  Length2 = 9.5
  Placement = pos=(0,0,0) rot=(0.57735,0.57735,0.57735;2.0944rad)
  Profile = -> Sketch029
  ReferenceAxis = -> Sketch029 [N_Axis]
  Type = 4
  expr: Length = <<Spreadsheet>>.ScrewD / 2 + 2mm
  expr: Length2 = 9.5
FEATURE [Sketcher::SketchObject] Sketch030
  ExternalGeometry = -> [Sketch026]
  FullyConstrained = true
  MapMode = 5
  Placement = pos=(0,0,0) rot=(0.57735,0.57735,0.57735;2.0944rad)
  Support = -> [YZ_Plane004]
  expr: Constraints[32] = <<Spreadsheet>>.Wiring
  expr: Constraints[42] = <<Spreadsheet>>.ArchLength - 10mm
  expr: Constraints[43] = <<Spreadsheet>>.ArchLength - 30mm
  expr: Constraints[44] = <<Spreadsheet>>.ArchLength
  expr: Constraints[45] = <<Spreadsheet>>.ArchLength - 20mm
  expr: Constraints[52] = <<Spreadsheet>>.ArchLength - 25mm
  expr: Constraints[53] = <<Spreadsheet>>.ArchLength - 5mm
  sketch-geometry (36):
    g0: LineSegment StartX=-13.6658 StartY=3.24435 StartZ=0 EndX=-12.6239 EndY=9.15319 EndZ=0
    g1: LineSegment StartX=-12.6239 StartY=9.15319 StartZ=0 EndX=-11.9293 EndY=13.0924 EndZ=0
    g2: LineSegment StartX=-11.9293 StartY=13.0924 StartZ=0 EndX=-9.46385 EndY=12.9848 EndZ=0
    g3: LineSegment StartX=-9.46385 StartY=12.9848 StartZ=0 EndX=-9.11523 EndY=9 EndZ=0
    g4: LineSegment StartX=-15 StartY=0 StartZ=0 EndX=-25 EndY=0 EndZ=0
    g5: LineSegment StartX=-25 StartY=0 StartZ=0 EndX=-25 EndY=3 EndZ=0
    g6: LineSegment StartX=-9.11523 StartY=9 StartZ=0 EndX=-8.59229 EndY=3.02283 EndZ=0
    g7: LineSegment StartX=-8.59229 StartY=3.02283 StartZ=0 EndX=-15 EndY=0 EndZ=0
    g8: LineSegment StartX=37.6521 StartY=14.6212 StartZ=0 EndX=34.2106 EndY=19.5362 EndZ=0
    g9: LineSegment StartX=34.2106 StartY=19.5362 StartZ=0 EndX=31.9163 EndY=22.8128 EndZ=0
    g10: LineSegment StartX=31.9163 StartY=22.8128 StartZ=0 EndX=29.7273 EndY=21.6733 EndZ=0
    g11: LineSegment StartX=29.7273 StartY=21.6733 StartZ=0 EndX=31.0954 EndY=17.9145 EndZ=0
    g12: LineSegment StartX=31.0954 StartY=17.9145 StartZ=0 EndX=33.1475 EndY=12.2763 EndZ=0
    g13: LineSegment StartX=33.1475 StartY=12.2763 StartZ=0 EndX=35 EndY=0 EndZ=0
    g14: LineSegment StartX=35 StartY=0 StartZ=0 EndX=45 EndY=0 EndZ=0
    g15: LineSegment StartX=45 StartY=0 StartZ=0 EndX=45 EndY=3 EndZ=0
    g16: LineSegment StartX=-13.6658 StartY=3.24435 StartZ=0 EndX=-13.9496 EndY=1.63459 EndZ=0
    g17: LineSegment StartX=-13.9496 StartY=1.63459 StartZ=0 EndX=-13.9496 EndY=0 EndZ=0
    g18: LineSegment StartX=45 StartY=3 StartZ=0 EndX=40 EndY=3 EndZ=0
    g19: LineSegment StartX=-25 StartY=3 StartZ=0 EndX=-20 EndY=3 EndZ=0
    g20-g23: Circle x4 (B-spline internal-alignment scaffolding for g24; pole/knot coordinates omitted)
    g24: BSplineCurve PolesCount=4 KnotsCount=2 Degree=3 IsPeriodic=0
    g25: GeomPoint X=-13.6658 Y=3.24435 Z=0
    g26: GeomPoint X=-25 Y=3 Z=0
    g27: LineSegment StartX=37.6521 StartY=14.6212 StartZ=0 EndX=42.2621 EndY=8.03739 EndZ=0
    g28: LineSegment StartX=42.2621 StartY=8.03739 StartZ=0 EndX=42.2621 EndY=0 EndZ=0
    g29-g32: Circle x4 (B-spline internal-alignment scaffolding for g33; pole/knot coordinates omitted)
    g33: BSplineCurve PolesCount=4 KnotsCount=2 Degree=3 IsPeriodic=0
    g34: GeomPoint X=37.6521 Y=14.6212 Z=0
    g35: GeomPoint X=45 Y=3 Z=0
  constraints (82):
    c: Coincident(g0,g-4)
    c: Coincident(g0,g1)
    c: Coincident(g1,g-3)
    c: Coincident(g1,g2)
    c: Coincident(g2,g-3)
    c: Coincident(g2,g3)
    c: Coincident(g3,g-4)
    c: PointOnObject(g4,g-1)
    c: PointOnObject(g4,g-1)
    c: Coincident(g4,g5)
    c: Vertical(g5)
    c: Coincident(g-4,g6)
    c: Coincident(g6,g7)
    c: Coincident(g7,g4)
    c: Coincident(g8,g-6)
    c: Coincident(g8,g9)
    c: Coincident(g9,g-5)
    c: Coincident(g9,g10)
    c: Coincident(g10,g-5)
    c: Coincident(g10,g11)
    c: Coincident(g11,g-6)
    c: Coincident(g11,g12)
    c: Coincident(g12,g13)
    c: PointOnObject(g13,g-1)
    c: Coincident(g13,g14)
    c: PointOnObject(g14,g-1)
    c: Coincident(g14,g15)
    c: Vertical(g15)
    c: Angle(g1,g0) = 3.14159
    c: Angle(g3,g6) = 3.14159
    c: Angle(g11,g12) = 3.14159
    c: Angle(g8,g9) = 3.14159
    c: Distance(g8) = 6
    c: Equal(g8,g12)
    c: Equal(g12,g6)
    c: Equal(g6,g0)
    c: Coincident(g0,g16)
    c: Coincident(g16,g17)
    c: PointOnObject(g17,g-1)
    c: Vertical(g17)
    c: Angle(g0,g16) = 3.14159
    c: Equal(g16,g17)
    c: DistanceX(g-7,g13) = 35
    c: DistanceX(g4,g-7) = 15
    c: DistanceX(g-7,g14) = 45
    c: DistanceX(g4,g-7) = 25
    c: DistanceY(g5,g5) = 3
    c: DistanceY(g15,g15) = 3
    c: Coincident(g18,g15)
    c: Horizontal(g18)
    c: Coincident(g19,g5)
    c: Horizontal(g19)
    c: DistanceX(g19,g-7) = 20
    c: DistanceX(g-7,g18) = 40
    c: Weight(g20) = 1
    c: Coincident(g24,g16)
    c: Equal(g20,g21)
    c: Coincident(g21,g16)
    c: Equal(g20,g22)
    c: Coincident(g22,g19)
    c: Equal(g20,g23)
    c: Coincident(g24,g19)
    c: InternalAlignment(g20-g23 -> g24) x4
    c: InternalAlignment(g25,g24)
    c: InternalAlignment(g26,g24)
    c: Coincident(g8,g27)
    c: Coincident(g27,g28)
    c: PointOnObject(g28,g-1)
    c: Vertical(g28)
    c: Equal(g28,g27)
    c: Angle(g27,g8) = 3.14159
    c: Weight(g29) = 1
    c: Coincident(g33,g27)
    c: Equal(g29,g30)
    c: Coincident(g30,g27)
    c: Equal(g29,g31)
    c: Coincident(g31,g18)
    c: Equal(g29,g32)
    c: Coincident(g33,g18)
    c: InternalAlignment(g29-g32 -> g33) x4
    c: InternalAlignment(g34,g33)
    c: InternalAlignment(g35,g33)
FEATURE [PartDesign::Pad] Pad018  label="IOuter Legs"
  BaseFeature = -> Pad017
  Direction = (1,-2e-16,3e-16)
  Length = 9.5
  Length2 = 10
  Placement = pos=(0,0,0) rot=(0.57735,0.57735,0.57735;2.0944rad)
  Profile = -> Sketch030
  ReferenceAxis = -> Sketch030 [N_Axis]
  Reversed = true
  Type = 0
FEATURE [Sketcher::SketchObject] Sketch031
  ExternalGeometry = -> [Sketch030]
  FullyConstrained = true
  MapMode = 5
  Support = -> [XY_Plane004]
  expr: Constraints[20] = <<Spreadsheet>>.NutR
  expr: Constraints[21] = <<Spreadsheet>>.NutR
  expr: Constraints[26] = <<Spreadsheet>>.ScrewD
  expr: Constraints[46] = <<Spreadsheet>>.ScrewD
  expr: Constraints[47] = <<Spreadsheet>>.NutR
  expr: Constraints[48] = <<Spreadsheet>>.NutR
  sketch-geometry (20):
    g0: LineSegment StartX=7.6225 StartY=-26.0949 StartZ=0 EndX=-3.6e-15 EndY=-20 EndZ=0
    g1: LineSegment StartX=-3.6e-15 StartY=-20 StartZ=0 EndX=-3.3e-15 EndY=-25 EndZ=0
    g2: LineSegment StartX=-3.3e-15 StartY=-25 StartZ=0 EndX=-9.5 EndY=-25 EndZ=0
    g3: LineSegment StartX=-9.5 StartY=-25 StartZ=0 EndX=-9.5 EndY=-35 EndZ=0
    g4: LineSegment StartX=-9.5 StartY=-35 StartZ=0 EndX=4.5 EndY=-35 EndZ=0
    g5: ArcOfCircle CenterX=4.5 CenterY=-30 CenterZ=0 NormalX=0 NormalY=0 NormalZ=1 AngleXU=0 Radius=5 StartAngle=4.71239 EndAngle=7.17949
    g6: LineSegment StartX=-9.5 StartY=-35 StartZ=0 EndX=0 EndY=-30 EndZ=0
    g7: LineSegment StartX=0 StartY=-30 StartZ=0 EndX=9.5 EndY=-35 EndZ=0
    g8: LineSegment StartX=9.5 StartY=-35 StartZ=0 EndX=9.5 EndY=-30 EndZ=0
    g9: Circle CenterX=0 CenterY=-30 CenterZ=0 NormalX=0 NormalY=0 NormalZ=1 AngleXU=0 Radius=2.1
    g10: LineSegment StartX=1.22e-14 StartY=45 StartZ=0 EndX=-9.5 EndY=45 EndZ=0
    g11: LineSegment StartX=-9.5 StartY=45 StartZ=0 EndX=-9.5 EndY=55 EndZ=0
    g12: LineSegment StartX=-9.5 StartY=55 StartZ=0 EndX=4.5 EndY=55 EndZ=0
    g13: ArcOfCircle CenterX=4.5 CenterY=50 CenterZ=0 NormalX=0 NormalY=0 NormalZ=1 AngleXU=0 Radius=5 StartAngle=5.38688 EndAngle=7.85398
    g14: LineSegment StartX=7.6225 StartY=46.0949 StartZ=0 EndX=8.9e-15 EndY=40 EndZ=0
    g15: LineSegment StartX=8.9e-15 StartY=40 StartZ=0 EndX=1.22e-14 EndY=45 EndZ=0
    g16: LineSegment StartX=9.5 StartY=50 StartZ=0 EndX=9.5 EndY=55 EndZ=0
    g17: LineSegment StartX=9.5 StartY=55 StartZ=0 EndX=0 EndY=50 EndZ=0
    g18: LineSegment StartX=0 StartY=50 StartZ=0 EndX=-9.5 EndY=55 EndZ=0
    g19: Circle CenterX=0 CenterY=50 CenterZ=0 NormalX=0 NormalY=0 NormalZ=1 AngleXU=0 Radius=2.1
  constraints (53):
    c: PointOnObject(g0,g-4)
    c: Coincident(g0,g1)
    c: Coincident(g1,g-4)
    c: Coincident(g1,g2)
    c: Horizontal(g2)
    c: Coincident(g2,g3)
    c: Vertical(g3)
    c: Coincident(g3,g4)
    c: Horizontal(g4)
    c: Tangent(g4,g5) = -1.5708
    c: Coincident(g3,g6)
    c: PointOnObject(g6,g-2)
    c: Coincident(g6,g7)
    c: Coincident(g8,g7)
    c: PointOnObject(g8,g5)
    c: Vertical(g8)
    c: Tangent(g8,g5)
    c: Horizontal(g7,g4)
    c: Equal(g7,g6)
    c: DistanceX(g6,g7) = 19
    c: DistanceY(g7,g6) = 5
    c: DistanceY(g6,g-4) = 5
    c: DistanceY(g1,g1) = 5
    c: Coincident(g9,g6)
    c: Horizontal(g5,g6)
    c: Tangent(g5,g0) = -1.5708
    c: Diameter(g9) = 4.2
    c: Coincident(g-3,g10)
    c: Horizontal(g10)
    c: Coincident(g10,g11)
    c: Vertical(g11)
    c: Coincident(g11,g12)
    c: Horizontal(g12)
    c: Tangent(g12,g13) = 1.5708
    c: Tangent(g13,g14) = 1.5708
    c: Coincident(g14,g15)
    c: Coincident(g15,g10)
    c: PointOnObject(g14,g-3)
    c: Vertical(g16)
    c: Coincident(g16,g17)
    c: Coincident(g17,g18)
    c: Coincident(g18,g11)
    c: PointOnObject(g17,g-2)
    c: Equal(g18,g17)
    c: Horizontal(g16,g12)
    c: Coincident(g19,g17)
    c: Diameter(g19) = 4.2
    c: DistanceY(g17,g16) = 5
    c: DistanceY(g-3,g17) = 5
    c: DistanceY(g15,g15) = 5
    c: DistanceX(g18,g16) = 19
    c: Tangent(g16,g13) = -1.5708
    c: Horizontal(g13,g17)
FEATURE [PartDesign::Pad] Pad019  label="IFeet"
  BaseFeature = -> Pad018
  Direction = (0,0,1)
  Length = 3
  Length2 = 10
  Placement = pos=(0,0,0) rot=(0.57735,0.57735,0.57735;2.0944rad)
  Profile = -> Sketch031
  ReferenceAxis = -> Sketch031 [N_Axis]
  Type = 0
FEATURE [PartDesign::Body] Body004  label="IndexArch"
  Group = -> [Sketch026,Pad016,Sketch027,Pocket008,Sketch028,Pocket009,Sketch029,Pad017,Sketch030,Pad018,Sketch031,Pad019]
  Origin = -> Origin004
  Placement = pos=(90,0,5) rot=(0,0,1;0rad)
  Tip = -> Pad019
FEATURE [Sketcher::SketchObject] Sketch032
  FullyConstrained = true
  MapMode = 5
  Placement = pos=(0,0,0) rot=(0.57735,0.57735,0.57735;2.0944rad)
  Support = -> [YZ_Plane005]
  expr: Constraints[104] = <<Spreadsheet>>.ZRowKey
  expr: Constraints[105] = <<Spreadsheet>>.ARowKey
  expr: Constraints[106] = <<Spreadsheet>>.QRowKey
  expr: Constraints[107] = <<Spreadsheet>>.TopRowKey
  expr: Constraints[138] = <<Spreadsheet>>.Wiring
  sketch-geometry (49):
    g0: LineSegment StartX=-31.3353 StartY=12.4525 StartZ=0 EndX=-12.6239 EndY=9.15319 EndZ=0
    g1: LineSegment StartX=-12.6239 StartY=9.15319 StartZ=0 EndX=-9.11523 EndY=9 EndZ=0
    g2: LineSegment StartX=-9.11523 StartY=9 StartZ=0 EndX=9.81247 EndY=10.656 EndZ=0
    g3: LineSegment StartX=9.81247 StartY=10.656 StartZ=0 EndX=13.2412 EndY=11.4161 EndZ=0
    g4: LineSegment StartX=13.2412 StartY=11.4161 StartZ=0 EndX=31.0954 EndY=17.9145 EndZ=0
    g5: LineSegment StartX=31.0954 StartY=17.9145 StartZ=0 EndX=34.2106 EndY=19.5362 EndZ=0
    g6: LineSegment StartX=34.2106 StartY=19.5362 StartZ=0 EndX=49.7745 EndY=30.4341 EndZ=0
    g7: LineSegment StartX=49.7745 StartY=30.4341 StartZ=0 EndX=47.4802 EndY=33.7107 EndZ=0
    g8: LineSegment StartX=47.4802 StartY=33.7107 StartZ=0 EndX=39.6982 EndY=28.2617 EndZ=0
    g9: LineSegment StartX=39.6982 StartY=28.2617 StartZ=0 EndX=31.9163 EndY=22.8128 EndZ=0
    g10: LineSegment StartX=31.9163 StartY=22.8128 StartZ=0 EndX=29.7273 EndY=21.6733 EndZ=0
    g11: LineSegment StartX=29.7273 StartY=21.6733 StartZ=0 EndX=20.8002 EndY=18.4241 EndZ=0
    g12: LineSegment StartX=20.8002 StartY=18.4241 StartZ=0 EndX=11.8732 EndY=15.1749 EndZ=0
    g13: LineSegment StartX=11.8732 StartY=15.1749 StartZ=0 EndX=9.46385 EndY=14.6407 EndZ=0
    g14: LineSegment StartX=9.46385 StartY=14.6407 StartZ=0 EndX=0 EndY=13.8128 EndZ=0
    g15: LineSegment StartX=0 StartY=13.8128 StartZ=0 EndX=-9.46385 EndY=12.9848 EndZ=0
    g16: LineSegment StartX=-9.46385 StartY=12.9848 StartZ=0 EndX=-11.9293 EndY=13.0924 EndZ=0
    g17: LineSegment StartX=-11.9293 StartY=13.0924 StartZ=0 EndX=-21.285 EndY=14.7421 EndZ=0
    g18: LineSegment StartX=-21.285 StartY=14.7421 StartZ=0 EndX=-30.6407 EndY=16.3917 EndZ=0
    g19: LineSegment StartX=-30.6407 StartY=16.3917 StartZ=0 EndX=-31.3353 EndY=12.4525 EndZ=0
    g20: LineSegment StartX=-21.285 StartY=14.7421 StartZ=0 EndX=-20.4167 EndY=19.6661 EndZ=0
    g21: LineSegment StartX=-20.4167 StartY=19.6661 StartZ=0 EndX=-17.4623 EndY=19.1452 EndZ=0
    g22: LineSegment StartX=-17.4623 StartY=19.1452 StartZ=0 EndX=-15.7258 EndY=28.9933 EndZ=0
    g23: LineSegment StartX=-4.29592 StartY=28.4942 StartZ=0 EndX=-3.42436 EndY=18.5323 EndZ=0
    g24: LineSegment StartX=-3.42436 StartY=18.5323 StartZ=0 EndX=-0.435779 EndY=18.7937 EndZ=0
    g25: LineSegment StartX=-0.435779 StartY=18.7937 StartZ=0 EndX=0 EndY=13.8128 EndZ=0
    g26: LineSegment StartX=-0.435779 StartY=18.7937 StartZ=0 EndX=2.55281 EndY=19.0552 EndZ=0
    g27: LineSegment StartX=2.55281 StartY=19.0552 StartZ=0 EndX=1.68125 EndY=29.0171 EndZ=0
    g28: LineSegment StartX=12.8509 StartY=31.4934 StartZ=0 EndX=16.2711 EndY=22.0965 EndZ=0
    g29: LineSegment StartX=16.2711 StartY=22.0965 StartZ=0 EndX=19.0901 EndY=23.1225 EndZ=0
    g30: LineSegment StartX=19.0901 StartY=23.1225 StartZ=0 EndX=20.8002 EndY=18.4241 EndZ=0
    g31: LineSegment StartX=19.0901 StartY=23.1225 StartZ=0 EndX=21.9092 EndY=24.1486 EndZ=0
    g32: LineSegment StartX=21.9092 StartY=24.1486 StartZ=0 EndX=18.489 EndY=33.5455 EndZ=0
    g33: LineSegment StartX=28.6371 StartY=38.8283 StartZ=0 EndX=34.3729 EndY=30.6368 EndZ=0
    g34: LineSegment StartX=34.3729 StartY=30.6368 StartZ=0 EndX=36.8304 EndY=32.3575 EndZ=0
    g35: LineSegment StartX=36.8304 StartY=32.3575 StartZ=0 EndX=39.6982 EndY=28.2617 EndZ=0
    g36: LineSegment StartX=-11.9293 StartY=13.0924 StartZ=0 EndX=-12.6239 EndY=9.15319 EndZ=0
    g37: LineSegment StartX=-9.11523 StartY=9 StartZ=0 EndX=-9.46385 EndY=12.9848 EndZ=0
    g38: LineSegment StartX=9.46385 StartY=14.6407 StartZ=0 EndX=9.81247 EndY=10.656 EndZ=0
    g39: LineSegment StartX=13.2412 StartY=11.4161 StartZ=0 EndX=11.8732 EndY=15.1749 EndZ=0
    g40: LineSegment StartX=29.7273 StartY=21.6733 StartZ=0 EndX=31.0954 EndY=17.9145 EndZ=0
    g41: LineSegment StartX=34.2106 StartY=19.5362 StartZ=0 EndX=31.9163 EndY=22.8128 EndZ=0
    g42: ArcOfCircle CenterX=-8.11558 CenterY=72.1532 CenterZ=0 NormalX=0 NormalY=0 NormalZ=1 AngleXU=0 Radius=43.8257 StartAngle=4.53786 EndAngle=4.79966
    g43: ArcOfCircle CenterX=-2.13841 CenterY=72.6761 CenterZ=0 NormalX=0 NormalY=0 NormalZ=1 AngleXU=0 Radius=43.8257 StartAngle=4.79966 EndAngle=5.06145
    g44: ArcOfCircle CenterX=3.49974 CenterY=74.7282 CenterZ=0 NormalX=0 NormalY=0 NormalZ=1 AngleXU=0 Radius=43.8257 StartAngle=5.06145 EndAngle=5.32325
    g45: LineSegment StartX=-50 StartY=3 StartZ=0 EndX=-70 EndY=3 EndZ=0
    g46: LineSegment StartX=-50 StartY=0 StartZ=0 EndX=-50 EndY=3 EndZ=0
    g47: LineSegment StartX=-50 StartY=3 StartZ=0 EndX=-50 EndY=9 EndZ=0
    g48: LineSegment StartX=-50 StartY=9 StartZ=0 EndX=50 EndY=9 EndZ=0
  constraints (142):
    c: Coincident(g0,g1)
    c: Coincident(g1,g2)
    c: Coincident(g2,g3)
    c: Coincident(g3,g4)
    c: Coincident(g4,g5)
    c: Coincident(g5,g6)
    c: Coincident(g6,g7)
    c: Coincident(g7,g8)
    c: Coincident(g8,g9)
    c: Coincident(g9,g10)
    c: Coincident(g10,g11)
    c: Coincident(g11,g12)
    c: Coincident(g12,g13)
    c: Coincident(g13,g14)
    c: Coincident(g14,g15)
    c: Coincident(g15,g16)
    c: Coincident(g16,g17)
    c: Coincident(g17,g18)
    c: Coincident(g18,g19)
    c: Coincident(g19,g0)
    c: Angle(g18,g17) = 3.14159
    c: Angle(g14,g15) = 3.14159
    c: Angle(g12,g11) = 3.14159
    c: Angle(g9,g8) = 3.14159
    c: Coincident(g17,g20)
    c: Coincident(g20,g21)
    c: Coincident(g21,g22)
    c: Coincident(g23,g24)
    c: Coincident(g24,g25)
    c: Coincident(g25,g14)
    c: Coincident(g24,g26)
    c: Coincident(g26,g27)
    c: Coincident(g28,g29)
    c: Coincident(g29,g30)
    c: Coincident(g30,g11)
    c: Coincident(g29,g31)
    c: Coincident(g31,g32)
    c: Coincident(g33,g34)
    c: Coincident(g34,g35)
    c: Coincident(g35,g8)
    c: Coincident(g36,g16)
    c: Coincident(g36,g0)
    c: Coincident(g37,g1)
    c: Coincident(g37,g15)
    c: Coincident(g38,g13)
    c: Coincident(g38,g2)
    c: Coincident(g39,g3)
    c: Coincident(g39,g12)
    c: Coincident(g40,g10)
    c: Coincident(g40,g4)
    c: Coincident(g41,g5)
    c: Coincident(g41,g9)
    c: Coincident(g42,g23)
    c: Coincident(g43,g27)
    c: Coincident(g43,g28)
    c: Coincident(g44,g32)
    c: Coincident(g44,g33)
    c: Coincident(g42,g22)
    c: Perpendicular(g42,g23)
    c: Perpendicular(g42,g22)
    c: Perpendicular(g43,g27)
    c: Perpendicular(g43,g28)
    c: Perpendicular(g44,g32)
    c: Perpendicular(g44,g33)
    c: Perpendicular(g21,g22)
    c: Perpendicular(g24,g23)
    c: Perpendicular(g26,g27)
    c: Perpendicular(g29,g28)
    c: Perpendicular(g31,g32)
    c: Perpendicular(g34,g33)
    c: Perpendicular(g20,g21)
    c: Perpendicular(g17,g20)
    c: Perpendicular(g15,g25)
    c: Perpendicular(g12,g30)
    c: Perpendicular(g30,g31)
    c: Perpendicular(g35,g34)
    c: Equal(g34,g31)
    c: Equal(g31,g29)
    c: Equal(g29,g26)
    c: Equal(g26,g24)
    c: Equal(g24,g21)
    c: Distance(g24) = 3
    c: Angle(g24,g26) = 3.14159
    c: Angle(g29,g31) = 3.14159
    c: Perpendicular(g9,g35)
    c: Equal(g9,g8)
    c: Perpendicular(g6,g7)
    c: Equal(g41,g40)
    c: Equal(g6,g4)
    c: Equal(g4,g2)
    c: Equal(g2,g0)
    c: Perpendicular(g25,g24)
    c: Equal(g14,g15)
    c: Equal(g17,g18)
    c: Equal(g11,g12)
    c: Distance(g2) = 19
    c: Perpendicular(g37,g2)
    c: Perpendicular(g38,g14)
    c: Perpendicular(g37,g15)
    c: Distance(g37) = 4
    c: Equal(g36,g37)
    c: Perpendicular(g17,g36)
    c: Perpendicular(g0,g19)
    c: Perpendicular(g19,g18)
    c: Distance(g20) = 5
    c: Distance(g25) = 5
    c: Distance(g30) = 5
    c: Distance(g35) = 5
    c: Perpendicular(g6,g41)
    c: Equal(g39,g38)
    c: Perpendicular(g41,g9)
    c: Perpendicular(g4,g39)
    c: Perpendicular(g40,g11)
    c: Perpendicular(g12,g39)
    c: Distance(g33) = 10
    c: Distance(g32) = 10
    c: Distance(g28) = 10
    c: Distance(g27) = 10
    c: Distance(g23) = 10
    c: Distance(g22) = 10
    c: Distance(g24,g20) = 20
    c: Distance(g29,g24) = 20
    c: Distance(g29,g34) = 20
    c: Angle(g20,g25) = 0.261799
    c: Angle(g25,g30) = 0.261799
    c: Angle(g30,g35) = 0.261799
    c: Angle(g45,g25) = 1.65806
    c: Horizontal(g45)
    c: PointOnObject(g46,g-1)
    c: Coincident(g46,g45)
    c: Vertical(g46)
    c: Coincident(g47,g45)
    c: Vertical(g47)
    c: Coincident(g48,g47)
    c: Horizontal(g48)
    c: DistanceX(g48,g48) = 100
    c: DistanceX(g45,g45) = 20
    c: DistanceY(g46,g46) = 3
    c: DistanceY(g47,g47) = 6
    c: DistanceX(g46,g-1) = 50
    c: PointOnObject(g14,g-2)
    c: PointOnObject(g1,g48)
FEATURE [PartDesign::Pad] Pad020  label="IIArch"
  Direction = (1,-2e-16,3e-16)
  Length = 19
  Length2 = 10
  Midplane = true
  Placement = pos=(0,0,0) rot=(0.57735,0.57735,0.57735;2.0944rad)
  Profile = -> Sketch032
  ReferenceAxis = -> Sketch032 [N_Axis]
  Type = 0
FEATURE [Sketcher::SketchObject] Sketch033
  ExternalGeometry = -> [Sketch032]
  FullyConstrained = true
  MapMode = 5
  Placement = pos=(0,0,0) rot=(0.57735,0.57735,0.57735;2.0944rad)
  Support = -> [YZ_Plane005]
  sketch-geometry (60):
    g0: LineSegment StartX=-28.1786 StartY=15.9576 StartZ=0 EndX=-21.285 EndY=14.7421 EndZ=0
    g1: LineSegment StartX=-21.285 StartY=14.7421 StartZ=0 EndX=-14.3913 EndY=13.5265 EndZ=0
    g2: LineSegment StartX=-14.3913 StartY=13.5265 StartZ=0 EndX=-14.6344 EndY=12.1478 EndZ=0
    g3: LineSegment StartX=-14.6344 StartY=12.1478 StartZ=0 EndX=-13.3542 EndY=11.9221 EndZ=0
    g4: LineSegment StartX=-13.3542 StartY=11.9221 StartZ=0 EndX=-13.8057 EndY=9.36157 EndZ=0
    g5: LineSegment StartX=-30.1535 StartY=12.2441 StartZ=0 EndX=-29.702 EndY=14.8046 EndZ=0
    g6: LineSegment StartX=-29.702 StartY=14.8046 StartZ=0 EndX=-28.4217 EndY=14.5789 EndZ=0
    g7: LineSegment StartX=-28.4217 StartY=14.5789 StartZ=0 EndX=-28.1786 EndY=15.9576 EndZ=0
    g8: LineSegment StartX=-6.97336 StartY=13.2027 StartZ=0 EndX=0 EndY=13.8128 EndZ=0
    g9: LineSegment StartX=0 StartY=13.8128 StartZ=0 EndX=6.97336 EndY=14.4228 EndZ=0
    g10: LineSegment StartX=6.97336 StartY=14.4228 StartZ=0 EndX=7.09538 EndY=13.0282 EndZ=0
    g11: LineSegment StartX=7.09538 StartY=13.0282 StartZ=0 EndX=8.39043 EndY=13.1415 EndZ=0
    g12: LineSegment StartX=8.39043 StartY=13.1415 StartZ=0 EndX=8.61704 EndY=10.5514 EndZ=0
    g13: LineSegment StartX=-7.91979 StartY=9.10459 StartZ=0 EndX=-8.1464 EndY=11.6947 EndZ=0
    g14: LineSegment StartX=-8.1464 StartY=11.6947 StartZ=0 EndX=-6.85134 EndY=11.808 EndZ=0
    g15: LineSegment StartX=-6.85134 StartY=11.808 StartZ=0 EndX=-6.97336 EndY=13.2027 EndZ=0
    g16: LineSegment StartX=14.2224 StartY=16.0299 StartZ=0 EndX=20.8002 EndY=18.4241 EndZ=0
    g17: LineSegment StartX=20.8002 StartY=18.4241 StartZ=0 EndX=27.3781 EndY=20.8182 EndZ=0
    g18: LineSegment StartX=27.3781 StartY=20.8182 StartZ=0 EndX=27.8569 EndY=19.5026 EndZ=0
    g19: LineSegment StartX=27.8569 StartY=19.5026 StartZ=0 EndX=29.0785 EndY=19.9473 EndZ=0
    g20: LineSegment StartX=29.0785 StartY=19.9473 StartZ=0 EndX=29.9678 EndY=17.5041 EndZ=0
    g21: LineSegment StartX=14.3689 StartY=11.8265 StartZ=0 EndX=13.4796 EndY=14.2697 EndZ=0
    g22: LineSegment StartX=13.4796 StartY=14.2697 StartZ=0 EndX=14.7012 EndY=14.7144 EndZ=0
    g23: LineSegment StartX=14.7012 StartY=14.7144 StartZ=0 EndX=14.2224 EndY=16.0299 EndZ=0
    g24: LineSegment StartX=33.9642 StartY=24.2467 StartZ=0 EndX=39.6982 EndY=28.2617 EndZ=0
    g25: LineSegment StartX=39.6982 StartY=28.2617 StartZ=0 EndX=45.4323 EndY=32.2768 EndZ=0
    g26: LineSegment StartX=45.4323 StartY=32.2768 StartZ=0 EndX=46.2353 EndY=31.13 EndZ=0
    g27: LineSegment StartX=46.2353 StartY=31.13 StartZ=0 EndX=47.3002 EndY=31.8756 EndZ=0
    g28: LineSegment StartX=47.3002 StartY=31.8756 StartZ=0 EndX=48.7915 EndY=29.7458 EndZ=0
    g29: LineSegment StartX=35.1936 StartY=20.2244 StartZ=0 EndX=33.7023 EndY=22.3542 EndZ=0
    g30: LineSegment StartX=33.7023 StartY=22.3542 StartZ=0 EndX=34.7672 EndY=23.0999 EndZ=0
    g31: LineSegment StartX=34.7672 StartY=23.0999 StartZ=0 EndX=33.9642 EndY=24.2467 EndZ=0
    g32: LineSegment StartX=47.3002 StartY=31.8756 StartZ=0 EndX=46.4972 EndY=33.0224 EndZ=0
    g33: LineSegment StartX=46.2353 StartY=31.13 StartZ=0 EndX=47.7266 EndY=29.0002 EndZ=0
    g34: LineSegment StartX=36.2585 StartY=20.9701 StartZ=0 EndX=34.7672 EndY=23.0999 EndZ=0
    g35: LineSegment StartX=33.7023 StartY=22.3542 StartZ=0 EndX=32.8993 EndY=23.5011 EndZ=0
    g36: LineSegment StartX=28.5997 StartY=21.2628 StartZ=0 EndX=29.0785 EndY=19.9473 EndZ=0
    g37: LineSegment StartX=27.8569 StartY=19.5026 StartZ=0 EndX=28.7462 EndY=17.0594 EndZ=0
    g38: LineSegment StartX=15.5905 StartY=12.2711 StartZ=0 EndX=14.7012 EndY=14.7144 EndZ=0
    g39: LineSegment StartX=13.4796 StartY=14.2697 StartZ=0 EndX=13.0008 EndY=15.5853 EndZ=0
    g40: LineSegment StartX=8.26842 StartY=14.5362 StartZ=0 EndX=8.39043 EndY=13.1415 EndZ=0
    g41: LineSegment StartX=7.09538 StartY=13.0282 StartZ=0 EndX=7.32199 EndY=10.4381 EndZ=0
    g42: LineSegment StartX=-6.85134 StartY=11.808 StartZ=0 EndX=-6.62474 EndY=9.21789 EndZ=0
    g43: LineSegment StartX=-8.1464 StartY=11.6947 StartZ=0 EndX=-8.26842 EndY=13.0894 EndZ=0
    g44: LineSegment StartX=-13.1111 StartY=13.3008 StartZ=0 EndX=-13.3542 EndY=11.9221 EndZ=0
    g45: LineSegment StartX=-14.6344 StartY=12.1478 StartZ=0 EndX=-15.0859 EndY=9.58731 EndZ=0
    g46: LineSegment StartX=-28.8732 StartY=12.0184 StartZ=0 EndX=-28.4217 EndY=14.5789 EndZ=0
    g47: LineSegment StartX=-29.702 StartY=14.8046 StartZ=0 EndX=-29.4589 EndY=16.1834 EndZ=0
    g48: LineSegment StartX=-21.285 StartY=14.7421 StartZ=0 EndX=-21.9796 EndY=10.8028 EndZ=0
    g49: LineSegment StartX=0 StartY=13.8128 StartZ=0 EndX=0.348623 EndY=9.82798 EndZ=0
    g50: LineSegment StartX=39.6982 StartY=28.2617 StartZ=0 EndX=41.9925 EndY=24.9851 EndZ=0
    g51: LineSegment StartX=20.8002 StartY=18.4241 StartZ=0 EndX=22.1683 EndY=14.6653 EndZ=0
    g52: LineSegment StartX=48.7915 StartY=29.7458 StartZ=0 EndX=41.9925 EndY=24.9851 EndZ=0
    g53: LineSegment StartX=41.9925 StartY=24.9851 StartZ=0 EndX=35.1936 EndY=20.2244 EndZ=0
    g54: LineSegment StartX=29.9678 StartY=17.5041 StartZ=0 EndX=22.1683 EndY=14.6653 EndZ=0
    g55: LineSegment StartX=22.1683 StartY=14.6653 StartZ=0 EndX=14.3689 EndY=11.8265 EndZ=0
    g56: LineSegment StartX=8.61704 StartY=10.5514 StartZ=0 EndX=0.348623 EndY=9.82798 EndZ=0
    g57: LineSegment StartX=0.348623 StartY=9.82798 StartZ=0 EndX=-7.91979 EndY=9.10459 EndZ=0
    g58: LineSegment StartX=-13.8057 StartY=9.36157 StartZ=0 EndX=-21.9796 EndY=10.8028 EndZ=0
    g59: LineSegment StartX=-21.9796 StartY=10.8028 StartZ=0 EndX=-30.1535 EndY=12.2441 EndZ=0
  constraints (167):
    c: PointOnObject(g0,g-4)
    c: Coincident(g0,g-4)
    c: Coincident(g0,g1)
    c: Coincident(g1,g2)
    c: Coincident(g2,g3)
    c: Coincident(g3,g4)
    c: PointOnObject(g5,g-5)
    c: Coincident(g5,g6)
    c: Coincident(g6,g7)
    c: Coincident(g7,g0)
    c: PointOnObject(g8,g-6)
    c: Coincident(g8,g-7)
    c: Coincident(g8,g9)
    c: PointOnObject(g9,g-7)
    c: Coincident(g9,g10)
    c: Coincident(g10,g11)
    c: Coincident(g11,g12)
    c: PointOnObject(g13,g-8)
    c: Coincident(g13,g14)
    c: Coincident(g14,g15)
    c: Coincident(g15,g8)
    c: PointOnObject(g16,g-10)
    c: Coincident(g16,g-11)
    c: Coincident(g16,g17)
    c: PointOnObject(g17,g-11)
    c: Coincident(g17,g18)
    c: Coincident(g18,g19)
    c: Coincident(g19,g20)
    c: PointOnObject(g21,g-9)
    c: Coincident(g21,g22)
    c: Coincident(g22,g23)
    c: Coincident(g23,g16)
    c: PointOnObject(g24,g-12)
    c: Coincident(g24,g-13)
    c: Coincident(g24,g25)
    c: PointOnObject(g25,g-13)
    c: Coincident(g25,g26)
    c: Coincident(g26,g27)
    c: Coincident(g27,g28)
    c: PointOnObject(g29,g-14)
    c: Coincident(g29,g30)
    c: Coincident(g30,g31)
    c: Coincident(g31,g24)
    c: Coincident(g32,g27)
    c: PointOnObject(g32,g-13)
    c: Coincident(g33,g26)
    c: Coincident(g34,g30)
    c: PointOnObject(g35,g-12)
    c: PointOnObject(g36,g-11)
    c: Coincident(g36,g19)
    c: Coincident(g37,g18)
    c: Coincident(g38,g22)
    c: Coincident(g39,g21)
    c: PointOnObject(g39,g-10)
    c: PointOnObject(g40,g-7)
    c: Coincident(g40,g11)
    c: Coincident(g41,g10)
    c: Coincident(g42,g14)
    c: Coincident(g43,g13)
    c: PointOnObject(g43,g-6)
    c: PointOnObject(g44,g-3)
    c: Coincident(g44,g3)
    c: Coincident(g45,g2)
    c: Coincident(g46,g6)
    c: Coincident(g47,g5)
    c: PointOnObject(g47,g-4)
    c: Symmetric(g1,g0,g0)
    c: Equal(g47,g7)
    c: Equal(g7,g2)
    c: Equal(g2,g44)
    c: Equal(g44,g43)
    c: Equal(g43,g15)
    c: Equal(g15,g10)
    c: Equal(g10,g40)
    c: Equal(g40,g39)
    c: Equal(g39,g23)
    c: Equal(g23,g18)
    c: Equal(g18,g36)
    c: Equal(g36,g35)
    c: Equal(g35,g31)
    c: Equal(g31,g26)
    c: Equal(g26,g32)
    c: Distance(g40) = 1.4
    c: Distance(g1,g0) = 14
    c: Distance(g5,g4) = 16.6
    c: Coincident(g48,g0)
    c: Perpendicular(g1,g48)
    c: Symmetric(g5,g4,g48)
    c: Angle(g5,g47) = 3.14159
    c: Angle(g7,g46) = 3.14159
    c: Angle(g45,g2) = 3.14159
    c: Angle(g4,g44) = 3.14159
    c: Perpendicular(g0,g7)
    c: Perpendicular(g1,g2)
    c: Coincident(g49,g8)
    c: Perpendicular(g9,g49)
    c: Symmetric(g13,g12,g49)
    c: Coincident(g29,g35)
    c: Angle(g29,g35) = 3.14159
    c: Angle(g31,g34) = 3.14159
    c: Angle(g26,g33) = 3.14159
    c: Angle(g32,g28) = 3.14159
    c: Angle(g36,g20) = 3.14159
    c: Angle(g18,g37) = 3.14159
    c: Angle(g23,g38) = 3.14159
    c: Angle(g21,g39) = 3.14159
    c: Angle(g12,g40) = 3.14159
    c: Angle(g10,g41) = 3.14159
    c: Angle(g42,g15) = 3.14159
    c: Angle(g13,g43) = 3.14159
    c: Equal(g8,g9)
    c: Equal(g9,g16)
    c: Equal(g16,g17)
    c: Equal(g17,g24)
    c: Equal(g24,g25)
    c: Equal(g8,g1)
    c: Coincident(g50,g24)
    c: Coincident(g51,g16)
    c: Perpendicular(g51,g17)
    c: Perpendicular(g50,g25)
    c: Symmetric(g29,g28,g50)
    c: Symmetric(g21,g20,g51)
    c: Perpendicular(g18,g17)
    c: Perpendicular(g16,g23)
    c: Perpendicular(g9,g10)
    c: Perpendicular(g8,g15)
    c: Perpendicular(g24,g31)
    c: Perpendicular(g25,g26)
    c: Coincident(g28,g52)
    c: Coincident(g52,g50)
    c: Coincident(g52,g53)
    c: Coincident(g53,g29)
    c: Coincident(g20,g54)
    c: Coincident(g54,g51)
    c: Coincident(g54,g55)
    c: Coincident(g55,g21)
    c: Coincident(g12,g56)
    c: Coincident(g56,g49)
    c: Coincident(g56,g57)
    c: Coincident(g57,g13)
    c: Coincident(g4,g58)
    c: Coincident(g58,g48)
    c: Coincident(g58,g59)
    c: Coincident(g59,g5)
    c: PointOnObject(g58,g-5)
    c: PointOnObject(g56,g-8)
    c: PointOnObject(g54,g-9)
    c: PointOnObject(g52,g-14)
    c: Distance(g28,g29) = 16.6
    c: Perpendicular(g53,g29)
    c: Perpendicular(g52,g28)
    c: PointOnObject(g33,g52)
    c: PointOnObject(g34,g53)
    c: PointOnObject(g37,g54)
    c: PointOnObject(g38,g55)
    c: PointOnObject(g41,g56)
    c: PointOnObject(g42,g57)
    c: PointOnObject(g45,g58)
    c: PointOnObject(g46,g59)
    c: Perpendicular(g5,g59)
    c: Perpendicular(g58,g4)
    c: Perpendicular(g57,g13)
    c: Distance(g12,g13) = 16.6
    c: Distance(g21,g20) = 16.6
    c: Perpendicular(g56,g12)
    c: Perpendicular(g21,g55)
    c: Perpendicular(g54,g20)
FEATURE [PartDesign::Pocket] Pocket010  label="IIMX Sockets"
  BaseFeature = -> Pad020
  Direction = (-1,2e-16,-3e-16)
  Length = 14
  Length2 = 5
  Midplane = true
  Placement = pos=(0,0,0) rot=(0.57735,0.57735,0.57735;2.0944rad)
  Profile = -> Sketch033
  ReferenceAxis = -> Sketch033 [N_Axis]
  Type = 0
FEATURE [Sketcher::SketchObject] Sketch034
  ExternalGeometry = -> [Sketch033]
  FullyConstrained = true
  MapMode = 5
  Placement = pos=(0,0,0) rot=(0.57735,0.57735,0.57735;2.0944rad)
  Support = -> [YZ_Plane005]
  sketch-geometry (44):
    g0: LineSegment StartX=-21.285 StartY=14.7421 StartZ=0 EndX=-21.4934 EndY=13.5603 EndZ=0
    g1: LineSegment StartX=-21.4934 StartY=13.5603 StartZ=0 EndX=-21.667 EndY=12.5755 EndZ=0
    g2: LineSegment StartX=-21.667 StartY=12.5755 StartZ=0 EndX=-21.9796 EndY=10.8028 EndZ=0
    g3: LineSegment StartX=0 StartY=13.8128 StartZ=0 EndX=0.104587 EndY=12.6173 EndZ=0
    g4: LineSegment StartX=0.104587 StartY=12.6173 StartZ=0 EndX=0.191743 EndY=11.6211 EndZ=0
    g5: LineSegment StartX=0.191743 StartY=11.6211 StartZ=0 EndX=0.348623 EndY=9.82798 EndZ=0
    g6: LineSegment StartX=20.8002 StartY=18.4241 StartZ=0 EndX=21.2107 EndY=17.2964 EndZ=0
    g7: LineSegment StartX=21.2107 StartY=17.2964 StartZ=0 EndX=21.5527 EndY=16.3567 EndZ=0
    g8: LineSegment StartX=21.5527 StartY=16.3567 StartZ=0 EndX=22.1683 EndY=14.6653 EndZ=0
    g9: LineSegment StartX=39.6982 StartY=28.2617 StartZ=0 EndX=40.3865 EndY=27.2788 EndZ=0
    g10: LineSegment StartX=40.3865 StartY=27.2788 StartZ=0 EndX=40.9601 EndY=26.4596 EndZ=0
    g11: LineSegment StartX=40.9601 StartY=26.4596 StartZ=0 EndX=41.9925 EndY=24.9851 EndZ=0
    g12: LineSegment StartX=14.6328 StartY=14.9023 StartZ=0 EndX=27.7885 EndY=19.6906 EndZ=0
    g13: LineSegment StartX=27.7885 StartY=19.6906 StartZ=0 EndX=27.8569 EndY=19.5026 EndZ=0
    g14: LineSegment StartX=27.8569 StartY=19.5026 StartZ=0 EndX=29.0785 EndY=19.9473 EndZ=0
    g15: LineSegment StartX=29.0785 StartY=19.9473 StartZ=0 EndX=29.3521 EndY=19.1955 EndZ=0
    g16: LineSegment StartX=29.3521 StartY=19.1955 StartZ=0 EndX=13.7532 EndY=13.518 EndZ=0
    g17: LineSegment StartX=13.7532 StartY=13.518 StartZ=0 EndX=13.4796 EndY=14.2697 EndZ=0
    g18: LineSegment StartX=13.4796 StartY=14.2697 StartZ=0 EndX=14.7012 EndY=14.7144 EndZ=0
    g19: LineSegment StartX=14.7012 StartY=14.7144 StartZ=0 EndX=14.6328 EndY=14.9023 EndZ=0
    g20: LineSegment StartX=-6.86878 StartY=12.0072 StartZ=0 EndX=7.07795 EndY=13.2274 EndZ=0
    g21: LineSegment StartX=7.07795 StartY=13.2274 StartZ=0 EndX=7.09538 EndY=13.0282 EndZ=0
    g22: LineSegment StartX=7.09538 StartY=13.0282 StartZ=0 EndX=8.39043 EndY=13.1415 EndZ=0
    g23: LineSegment StartX=8.39043 StartY=13.1415 StartZ=0 EndX=8.46016 EndY=12.3445 EndZ=0
    g24: LineSegment StartX=8.46016 StartY=12.3445 StartZ=0 EndX=-8.07667 EndY=10.8977 EndZ=0
    g25: LineSegment StartX=-8.07667 StartY=10.8977 StartZ=0 EndX=-8.1464 EndY=11.6947 EndZ=0
    g26: LineSegment StartX=-8.1464 StartY=11.6947 StartZ=0 EndX=-6.85134 EndY=11.808 EndZ=0
    g27: LineSegment StartX=-6.85134 StartY=11.808 StartZ=0 EndX=-6.86878 EndY=12.0072 EndZ=0
    g28: LineSegment StartX=-28.387 StartY=14.7758 StartZ=0 EndX=-14.5997 EndY=12.3448 EndZ=0
    g29: LineSegment StartX=-14.5997 StartY=12.3448 StartZ=0 EndX=-14.6344 EndY=12.1478 EndZ=0
    g30: LineSegment StartX=-14.6344 StartY=12.1478 StartZ=0 EndX=-13.3542 EndY=11.9221 EndZ=0
    g31: LineSegment StartX=-13.3542 StartY=11.9221 StartZ=0 EndX=-13.4931 EndY=11.1342 EndZ=0
    g32: LineSegment StartX=-13.4931 StartY=11.1342 StartZ=0 EndX=-29.8409 EndY=14.0168 EndZ=0
    g33: LineSegment StartX=-29.8409 StartY=14.0168 StartZ=0 EndX=-29.702 EndY=14.8046 EndZ=0
    g34: LineSegment StartX=-29.702 StartY=14.8046 StartZ=0 EndX=-28.4217 EndY=14.5789 EndZ=0
    g35: LineSegment StartX=-28.4217 StartY=14.5789 StartZ=0 EndX=-28.387 EndY=14.7758 EndZ=0
    g36: LineSegment StartX=34.6525 StartY=23.2637 StartZ=0 EndX=46.1206 EndY=31.2938 EndZ=0
    g37: LineSegment StartX=46.1206 StartY=31.2938 StartZ=0 EndX=46.2353 EndY=31.13 EndZ=0
    g38: LineSegment StartX=46.2353 StartY=31.13 StartZ=0 EndX=47.3002 EndY=31.8756 EndZ=0
    g39: LineSegment StartX=47.3002 StartY=31.8756 StartZ=0 EndX=47.7591 EndY=31.2203 EndZ=0
    g40: LineSegment StartX=47.7591 StartY=31.2203 StartZ=0 EndX=34.1611 EndY=21.6989 EndZ=0
    g41: LineSegment StartX=34.1611 StartY=21.6989 StartZ=0 EndX=33.7023 EndY=22.3542 EndZ=0
    g42: LineSegment StartX=33.7023 StartY=22.3542 StartZ=0 EndX=34.7672 EndY=23.0999 EndZ=0
    g43: LineSegment StartX=34.7672 StartY=23.0999 StartZ=0 EndX=34.6525 EndY=23.2637 EndZ=0
  constraints (112):
    c: Coincident(g-11,g0)
    c: Coincident(g0,g1)
    c: Coincident(g1,g2)
    c: Coincident(g2,g-14)
    c: Coincident(g-7,g3)
    c: Coincident(g3,g4)
    c: Coincident(g4,g5)
    c: Coincident(g5,g-8)
    c: Coincident(g-4,g6)
    c: Coincident(g6,g7)
    c: Coincident(g7,g8)
    c: Coincident(g8,g-6)
    c: Coincident(g-15,g9)
    c: Coincident(g9,g10)
    c: Coincident(g10,g11)
    c: Coincident(g11,g-18)
    c: Angle(g11,g10) = 3.14159
    c: Angle(g9,g10) = 3.14159
    c: Angle(g7,g6) = 3.14159
    c: Angle(g7,g8) = 3.14159
    c: Angle(g4,g3) = 3.14159
    c: Angle(g4,g5) = 3.14159
    c: Angle(g1,g0) = 3.14159
    c: Angle(g1,g2) = 3.14159
    c: Equal(g1,g4)
    c: Equal(g7,g10)
    c: Equal(g7,g4)
    c: PointOnObject(g12,g-3)
    c: PointOnObject(g12,g-22)
    c: Coincident(g12,g13)
    c: Coincident(g13,g-22)
    c: Coincident(g13,g14)
    c: Coincident(g14,g-21)
    c: Coincident(g14,g15)
    c: PointOnObject(g15,g-21)
    c: Coincident(g15,g16)
    c: PointOnObject(g16,g-5)
    c: Coincident(g16,g17)
    c: Coincident(g17,g-5)
    c: Coincident(g17,g18)
    c: Coincident(g18,g-3)
    c: Coincident(g18,g19)
    c: Coincident(g19,g12)
    c: PointOnObject(g6,g12)
    c: PointOnObject(g7,g16)
    c: Perpendicular(g6,g12)
    c: Perpendicular(g8,g16)
    c: PointOnObject(g20,g-10)
    c: PointOnObject(g20,g-23)
    c: Coincident(g20,g21)
    c: Coincident(g21,g22)
    c: Coincident(g22,g-24)
    c: Coincident(g22,g23)
    c: PointOnObject(g23,g-24)
    c: Coincident(g23,g24)
    c: PointOnObject(g24,g-9)
    c: Coincident(g24,g25)
    c: Coincident(g25,g-9)
    c: Coincident(g25,g26)
    c: Coincident(g26,g-10)
    c: Coincident(g26,g27)
    c: Coincident(g27,g20)
    c: Coincident(g-23,g21)
    c: Perpendicular(g3,g20)
    c: Perpendicular(g5,g24)
    c: PointOnObject(g4,g24)
    c: PointOnObject(g3,g20)
    c: PointOnObject(g28,g-25)
    c: Coincident(g28,g29)
    c: Coincident(g29,g-25)
    c: Coincident(g29,g30)
    c: Coincident(g30,g-26)
    c: Coincident(g30,g31)
    c: PointOnObject(g31,g-26)
    c: Coincident(g31,g32)
    c: PointOnObject(g32,g-13)
    c: Coincident(g32,g33)
    c: Coincident(g33,g-13)
    c: Coincident(g33,g34)
    c: Coincident(g34,g-12)
    c: Coincident(g34,g35)
    c: Coincident(g35,g28)
    c: PointOnObject(g28,g-12)
    c: Perpendicular(g0,g28)
    c: Perpendicular(g2,g32)
    c: PointOnObject(g1,g32)
    c: PointOnObject(g0,g28)
    c: Distance(g3) = 1.2
    c: Distance(g4) = 1
    c: Equal(g0,g3)
    c: Equal(g6,g3)
    c: Equal(g9,g3)
    c: PointOnObject(g36,g-16)
    c: PointOnObject(g36,g-19)
    c: Coincident(g36,g37)
    c: Coincident(g37,g-19)
    c: Coincident(g37,g38)
    c: Coincident(g38,g-20)
    c: Coincident(g38,g39)
    c: PointOnObject(g39,g-20)
    c: Coincident(g39,g40)
    c: PointOnObject(g40,g-17)
    c: Coincident(g40,g41)
    c: Coincident(g41,g-17)
    c: Coincident(g41,g42)
    c: Coincident(g42,g-16)
    c: Coincident(g43,g42)
    c: Coincident(g43,g36)
    c: PointOnObject(g9,g36)
    c: PointOnObject(g10,g40)
    c: Perpendicular(g9,g36)
    c: Perpendicular(g11,g40)
FEATURE [PartDesign::Pocket] Pocket011  label="IIChoc Sockets"
  BaseFeature = -> Pocket010
  Direction = (-1,2e-16,-3e-16)
  Length = 14.6
  Length2 = 5
  Midplane = true
  Placement = pos=(0,0,0) rot=(0.57735,0.57735,0.57735;2.0944rad)
  Profile = -> Sketch034
  ReferenceAxis = -> Sketch034 [N_Axis]
  Type = 0
FEATURE [Sketcher::SketchObject] Sketch035
  ExternalGeometry = -> [Sketch032]
  FullyConstrained = true
  MapMode = 5
  Placement = pos=(0,0,0) rot=(0.57735,0.57735,0.57735;2.0944rad)
  Support = -> [YZ_Plane005]
  expr: Constraints[17] = <<Spreadsheet>>.Wiring
  sketch-geometry (8):
    g0: LineSegment StartX=9.46385 StartY=14.6407 StartZ=0 EndX=11.8732 EndY=15.1749 EndZ=0
    g1: LineSegment StartX=11.8732 StartY=15.1749 StartZ=0 EndX=13.2412 EndY=11.4161 EndZ=0
    g2: LineSegment StartX=13.2412 StartY=11.4161 StartZ=0 EndX=15.2934 EndY=5.77794 EndZ=0
    g3: LineSegment StartX=15.2934 StartY=5.77794 StartZ=0 EndX=15.2934 EndY=0 EndZ=0
    g4: LineSegment StartX=15.2934 StartY=0 StartZ=0 EndX=10.3354 EndY=0 EndZ=0
    g5: LineSegment StartX=10.3354 StartY=0 StartZ=0 EndX=10.3354 EndY=4.67879 EndZ=0
    g6: LineSegment StartX=10.3354 StartY=4.67879 StartZ=0 EndX=9.81247 EndY=10.656 EndZ=0
    g7: LineSegment StartX=9.81247 StartY=10.656 StartZ=0 EndX=9.46385 EndY=14.6407 EndZ=0
  constraints (20):
    c: Coincident(g-3,g0)
    c: Coincident(g0,g-3)
    c: Coincident(g0,g1)
    c: Coincident(g1,g-4)
    c: Coincident(g1,g2)
    c: Coincident(g2,g3)
    c: PointOnObject(g3,g-1)
    c: Vertical(g3)
    c: Coincident(g3,g4)
    c: PointOnObject(g4,g-1)
    c: Coincident(g4,g5)
    c: Vertical(g5)
    c: Coincident(g5,g6)
    c: Coincident(g6,g-4)
    c: Coincident(g6,g7)
    c: Coincident(g7,g0)
    c: Equal(g2,g6)
    c: Distance(g6) = 6
    c: Angle(g6,g7) = 3.14159
    c: Angle(g2,g1) = 3.14159
FEATURE [PartDesign::Pad] Pad021  label="IIInner Legs"
  BaseFeature = -> Pocket011
  Direction = (1,-2e-16,3e-16)
  Length = 4.1
  Length2 = 9.5
  Placement = pos=(0,0,0) rot=(0.57735,0.57735,0.57735;2.0944rad)
  Profile = -> Sketch035
  ReferenceAxis = -> Sketch035 [N_Axis]
  Type = 4
  expr: Length = <<Spreadsheet>>.ScrewD / 2 + 2mm
FEATURE [Sketcher::SketchObject] Sketch036
  ExternalGeometry = -> [Sketch032]
  FullyConstrained = true
  MapMode = 5
  Placement = pos=(0,0,0) rot=(0.57735,0.57735,0.57735;2.0944rad)
  Support = -> [YZ_Plane005]
  expr: Constraints[22] = <<Spreadsheet>>.ArchLength - 30mm
  expr: Constraints[23] = <<Spreadsheet>>.ArchLength - 25mm
  expr: Constraints[24] = <<Spreadsheet>>.ArchLength - 20mm
  expr: Constraints[71] = <<Spreadsheet>>.ArchLength
  expr: Constraints[72] = <<Spreadsheet>>.ArchLength - 5mm
  expr: Constraints[73] = <<Spreadsheet>>.ArchLength - 10mm
  sketch-geometry (36):
    g0: LineSegment StartX=-11.9293 StartY=13.0924 StartZ=0 EndX=-9.46385 EndY=12.9848 EndZ=0
    g1: LineSegment StartX=-9.46385 StartY=12.9848 StartZ=0 EndX=-9.11523 EndY=9 EndZ=0
    g2: LineSegment StartX=-9.11523 StartY=9 StartZ=0 EndX=-8.59229 EndY=3.02283 EndZ=0
    g3: LineSegment StartX=-8.59229 StartY=3.02283 StartZ=0 EndX=-15 EndY=0 EndZ=0
    g4: LineSegment StartX=-15 StartY=0 StartZ=0 EndX=-25 EndY=0 EndZ=0
    g5: LineSegment StartX=-25 StartY=0 StartZ=0 EndX=-25 EndY=3 EndZ=0
    g6: LineSegment StartX=-11.9293 StartY=13.0924 StartZ=0 EndX=-12.6239 EndY=9.15319 EndZ=0
    g7: LineSegment StartX=-12.6239 StartY=9.15319 StartZ=0 EndX=-13.6658 EndY=3.24435 EndZ=0
    g8: LineSegment StartX=-13.6658 StartY=3.24435 StartZ=0 EndX=-13.9496 EndY=1.63459 EndZ=0
    g9: LineSegment StartX=-25 StartY=3 StartZ=0 EndX=-20 EndY=3 EndZ=0
    g10: LineSegment StartX=37.6521 StartY=14.6212 StartZ=0 EndX=34.2106 EndY=19.5362 EndZ=0
    g11: LineSegment StartX=34.2106 StartY=19.5362 StartZ=0 EndX=31.9163 EndY=22.8128 EndZ=0
    g12: LineSegment StartX=31.9163 StartY=22.8128 StartZ=0 EndX=29.7273 EndY=21.6733 EndZ=0
    g13: LineSegment StartX=29.7273 StartY=21.6733 StartZ=0 EndX=31.0954 EndY=17.9145 EndZ=0
    g14: LineSegment StartX=31.0954 StartY=17.9145 StartZ=0 EndX=33.1475 EndY=12.2763 EndZ=0
    g15: LineSegment StartX=33.1475 StartY=12.2763 StartZ=0 EndX=35 EndY=0 EndZ=0
    g16: LineSegment StartX=35 StartY=0 StartZ=0 EndX=45 EndY=0 EndZ=0
    g17: LineSegment StartX=45 StartY=0 StartZ=0 EndX=45 EndY=3 EndZ=0
    g18: LineSegment StartX=45 StartY=3 StartZ=0 EndX=40 EndY=3 EndZ=0
    g19: LineSegment StartX=42.2621 StartY=8.03739 StartZ=0 EndX=37.6521 EndY=14.6212 EndZ=0
    g20: LineSegment StartX=-13.9496 StartY=1.63459 StartZ=0 EndX=-13.9496 EndY=0 EndZ=0
    g21-g24: Circle x4 (B-spline internal-alignment scaffolding for g25; pole/knot coordinates omitted)
    g25: BSplineCurve PolesCount=4 KnotsCount=2 Degree=3 IsPeriodic=0
    g26: GeomPoint X=-13.6658 Y=3.24435 Z=0
    g27: GeomPoint X=-25 Y=3 Z=0
    g28: LineSegment StartX=42.2621 StartY=8.03739 StartZ=0 EndX=42.2621 EndY=0 EndZ=0
    g29-g32: Circle x4 (B-spline internal-alignment scaffolding for g33; pole/knot coordinates omitted)
    g33: BSplineCurve PolesCount=4 KnotsCount=2 Degree=3 IsPeriodic=0
    g34: GeomPoint X=37.6521 Y=14.6212 Z=0
    g35: GeomPoint X=45 Y=3 Z=0
  constraints (82):
    c: Coincident(g-5,g0)
    c: Coincident(g0,g-5)
    c: Coincident(g0,g1)
    c: Coincident(g1,g-6)
    c: Coincident(g1,g2)
    c: Coincident(g2,g3)
    c: PointOnObject(g3,g-1)
    c: Coincident(g3,g4)
    c: PointOnObject(g4,g-1)
    c: Coincident(g4,g5)
    c: Vertical(g5)
    c: Coincident(g0,g6)
    c: Coincident(g6,g-6)
    c: Coincident(g7,g6)
    c: Distance(g7) = 6
    c: Equal(g2,g7)
    c: Coincident(g7,g8)
    c: Horizontal(g9)
    c: Angle(g7,g8) = 3.14159
    c: Angle(g6,g7) = 3.14159
    c: Angle(g2,g1) = 3.14159
    c: DistanceY(g5,g5) = 3
    c: DistanceX(g3,g-7) = 15
    c: DistanceX(g9,g-7) = 20
    c: DistanceX(g4,g-7) = 25
    c: Coincident(g10,g-4)
    c: Coincident(g10,g11)
    c: Coincident(g11,g-3)
    c: Coincident(g11,g12)
    c: Coincident(g12,g-3)
    c: Coincident(g12,g13)
    c: Coincident(g13,g-4)
    c: Coincident(g13,g14)
    c: Coincident(g14,g15)
    c: PointOnObject(g15,g-1)
    c: Coincident(g15,g16)
    c: PointOnObject(g16,g-1)
    c: Coincident(g16,g17)
    c: Vertical(g17)
    c: Coincident(g19,g10)
    c: Horizontal(g18)
    c: Angle(g19,g10) = 3.14159
    c: Angle(g14,g13) = 3.14159
    c: Angle(g10,g11) = 3.14159
    c: Equal(g10,g14)
    c: Equal(g10,g7)
    c: Coincident(g9,g5)
    c: Coincident(g20,g8)
    c: PointOnObject(g20,g-1)
    c: Vertical(g20)
    c: Equal(g20,g8)
    c: Weight(g21) = 1
    c: Coincident(g25,g7)
    c: Equal(g21,g22)
    c: Coincident(g22,g8)
    c: Equal(g21,g23)
    c: Coincident(g23,g9)
    c: Equal(g21,g24)
    c: Coincident(g25,g5)
    c: InternalAlignment(g21-g24 -> g25) x4
    c: InternalAlignment(g26,g25)
    c: InternalAlignment(g27,g25)
    c: Coincident(g28,g19)
    c: PointOnObject(g28,g-1)
    c: Vertical(g28)
    c: Equal(g28,g19)
    c: Coincident(g18,g17)
    c: Equal(g17,g5)
    c: DistanceX(g-7,g17) = 45
    c: DistanceX(g-7,g18) = 40
    c: DistanceX(g-7,g15) = 35
    c: Weight(g29) = 1
    c: Coincident(g33,g10)
    c: Equal(g29,g30)
    c: Coincident(g30,g19)
    c: Equal(g29,g31)
    c: Coincident(g31,g18)
    c: Equal(g29,g32)
    c: Coincident(g33,g17)
    c: InternalAlignment(g29-g32 -> g33) x4
    c: InternalAlignment(g34,g33)
    c: InternalAlignment(g35,g33)
FEATURE [PartDesign::Pad] Pad022  label="IIOuter Legs"
  BaseFeature = -> Pad021
  Direction = (1,-2e-16,3e-16)
  Length = 9.5
  Length2 = 10
  Placement = pos=(0,0,0) rot=(0.57735,0.57735,0.57735;2.0944rad)
  Profile = -> Sketch036
  ReferenceAxis = -> Sketch036 [N_Axis]
  Reversed = true
  Type = 0
FEATURE [Sketcher::SketchObject] Sketch037
  ExternalGeometry = -> [Sketch036]
  FullyConstrained = true
  MapMode = 5
  Support = -> [XY_Plane005]
  expr: Constraints[19] = <<Spreadsheet>>.NutR
  expr: Constraints[20] = <<Spreadsheet>>.NutR
  expr: Constraints[25] = <<Spreadsheet>>.ScrewD
  expr: Constraints[59] = <<Spreadsheet>>.ScrewD
  expr: Constraints[60] = <<Spreadsheet>>.NutR
  expr: Constraints[61] = <<Spreadsheet>>.NutR
  sketch-geometry (24):
    g0: LineSegment StartX=-4.4e-15 StartY=-20 StartZ=0 EndX=7.6225 EndY=-26.0949 EndZ=0
    g1: LineSegment StartX=-4.4e-15 StartY=-20 StartZ=0 EndX=-5.6e-15 EndY=-25 EndZ=0
    g2: LineSegment StartX=-5.6e-15 StartY=-25 StartZ=0 EndX=-9.5 EndY=-25 EndZ=0
    g3: LineSegment StartX=-9.5 StartY=-25 StartZ=0 EndX=-9.5 EndY=-35 EndZ=0
    g4: LineSegment StartX=-9.5 StartY=-35 StartZ=0 EndX=4.5 EndY=-35 EndZ=0
    g5: ArcOfCircle CenterX=4.5 CenterY=-30 CenterZ=0 NormalX=0 NormalY=0 NormalZ=1 AngleXU=0 Radius=5 StartAngle=4.71239 EndAngle=7.17949
    g6: LineSegment StartX=4.5 StartY=-35 StartZ=0 EndX=9.5 EndY=-35 EndZ=0
    g7: LineSegment StartX=9.5 StartY=-35 StartZ=0 EndX=9.5 EndY=-30 EndZ=0
    g8: Circle CenterX=0 CenterY=-30 CenterZ=0 NormalX=0 NormalY=0 NormalZ=1 AngleXU=0 Radius=2.1
    g9: LineSegment StartX=0 StartY=-30 StartZ=0 EndX=9.5 EndY=-30 EndZ=0
    g10: LineSegment StartX=9.5 StartY=-35 StartZ=0 EndX=0 EndY=-30 EndZ=0
    g11: LineSegment StartX=0 StartY=-30 StartZ=0 EndX=-9.5 EndY=-35 EndZ=0
    g12: LineSegment StartX=1e-14 StartY=45 StartZ=0 EndX=8.9e-15 EndY=40 EndZ=0
    g13: LineSegment StartX=-9.5 StartY=45 StartZ=0 EndX=-9.5 EndY=55 EndZ=0
    g14: LineSegment StartX=-9.5 StartY=55 StartZ=0 EndX=4.5 EndY=55 EndZ=0
    g15: ArcOfCircle CenterX=4.5 CenterY=50 CenterZ=0 NormalX=0 NormalY=0 NormalZ=1 AngleXU=0 Radius=5 StartAngle=5.38688 EndAngle=7.85398
    g16: LineSegment StartX=7.6225 StartY=46.0949 StartZ=0 EndX=8.9e-15 EndY=40 EndZ=0
    g17: LineSegment StartX=1e-14 StartY=45 StartZ=0 EndX=-9.5 EndY=45 EndZ=0
    g18: LineSegment StartX=4.5 StartY=55 StartZ=0 EndX=9.5 EndY=55 EndZ=0
    g19: LineSegment StartX=9.5 StartY=55 StartZ=0 EndX=9.5 EndY=50 EndZ=0
    g20: LineSegment StartX=9.5 StartY=55 StartZ=0 EndX=0 EndY=50 EndZ=0
    g21: LineSegment StartX=0 StartY=50 StartZ=0 EndX=-9.5 EndY=55 EndZ=0
    g22: LineSegment StartX=0 StartY=50 StartZ=0 EndX=9.5 EndY=50 EndZ=0
    g23: Circle CenterX=0 CenterY=50 CenterZ=0 NormalX=0 NormalY=0 NormalZ=1 AngleXU=0 Radius=2.1
  constraints (62):
    c: PointOnObject(g0,g-4)
    c: Coincident(g0,g1)
    c: Coincident(g1,g-4)
    c: Coincident(g1,g2)
    c: Horizontal(g2)
    c: Coincident(g2,g3)
    c: Vertical(g3)
    c: Coincident(g3,g4)
    c: Horizontal(g4)
    c: Tangent(g5,g0) = 1.5708
    c: Tangent(g5,g4) = -1.5708
    c: Coincident(g4,g6)
    c: Horizontal(g6)
    c: Coincident(g6,g7)
    c: PointOnObject(g7,g5)
    c: Vertical(g7)
    c: DistanceX(g3,g6) = 19
    c: DistanceY(g1,g1) = 5
    c: PointOnObject(g8,g-2)
    c: DistanceY(g8,g1) = 5
    c: DistanceY(g3,g8) = 5
    c: Coincident(g9,g8)
    c: Coincident(g9,g7)
    c: Horizontal(g9)
    c: PointOnObject(g5,g9)
    c: Diameter(g8) = 4.2
    c: Coincident(g6,g10)
    c: Coincident(g10,g8)
    c: Coincident(g10,g11)
    c: Coincident(g11,g3)
    c: Equal(g11,g10)
    c: Coincident(g-3,g12)
    c: PointOnObject(g12,g-3)
    c: Vertical(g13)
    c: Coincident(g13,g14)
    c: Horizontal(g14)
    c: Tangent(g14,g15) = 1.5708
    c: Tangent(g15,g16) = 1.5708
    c: Coincident(g16,g12)
    c: Coincident(g17,g12)
    c: Coincident(g17,g13)
    c: Equal(g12,g1)
    c: Coincident(g14,g18)
    c: Coincident(g18,g19)
    c: Vertical(g19)
    c: PointOnObject(g19,g15)
    c: Horizontal(g18)
    c: DistanceX(g13,g18) = 19
    c: Horizontal(g17)
    c: Coincident(g18,g20)
    c: PointOnObject(g20,g-2)
    c: Coincident(g20,g21)
    c: Coincident(g21,g13)
    c: Equal(g20,g21)
    c: Coincident(g22,g20)
    c: Coincident(g22,g19)
    c: Horizontal(g22)
    c: PointOnObject(g15,g22)
    c: Coincident(g23,g20)
    c: Diameter(g23) = 4.2
    c: DistanceY(g12,g23) = 5
    c: DistanceY(g23,g13) = 5
FEATURE [PartDesign::Pad] Pad023
  BaseFeature = -> Pad022
  Direction = (0,0,1)
  Length = 3
  Length2 = 10
  Placement = pos=(0,0,0) rot=(0.57735,0.57735,0.57735;2.0944rad)
  Profile = -> Sketch037
  ReferenceAxis = -> Sketch037 [N_Axis]
  Type = 0
FEATURE [PartDesign::Body] Body005  label="InnerIndexArch"
  Group = -> [Sketch032,Pad020,Sketch033,Pocket010,Sketch034,Pocket011,Sketch035,Pad021,Sketch036,Pad022,Sketch037,Pad023]
  Origin = -> Origin005
  Placement = pos=(110,0,5) rot=(0,0,1;0rad)
  Tip = -> Pad023
  expr: .Placement.Base.y = <<IndexArch>>.Placement.Base.y
  expr: .Placement.Base.z = <<IndexArch>>.Placement.Base.z
FEATURE [PartDesign::Body] Body006  label="StaggerGuide"
  Origin = -> Origin006
FEATURE [Sketcher::SketchObject] Sketch038
  FullyConstrained = true
  MapMode = 5
  Placement = pos=(0,0,0) rot=(1,0,0;1.5708rad)
  Support = -> [XZ_Plane007]
  expr: Constraints[33] = <<OuterArch>>.Placement.Base.z
  expr: Constraints[38] = <<RingArch>>.Placement.Base.z
  expr: Constraints[39] = <<IndexArch>>.Placement.Base.z
  expr: Constraints[53] = 20mm + <<MiddleArch>>.Placement.Base.z
  sketch-geometry (18):
    g0: LineSegment StartX=0 StartY=15 StartZ=0 EndX=40 EndY=15 EndZ=0
    g1: LineSegment StartX=40 StartY=15 StartZ=0 EndX=40 EndY=5 EndZ=0
    g2: LineSegment StartX=40 StartY=5 StartZ=0 EndX=60 EndY=5 EndZ=0
    g3: LineSegment StartX=60 StartY=5 StartZ=0 EndX=60 EndY=0 EndZ=0
    g4: LineSegment StartX=60 StartY=0 StartZ=0 EndX=80 EndY=0 EndZ=0
    g5: LineSegment StartX=80 StartY=0 StartZ=0 EndX=80 EndY=5 EndZ=0
    g6: LineSegment StartX=80 StartY=5 StartZ=0 EndX=140 EndY=5 EndZ=0
    g7: LineSegment StartX=140 StartY=5 StartZ=0 EndX=140 EndY=2 EndZ=0
    g8: LineSegment StartX=140 StartY=2 StartZ=0 EndX=83 EndY=2 EndZ=0
    g9: LineSegment StartX=83 StartY=2 StartZ=0 EndX=83 EndY=-3 EndZ=0
    g10: LineSegment StartX=83 StartY=-3 StartZ=0 EndX=57 EndY=-3 EndZ=0
    g11: LineSegment StartX=57 StartY=-3 StartZ=0 EndX=57 EndY=2 EndZ=0
    g12: LineSegment StartX=57 StartY=2 StartZ=0 EndX=37 EndY=2 EndZ=0
    g13: LineSegment StartX=37 StartY=2 StartZ=0 EndX=37 EndY=12 EndZ=0
    g14: LineSegment StartX=37 StartY=12 StartZ=0 EndX=0 EndY=12 EndZ=0
    g15: LineSegment StartX=0 StartY=12 StartZ=0 EndX=0 EndY=15 EndZ=0
    g16: LineSegment StartX=0 StartY=-20 StartZ=0 EndX=60 EndY=-20 EndZ=0
    g17: LineSegment StartX=60 StartY=0 StartZ=0 EndX=60 EndY=-20 EndZ=0
  constraints (54):
    c: PointOnObject(g0,g-2)
    c: Horizontal(g0)
    c: Coincident(g0,g1)
    c: Coincident(g1,g2)
    c: Horizontal(g2)
    c: Coincident(g2,g3)
    c: Coincident(g3,g4)
    c: Horizontal(g4)
    c: Coincident(g4,g5)
    c: Vertical(g5)
    c: Coincident(g5,g6)
    c: Horizontal(g6)
    c: Coincident(g6,g7)
    c: Vertical(g7)
    c: Coincident(g7,g8)
    c: Horizontal(g8)
    c: Coincident(g8,g9)
    c: Vertical(g9)
    c: Coincident(g9,g10)
    c: Horizontal(g10)
    c: Coincident(g10,g11)
    c: Coincident(g11,g12)
    c: Horizontal(g12)
    c: Coincident(g12,g13)
    c: Vertical(g13)
    c: Coincident(g13,g14)
    c: Horizontal(g14)
    c: Coincident(g14,g15)
    c: Coincident(g15,g0)
    c: PointOnObject(g14,g-2)
    c: Vertical(g1)
    c: Vertical(g3)
    c: Vertical(g11)
    c: DistanceY(g-1,g0) = 15
    c: DistanceX(g0,g0) = 40
    c: DistanceX(g-1,g2) = 60
    c: DistanceX(g-1,g5) = 80
    c: DistanceX(g-1,g6) = 140
    c: DistanceY(g-1,g1) = 5
    c: DistanceY(g-1,g5) = 5
    c: DistanceY(g15,g15) = 3
    c: DistanceY(g12,g1) = 3
    c: DistanceX(g12,g1) = 3
    c: DistanceX(g11,g3) = 3
    c: DistanceY(g10,g3) = 3
    c: DistanceY(g7,g7) = 3
    c: DistanceX(g4,g8) = 3
    c: PointOnObject(g16,g-2)
    c: Horizontal(g16)
    c: Coincident(g17,g3)
    c: Coincident(g17,g16)
    c: Vertical(g17)
    c: DistanceY(g16,g-1) = 20
    c: DistanceY(g17,g17) = 20
FEATURE [PartDesign::Pad] Pad024  label="Plate"
  Direction = (0,-1,-2e-16)
  Length = 80
  Length2 = 78
  Placement = pos=(0,0,0) rot=(1,0,0;1.5708rad)
  Profile = -> Sketch038
  ReferenceAxis = -> Sketch038 [N_Axis]
  Type = 4
  expr: Length = -<<OuterArch>>.Placement.Base.y + <<Spreadsheet>>.ArchLength + <<Spreadsheet>>.NutR * 3 + 10mm
  expr: Length2 = <<MiddleArch>>.Placement.Base.y + <<Spreadsheet>>.ArchLength + <<Spreadsheet>>.NutR * 3 + 13mm
FEATURE [Sketcher::SketchObject] Sketch039
  ExternalGeometry = -> [Sketch038]
  FullyConstrained = true
  MapMode = 5
  Placement = pos=(0,78,0) rot=(-1,0,0;1.5708rad)
  Support = -> [Pad024]
  expr: Constraints[20] = <<Spreadsheet>>.ScrewD
  expr: Constraints[36] = <<Spreadsheet>>.NutR + 1mm
  expr: Constraints[62] = <<Spreadsheet>>.NutR * 2
  expr: Constraints[71] = <<Spreadsheet>>.NutR
  sketch-geometry (29):
    g0: LineSegment StartX=140 StartY=-5 StartZ=0 EndX=140 EndY=20.1125 EndZ=0
    g1: LineSegment StartX=0 StartY=-12 StartZ=0 EndX=0 EndY=-15 EndZ=0
    g2: LineSegment StartX=0 StartY=-15 StartZ=0 EndX=40 EndY=-15 EndZ=0
    g3: LineSegment StartX=40 StartY=-15 StartZ=0 EndX=40 EndY=-5 EndZ=0
    g4: LineSegment StartX=40 StartY=-5 StartZ=0 EndX=60 EndY=-5 EndZ=0
    g5: LineSegment StartX=60 StartY=-5 StartZ=0 EndX=60 EndY=0 EndZ=0
    g6: LineSegment StartX=60 StartY=0 StartZ=0 EndX=80 EndY=-4e-16 EndZ=0
    g7: LineSegment StartX=80 StartY=-4e-16 StartZ=0 EndX=80 EndY=-5 EndZ=0
    g8: LineSegment StartX=80 StartY=-5 StartZ=0 EndX=140 EndY=-5 EndZ=0
    g9: Circle CenterX=131.539 CenterY=4 CenterZ=0 NormalX=0 NormalY=0 NormalZ=1 AngleXU=0 Radius=2.1
    g10: LineSegment StartX=131.539 StartY=4 StartZ=0 EndX=140 EndY=4 EndZ=0
    g11: LineSegment StartX=131.539 StartY=4 StartZ=0 EndX=129.594 EndY=9.67607 EndZ=0
    g12: LineSegment StartX=140 StartY=20.1125 StartZ=0 EndX=117.081 EndY=12.2597 EndZ=0
    g13: LineSegment StartX=112.219 StartY=26.4498 StartZ=0 EndX=0 EndY=-12 EndZ=0
    g14: LineSegment StartX=131.539 StartY=4 StartZ=0 EndX=131.539 EndY=-2 EndZ=0
    g15: LineSegment StartX=140 StartY=13.2415 StartZ=0 EndX=119.188 EndY=6.11059 EndZ=0
    g16: LineSegment StartX=119.188 StartY=6.11059 StartZ=0 EndX=117.081 EndY=12.2597 EndZ=0
    g17: LineSegment StartX=117.081 StartY=12.2597 StartZ=0 EndX=112.219 EndY=26.4498 EndZ=0
    g18: LineSegment StartX=106.543 StartY=24.505 StartZ=0 EndX=108.163 EndY=19.775 EndZ=0
    g19: LineSegment StartX=108.163 StartY=19.775 StartZ=0 EndX=111.405 EndY=10.3149 EndZ=0
    g20: LineSegment StartX=91.7781 StartY=14.1608 StartZ=0 EndX=90.1574 EndY=18.8909 EndZ=0
    g21: Circle CenterX=111.405 CenterY=10.3149 CenterZ=0 NormalX=0 NormalY=0 NormalZ=1 AngleXU=0 Radius=2.1
    g22: Circle CenterX=108.163 CenterY=19.775 CenterZ=0 NormalX=0 NormalY=0 NormalZ=1 AngleXU=0 Radius=2.1
    g23: Circle CenterX=91.7781 CenterY=14.1608 CenterZ=0 NormalX=0 NormalY=0 NormalZ=1 AngleXU=0 Radius=2.1
    g24: LineSegment StartX=111.405 StartY=10.3149 StartZ=0 EndX=117.081 EndY=12.2597 EndZ=0
    g25: LineSegment StartX=108.163 StartY=19.775 StartZ=0 EndX=101.591 EndY=12.2378 EndZ=0
    g26: LineSegment StartX=101.591 StartY=12.2378 StartZ=0 EndX=91.7781 EndY=14.1608 EndZ=0
    g27: LineSegment StartX=101.591 StartY=12.2378 StartZ=0 EndX=111.405 EndY=10.3149 EndZ=0
    g28: Circle CenterX=101.591 CenterY=12.2378 CenterZ=0 NormalX=0 NormalY=0 NormalZ=1 AngleXU=0 Radius=2.1
  constraints (72):
    c: Coincident(g-9,g0)
    c: Vertical(g0)
    c: Coincident(g0,g12)
    c: Coincident(g13,g-4)
    c: Coincident(g13,g1)
    c: Coincident(g1,g-3)
    c: Coincident(g1,g2)
    c: Coincident(g2,g-3)
    c: Coincident(g2,g3)
    c: Coincident(g3,g-6)
    c: Coincident(g3,g4)
    c: Coincident(g4,g-6)
    c: Coincident(g4,g5)
    c: Coincident(g5,g-8)
    c: Coincident(g5,g6)
    c: Coincident(g6,g-8)
    c: Coincident(g6,g7)
    c: Coincident(g7,g-9)
    c: Coincident(g7,g8)
    c: Coincident(g8,g0)
    c: Diameter(g9) = 4.2
    c: Coincident(g10,g9)
    c: PointOnObject(g10,g0)
    c: Horizontal(g10)
    c: Coincident(g11,g9)
    c: Coincident(g17,g13)
    c: Coincident(g14,g9)
    c: PointOnObject(g14,g-10)
    c: Vertical(g14)
    c: PointOnObject(g15,g0)
    c: Coincident(g16,g15)
    c: Coincident(g16,g17)
    c: Distance(g16,g17) = 21.5
    c: Coincident(g16,g12)
    c: Distance(g16) = 6.5
    c: PointOnObject(g11,g15)
    c: DistanceY(g14,g14) = 6
    c: Equal(g14,g11)
    c: Distance(g15) = 22
    c: Symmetric(g15,g15,g11)
    c: Angle(g17,g16) = 3.14159
    c: Parallel(g12,g13)
    c: Perpendicular(g15,g16)
    c: Perpendicular(g17,g12)
    c: PointOnObject(g18,g13)
    c: Coincident(g18,g19)
    c: PointOnObject(g20,g13)
    c: PointOnObject(g24,g19)
    c: Angle(g19,g18) = 3.14159
    c: Perpendicular(g13,g20)
    c: Perpendicular(g18,g13)
    c: Coincident(g21,g19)
    c: Coincident(g22,g18)
    c: Equal(g23,g22)
    c: Equal(g21,g9)
    c: Equal(g22,g9)
    c: Tangent(g24,g12) = 1.5708
    c: Equal(g24,g14)
    c: Coincident(g25,g22)
    c: Coincident(g26,g23)
    c: Coincident(g27,g25)
    c: Coincident(g27,g21)
    c: Distance(g27) = 10
    c: Coincident(g25,g26)
    c: Equal(g25,g26)
    c: Coincident(g28,g25)
    c: Coincident(g23,g20)
    c: Equal(g26,g27)
    c: Equal(g19,g27)
    c: Equal(g28,g21)
    c: Equal(g20,g18)
    c: Distance(g18) = 5
FEATURE [PartDesign::Pad] Pad025
  BaseFeature = -> Pad024
  Direction = (0,1,2e-16)
  Length = 3
  Length2 = 10
  Placement = pos=(0,0,0) rot=(1,0,0;1.5708rad)
  Profile = -> Sketch039
  ReferenceAxis = -> Sketch039 [N_Axis]
  Reversed = true
  Type = 0
FEATURE [Part::Feature] Part__Feature  label="RJ11-6"
  Placement = pos=(139.693,87,-28.3294) rot=(0,1,0;1.8326rad)
  shape: bbox 20.86 x 16.38 x 17.5 mm, 161 faces, 0 solids (baked)
FEATURE [Part::Feature] Part__Feature001  label="PICO_REF_BOARD.STEP"
  shape: bbox 21 x 1 x 51 mm, 450 faces (baked)
FEATURE [Part::Feature] Part__Feature002  label="PICO_REF_USB.STEP"
  Placement = pos=(10.5,1.76,-49.2) rot=(0,1,0;3.14159rad)
  shape: bbox 8 x 2.94 x 5.6 mm, 67 faces, 5 solids (baked)
FEATURE [Part::Feature] Part__Feature003  label="PICO_REF_SWITCH.STEP"
  Placement = pos=(7,0.5,-39) rot=(0,1,0;1.5708rad)
  shape: bbox 3.2 x 2.5 x 4.25 mm, 15 faces (baked)
FEATURE [Part::Feature] Part__Feature004  label="PICO_REF_MICROCONTROLLER.STEP"
  Placement = pos=(10.5,0.95,-25) rot=(0,0,1;0rad)
  shape: bbox 7 x 0.9 x 7 mm, 6 faces (baked)
FEATURE [Part::Feature] Part__Feature005  label="PICO_REF_LED.STEP"
  Placement = pos=(4.8,0.5,-46.2) rot=(0,0,1;0rad)
  shape: bbox 1.6 x 0.6 x 0.8 mm, 10 faces (baked)
FEATURE [Part::Feature] Part__Feature006  label="PICO_REF_ONSEMI.STEP"
  Placement = pos=(16.5,0.5,-44.4) rot=(0,1,0;1.5708rad)
  shape: bbox 1.65 x 0.95 x 3.6 mm, 14 faces (baked)
FEATURE [Part::Feature] Part__Feature007  label="PICO_BOURNS.STEP"
  Placement = pos=(16.5,0.5,-40.1) rot=(0,-1,0;1.5708rad)
  shape: bbox 2 x 1.2 x 2.5 mm, 6 faces (baked)
FEATURE [Part::Feature] Part__Feature008  label="PICO_MURATA.STEP"
  Placement = pos=(13.4,1.125,-42.6) rot=(0,0,1;0rad)
  shape: bbox 2 x 1.25 x 1.25 mm, 6 faces (baked)
FEATURE [Part::Feature] Part__Feature009  label="PICO_MURATA.STEP001"
  Placement = pos=(13.4,1.125,-37.6) rot=(0,0,1;0rad)
  shape: bbox 2 x 1.25 x 1.25 mm, 6 faces (baked)
FEATURE [Part::Feature] Part__Feature010  label="PICO_RICHTEK.STEP"
  Placement = pos=(13.4,0.5,-40.1) rot=(0,0,1;0rad)
  shape: bbox 2.5 x 0.75 x 2.5 mm, 6 faces (baked)
FEATURE [Part::Feature] Part__Feature011  label="PICO_DIODES.STEP"
  Placement = pos=(16.9,0.5,-32.7) rot=(0,0,1;0rad)
  shape: bbox 1.6 x 0.8 x 0.8 mm, 6 faces (baked)
FEATURE [Part::Feature] Part__Feature012  label="PICO_AEL.STEP"
  Placement = pos=(8.2,0.5,-16.45) rot=(0,0,1;0rad)
  shape: bbox 3.2 x 0.6 x 2.5 mm, 6 faces (baked)
FEATURE [Part::Feature] Part__Feature013  label="PICO_WINBOND.STEP"
  Placement = pos=(6.7,0.8,-31.9) rot=(0,0,1;0rad)
  shape: bbox 2 x 0.6 x 3 mm, 6 faces (baked)
FEATURE [App::Part] PICO_assm_140121_STEP  label="PICO_assm_140121.STEP"
  Group = -> [Part__Feature001,Part__Feature002,Part__Feature003,Part__Feature004,Part__Feature005,Part__Feature006,Part__Feature007,Part__Feature008,Part__Feature009,Part__Feature010,Part__Feature011,Part__Feature012,Part__Feature013]
  Origin = -> Origin008
FEATURE [App::Part] PICO
  Group = -> [PICO_assm_140121_STEP]
  Origin = -> Origin009
  Placement = pos=(128,-3.82e-14,35) rot=(-0.57735,-0.57735,0.57735;4.18879rad)
FEATURE [Sketcher::SketchObject] Sketch040
  FullyConstrained = true
  MapMode = 5
  Support = -> [XY_Plane010]
  expr: Constraints[34] = <<Spreadsheet>>.NutR
  expr: Constraints[35] = <<Spreadsheet>>.NutR
  expr: Constraints[41] = <<Spreadsheet>>.NutR
  expr: Constraints[71] = <<Spreadsheet>>.ScrewD
  expr: Constraints[74] = <<Spreadsheet>>.NutR
  sketch-geometry (29):
    g0: LineSegment StartX=-29.5 StartY=10 StartZ=0 EndX=29.5 EndY=10 EndZ=0
    g1: LineSegment StartX=29.5 StartY=10 StartZ=0 EndX=29.5 EndY=0 EndZ=0
    g2: LineSegment StartX=29.5 StartY=0 StartZ=0 EndX=-29.5 EndY=0 EndZ=0
    g3: LineSegment StartX=-29.5 StartY=0 StartZ=0 EndX=-29.5 EndY=10 EndZ=0
    g4: LineSegment StartX=-26.6 StartY=5 StartZ=0 EndX=-26.6 EndY=7.1 EndZ=0
    g5: LineSegment StartX=-26.6 StartY=7.1 StartZ=0 EndX=-10.8667 EndY=7.1 EndZ=0
    g6: LineSegment StartX=-10.8667 StartY=7.1 StartZ=0 EndX=-10.8667 EndY=5 EndZ=0
    g7: LineSegment StartX=-12.9667 StartY=2.9 StartZ=0 EndX=-24.5 EndY=2.9 EndZ=0
    g8: GeomPoint X=-24.5 Y=5 Z=0
    g9: LineSegment StartX=-7.86667 StartY=5 StartZ=0 EndX=-7.86667 EndY=7.1 EndZ=0
    g10: LineSegment StartX=-7.86667 StartY=7.1 StartZ=0 EndX=7.86667 EndY=7.1 EndZ=0
    g11: LineSegment StartX=7.86667 StartY=7.1 StartZ=0 EndX=7.86667 EndY=5 EndZ=0
    g12: LineSegment StartX=5.76667 StartY=2.9 StartZ=0 EndX=-5.76667 EndY=2.9 EndZ=0
    g13: GeomPoint X=0 Y=5 Z=0
    g14: LineSegment StartX=10.8667 StartY=5 StartZ=0 EndX=10.8667 EndY=7.1 EndZ=0
    g15: LineSegment StartX=10.8667 StartY=7.1 StartZ=0 EndX=26.6 EndY=7.1 EndZ=0
    g16: LineSegment StartX=26.6 StartY=7.1 StartZ=0 EndX=26.6 EndY=5 EndZ=0
    g17: LineSegment StartX=24.5 StartY=2.9 StartZ=0 EndX=12.9667 EndY=2.9 EndZ=0
    g18: GeomPoint X=24.5 Y=5 Z=0
    g19: LineSegment StartX=-24.5 StartY=5 StartZ=0 EndX=0 EndY=5 EndZ=0
    g20: LineSegment StartX=0 StartY=5 StartZ=0 EndX=24.5 EndY=5 EndZ=0
    g21: LineSegment StartX=24.5 StartY=2.9 StartZ=0 EndX=26.6 EndY=2.9 EndZ=0
    g22: LineSegment StartX=26.6 StartY=2.9 StartZ=0 EndX=26.6 EndY=5 EndZ=0
    g23: ArcOfCircle CenterX=24.5 CenterY=5 CenterZ=0 NormalX=0 NormalY=0 NormalZ=1 AngleXU=0 Radius=2.1 StartAngle=4.71239 EndAngle=6.28319
    g24: ArcOfCircle CenterX=12.9667 CenterY=5 CenterZ=0 NormalX=0 NormalY=0 NormalZ=1 AngleXU=0 Radius=2.1 StartAngle=3.14159 EndAngle=4.71239
    g25: ArcOfCircle CenterX=5.76667 CenterY=5 CenterZ=0 NormalX=0 NormalY=0 NormalZ=1 AngleXU=0 Radius=2.1 StartAngle=4.71239 EndAngle=6.28319
    g26: ArcOfCircle CenterX=-5.76667 CenterY=5 CenterZ=0 NormalX=0 NormalY=0 NormalZ=1 AngleXU=0 Radius=2.1 StartAngle=3.14159 EndAngle=4.71239
    g27: ArcOfCircle CenterX=-12.9667 CenterY=5 CenterZ=0 NormalX=0 NormalY=0 NormalZ=1 AngleXU=0 Radius=2.1 StartAngle=4.71239 EndAngle=6.28319
    g28: ArcOfCircle CenterX=-24.5 CenterY=5 CenterZ=0 NormalX=0 NormalY=0 NormalZ=1 AngleXU=0 Radius=2.1 StartAngle=3.14159 EndAngle=4.71239
  constraints (76):
    c: Coincident(g0,g1)
    c: Coincident(g1,g2)
    c: Coincident(g2,g3)
    c: Coincident(g3,g0)
    c: Horizontal(g2)
    c: Vertical(g1)
    c: Vertical(g3)
    c: Coincident(g4,g5)
    c: Coincident(g5,g6)
    c: Horizontal(g5)
    c: Horizontal(g7)
    c: Vertical(g4)
    c: Vertical(g6)
    c: Coincident(g9,g10)
    c: Coincident(g10,g11)
    c: Horizontal(g10)
    c: Horizontal(g12)
    c: Vertical(g9)
    c: Vertical(g11)
    c: PointOnObject(g13,g-2)
    c: Coincident(g14,g15)
    c: Coincident(g15,g16)
    c: Horizontal(g15)
    c: Horizontal(g17)
    c: Vertical(g14)
    c: Vertical(g16)
    c: Coincident(g19,g8)
    c: Coincident(g19,g13)
    c: Horizontal(g19)
    c: Coincident(g20,g13)
    c: Coincident(g20,g18)
    c: Horizontal(g20)
    c: Equal(g14,g11)
    c: Equal(g9,g6)
    c: DistanceY(g8,g0) = 5
    c: DistanceY(g2,g8) = 5
    c: DistanceX(g6,g9) = 3
    c: DistanceX(g11,g14) = 3
    c: DistanceX(g2,g2) = 59
    c: Equal(g5,g10)
    c: Equal(g15,g10)
    c: DistanceX(g23,g1) = 5
    c: Symmetric(g0,g0,g-2)
    c: PointOnObject(g-1,g2)
    c: PointOnObject(g14,g20)
    c: PointOnObject(g11,g20)
    c: PointOnObject(g6,g19)
    c: PointOnObject(g9,g19)
    c: PointOnObject(g4,g19)
    c: Coincident(g17,g21)
    c: Coincident(g21,g22)
    c: Coincident(g22,g16)
    c: Vertical(g22)
    c: Tangent(g23,g17) = 1.5708
    c: Tangent(g23,g16) = 1.5708
    c: PointOnObject(g25,g20)
    c: Coincident(g25,g11)
    c: PointOnObject(g26,g19)
    c: Coincident(g26,g9)
    c: PointOnObject(g27,g19)
    c: Coincident(g27,g6)
    c: Coincident(g28,g8)
    c: Coincident(g28,g4)
    c: Tangent(g28,g7) = 1.5708
    c: Tangent(g27,g7) = 1.5708
    c: Tangent(g26,g12) = 1.5708
    c: Tangent(g25,g12) = 1.5708
    c: Tangent(g24,g17) = 1.5708
    c: Tangent(g24,g14) = 1.5708
    c: Coincident(g18,g23)
    c: Equal(g7,g12)
    c: DistanceY(g21,g15) = 4.2
    c: Horizontal(g21)
    c: Equal(g22,g16)
    c: DistanceX(g2,g28) = 5
    c: Horizontal(g17,g12)
FEATURE [PartDesign::Pad] Pad026
  Direction = (0,0,1)
  Length = 3
  Length2 = 10
  Profile = -> Sketch040
  ReferenceAxis = -> Sketch040 [N_Axis]
  Type = 0
FEATURE [PartDesign::Line] DatumLine
  AttacherType = Attacher::AttachEngineLine
  AttachmentOffset = pos=(21,0,0) rot=(0,-1,0;0.10472rad)
  Length = 20
  MapMode = 16
  Placement = pos=(4.7e-15,-4.7e-15,21) rot=(0.743145,0,0.669131;3.14159rad)
  ResizeMode = 0
  Support = -> [XZ_Plane010]
FEATURE [Sketcher::SketchObject] Sketch041
  ExternalGeometry = -> [Sketch040,DatumLine]
  FullyConstrained = true
  MapMode = 5
  Placement = pos=(0,0,0) rot=(1,0,0;1.5708rad)
  Support = -> [XZ_Plane010]
  sketch-geometry (30):
    g0: LineSegment StartX=29.5 StartY=0 StartZ=0 EndX=29.5 EndY=3 EndZ=0
    g1: LineSegment StartX=29.5 StartY=3 StartZ=0 EndX=17.9014 EndY=3 EndZ=0
    g2: LineSegment StartX=-29.5 StartY=0 StartZ=0 EndX=-29.5 EndY=3 EndZ=0
    g3: LineSegment StartX=-29.5 StartY=3 StartZ=0 EndX=-17.9014 EndY=3 EndZ=0
    g4: ArcOfCircle CenterX=-56.761 CenterY=19.4384 CenterZ=0 NormalX=0 NormalY=0 NormalZ=1 AngleXU=0 Radius=42.1934 StartAngle=5.88299 EndAngle=6.17847
    g5: ArcOfCircle CenterX=-14.7725 CenterY=15.0252 CenterZ=0 NormalX=0 NormalY=0 NormalZ=1 AngleXU=0 Radius=23.9737 StartAngle=5.75774 EndAngle=6.17847
    g6: ArcOfCircle CenterX=4.78187 CenterY=12.9699 CenterZ=0 NormalX=0 NormalY=0 NormalZ=1 AngleXU=0 Radius=14.6609 StartAngle=3.03687 EndAngle=3.88941
    g7: ArcOfCircle CenterX=5.60272 CenterY=12.8837 CenterZ=0 NormalX=0 NormalY=0 NormalZ=1 AngleXU=0 Radius=3.48623 StartAngle=6.17847 EndAngle=7.74926
    g8: ArcOfCircle CenterX=-6.33154 CenterY=14.138 CenterZ=0 NormalX=0 NormalY=0 NormalZ=1 AngleXU=0 Radius=3.48623 StartAngle=1.46608 EndAngle=3.03687
    g9: ArcOfCircle CenterX=-18.2658 CenterY=15.3923 CenterZ=0 NormalX=0 NormalY=0 NormalZ=1 AngleXU=0 Radius=3.48623 StartAngle=6.17847 EndAngle=7.74926
    g10: ArcOfCircle CenterX=17.537 CenterY=11.6293 CenterZ=0 NormalX=0 NormalY=0 NormalZ=1 AngleXU=0 Radius=3.48623 StartAngle=1.46608 EndAngle=3.03687
    g11: LineSegment StartX=30.2538 StartY=17.8202 StartZ=0 EndX=-29.4175 EndY=24.0919 EndZ=0
    g12: LineSegment StartX=-29.4175 StartY=24.0919 StartZ=0 EndX=-29.8357 EndY=20.1138 EndZ=0
    g13: LineSegment StartX=-29.8357 StartY=20.1138 StartZ=0 EndX=-17.9014 EndY=18.8595 EndZ=0
    g14: LineSegment StartX=-5.96713 StartY=17.6051 StartZ=0 EndX=5.96713 EndY=16.3508 EndZ=0
    g15: LineSegment StartX=-5.96713 StartY=3 StartZ=0 EndX=5.96713 EndY=3 EndZ=0
    g16: LineSegment StartX=-17.9014 StartY=3 StartZ=0 EndX=-5.96713 EndY=3 EndZ=0
    g17: LineSegment StartX=5.96713 StartY=3 StartZ=0 EndX=17.9014 EndY=3 EndZ=0
    g18: LineSegment StartX=17.9014 StartY=15.0965 StartZ=0 EndX=5.96713 EndY=16.3508 EndZ=0
    g19: LineSegment StartX=-5.96713 StartY=17.6051 StartZ=0 EndX=-17.9014 EndY=18.8595 EndZ=0
    g20: LineSegment StartX=17.9014 StartY=3 StartZ=0 EndX=17.9014 EndY=15.0965 EndZ=0
    g21: LineSegment StartX=5.96713 StartY=3 StartZ=0 EndX=5.96713 EndY=16.3508 EndZ=0
    g22: LineSegment StartX=-5.96713 StartY=17.6051 StartZ=0 EndX=-5.96713 EndY=3 EndZ=0
    g23: LineSegment StartX=-17.9014 StartY=3 StartZ=0 EndX=-17.9014 EndY=18.8595 EndZ=0
    g24: LineSegment StartX=29.5 StartY=0 StartZ=0 EndX=-29.5 EndY=0 EndZ=0
    g25: LineSegment StartX=17.9014 StartY=15.0965 StartZ=0 EndX=29.8357 EndY=13.8421 EndZ=0
    g26: LineSegment StartX=-14.7987 StartY=15.0279 StartZ=0 EndX=14.0699 EndY=11.9937 EndZ=0
    g27: ArcOfCircle CenterX=24.0732 CenterY=10.9423 CenterZ=0 NormalX=0 NormalY=0 NormalZ=1 AngleXU=0 Radius=10.0584 StartAngle=3.03687 EndAngle=4.05179
    g28: LineSegment StartX=29.8357 StartY=13.8421 StartZ=0 EndX=30.2538 EndY=17.8202 EndZ=0
    g29: LineSegment StartX=29.8357 StartY=13.8421 StartZ=0 EndX=28.3808 EndY=0 EndZ=0
  constraints (78):
    c: Coincident(g-3,g0)
    c: Coincident(g0,g1)
    c: Horizontal(g1)
    c: Coincident(g-3,g2)
    c: Vertical(g2)
    c: Coincident(g2,g3)
    c: Horizontal(g3)
    c: Coincident(g11,g12)
    c: Coincident(g12,g13)
    c: Tangent(g14,g8) = 1.5708
    c: Tangent(g8,g6) = -1.5708
    c: Coincident(g15,g6)
    c: Coincident(g15,g5)
    c: Coincident(g16,g6)
    c: Coincident(g17,g5)
    c: Coincident(g17,g1)
    c: Coincident(g18,g7)
    c: Coincident(g19,g13)
    c: Tangent(g9,g13) = 1.5708
    c: Coincident(g10,g26) = -1.5708
    c: Tangent(g7,g5) = -1.5708
    c: Horizontal(g15)
    c: Horizontal(g16)
    c: Horizontal(g17)
    c: Equal(g17,g16)
    c: Equal(g19,g18)
    c: Tangent(g9,g4) = -1.5708
    c: Coincident(g20,g1)
    c: Coincident(g20,g10)
    c: Coincident(g21,g5)
    c: Coincident(g22,g8)
    c: Coincident(g22,g6)
    c: Coincident(g23,g3)
    c: Coincident(g23,g9)
    c: Tangent(g8,g19) = -1.5708
    c: Coincident(g7,g21)
    c: Coincident(g3,g4)
    c: Coincident(g3,g16)
    c: Tangent(g14,g7) = 1.5708
    c: Tangent(g18,g10) = -1.5708
    c: DistanceY(g2,g2) = 3
    c: Equal(g13,g14)
    c: Vertical(g0)
    c: Coincident(g24,g0)
    c: Coincident(g24,g2)
    c: Coincident(g25,g10)
    c: Parallel(g18,g25)
    c: Parallel(g14,g18)
    c: Parallel(g13,g19)
    c: Perpendicular(g11,g12)
    c: Distance(g12) = 4
    c: Vertical(g21)
    c: Vertical(g22)
    c: Vertical(g23)
    c: Equal(g14,g25)
    c: Coincident(g26,g4)
    c: PointOnObject(g6,g26)
    c: PointOnObject(g5,g26)
    c: PointOnObject(g7,g26)
    c: PointOnObject(g8,g26)
    c: Equal(g1,g3)
    c: Distance(g11) = 60
    c: Parallel(g26,g14)
    c: Equal(g25,g18)
    c: PointOnObject(g10,g26)
    c: PointOnObject(g11,g-4)
    c: PointOnObject(g11,g-4)
    c: Coincident(g27,g1)
    c: Tangent(g27,g10) = -1.5708
    c: PointOnObject(g9,g26)
    c: DistanceX(g5,g10) = 5
    c: Coincident(g28,g25)
    c: Coincident(g28,g11)
    c: Coincident(g29,g25)
    c: PointOnObject(g29,g-1)
    c: Angle(g29,g28) = 3.14159
    c: Perpendicular(g28,g25)
    c: Equal(g28,g12)
FEATURE [PartDesign::Pad] Pad027
  BaseFeature = -> Pad026
  Direction = (0,-1,-2e-16)
  Length = 4
  Length2 = 10
  Profile = -> Sketch041
  ReferenceAxis = -> Sketch041 [N_Axis]
  Type = 0
FEATURE [PartDesign::Plane] DatumPlane
  Length = 66.6324
  MapMode = 2
  Placement = pos=(4e-15,-4.7e-15,21) rot=(0.743145,0,0.669131;3.14159rad)
  ResizeMode = 0
  Support = -> [DatumLine]
  Width = 60.5873
FEATURE [Sketcher::SketchObject] Sketch042
  FullyConstrained = true
  MapMode = 5
  Placement = pos=(4.4e-15,-4.7e-15,21) rot=(0.743145,0,0.669131;3.14159rad)
  Support = -> [DatumPlane]
  sketch-geometry (7):
    g0: LineSegment StartX=-3.53373 StartY=-20.3907 StartZ=0 EndX=-7.47296 EndY=-19.6962 EndZ=0
    g1: LineSegment StartX=-7.47296 StartY=-19.6962 StartZ=0 EndX=-4 EndY=0 EndZ=0
    g2: ArcOfCircle CenterX=-4 CenterY=0 CenterZ=0 NormalX=0 NormalY=0 NormalZ=1 AngleXU=0 Radius=4 StartAngle=6.10865 EndAngle=6.95832
    g3: LineSegment StartX=-0.877501 StartY=2.5 StartZ=0 EndX=-4 EndY=0 EndZ=0
    g4: LineSegment StartX=-0.060769 StartY=-0.694593 StartZ=0 EndX=-1.79725 EndY=-10.5427 EndZ=0
    g5: LineSegment StartX=-1.79725 StartY=-10.5427 StartZ=0 EndX=-3.53373 EndY=-20.3907 EndZ=0
    g6: LineSegment StartX=-4 StartY=0 StartZ=0 EndX=-0.060769 EndY=-0.694593 EndZ=0
  constraints (20):
    c: Coincident(g5,g0)
    c: Coincident(g0,g1)
    c: Distance(g0) = 4
    c: Distance(g1) = 20
    c: Perpendicular(g1,g0)
    c: PointOnObject(g1,g-1)
    c: DistanceX(g1,g-1) = 4
    c: Coincident(g2,g1)
    c: Coincident(g2,g4)
    c: Coincident(g3,g2)
    c: Coincident(g3,g1)
    c: DistanceY(g-1,g2) = 2.5
    c: Coincident(g4,g5)
    c: Perpendicular(g4,g0)
    c: Perpendicular(g5,g0)
    c: Equal(g4,g5)
    c: Coincident(g6,g1)
    c: Coincident(g6,g2)
    c: Perpendicular(g1,g6)
    c: Angle(g4,g-1) = 1.74533
FEATURE [PartDesign::Pad] Pad028
  BaseFeature = -> Pad027
  Direction = (0.994522,0,-0.104528)
  Length = 59
  Length2 = 10
  Midplane = true
  Profile = -> Sketch042
  ReferenceAxis = -> Sketch042 [N_Axis]
  Type = 3
  UpToFace = -> Pad027 [Face35]
FEATURE [PartDesign::Pad] Pad029
  BaseFeature = -> Pad028
  Direction = (0.994522,0,-0.104528)
  Length = 10
  Length2 = 10
  Profile = -> Sketch042
  ReferenceAxis = -> Sketch042 [N_Axis]
  Type = 3
  UpToFace = -> Pad028 [Face41]
FEATURE [Sketcher::SketchObject] Sketch043
  FullyConstrained = true
  MapMode = 5
  Placement = pos=(0,0,0) rot=(1,0,0;1.5708rad)
  Support = -> [XZ_Plane011]
  expr: Constraints[26] = <<Spreadsheet>>.NutR
  expr: Constraints[3] = <<Spreadsheet>>.ScrewD
  expr: Constraints[7] = <<Spreadsheet>>.NutR
  sketch-geometry (13):
    g0: LineSegment StartX=-10.25 StartY=-7.5 StartZ=0 EndX=10.25 EndY=-7.5 EndZ=0
    g1: LineSegment StartX=10.25 StartY=-7.5 StartZ=0 EndX=10.25 EndY=3.83222e-11 EndZ=0
    g2: LineSegment StartX=-10.25 StartY=3.83222e-11 StartZ=0 EndX=-10.25 EndY=-7.5 EndZ=0
    g3: Circle CenterX=0 CenterY=5 CenterZ=0 NormalX=0 NormalY=0 NormalZ=1 AngleXU=0 Radius=2.1
    g4: LineSegment StartX=-10.25 StartY=3.83222e-11 StartZ=0 EndX=10.25 EndY=3.83222e-11 EndZ=0
    g5: Circle CenterX=-7.345 CenterY=-3.75 CenterZ=0 NormalX=0 NormalY=0 NormalZ=1 AngleXU=0 Radius=1.625
    g6: Circle CenterX=7.345 CenterY=-3.75 CenterZ=0 NormalX=0 NormalY=0 NormalZ=1 AngleXU=0 Radius=1.625
    g7: LineSegment StartX=0 StartY=10 StartZ=0 EndX=0 EndY=-7.5 EndZ=0
    g8: LineSegment StartX=-7.345 StartY=-3.75 StartZ=0 EndX=0 EndY=-3.75 EndZ=0
    g9: LineSegment StartX=0 StartY=-3.75 StartZ=0 EndX=7.345 EndY=-3.75 EndZ=0
    g10: ArcOfCircle CenterX=0 CenterY=5 CenterZ=0 NormalX=0 NormalY=0 NormalZ=1 AngleXU=0 Radius=5 StartAngle=0.0246921 EndAngle=3.1169
    g11: ArcOfCircle CenterX=10.25 CenterY=5.25315 CenterZ=0 NormalX=0 NormalY=0 NormalZ=1 AngleXU=0 Radius=5.25315 StartAngle=3.16628 EndAngle=4.71239
    g12: ArcOfCircle CenterX=-10.25 CenterY=5.25315 CenterZ=0 NormalX=0 NormalY=0 NormalZ=1 AngleXU=0 Radius=5.25315 StartAngle=4.71239 EndAngle=6.25849
  constraints (37):
    c: Coincident(g0,g1)
    c: Horizontal(g0)
    c: Vertical(g1)
    c: Diameter(g3) = 4.2
    c: PointOnObject(g4,g2)
    c: Horizontal(g4)
    c: DistanceY(g0,g4) = 7.5
    c: DistanceY(g4,g3) = 5
    c: DistanceX(g0,g0) = 20.5
    c: DistanceX(g5,g6) = 14.69
    c: Diameter(g6) = 3.25
    c: PointOnObject(g7,g0)
    c: Vertical(g7)
    c: Symmetric(g2,g1,g7)
    c: PointOnObject(g3,g7)
    c: Coincident(g8,g5)
    c: PointOnObject(g8,g7)
    c: Horizontal(g8)
    c: Coincident(g8,g9)
    c: Coincident(g9,g6)
    c: Horizontal(g9)
    c: Equal(g9,g8)
    c: Equal(g5,g6)
    c: Symmetric(g4,g0,g8)
    c: Coincident(g10,g3)
    c: PointOnObject(g7,g10)
    c: Radius(g10) = 5
    c: Coincident(g11,g1)
    c: Tangent(g11,g10) = 1.5708
    c: Coincident(g1,g4)
    c: Coincident(g12,g2)
    c: Tangent(g12,g10) = 1.5708
    c: Equal(g12,g11)
    c: Tangent(g11,g4)
    c: Coincident(g2,g0)
    c: PointOnObject(g-1,g7)
    c: PointOnObject(g-1,g4)
FEATURE [PartDesign::Pad] Pad030
  Direction = (0,-1,-2e-16)
  Length = 3
  Length2 = 10
  Placement = pos=(0,0,0) rot=(1,0,0;1.5708rad)
  Profile = -> Sketch043
  ReferenceAxis = -> Sketch043 [N_Axis]
  Reversed = true
  Type = 0
FEATURE [Sketcher::SketchObject] Sketch044
  FullyConstrained = true
  MapMode = 5
  Placement = pos=(0,0,0) rot=(1,0,0;1.5708rad)
  Support = -> [XZ_Plane011]
  expr: Constraints[11] = <<Spreadsheet>>.ScrewD
  expr: Constraints[12] = <<Spreadsheet>>.NutR * 2
  sketch-geometry (6):
    g0: Circle CenterX=7.345 CenterY=-3.75 CenterZ=0 NormalX=0 NormalY=0 NormalZ=1 AngleXU=0 Radius=1.5
    g1: Circle CenterX=-7.345 CenterY=-3.75 CenterZ=0 NormalX=0 NormalY=0 NormalZ=1 AngleXU=0 Radius=1.5
    g2: LineSegment StartX=-7.345 StartY=-3.75 StartZ=0 EndX=7.345 EndY=-3.75 EndZ=0
    g3: LineSegment StartX=0 StartY=0 StartZ=0 EndX=0 EndY=-7.5 EndZ=0
    g4: Circle CenterX=0 CenterY=5 CenterZ=0 NormalX=0 NormalY=0 NormalZ=1 AngleXU=0 Radius=5
    g5: Circle CenterX=0 CenterY=5 CenterZ=0 NormalX=0 NormalY=0 NormalZ=1 AngleXU=0 Radius=2.1
  constraints (14):
    c: Coincident(g2,g1)
    c: Coincident(g2,g0)
    c: Equal(g0,g1)
    c: DistanceX(g2,g2) = 14.69
    c: Diameter(g0) = 3
    c: Symmetric(g1,g0,g-2)
    c: Coincident(g3,g-1)
    c: DistanceY(g3,g3) = 7.5
    c: Symmetric(g3,g3,g2)
    c: PointOnObject(g4,g-2)
    c: Coincident(g5,g4)
    c: Diameter(g5) = 4.2
    c: Diameter(g4) = 10
    c: PointOnObject(g3,g4)
FEATURE [PartDesign::Pad] Pad031
  BaseFeature = -> Pad030
  Direction = (0,-1,-2e-16)
  Length = 1.57
  Length2 = 10
  Placement = pos=(0,0,0) rot=(1,0,0;1.5708rad)
  Profile = -> Sketch044
  ReferenceAxis = -> Sketch044 [N_Axis]
  Type = 0
FEATURE [PartDesign::Body] Body009  label="RJ11Holder"
  Group = -> [Sketch043,Pad030,Sketch044,Pad031]
  Origin = -> Origin011
  Placement = pos=(130.775,69,-8.70711) rot=(0.130526,0,0.991445;3.14159rad)
  Tip = -> Pad031
FEATURE [PartDesign::Plane] DatumPlane001
  AttachmentOffset = pos=(0,0,-20) rot=(0,0,1;0rad)
  Length = 66.6324
  MapMode = 5
  Placement = pos=(-19.8904,-5.1e-15,23.0906) rot=(0.743145,0,0.669131;3.14159rad)
  ResizeMode = 0
  Support = -> [DatumPlane]
  Width = 60.5873
FEATURE [PartDesign::Plane] DatumPlane002
  AttachmentOffset = pos=(0,0,20) rot=(0,0,1;0rad)
  Length = 66.6324
  MapMode = 5
  Placement = pos=(19.8904,-4.2e-15,18.9094) rot=(0.743145,0,0.669131;3.14159rad)
  ResizeMode = 0
  Support = -> [DatumPlane]
  Width = 60.5873
FEATURE [Sketcher::SketchObject] Sketch045
  ExternalGeometry = -> [Sketch042]
  FullyConstrained = true
  MapMode = 5
  Placement = pos=(-19.8904,-5.1e-15,23.0906) rot=(0.743145,0,0.669131;3.14159rad)
  Support = -> [DatumPlane001]
  sketch-geometry (15):
    g0: LineSegment StartX=-1.79725 StartY=-10.5427 StartZ=0 EndX=-3.01279 EndY=-17.4363 EndZ=0
    g1: LineSegment StartX=-3.01279 StartY=-17.4363 StartZ=0 EndX=-4.39152 EndY=-17.1932 EndZ=0
    g2: LineSegment StartX=-4.39152 StartY=-17.1932 StartZ=0 EndX=-4.61726 EndY=-18.4735 EndZ=0
    g3: LineSegment StartX=-4.61726 StartY=-18.4735 StartZ=0 EndX=-7.17776 EndY=-18.022 EndZ=0
    g4: LineSegment StartX=-0.581714 StartY=-3.64902 StartZ=0 EndX=-1.79725 EndY=-10.5427 EndZ=0
    g5: LineSegment StartX=-4.39152 StartY=-17.1932 StartZ=0 EndX=-6.95202 EndY=-16.7417 EndZ=0
    g6: LineSegment StartX=-4.61726 StartY=-18.4735 StartZ=0 EndX=-3.23853 EndY=-18.7166 EndZ=0
    g7: LineSegment StartX=-4.2952 StartY=-1.67417 StartZ=0 EndX=-1.7347 EndY=-2.12566 EndZ=0
    g8: LineSegment StartX=-1.7347 StartY=-2.12566 StartZ=0 EndX=-1.96044 EndY=-3.40591 EndZ=0
    g9: LineSegment StartX=-1.96044 StartY=-3.40591 StartZ=0 EndX=-0.581714 EndY=-3.64902 EndZ=0
    g10: LineSegment StartX=-1.7347 StartY=-2.12566 StartZ=0 EndX=-0.355971 EndY=-2.36877 EndZ=0
    g11: LineSegment StartX=-1.96044 StartY=-3.40591 StartZ=0 EndX=-4.52094 EndY=-2.95442 EndZ=0
    g12: LineSegment StartX=-7.17776 StartY=-18.022 StartZ=0 EndX=-5.73648 EndY=-9.84808 EndZ=0
    g13: LineSegment StartX=-5.73648 StartY=-9.84808 StartZ=0 EndX=-4.2952 EndY=-1.67417 EndZ=0
    g14: LineSegment StartX=-1.79725 StartY=-10.5427 StartZ=0 EndX=-5.73648 EndY=-9.84808 EndZ=0
  constraints (43):
    c: Coincident(g-4,g0)
    c: PointOnObject(g0,g-4)
    c: Coincident(g0,g1)
    c: Coincident(g1,g2)
    c: Coincident(g2,g3)
    c: PointOnObject(g3,g-5)
    c: PointOnObject(g7,g-5)
    c: PointOnObject(g4,g-3)
    c: Coincident(g4,g0)
    c: Equal(g4,g0)
    c: Coincident(g5,g1)
    c: Coincident(g6,g2)
    c: PointOnObject(g6,g-4)
    c: Coincident(g7,g8)
    c: Coincident(g8,g9)
    c: Coincident(g9,g4)
    c: Coincident(g10,g7)
    c: PointOnObject(g10,g-3)
    c: Coincident(g11,g8)
    c: Angle(g9,g11) = 3.14159
    c: Angle(g7,g10) = 3.14159
    c: Angle(g5,g1) = 3.14159
    c: Angle(g6,g3) = 3.14159
    c: Perpendicular(g0,g1)
    c: Perpendicular(g4,g9)
    c: Distance(g0,g4) = 14
    c: Distance(g1) = 1.4
    c: Coincident(g3,g12)
    c: PointOnObject(g12,g-5)
    c: Coincident(g12,g13)
    c: Coincident(g13,g7)
    c: Coincident(g14,g0)
    c: Coincident(g14,g12)
    c: Perpendicular(g4,g14)
    c: Equal(g13,g12)
    c: Distance(g3,g7) = 16.6
    c: Equal(g10,g9)
    c: Equal(g9,g1)
    c: Equal(g1,g6)
    c: PointOnObject(g5,g12)
    c: Perpendicular(g12,g3)
    c: Perpendicular(g13,g7)
    c: PointOnObject(g11,g13)
FEATURE [PartDesign::Pocket] Pocket012
  BaseFeature = -> Pad029
  Direction = (-0.994522,0,0.104528)
  Length = 14
  Length2 = 5
  Midplane = true
  Profile = -> Sketch045
  ReferenceAxis = -> Sketch045 [N_Axis]
  Type = 0
FEATURE [Sketcher::SketchObject] Sketch046
  ExternalGeometry = -> [Sketch042]
  FullyConstrained = true
  MapMode = 5
  Placement = pos=(4.4e-15,-4.7e-15,21) rot=(0.743145,0,0.669131;3.14159rad)
  Support = -> [DatumPlane]
  sketch-geometry (15):
    g0: LineSegment StartX=-0.581714 StartY=-3.64902 StartZ=0 EndX=-1.79725 EndY=-10.5427 EndZ=0
    g1: LineSegment StartX=-1.79725 StartY=-10.5427 StartZ=0 EndX=-3.01279 EndY=-17.4363 EndZ=0
    g2: LineSegment StartX=-3.01279 StartY=-17.4363 StartZ=0 EndX=-4.39152 EndY=-17.1932 EndZ=0
    g3: LineSegment StartX=-4.39152 StartY=-17.1932 StartZ=0 EndX=-4.61726 EndY=-18.4735 EndZ=0
    g4: LineSegment StartX=-4.61726 StartY=-18.4735 StartZ=0 EndX=-7.17776 EndY=-18.022 EndZ=0
    g5: LineSegment StartX=-7.17776 StartY=-18.022 StartZ=0 EndX=-5.73648 EndY=-9.84808 EndZ=0
    g6: LineSegment StartX=-5.73648 StartY=-9.84808 StartZ=0 EndX=-4.2952 EndY=-1.67417 EndZ=0
    g7: LineSegment StartX=-4.2952 StartY=-1.67417 StartZ=0 EndX=-1.7347 EndY=-2.12566 EndZ=0
    g8: LineSegment StartX=-1.7347 StartY=-2.12566 StartZ=0 EndX=-1.96044 EndY=-3.40591 EndZ=0
    g9: LineSegment StartX=-1.96044 StartY=-3.40591 StartZ=0 EndX=-0.581714 EndY=-3.64902 EndZ=0
    g10: LineSegment StartX=-1.7347 StartY=-2.12566 StartZ=0 EndX=-0.355971 EndY=-2.36877 EndZ=0
    g11: LineSegment StartX=-1.96044 StartY=-3.40591 StartZ=0 EndX=-4.52094 EndY=-2.95442 EndZ=0
    g12: LineSegment StartX=-4.39152 StartY=-17.1932 StartZ=0 EndX=-6.95202 EndY=-16.7417 EndZ=0
    g13: LineSegment StartX=-4.61726 StartY=-18.4735 StartZ=0 EndX=-3.23853 EndY=-18.7166 EndZ=0
    g14: LineSegment StartX=-1.79725 StartY=-10.5427 StartZ=0 EndX=-5.73648 EndY=-9.84808 EndZ=0
  constraints (43):
    c: PointOnObject(g0,g-3)
    c: Coincident(g0,g-4)
    c: Coincident(g0,g1)
    c: Coincident(g1,g2)
    c: Coincident(g2,g3)
    c: Coincident(g3,g4)
    c: PointOnObject(g4,g-5)
    c: Coincident(g4,g5)
    c: PointOnObject(g5,g-5)
    c: Coincident(g5,g6)
    c: PointOnObject(g6,g-5)
    c: Coincident(g6,g7)
    c: Coincident(g7,g8)
    c: Coincident(g8,g9)
    c: Coincident(g9,g0)
    c: Coincident(g10,g7)
    c: PointOnObject(g10,g-3)
    c: Coincident(g11,g8)
    c: PointOnObject(g11,g6)
    c: Coincident(g12,g2)
    c: PointOnObject(g12,g5)
    c: Coincident(g13,g3)
    c: PointOnObject(g13,g-4)
    c: Angle(g2,g12) = 3.14159
    c: Angle(g4,g13) = 3.14159
    c: Angle(g9,g11) = 3.14159
    c: Angle(g10,g7) = 3.14159
    c: Equal(g10,g9)
    c: Equal(g9,g2)
    c: Equal(g2,g13)
    c: PointOnObject(g1,g-4)
    c: Coincident(g14,g0)
    c: Coincident(g14,g5)
    c: Perpendicular(g0,g14)
    c: Equal(g0,g1)
    c: Equal(g6,g5)
    c: Distance(g6,g4) = 16.6
    c: Distance(g0,g1) = 14
    c: Perpendicular(g1,g2)
    c: Perpendicular(g9,g0)
    c: Perpendicular(g6,g7)
    c: Distance(g2) = 1.4
    c: Perpendicular(g5,g4)
FEATURE [PartDesign::Pocket] Pocket013
  BaseFeature = -> Pocket012
  Direction = (-0.994522,0,0.104528)
  Length = 14
  Length2 = 5
  Midplane = true
  Profile = -> Sketch046
  ReferenceAxis = -> Sketch046 [N_Axis]
  Type = 0
FEATURE [Sketcher::SketchObject] Sketch047
  ExternalGeometry = -> [Sketch042]
  FullyConstrained = true
  MapMode = 5
  Placement = pos=(19.8904,-4.2e-15,18.9094) rot=(0.743145,0,0.669131;3.14159rad)
  Support = -> [DatumPlane002]
  sketch-geometry (15):
    g0: LineSegment StartX=-0.355971 StartY=-2.36877 StartZ=0 EndX=-1.7347 EndY=-2.12566 EndZ=0
    g1: LineSegment StartX=-3.23853 StartY=-18.7166 StartZ=0 EndX=-4.61726 EndY=-18.4735 EndZ=0
    g2: LineSegment StartX=-6.95202 StartY=-16.7417 StartZ=0 EndX=-4.39152 EndY=-17.1932 EndZ=0
    g3: LineSegment StartX=-4.52094 StartY=-2.95442 StartZ=0 EndX=-1.96044 EndY=-3.40591 EndZ=0
    g4: LineSegment StartX=-4.2952 StartY=-1.67417 StartZ=0 EndX=-1.7347 EndY=-2.12566 EndZ=0
    g5: LineSegment StartX=-1.7347 StartY=-2.12566 StartZ=0 EndX=-1.96044 EndY=-3.40591 EndZ=0
    g6: LineSegment StartX=-1.96044 StartY=-3.40591 StartZ=0 EndX=-0.581714 EndY=-3.64902 EndZ=0
    g7: LineSegment StartX=-0.581714 StartY=-3.64902 StartZ=0 EndX=-1.79725 EndY=-10.5427 EndZ=0
    g8: LineSegment StartX=-1.79725 StartY=-10.5427 StartZ=0 EndX=-3.01279 EndY=-17.4363 EndZ=0
    g9: LineSegment StartX=-3.01279 StartY=-17.4363 StartZ=0 EndX=-4.39152 EndY=-17.1932 EndZ=0
    g10: LineSegment StartX=-4.39152 StartY=-17.1932 StartZ=0 EndX=-4.61726 EndY=-18.4735 EndZ=0
    g11: LineSegment StartX=-4.61726 StartY=-18.4735 StartZ=0 EndX=-7.17776 EndY=-18.022 EndZ=0
    g12: LineSegment StartX=-7.17776 StartY=-18.022 StartZ=0 EndX=-5.73648 EndY=-9.84808 EndZ=0
    g13: LineSegment StartX=-5.73648 StartY=-9.84808 StartZ=0 EndX=-4.2952 EndY=-1.67417 EndZ=0
    g14: LineSegment StartX=-1.79725 StartY=-10.5427 StartZ=0 EndX=-5.73648 EndY=-9.84808 EndZ=0
  constraints (43):
    c: PointOnObject(g0,g-3)
    c: PointOnObject(g1,g-4)
    c: PointOnObject(g2,g-5)
    c: PointOnObject(g3,g-5)
    c: PointOnObject(g4,g-5)
    c: Coincident(g4,g0)
    c: Coincident(g4,g5)
    c: Coincident(g5,g3)
    c: Coincident(g5,g6)
    c: PointOnObject(g6,g-3)
    c: Coincident(g6,g7)
    c: Coincident(g7,g-4)
    c: Coincident(g7,g8)
    c: PointOnObject(g8,g-4)
    c: Coincident(g8,g9)
    c: Coincident(g9,g2)
    c: Coincident(g9,g10)
    c: Coincident(g10,g1)
    c: Coincident(g10,g11)
    c: Coincident(g11,g12)
    c: PointOnObject(g12,g-5)
    c: Coincident(g12,g13)
    c: Coincident(g13,g4)
    c: Perpendicular(g7,g6)
    c: Perpendicular(g13,g4)
    c: Perpendicular(g8,g9)
    c: Perpendicular(g12,g11)
    c: PointOnObject(g11,g-5)
    c: Coincident(g14,g7)
    c: Coincident(g14,g12)
    c: Perpendicular(g7,g14)
    c: Angle(g3,g6) = 3.14159
    c: Angle(g0,g4) = 3.14159
    c: Angle(g2,g9) = 3.14159
    c: Angle(g1,g11) = 3.14159
    c: Equal(g1,g9)
    c: Equal(g9,g6)
    c: Equal(g6,g0)
    c: Distance(g6) = 1.4
    c: Equal(g8,g7)
    c: Equal(g13,g12)
    c: Distance(g8,g6) = 14
    c: Distance(g4,g11) = 16.6
FEATURE [PartDesign::Pocket] Pocket014
  BaseFeature = -> Pocket013
  Direction = (-0.994522,0,0.104528)
  Length = 14
  Length2 = 5
  Midplane = true
  Profile = -> Sketch047
  ReferenceAxis = -> Sketch047 [N_Axis]
  Type = 0
FEATURE [Sketcher::SketchObject] Sketch048
  FullyConstrained = true
  MapMode = 5
  Support = -> [XY_Plane007]
  expr: .Constraints.Rlyy = -<<Thumb Cluster>>.Placement.Base.y + 7mm
  expr: Constraints[112] = <<Spreadsheet>>.NutR * 2
  expr: Constraints[113] = <<Spreadsheet>>.ScrewD
  expr: Constraints[149] = <<Spreadsheet>>.ArchLength + <<MiddleArch>>.Placement.Base.y + <<Spreadsheet>>.NutR + 10mm
  expr: Constraints[152] = <<OuterArch>>.Placement.Base.y + <<Spreadsheet>>.NutR
  expr: Constraints[153] = <<PinkieArch>>.Placement.Base.y + <<Spreadsheet>>.NutR
  expr: Constraints[154] = <<Spreadsheet>>.ArchLength + -<<OuterArch>>.Placement.Base.y + <<Spreadsheet>>.NutR + 10mm
  expr: Constraints[155] = <<RingArch>>.Placement.Base.y + <<Spreadsheet>>.NutR
  expr: Constraints[156] = <<Spreadsheet>>.ArchLength + -<<PinkieArch>>.Placement.Base.y + <<Spreadsheet>>.NutR + 10mm
  expr: Constraints[157] = <<MiddleArch>>.Placement.Base.y + <<Spreadsheet>>.NutR
  expr: Constraints[158] = <<IndexArch>>.Placement.Base.y + <<Spreadsheet>>.NutR
  expr: Constraints[159] = <<InnerIndexArch>>.Placement.Base.y + <<Spreadsheet>>.NutR
  expr: Constraints[161] = <<Spreadsheet>>.ArchLength + -<<RingArch>>.Placement.Base.y + <<Spreadsheet>>.NutR + 10mm
  expr: Constraints[162] = <<Spreadsheet>>.ArchLength + -<<MiddleArch>>.Placement.Base.y + <<Spreadsheet>>.NutR + 10mm
  sketch-geometry (70):
    g0: ArcOfCircle CenterX=10 CenterY=-5 CenterZ=0 NormalX=0 NormalY=0 NormalZ=1 AngleXU=0 Radius=2.1 StartAngle=3.14159 EndAngle=6.28319
    g1: ArcOfCircle CenterX=10 CenterY=65 CenterZ=0 NormalX=0 NormalY=0 NormalZ=1 AngleXU=0 Radius=2.1 StartAngle=3.2e-15 EndAngle=3.14159
    g2: LineSegment StartX=12.1 StartY=-5 StartZ=0 EndX=12.1 EndY=65 EndZ=0
    g3: LineSegment StartX=7.9 StartY=65 StartZ=0 EndX=7.9 EndY=-5 EndZ=0
    g4: ArcOfCircle CenterX=10 CenterY=-15 CenterZ=0 NormalX=0 NormalY=0 NormalZ=1 AngleXU=0 Radius=2.1 StartAngle=3e-16 EndAngle=3.14159
    g5: ArcOfCircle CenterX=10 CenterY=-70 CenterZ=0 NormalX=0 NormalY=0 NormalZ=1 AngleXU=0 Radius=2.1 StartAngle=3.14159 EndAngle=6.28319
    g6: LineSegment StartX=7.9 StartY=-15 StartZ=0 EndX=7.9 EndY=-70 EndZ=0
    g7: LineSegment StartX=12.1 StartY=-70 StartZ=0 EndX=12.1 EndY=-15 EndZ=0
    g8: ArcOfCircle CenterX=30 CenterY=-70 CenterZ=0 NormalX=0 NormalY=0 NormalZ=1 AngleXU=0 Radius=2.1 StartAngle=3.14159 EndAngle=6.28319
    g9: ArcOfCircle CenterX=30 CenterY=-15 CenterZ=0 NormalX=0 NormalY=0 NormalZ=1 AngleXU=0 Radius=2.1 StartAngle=3e-16 EndAngle=3.14159
    g10: LineSegment StartX=32.1 StartY=-70 StartZ=0 EndX=32.1 EndY=-15 EndZ=0
    g11: LineSegment StartX=27.9 StartY=-15 StartZ=0 EndX=27.9 EndY=-70 EndZ=0
    g12: ArcOfCircle CenterX=50 CenterY=-5 CenterZ=0 NormalX=0 NormalY=0 NormalZ=1 AngleXU=0 Radius=2.1 StartAngle=0 EndAngle=3.14159
    g13: ArcOfCircle CenterX=50 CenterY=-60 CenterZ=0 NormalX=0 NormalY=0 NormalZ=1 AngleXU=0 Radius=2.1 StartAngle=3.14159 EndAngle=6.28319
    g14: LineSegment StartX=47.9 StartY=-5 StartZ=0 EndX=47.9 EndY=-60 EndZ=0
    g15: LineSegment StartX=52.1 StartY=-60 StartZ=0 EndX=52.1 EndY=-5 EndZ=0
    g16: ArcOfCircle CenterX=70 CenterY=-55 CenterZ=0 NormalX=0 NormalY=0 NormalZ=1 AngleXU=0 Radius=2.1 StartAngle=3.14159 EndAngle=6.28319
    g17: ArcOfCircle CenterX=70 CenterY=5e-16 CenterZ=0 NormalX=0 NormalY=0 NormalZ=1 AngleXU=0 Radius=2.1 StartAngle=0 EndAngle=3.14159
    g18: LineSegment StartX=72.1 StartY=-55 StartZ=0 EndX=72.1 EndY=0 EndZ=0
    g19: LineSegment StartX=67.9 StartY=8e-16 StartZ=0 EndX=67.9 EndY=-55 EndZ=0
    g20: ArcOfCircle CenterX=90 CenterY=-68 CenterZ=0 NormalX=0 NormalY=0 NormalZ=1 AngleXU=0 Radius=2.1 StartAngle=3.14159 EndAngle=6.28319
    g21: ArcOfCircle CenterX=90 CenterY=-5 CenterZ=0 NormalX=0 NormalY=0 NormalZ=1 AngleXU=0 Radius=2.1 StartAngle=1e-16 EndAngle=3.14159
    g22: LineSegment StartX=92.1 StartY=-68 StartZ=0 EndX=92.1 EndY=-5 EndZ=0
    g23: LineSegment StartX=87.9 StartY=-5 StartZ=0 EndX=87.9 EndY=-68 EndZ=0
    g24: ArcOfCircle CenterX=110 CenterY=-5 CenterZ=0 NormalX=0 NormalY=0 NormalZ=1 AngleXU=0 Radius=2.1 StartAngle=2e-16 EndAngle=3.14159
    g25: ArcOfCircle CenterX=110 CenterY=-68 CenterZ=0 NormalX=0 NormalY=0 NormalZ=1 AngleXU=0 Radius=2.1 StartAngle=3.14159 EndAngle=6.28319
    g26: LineSegment StartX=107.9 StartY=-5 StartZ=0 EndX=107.9 EndY=-68 EndZ=0
    g27: LineSegment StartX=112.1 StartY=-68 StartZ=0 EndX=112.1 EndY=-5 EndZ=0
    g28: ArcOfCircle CenterX=130 CenterY=-68 CenterZ=0 NormalX=0 NormalY=0 NormalZ=1 AngleXU=0 Radius=2.1 StartAngle=3.14159 EndAngle=6.28319
    g29: ArcOfCircle CenterX=130 CenterY=-5 CenterZ=0 NormalX=0 NormalY=0 NormalZ=1 AngleXU=0 Radius=2.1 StartAngle=1e-16 EndAngle=3.14159
    g30: LineSegment StartX=132.1 StartY=-68 StartZ=0 EndX=132.1 EndY=-5 EndZ=0
    g31: LineSegment StartX=127.9 StartY=-5 StartZ=0 EndX=127.9 EndY=-68 EndZ=0
    g32: ArcOfCircle CenterX=130 CenterY=5 CenterZ=0 NormalX=0 NormalY=0 NormalZ=1 AngleXU=0 Radius=2.1 StartAngle=3.14159 EndAngle=6.28319
    g33: ArcOfCircle CenterX=130 CenterY=65 CenterZ=0 NormalX=0 NormalY=0 NormalZ=1 AngleXU=0 Radius=2.1 StartAngle=-9e-16 EndAngle=3.14159
    g34: LineSegment StartX=132.1 StartY=5 StartZ=0 EndX=132.1 EndY=65 EndZ=0
    g35: LineSegment StartX=127.9 StartY=65 StartZ=0 EndX=127.9 EndY=5 EndZ=0
    g36: ArcOfCircle CenterX=110 CenterY=65 CenterZ=0 NormalX=0 NormalY=0 NormalZ=1 AngleXU=0 Radius=2.1 StartAngle=-1.8e-15 EndAngle=3.14159
    g37: ArcOfCircle CenterX=110 CenterY=5 CenterZ=0 NormalX=0 NormalY=0 NormalZ=1 AngleXU=0 Radius=2.1 StartAngle=3.14159 EndAngle=6.28319
    g38: LineSegment StartX=107.9 StartY=65 StartZ=0 EndX=107.9 EndY=5 EndZ=0
    g39: LineSegment StartX=112.1 StartY=5 StartZ=0 EndX=112.1 EndY=65 EndZ=0
    g40: ArcOfCircle CenterX=90 CenterY=5 CenterZ=0 NormalX=0 NormalY=0 NormalZ=1 AngleXU=0 Radius=2.1 StartAngle=3.14159 EndAngle=6.28319
    g41: ArcOfCircle CenterX=90 CenterY=65 CenterZ=0 NormalX=0 NormalY=0 NormalZ=1 AngleXU=0 Radius=2.1 StartAngle=-9e-16 EndAngle=3.14159
    g42: LineSegment StartX=92.1 StartY=5 StartZ=0 EndX=92.1 EndY=65 EndZ=0
    g43: LineSegment StartX=87.9 StartY=65 StartZ=0 EndX=87.9 EndY=5 EndZ=0
    g44: ArcOfCircle CenterX=70 CenterY=10 CenterZ=0 NormalX=0 NormalY=0 NormalZ=1 AngleXU=0 Radius=2.1 StartAngle=3.14159 EndAngle=6.28319
    g45: ArcOfCircle CenterX=70 CenterY=65 CenterZ=0 NormalX=0 NormalY=0 NormalZ=1 AngleXU=0 Radius=2.1 StartAngle=-2.7e-15 EndAngle=3.14159
    g46: LineSegment StartX=72.1 StartY=10 StartZ=0 EndX=72.1 EndY=65 EndZ=0
    g47: LineSegment StartX=67.9 StartY=65 StartZ=0 EndX=67.9 EndY=10 EndZ=0
    g48: ArcOfCircle CenterX=50 CenterY=5 CenterZ=0 NormalX=0 NormalY=0 NormalZ=1 AngleXU=0 Radius=2.1 StartAngle=3.14159 EndAngle=6.28319
    g49: ArcOfCircle CenterX=50 CenterY=65 CenterZ=0 NormalX=0 NormalY=0 NormalZ=1 AngleXU=0 Radius=2.1 StartAngle=5e-16 EndAngle=3.14159
    g50: LineSegment StartX=52.1 StartY=5 StartZ=0 EndX=52.1 EndY=65 EndZ=0
    g51: LineSegment StartX=47.9 StartY=65 StartZ=0 EndX=47.9 EndY=5 EndZ=0
    g52: ArcOfCircle CenterX=30 CenterY=-5 CenterZ=0 NormalX=0 NormalY=0 NormalZ=1 AngleXU=0 Radius=2.1 StartAngle=3.14159 EndAngle=6.28319
    g53: ArcOfCircle CenterX=30 CenterY=65 CenterZ=0 NormalX=0 NormalY=0 NormalZ=1 AngleXU=0 Radius=2.1 StartAngle=-9e-16 EndAngle=3.14159
    g54: LineSegment StartX=32.1 StartY=-5 StartZ=0 EndX=32.1 EndY=65 EndZ=0
    g55: LineSegment StartX=27.9 StartY=65 StartZ=0 EndX=27.9 EndY=-5 EndZ=0
    g56: LineSegment StartX=10 StartY=65 StartZ=0 EndX=30 EndY=65 EndZ=0
    g57: LineSegment StartX=30 StartY=65 StartZ=0 EndX=50 EndY=65 EndZ=0
    g58: LineSegment StartX=50 StartY=65 StartZ=0 EndX=70 EndY=65 EndZ=0
    g59: LineSegment StartX=70 StartY=65 StartZ=0 EndX=90 EndY=65 EndZ=0
    g60: LineSegment StartX=90 StartY=65 StartZ=0 EndX=110 EndY=65 EndZ=0
    g61: LineSegment StartX=110 StartY=65 StartZ=0 EndX=130 EndY=65 EndZ=0
    g62: LineSegment StartX=10 StartY=-5 StartZ=0 EndX=10 EndY=-15 EndZ=0
    g63: LineSegment StartX=30 StartY=-15 StartZ=0 EndX=30 EndY=-5 EndZ=0
    g64: LineSegment StartX=50 StartY=5 StartZ=0 EndX=50 EndY=-5 EndZ=0
    g65: LineSegment StartX=70 StartY=5e-16 StartZ=0 EndX=70 EndY=10 EndZ=0
    g66: LineSegment StartX=90 StartY=5 StartZ=0 EndX=90 EndY=-5 EndZ=0
    g67: LineSegment StartX=110 StartY=-5 StartZ=0 EndX=110 EndY=5 EndZ=0
    g68: LineSegment StartX=130 StartY=5 StartZ=0 EndX=130 EndY=-5 EndZ=0
    g69: LineSegment StartX=90 StartY=-68 StartZ=0 EndX=130 EndY=-68 EndZ=0
  constraints (168):
    c: Tangent(g0,g2) = -1.5708
    c: Tangent(g2,g1) = -1.5708
    c: Tangent(g1,g3) = -1.5708
    c: Tangent(g3,g0) = -1.5708
    c: Equal(g0,g1)
    c: Vertical(g2)
    c: Tangent(g4,g6) = -1.5708
    c: Tangent(g6,g5) = -1.5708
    c: Tangent(g5,g7) = -1.5708
    c: Tangent(g7,g4) = -1.5708
    c: Equal(g4,g5)
    c: Vertical(g6)
    c: Tangent(g8,g10) = -1.5708
    c: Tangent(g10,g9) = -1.5708
    c: Tangent(g9,g11) = -1.5708
    c: Tangent(g11,g8) = -1.5708
    c: Equal(g8,g9)
    c: Vertical(g10)
    c: Tangent(g12,g14) = -1.5708
    c: Tangent(g14,g13) = -1.5708
    c: Tangent(g13,g15) = -1.5708
    c: Tangent(g15,g12) = -1.5708
    c: Equal(g12,g13)
    c: Vertical(g14)
    c: Tangent(g16,g18) = -1.5708
    c: Tangent(g18,g17) = -1.5708
    c: Tangent(g17,g19) = -1.5708
    c: Tangent(g19,g16) = -1.5708
    c: Equal(g16,g17)
    c: Vertical(g18)
    c: Tangent(g20,g22) = -1.5708
    c: Tangent(g22,g21) = -1.5708
    c: Tangent(g21,g23) = -1.5708
    c: Tangent(g23,g20) = -1.5708
    c: Equal(g20,g21)
    c: Vertical(g22)
    c: Tangent(g24,g26) = -1.5708
    c: Tangent(g26,g25) = -1.5708
    c: Tangent(g25,g27) = -1.5708
    c: Tangent(g27,g24) = -1.5708
    c: Equal(g24,g25)
    c: Vertical(g26)
    c: Tangent(g28,g30) = -1.5708
    c: Tangent(g30,g29) = -1.5708
    c: Tangent(g29,g31) = -1.5708
    c: Tangent(g31,g28) = -1.5708
    c: Equal(g28,g29)
    c: Vertical(g30)
    c: Tangent(g32,g34) = -1.5708
    c: Tangent(g34,g33) = -1.5708
    c: Tangent(g33,g35) = -1.5708
    c: Tangent(g35,g32) = -1.5708
    c: Equal(g32,g33)
    c: Vertical(g34)
    c: Tangent(g36,g38) = -1.5708
    c: Tangent(g38,g37) = -1.5708
    c: Tangent(g37,g39) = -1.5708
    c: Tangent(g39,g36) = -1.5708
    c: Equal(g36,g37)
    c: Vertical(g38)
    c: Tangent(g40,g42) = -1.5708
    c: Tangent(g42,g41) = -1.5708
    c: Tangent(g41,g43) = -1.5708
    c: Tangent(g43,g40) = -1.5708
    c: Equal(g40,g41)
    c: Vertical(g42)
    c: Tangent(g44,g46) = -1.5708
    c: Tangent(g46,g45) = -1.5708
    c: Tangent(g45,g47) = -1.5708
    c: Tangent(g47,g44) = -1.5708
    c: Equal(g44,g45)
    c: Vertical(g46)
    c: Tangent(g48,g50) = -1.5708
    c: Tangent(g50,g49) = -1.5708
    c: Tangent(g49,g51) = -1.5708
    c: Tangent(g51,g48) = -1.5708
    c: Equal(g48,g49)
    c: Vertical(g50)
    c: Tangent(g52,g54) = -1.5708
    c: Tangent(g54,g53) = -1.5708
    c: Tangent(g53,g55) = -1.5708
    c: Tangent(g55,g52) = -1.5708
    c: Equal(g52,g53)
    c: Vertical(g54)
    c: Coincident(g56,g1)
    c: Coincident(g56,g53)
    c: Coincident(g57,g53)
    c: Coincident(g57,g49)
    c: Coincident(g57,g58)
    c: Coincident(g58,g45)
    c: Coincident(g58,g59)
    c: Coincident(g59,g41)
    c: Coincident(g59,g60)
    c: Coincident(g60,g36)
    c: Coincident(g60,g61)
    c: Coincident(g61,g33)
    c: Coincident(g62,g0)
    c: Coincident(g62,g4)
    c: Vertical(g62)
    c: Coincident(g63,g9)
    c: Coincident(g63,g52)
    c: Coincident(g64,g48)
    c: Coincident(g64,g12)
    c: Coincident(g65,g17)
    c: Coincident(g65,g44)
    c: Coincident(g66,g40)
    c: Coincident(g66,g21)
    c: Coincident(g67,g24)
    c: Coincident(g67,g37)
    c: Coincident(g68,g32)
    c: Coincident(g68,g29)
    c: Vertical(g68)
    c: DistanceY(g68,g68) = 10
    c: DistanceX(g1,g1) = 4.2
    c: Equal(g1,g53)
    c: Equal(g53,g49)
    c: Equal(g49,g45)
    c: Equal(g45,g41)
    c: Equal(g41,g36)
    c: Equal(g36,g33)
    c: Equal(g5,g8)
    c: Equal(g8,g13)
    c: Equal(g13,g16)
    c: Equal(g16,g20)
    c: Equal(g20,g25)
    c: Equal(g25,g28)
    c: Equal(g5,g1)
    c: Vertical(g63)
    c: Vertical(g65)
    c: Vertical(g66)
    c: Vertical(g67)
    c: Equal(g68,g67)
    c: Equal(g67,g66)
    c: Equal(g66,g65)
    c: Equal(g65,g64)
    c: Equal(g64,g63)
    c: Equal(g63,g62)
    c: Equal(g56,g57)
    c: Equal(g57,g58)
    c: Equal(g58,g59)
    c: Equal(g59,g60)
    c: Equal(g60,g61)
    c: Horizontal(g61)
    c: Horizontal(g60)
    c: Horizontal(g59)
    c: Horizontal(g58)
    c: Horizontal(g57)
    c: Horizontal(g56)
    c: DistanceX(g-1,g0) = 10
    c: DistanceY(g-1,g45) = 65
    c: DistanceX(g56,g56) = 20
    c: Vertical(g64)
    c: DistanceY(g-1,g0) = -5
    c: DistanceY(g-1,g52) = -5
    c: DistanceY(g5,g-1) = 70
    c: DistanceY(g-1,g48) = 5
    c: DistanceY(g8,g-1) = 70
    c: DistanceY(g-1,g44) = 10
    c: DistanceY(g-1,g40) = 5
    c: DistanceY(g-1,g37) = 5
    c: Horizontal(g24,g29)
    c: DistanceY(g13,g-1) = 60
    c: DistanceY(g16,g-1) = 55
    c: DistanceY(g20,g-1) = 68  'Rlyy'
    c: Coincident(g69,g20)
    c: Horizontal(g69)
    c: Coincident(g69,g28)
    c: PointOnObject(g25,g69)
FEATURE [PartDesign::Pocket] Pocket015
  BaseFeature = -> Pad025
  Direction = (0,0,-1)
  Length = 5
  Length2 = 5
  Midplane = true
  Placement = pos=(0,0,0) rot=(1,0,0;1.5708rad)
  Profile = -> Sketch048
  ReferenceAxis = -> Sketch048 [N_Axis]
  Type = 1
FEATURE [PartDesign::Body] Body007  label="BasePlate"
  Group = -> [Sketch038,Pad024,Sketch039,Pad025,Sketch048,Pocket015]
  Origin = -> Origin007
  Tip = -> Pocket015
FEATURE [Sketcher::SketchObject] Sketch049
  FullyConstrained = true
  MapMode = 5
  Placement = pos=(0,0,0) rot=(0.57735,0.57735,0.57735;2.0944rad)
  Support = -> [YZ_Plane012]
  expr: Constraints[88] = <<Spreadsheet>>.Wiring
  sketch-geometry (43):
    g0: Circle CenterX=49 CenterY=13.8 CenterZ=0 NormalX=0 NormalY=0 NormalZ=1 AngleXU=0 Radius=1.1
    g1: Circle CenterX=49 CenterY=25.2 CenterZ=0 NormalX=0 NormalY=0 NormalZ=1 AngleXU=0 Radius=1.1
    g2: Circle CenterX=2 CenterY=25.2 CenterZ=0 NormalX=0 NormalY=0 NormalZ=1 AngleXU=0 Radius=1.1
    g3: Circle CenterX=2 CenterY=13.8 CenterZ=0 NormalX=0 NormalY=0 NormalZ=1 AngleXU=0 Radius=1.1
    g4: ArcOfCircle CenterX=2 CenterY=25.2 CenterZ=0 NormalX=0 NormalY=0 NormalZ=1 AngleXU=0 Radius=2 StartAngle=4.71239 EndAngle=7.85398
    g5: ArcOfCircle CenterX=2 CenterY=13.8 CenterZ=0 NormalX=0 NormalY=0 NormalZ=1 AngleXU=0 Radius=2 StartAngle=4.71239 EndAngle=7.85398
    g6: ArcOfCircle CenterX=49 CenterY=13.8 CenterZ=0 NormalX=0 NormalY=0 NormalZ=1 AngleXU=0 Radius=2 StartAngle=4.71239 EndAngle=7.85398
    g7: ArcOfCircle CenterX=49 CenterY=25.2 CenterZ=0 NormalX=0 NormalY=0 NormalZ=1 AngleXU=0 Radius=2 StartAngle=4.71239 EndAngle=7.85398
    g8: LineSegment StartX=2 StartY=23.2 StartZ=0 EndX=0 EndY=23.2 EndZ=0
    g9: LineSegment StartX=2 StartY=27.2 StartZ=0 EndX=2e-16 EndY=27.2 EndZ=0
    g10: ArcOfCircle CenterX=0 CenterY=21.2 CenterZ=0 NormalX=0 NormalY=0 NormalZ=1 AngleXU=0 Radius=2 StartAngle=1.5708 EndAngle=3.14159
    g11: ArcOfCircle CenterX=0 CenterY=22.2 CenterZ=0 NormalX=0 NormalY=0 NormalZ=1 AngleXU=0 Radius=5 StartAngle=1.5708 EndAngle=3.14159
    g12: LineSegment StartX=-2 StartY=21.2 StartZ=0 EndX=-2 EndY=14.416 EndZ=0
    g13: LineSegment StartX=-5 StartY=22.2 StartZ=0 EndX=-5 EndY=0 EndZ=0
    g14: LineSegment StartX=2 StartY=15.8 StartZ=0 EndX=7e-16 EndY=15.8 EndZ=0
    g15: LineSegment StartX=2 StartY=11.8 StartZ=0 EndX=2e-16 EndY=11.8 EndZ=0
    g16: ArcOfCircle CenterX=0 CenterY=9.4 CenterZ=0 NormalX=0 NormalY=0 NormalZ=1 AngleXU=0 Radius=2.4 StartAngle=1.5708 EndAngle=4.71239
    g17: LineSegment StartX=2 StartY=13.8 StartZ=0 EndX=2 EndY=25.2 EndZ=0
    g18: LineSegment StartX=49 StartY=13.8 StartZ=0 EndX=49 EndY=25.2 EndZ=0
    g19: LineSegment StartX=2 StartY=13.8 StartZ=0 EndX=49 EndY=13.8 EndZ=0
    g20: LineSegment StartX=42 StartY=9 StartZ=0 EndX=42 EndY=30 EndZ=0
    g21: LineSegment StartX=42 StartY=30 StartZ=0 EndX=2 EndY=27.2 EndZ=0
    g22: LineSegment StartX=2 StartY=11.8 StartZ=0 EndX=42 EndY=9 EndZ=0
    g23: LineSegment StartX=42 StartY=9 StartZ=0 EndX=42 EndY=7 EndZ=0
    g24: LineSegment StartX=0 StartY=21.2 StartZ=0 EndX=-2 EndY=21.2 EndZ=0
    g25: LineSegment StartX=0 StartY=7 StartZ=0 EndX=42 EndY=7 EndZ=0
    g26: ArcOfCircle CenterX=42 CenterY=9 CenterZ=0 NormalX=0 NormalY=0 NormalZ=1 AngleXU=0 Radius=2 StartAngle=4.71239 EndAngle=6.28319
    g27: ArcOfCircle CenterX=49 CenterY=17.8 CenterZ=0 NormalX=0 NormalY=0 NormalZ=1 AngleXU=0 Radius=2 StartAngle=3.14159 EndAngle=4.71239
    g28: ArcOfCircle CenterX=49 CenterY=21.2 CenterZ=0 NormalX=0 NormalY=0 NormalZ=1 AngleXU=0 Radius=2 StartAngle=1.5708 EndAngle=3.14159
    g29: LineSegment StartX=47 StartY=21.2 StartZ=0 EndX=47 EndY=17.8 EndZ=0
    g30: ArcOfCircle CenterX=49 CenterY=22.2 CenterZ=0 NormalX=0 NormalY=0 NormalZ=1 AngleXU=0 Radius=5 StartAngle=1.5708 EndAngle=3.14159
    g31: LineSegment StartX=49 StartY=25.2 StartZ=0 EndX=49 EndY=27.2 EndZ=0
    g32: LineSegment StartX=44 StartY=22.2 StartZ=0 EndX=44 EndY=9 EndZ=0
    g33: LineSegment StartX=51 StartY=0 StartZ=0 EndX=51 EndY=3 EndZ=0
    g34: LineSegment StartX=51 StartY=3 StartZ=0 EndX=51 EndY=13.8 EndZ=0
    g35: ArcOfCircle CenterX=2.14e-14 CenterY=13.6629 CenterZ=0 NormalX=0 NormalY=0 NormalZ=1 AngleXU=0 Radius=2.13707 StartAngle=1.5708 EndAngle=2.78149
    g36: LineSegment StartX=-0.888889 StartY=11.6293 StartZ=0 EndX=-2 EndY=14.416 EndZ=0
    g37: ArcOfCircle CenterX=49 CenterY=9.8 CenterZ=0 NormalX=0 NormalY=0 NormalZ=1 AngleXU=0 Radius=2 StartAngle=1.5708 EndAngle=3.14159
    g38: LineSegment StartX=-5 StartY=0 StartZ=0 EndX=47 EndY=0 EndZ=0
    g39: LineSegment StartX=47 StartY=0 StartZ=0 EndX=51 EndY=0 EndZ=0
    g40: LineSegment StartX=47 StartY=9.8 StartZ=0 EndX=47 EndY=0 EndZ=0
    g41: LineSegment StartX=49 StartY=11.8 StartZ=0 EndX=49 EndY=13.8 EndZ=0
    g42: LineSegment StartX=47 StartY=21.2 StartZ=0 EndX=49 EndY=21.2 EndZ=0
  constraints (114):
    c: Diameter(g2) = 2.2
    c: Equal(g3,g2)
    c: Equal(g2,g1)
    c: Equal(g1,g0)
    c: Coincident(g4,g2)
    c: Coincident(g5,g3)
    c: Coincident(g6,g0)
    c: Coincident(g7,g1)
    c: DistanceY(g3,g2) = 11.4
    c: Diameter(g4) = 4
    c: Equal(g4,g5)
    c: Equal(g5,g6)
    c: Equal(g6,g7)
    c: PointOnObject(g39,g-1)
    c: PointOnObject(g8,g-2)
    c: Horizontal(g8)
    c: Tangent(g-2,g4)
    c: Tangent(g4,g8) = 1.5708
    c: PointOnObject(g9,g-2)
    c: Horizontal(g9)
    c: Tangent(g9,g4) = -1.5708
    c: PointOnObject(g10,g-2)
    c: Coincident(g10,g8)
    c: PointOnObject(g11,g-2)
    c: Coincident(g11,g9)
    c: DistanceX(g11,g10) = 3
    c: Vertical(g12)
    c: Tangent(g12,g10) = -1.5708
    c: Vertical(g13)
    c: Tangent(g13,g11) = -1.5708
    c: PointOnObject(g14,g-2)
    c: Horizontal(g14)
    c: Tangent(g5,g14) = -1.5708
    c: PointOnObject(g15,g-2)
    c: Horizontal(g15)
    c: PointOnObject(g16,g-2)
    c: Coincident(g16,g15)
    c: Coincident(g17,g5)
    c: Coincident(g17,g4)
    c: Vertical(g17)
    c: Coincident(g18,g0)
    c: Coincident(g18,g1)
    c: Vertical(g18)
    c: Equal(g18,g17)
    c: Coincident(g19,g5)
    c: Coincident(g19,g0)
    c: Horizontal(g19)
    c: Vertical(g20)
    c: DistanceY(g20,g20) = 21
    c: Coincident(g21,g20)
    c: Coincident(g21,g4)
    c: Coincident(g22,g5)
    c: Coincident(g22,g20)
    c: Tangent(g15,g5) = 1.5708
    c: Equal(g21,g22)
    c: PointOnObject(g16,g-2)
    c: Coincident(g23,g20)
    c: Vertical(g23)
    c: Coincident(g24,g10)
    c: Coincident(g24,g10)
    c: Equal(g24,g23)
    c: Coincident(g25,g16)
    c: Horizontal(g25)
    c: Coincident(g13,g38)
    c: PointOnObject(g38,g-1)
    c: Tangent(g25,g26) = -1.5708
    c: Coincident(g23,g25)
    c: PointOnObject(g6,g18)
    c: PointOnObject(g27,g18)
    c: Coincident(g27,g6)
    c: PointOnObject(g28,g18)
    c: Tangent(g29,g28) = -1.5708
    c: Tangent(g29,g27) = -1.5708
    c: Vertical(g29)
    c: Tangent(g7,g28) = 1.5708
    c: Tangent(g7,g30) = -1.5708
    c: Coincident(g31,g1)
    c: Coincident(g31,g7)
    c: Vertical(g31)
    c: Vertical(g32)
    c: Tangent(g32,g30) = -1.5708
    c: DistanceX(g30,g28) = 3
    c: Tangent(g32,g26) = 1.5708
    c: Coincident(g33,g39)
    c: Vertical(g33)
    c: DistanceY(g33,g33) = 3
    c: Coincident(g34,g33)
    c: Tangent(g34,g6) = -1.5708
    c: DistanceY(g33,g26) = 6
    c: DistanceX(g-1,g39) = 51
    c: Tangent(g35,g14) = -1.5708
    c: Coincident(g35,g12)
    c: PointOnObject(g36,g16)
    c: Coincident(g36,g12)
    c: Perpendicular(g16,g36)
    c: Distance(g36) = 3
    c: Vertical(g34)
    c: DistanceX(g24,g24) = 2
    c: Horizontal(g20,g26)
    c: Coincident(g38,g39)
    c: PointOnObject(g38,g-1)
    c: Vertical(g38,g37)
    c: DistanceX(g26,g37) = 3
    c: Coincident(g40,g38)
    c: Tangent(g40,g37) = -1.5708
    c: Tangent(g37,g6) = 1.5708
    c: Coincident(g41,g6)
    c: Coincident(g41,g0)
    c: Vertical(g41)
    c: Coincident(g42,g28)
    c: PointOnObject(g42,g18)
    c: Horizontal(g42)
    c: Equal(g42,g24)
    c: DistanceX(g19,g19) = 47
FEATURE [PartDesign::Pad] Pad032
  Direction = (1,-2e-16,3e-16)
  Length = 3
  Length2 = 10
  Placement = pos=(0,0,0) rot=(0.57735,0.57735,0.57735;2.0944rad)
  Profile = -> Sketch049
  ReferenceAxis = -> Sketch049 [N_Axis]
  Type = 0
FEATURE [Sketcher::SketchObject] Sketch051
  ExternalGeometry = -> [Sketch049]
  FullyConstrained = true
  MapMode = 5
  Support = -> [XY_Plane012]
  expr: Constraints[10] = <<Spreadsheet>>.NutR
  expr: Constraints[21] = <<Spreadsheet>>.NutR
  expr: Constraints[3] = <<Spreadsheet>>.ScrewD
  sketch-geometry (9):
    g0: LineSegment StartX=1.04e-14 StartY=47 StartZ=0 EndX=-1.1e-15 EndY=-5 EndZ=0
    g1: Circle CenterX=8 CenterY=5 CenterZ=0 NormalX=0 NormalY=0 NormalZ=1 AngleXU=0 Radius=2.1
    g2: Circle CenterX=8 CenterY=37 CenterZ=0 NormalX=0 NormalY=0 NormalZ=1 AngleXU=0 Radius=2.1
    g3: LineSegment StartX=1.04e-14 StartY=47 StartZ=0 EndX=3 EndY=47 EndZ=0
    g4: LineSegment StartX=-1.1e-15 StartY=-5 StartZ=0 EndX=3 EndY=-5 EndZ=0
    g5: ArcOfCircle CenterX=3 CenterY=5 CenterZ=0 NormalX=0 NormalY=0 NormalZ=1 AngleXU=0 Radius=10 StartAngle=4.71239 EndAngle=6.28319
    g6: ArcOfCircle CenterX=3 CenterY=37 CenterZ=0 NormalX=0 NormalY=0 NormalZ=1 AngleXU=0 Radius=10 StartAngle=0 EndAngle=1.5708
    g7: LineSegment StartX=8 StartY=5 StartZ=0 EndX=8 EndY=37 EndZ=0
    g8: LineSegment StartX=13 StartY=37 StartZ=0 EndX=13 EndY=5 EndZ=0
  constraints (22):
    c: Coincident(g0,g-3)
    c: Coincident(g0,g-3)
    c: Equal(g2,g1)
    c: Diameter(g1) = 4.2
    c: Coincident(g3,g0)
    c: Horizontal(g3)
    c: Coincident(g4,g0)
    c: Horizontal(g4)
    c: Equal(g4,g3)
    c: DistanceX(g4,g4) = 3
    c: DistanceX(g4,g1) = 5
    c: Tangent(g6,g3) = 1.5708
    c: Tangent(g5,g4) = -1.5708
    c: Coincident(g7,g1)
    c: Coincident(g7,g2)
    c: Vertical(g7)
    c: Vertical(g8)
    c: Tangent(g5,g8) = 1.5708
    c: Tangent(g8,g6) = 1.5708
    c: Horizontal(g1,g5)
    c: Horizontal(g2,g6)
    c: DistanceX(g1,g5) = 5
FEATURE [PartDesign::Pad] Pad034
  BaseFeature = -> Pad032
  Direction = (0,0,1)
  Length = 3
  Length2 = 10
  Placement = pos=(0,0,0) rot=(0.57735,0.57735,0.57735;2.0944rad)
  Profile = -> Sketch051
  ReferenceAxis = -> Sketch051 [N_Axis]
  Type = 0
FEATURE [Sketcher::SketchObject] Sketch052
  ExternalGeometry = -> [Sketch049]
  FullyConstrained = true
  MapMode = 5
  Placement = pos=(0,0,0) rot=(0.57735,0.57735,0.57735;2.0944rad)
  Support = -> [YZ_Plane012]
  sketch-geometry (8):
    g0: Circle CenterX=2 CenterY=25.2 CenterZ=0 NormalX=0 NormalY=0 NormalZ=1 AngleXU=0 Radius=1.1
    g1: Circle CenterX=2 CenterY=13.8 CenterZ=0 NormalX=0 NormalY=0 NormalZ=1 AngleXU=0 Radius=1.1
    g2: Circle CenterX=49 CenterY=13.8 CenterZ=0 NormalX=0 NormalY=0 NormalZ=1 AngleXU=0 Radius=1.1
    g3: Circle CenterX=49 CenterY=25.2 CenterZ=0 NormalX=0 NormalY=0 NormalZ=1 AngleXU=0 Radius=1.1
    g4: Circle CenterX=2 CenterY=25.2 CenterZ=0 NormalX=0 NormalY=0 NormalZ=1 AngleXU=0 Radius=2
    g5: Circle CenterX=2 CenterY=13.8 CenterZ=0 NormalX=0 NormalY=0 NormalZ=1 AngleXU=0 Radius=2
    g6: Circle CenterX=49 CenterY=25.2 CenterZ=0 NormalX=0 NormalY=0 NormalZ=1 AngleXU=0 Radius=2
    g7: Circle CenterX=49 CenterY=13.8 CenterZ=0 NormalX=0 NormalY=0 NormalZ=1 AngleXU=0 Radius=2
  constraints (16):
    c: Equal(g-3,g0)
    c: Equal(g-5,g1)
    c: Equal(g2,g-6)
    c: Equal(g3,g-7)
    c: Coincident(g3,g-7)
    c: Coincident(g2,g-6)
    c: Coincident(g1,g-5)
    c: Coincident(g0,g-4)
    c: Coincident(g4,g0)
    c: PointOnObject(g-4,g4)
    c: Coincident(g5,g1)
    c: Coincident(g6,g3)
    c: Coincident(g7,g2)
    c: Equal(g5,g6)
    c: Equal(g6,g7)
    c: Equal(g7,g4)
FEATURE [PartDesign::Pad] Pad035
  BaseFeature = -> Pad034
  Direction = (1,-2e-16,3e-16)
  Length = 5
  Length2 = 10
  Placement = pos=(0,0,0) rot=(0.57735,0.57735,0.57735;2.0944rad)
  Profile = -> Sketch052
  ReferenceAxis = -> Sketch052 [N_Axis]
  Type = 0
FEATURE [PartDesign::Body] Body010  label="PicoBase"
  Group = -> [Sketch049,Pad032,Sketch051,Pad034,Sketch052,Pad035]
  Origin = -> Origin012
  Placement = pos=(122,0,5) rot=(0,0,1;0rad)
  Tip = -> Pad035
  expr: .Placement.Base.z = <<InnerIndexArch>>.Placement.Base.z
FEATURE [Mesh::Feature] Mesh  label="RJ11 Breakout"
FEATURE [Sketcher::SketchObject] Sketch053
  FullyConstrained = true
  MapMode = 5
  Placement = pos=(0,0,0) rot=(0.57735,0.57735,0.57735;2.0944rad)
  Support = -> [YZ_Plane013]
  sketch-geometry (2):
    g0: Circle CenterX=0 CenterY=0 CenterZ=0 NormalX=0 NormalY=0 NormalZ=1 AngleXU=0 Radius=1.05
    g1: Circle CenterX=0 CenterY=0 CenterZ=0 NormalX=0 NormalY=0 NormalZ=1 AngleXU=0 Radius=1.9
  constraints (4):
    c: Coincident(g0,g-1)
    c: Coincident(g1,g0)
    c: Diameter(g0) = 2.1
    c: Diameter(g1) = 3.8
FEATURE [PartDesign::Pad] Pad036
  Direction = (1,-2e-16,3e-16)
  Length = 3
  Length2 = 10
  Placement = pos=(0,0,0) rot=(0.57735,0.57735,0.57735;2.0944rad)
  Profile = -> Sketch053
  ReferenceAxis = -> Sketch053 [N_Axis]
  Type = 0
FEATURE [PartDesign::Body] Body011  label="PicoStandoffs"
  Group = -> [Sketch053,Pad036]
  Origin = -> Origin013
  Placement = pos=(129,2,30) rot=(0,0,1;0rad)
  Tip = -> Pad036
FEATURE [App::Link] Link  label="PicoStandoffs001"
  LinkPlacement = pos=(129,2,18.75) rot=(0,0,1;0rad)
  LinkedObject = -> Body011
  Placement = pos=(129,2,18.75) rot=(0,0,1;0rad)
FEATURE [App::Link] Link001  label="PicoStandoffs002"
  LinkPlacement = pos=(129,49,30) rot=(0,0,1;0rad)
  LinkedObject = -> Body011
  Placement = pos=(129,49,30) rot=(0,0,1;0rad)
FEATURE [App::Link] Link002  label="PicoStandoffs003"
  LinkPlacement = pos=(129,49,18.75) rot=(0,0,1;0rad)
  LinkedObject = -> Body011
  Placement = pos=(129,49,18.75) rot=(0,0,1;0rad)
FEATURE [App::DocumentObjectGroup] Group  label="Microcontroller"
  Group = -> [Body011,Link,Link001,Link002,PICO,Body010]
FEATURE [App::DocumentObjectGroup] Group001  label="RJ11"
  Group = -> [Part__Feature,Body009,Mesh]
FEATURE [Sketcher::SketchObject] Sketch054
  FullyConstrained = true
  MapMode = 5
  Placement = pos=(0,0,0) rot=(1,0,0;1.5708rad)
  Support = -> [XZ_Plane015]
  expr: .Constraints.real = <<InnerIndexArch>>.Placement.Base.z - 3mm
  expr: Constraints[11] = 10mm - <<Spreadsheet>>.NutR
  expr: Constraints[26] = <<Spreadsheet>>.Wiring
  expr: Constraints[28] = <<Spreadsheet>>.NutR * 6
  expr: Constraints[8] = 40mm + <<Spreadsheet>>.NutR * 2
  sketch-geometry (10):
    g0: LineSegment StartX=-55 StartY=-1 StartZ=0 EndX=-5 EndY=-1 EndZ=0
    g1: LineSegment StartX=-5 StartY=-1 StartZ=0 EndX=-5 EndY=2 EndZ=0
    g2: LineSegment StartX=-5 StartY=2 StartZ=0 EndX=-55 EndY=2 EndZ=0
    g3: LineSegment StartX=-55 StartY=2 StartZ=0 EndX=-55 EndY=-1 EndZ=0
    g4: LineSegment StartX=4 StartY=-1 StartZ=0 EndX=4 EndY=2 EndZ=0
    g5: LineSegment StartX=4 StartY=2 StartZ=0 EndX=-5 EndY=2 EndZ=0
    g6: LineSegment StartX=-5 StartY=-1 StartZ=0 EndX=1 EndY=-1 EndZ=0
    g7: LineSegment StartX=1 StartY=-1 StartZ=0 EndX=1 EndY=-31 EndZ=0
    g8: LineSegment StartX=1 StartY=-31 StartZ=0 EndX=4 EndY=-31 EndZ=0
    g9: LineSegment StartX=4 StartY=-1 StartZ=0 EndX=4 EndY=-31 EndZ=0
  constraints (29):
    c: Coincident(g0,g1)
    c: Coincident(g1,g2)
    c: Coincident(g2,g3)
    c: Coincident(g3,g0)
    c: Horizontal(g0)
    c: Horizontal(g2)
    c: Vertical(g1)
    c: Vertical(g3)
    c: DistanceX(g2,g2) = 50
    c: DistanceY(g-1,g1) = 2  'real'
    c: DistanceY(g1,g1) = 3
    c: DistanceX(g1,g-1) = 5
    c: Vertical(g4)
    c: Coincident(g4,g5)
    c: Coincident(g5,g2)
    c: Horizontal(g5)
    c: Coincident(g6,g0)
    c: Horizontal(g6)
    c: Coincident(g6,g7)
    c: Vertical(g7)
    c: Coincident(g7,g8)
    c: Horizontal(g8)
    c: Coincident(g9,g8)
    c: Vertical(g9)
    c: PointOnObject(g4,g6)
    c: Equal(g8,g1)
    c: DistanceX(g6,g6) = 6
    c: Coincident(g4,g9)
    c: DistanceY(g9,g9) = 30
FEATURE [PartDesign::Pad] Pad037
  Direction = (0,-1,-2e-16)
  Length = 46
  Length2 = 3
  Placement = pos=(0,0,0) rot=(1,0,0;1.5708rad)
  Profile = -> Sketch054
  ReferenceAxis = -> Sketch054 [N_Axis]
  Type = 4
  expr: Length = <<Spreadsheet>>.NutR * 2 * 4 + <<Spreadsheet>>.Wiring
FEATURE [Sketcher::SketchObject] Sketch055
  ExternalGeometry = -> [Sketch054]
  FullyConstrained = true
  MapMode = 5
  Placement = pos=(0,0,0) rot=(1,0,0;1.5708rad)
  Support = -> [XZ_Plane015]
  expr: Constraints[11] = Spreadsheet.NutR
  expr: Constraints[15] = <<Spreadsheet>>.NutR * 2
  expr: Constraints[19] = <<Spreadsheet>>.ScrewD
  sketch-geometry (32):
    g0: ArcOfCircle CenterX=9 CenterY=-28.2857 CenterZ=0 NormalX=0 NormalY=0 NormalZ=1 AngleXU=0 Radius=2.1 StartAngle=3.14159 EndAngle=6.28319
    g1: LineSegment StartX=6.9 StartY=-8 StartZ=0 EndX=6.9 EndY=-28.2857 EndZ=0
    g2: LineSegment StartX=11.1 StartY=-28.2857 StartZ=0 EndX=11.1 EndY=-8 EndZ=0
    g3: ArcOfCircle CenterX=9 CenterY=-38.2857 CenterZ=0 NormalX=0 NormalY=0 NormalZ=1 AngleXU=0 Radius=2.1 StartAngle=4.71239 EndAngle=7.85398
    g4: ArcOfCircle CenterX=-8.44423 CenterY=-28.2143 CenterZ=0 NormalX=0 NormalY=0 NormalZ=1 AngleXU=0 Radius=2.1 StartAngle=0.523599 EndAngle=3.66519
    g5: ArcOfCircle CenterX=9 CenterY=-38.2857 CenterZ=0 NormalX=0 NormalY=0 NormalZ=1 AngleXU=0 Radius=5 StartAngle=4.71239 EndAngle=6.47156
    g6: ArcOfCircle CenterX=-8.44423 CenterY=-28.2143 CenterZ=0 NormalX=0 NormalY=0 NormalZ=1 AngleXU=0 Radius=5 StartAngle=2.16569 EndAngle=3.66519
    g7: ArcOfCircle CenterX=-26.8593 CenterY=-1 CenterZ=0 NormalX=0 NormalY=0 NormalZ=1 AngleXU=0 Radius=27.8593 StartAngle=5.30728 EndAngle=6.28319
    g8: LineSegment StartX=4 StartY=2 StartZ=0 EndX=1 EndY=-1 EndZ=0
    g9: LineSegment StartX=-8.44423 StartY=-28.2143 StartZ=0 EndX=-12.7744 EndY=-30.7143 EndZ=0
    g10: LineSegment StartX=9 StartY=-38.2857 StartZ=0 EndX=9 EndY=-43.2857 EndZ=0
    g11: LineSegment StartX=-1.64151 StartY=-35.2453 StartZ=0 EndX=1 EndY=-31 EndZ=0
    g12: LineSegment StartX=9 StartY=-28.2857 StartZ=0 EndX=9 EndY=-38.2857 EndZ=0
    g13: ArcOfCircle CenterX=9 CenterY=-8 CenterZ=0 NormalX=0 NormalY=0 NormalZ=1 AngleXU=0 Radius=2.1 StartAngle=0 EndAngle=3.14159
    g14: ArcOfCircle CenterX=9 CenterY=2 CenterZ=0 NormalX=0 NormalY=0 NormalZ=1 AngleXU=0 Radius=2.1 StartAngle=1.5708 EndAngle=4.71239
    g15: ArcOfCircle CenterX=26.4442 CenterY=-8.07143 CenterZ=0 NormalX=0 NormalY=0 NormalZ=1 AngleXU=0 Radius=2.1 StartAngle=3.66519 EndAngle=6.80678
    g16: LineSegment StartX=9 StartY=2 StartZ=0 EndX=9 EndY=-8 EndZ=0
    g17: LineSegment StartX=26.4442 StartY=-8.07143 StartZ=0 EndX=24.6256 EndY=-9.12143 EndZ=0
    g18: ArcOfCircle CenterX=35.2282 CenterY=-33.2857 CenterZ=0 NormalX=0 NormalY=0 NormalZ=1 AngleXU=0 Radius=21.7005 StartAngle=1.90602 EndAngle=3.32997
    g19: ArcOfCircle CenterX=26.4442 CenterY=-8.07143 CenterZ=0 NormalX=0 NormalY=0 NormalZ=1 AngleXU=0 Radius=5 StartAngle=5.04761 EndAngle=6.80678
    g20: LineSegment StartX=26.4442 StartY=-8.07143 StartZ=0 EndX=31.4442 EndY=-8.07143 EndZ=0
    g21: LineSegment StartX=9 StartY=-28.2857 StartZ=0 EndX=13.9115 EndY=-29.222 EndZ=0
    g22: ArcOfCircle CenterX=9 CenterY=2 CenterZ=0 NormalX=0 NormalY=0 NormalZ=1 AngleXU=0 Radius=5 StartAngle=1.5708 EndAngle=3.14159
    g23: ArcOfCircle CenterX=9 CenterY=-18.1429 CenterZ=0 NormalX=0 NormalY=0 NormalZ=1 AngleXU=0 Radius=18.0429 StartAngle=3.66519 EndAngle=4.71239
    g24: ArcOfCircle CenterX=9 CenterY=-18.1429 CenterZ=0 NormalX=0 NormalY=0 NormalZ=1 AngleXU=0 Radius=22.2429 StartAngle=3.66519 EndAngle=4.71239
    g25: ArcOfCircle CenterX=9 CenterY=-18.1429 CenterZ=0 NormalX=0 NormalY=0 NormalZ=1 AngleXU=0 Radius=25.1429 StartAngle=3.66519 EndAngle=4.71239
    g26: ArcOfCircle CenterX=9 CenterY=-18.1429 CenterZ=0 NormalX=0 NormalY=0 NormalZ=1 AngleXU=0 Radius=18.0429 StartAngle=0.523599 EndAngle=1.5708
    g27: ArcOfCircle CenterX=9 CenterY=-18.1429 CenterZ=0 NormalX=0 NormalY=0 NormalZ=1 AngleXU=0 Radius=22.2429 StartAngle=0.523599 EndAngle=1.5708
    g28: ArcOfCircle CenterX=9 CenterY=-18.1429 CenterZ=0 NormalX=0 NormalY=0 NormalZ=1 AngleXU=0 Radius=25.1429 StartAngle=0.523599 EndAngle=1.5708
    g29: ArcOfCircle CenterX=9 CenterY=-18.1429 CenterZ=0 NormalX=0 NormalY=0 NormalZ=1 AngleXU=0 Radius=20.1429 StartAngle=3.66519 EndAngle=4.71239
    g30: LineSegment StartX=-6.62557 StartY=-27.1643 StartZ=0 EndX=9 EndY=-18.1429 EndZ=0
    g31: LineSegment StartX=9 StartY=-18.1429 StartZ=0 EndX=24.6256 EndY=-9.12143 EndZ=0
  constraints (78):
    c: Tangent(g1,g0) = -1.5708
    c: Tangent(g0,g2) = -1.5708
    c: Vertical(g1)
    c: Coincident(g5,g3)
    c: Coincident(g6,g4)
    c: Equal(g3,g0)
    c: Coincident(g6,g9) = -1.5708
    c: Tangent(g7,g6) = 1.5708
    c: Coincident(g9,g4)
    c: Coincident(g10,g3)
    c: Coincident(g10,g5)
    c: Distance(g9) = 5
    c: Angle(g9,g10) = 1.0472
    c: Coincident(g12,g0)
    c: Coincident(g12,g3)
    c: Distance(g12) = 10
    c: Vertical(g2)
    c: Tangent(g13,g1) = -1.5708
    c: Tangent(g13,g2) = -1.5708
    c: DistanceX(g1,g2) = 4.2
    c: Coincident(g16,g14)
    c: Coincident(g16,g13)
    c: Equal(g16,g12)
    c: Coincident(g17,g15)
    c: Vertical(g16)
    c: Equal(g14,g13)
    c: Coincident(g15,g17) = 1.5708
    c: Angle(g17,g16) = 1.0472
    c: Tangent(g19,g18) = 1.5708
    c: Coincident(g20,g15)
    c: Horizontal(g20)
    c: Coincident(g19,g15)
    c: Tangent(g18,g5) = 1.5708
    c: Coincident(g21,g0)
    c: PointOnObject(g21,g18)
    c: Perpendicular(g18,g21)
    c: Coincident(g22,g14)
    c: Equal(g11,g9)
    c: Equal(g21,g9)
    c: Coincident(g24,g23)
    c: Tangent(g23,g4) = 1.5708
    c: Tangent(g23,g3) = 1.5708
    c: Tangent(g24,g3) = -1.5708
    c: Tangent(g24,g4) = -1.5708
    c: PointOnObject(g3,g10)
    c: PointOnObject(g4,g9)
    c: Coincident(g25,g23)
    c: Coincident(g25,g5)
    c: Coincident(g25,g6)
    c: Coincident(g26,g23)
    c: Tangent(g26,g14) = 1.5708
    c: Tangent(g26,g15) = 1.5708
    c: Coincident(g27,g23)
    c: Tangent(g27,g15) = -1.5708
    c: Tangent(g27,g14) = -1.5708
    c: Equal(g20,g21)
    c: Coincident(g22,g8)
    c: Coincident(g28,g23)
    c: Tangent(g28,g22) = -1.5708
    c: Tangent(g28,g19) = -1.5708
    c: PointOnObject(g14,g16)
    c: Coincident(g29,g4)
    c: Coincident(g29,g3)
    c: Perpendicular(g29,g11)
    c: Perpendicular(g29,g9)
    c: Coincident(g4,g30)
    c: Coincident(g30,g31)
    c: Coincident(g31,g15)
    c: Coincident(g23,g30)
    c: Equal(g31,g30)
    c: PointOnObject(g20,g19)
    c: PointOnObject(g11,g29)
    c: Vertical(g12)
    c: Coincident(g11,g-5)
    c: Coincident(g8,g-4)
    c: Tangent(g7,g-3) = 1.5708
    c: Coincident(g8,g7)
    c: Horizontal(g8,g14)
FEATURE [PartDesign::Pad] Pad038
  BaseFeature = -> Pad037
  Direction = (0,-1,-2e-16)
  Length = 3
  Length2 = 10
  Placement = pos=(0,0,0) rot=(1,0,0;1.5708rad)
  Profile = -> Sketch055
  ReferenceAxis = -> Sketch055 [N_Axis]
  Reversed = true
  Type = 0
FEATURE [Sketcher::SketchObject] Sketch060
  FullyConstrained = true
  MapMode = 5
  Placement = pos=(0,0,0) rot=(1,0,0;1.5708rad)
  Support = -> [XZ_Plane016]
  expr: Constraints[11] = <<Spreadsheet>>.NutR + 3mm
  expr: Constraints[32] = <<Spreadsheet>>.NutR * 2
  expr: Constraints[39] = <<Spreadsheet>>.NutR
  expr: Constraints[41] = <<Spreadsheet>>.ScrewD / 2
  expr: Constraints[42] = <<Spreadsheet>>.NutR
  expr: Constraints[48] = <<Spreadsheet>>.NutR * 9
  sketch-geometry (23):
    g0: ArcOfCircle CenterX=14.6985 CenterY=-1.7101 CenterZ=0 NormalX=0 NormalY=0 NormalZ=1 AngleXU=0 Radius=2.1 StartAngle=5.93412 EndAngle=9.07571
    g1: ArcOfCircle CenterX=-16.0661 CenterY=-27.759 CenterZ=0 NormalX=0 NormalY=0 NormalZ=1 AngleXU=0 Radius=15 StartAngle=4.36332 EndAngle=5.93412
    g2: ArcOfCircle CenterX=14.6985 CenterY=-1.7101 CenterZ=0 NormalX=0 NormalY=0 NormalZ=1 AngleXU=0 Radius=5 StartAngle=0.000890861 EndAngle=2.79253
    g3: LineSegment StartX=-21.1964 StartY=-41.8544 StartZ=0 EndX=-32.4727 EndY=-37.7501 EndZ=0
    g4: LineSegment StartX=-32.4727 StartY=-37.7501 StartZ=0 EndX=-34.1828 EndY=-42.4486 EndZ=0
    g5: LineSegment StartX=-34.1828 StartY=-42.4486 StartZ=0 EndX=3.40488 EndY=-56.1294 EndZ=0
    g6: LineSegment StartX=19.6985 StartY=-1.70565 StartZ=0 EndX=19.7058 EndY=-9.92528 EndZ=0
    g7: ArcOfCircle CenterX=11.7058 CenterY=-9.93241 CenterZ=0 NormalX=0 NormalY=0 NormalZ=1 AngleXU=0 Radius=8 StartAngle=5.93412 EndAngle=6.28408
    g8: LineSegment StartX=8.71311 StartY=-18.1547 StartZ=0 EndX=16.2307 EndY=-20.8909 EndZ=0
    g9: LineSegment StartX=19.2233 StartY=-12.6686 StartZ=0 EndX=3.40488 EndY=-56.1294 EndZ=0
    g10: LineSegment StartX=-1.97072 StartY=-32.8893 StartZ=0 EndX=10 EndY=0 EndZ=0
    g11: ArcOfCircle CenterX=5.2929 CenterY=-27.5516 CenterZ=0 NormalX=0 NormalY=0 NormalZ=1 AngleXU=0 Radius=2.1 StartAngle=5.93412 EndAngle=9.07571
    g12: ArcOfCircle CenterX=-0.692466 CenterY=-43.9963 CenterZ=0 NormalX=0 NormalY=0 NormalZ=1 AngleXU=0 Radius=2.1 StartAngle=2.79253 EndAngle=5.93412
    g13: LineSegment StartX=3.31955 StartY=-26.8334 StartZ=0 EndX=-2.66582 EndY=-43.278 EndZ=0
    g14: LineSegment StartX=1.28089 StartY=-44.7145 StartZ=0 EndX=7.26625 EndY=-28.2699 EndZ=0
    g15: LineSegment StartX=12.7251 StartY=-0.991858 StartZ=0 EndX=6.73976 EndY=-17.4365 EndZ=0
    g16: LineSegment StartX=10.6865 StartY=-18.873 StartZ=0 EndX=16.6718 EndY=-2.42834 EndZ=0
    g17: ArcOfCircle CenterX=8.71311 CenterY=-18.1547 CenterZ=0 NormalX=0 NormalY=0 NormalZ=1 AngleXU=0 Radius=2.1 StartAngle=2.79253 EndAngle=5.93412
    g18: LineSegment StartX=-21.1964 StartY=-41.8544 StartZ=0 EndX=-2.40256 EndY=-48.6947 EndZ=0
    g19: LineSegment StartX=-0.692466 StartY=-43.9963 StartZ=0 EndX=-2.40256 EndY=-48.6947 EndZ=0
    g20: LineSegment StartX=6.73976 StartY=-17.4365 StartZ=0 EndX=3.31955 EndY=-26.8334 EndZ=0
    g21: LineSegment StartX=14.6985 StartY=-1.7101 StartZ=0 EndX=11.7058 EndY=-9.93241 EndZ=0
    g22: LineSegment StartX=11.7058 StartY=-9.93241 StartZ=0 EndX=8.71311 EndY=-18.1547 EndZ=0
  constraints (57):
    c: Coincident(g2,g0)
    c: Tangent(g1,g3) = 1.5708
    c: Coincident(g3,g4)
    c: Coincident(g4,g5)
    c: Perpendicular(g3,g4)
    c: Perpendicular(g5,g4)
    c: Distance(g4) = 5
    c: Tangent(g6,g2) = 1.5708
    c: Radius(g1) = 15
    c: Angle(g3,g-1) = 0.349066
    c: Distance(g5) = 40
    c: Distance(g8) = 8
    c: Tangent(g7,g6) = 1.5708
    c: Coincident(g9,g5)
    c: Tangent(g10,g1) = -1.5708
    c: Perpendicular(g5,g9)
    c: Parallel(g10,g9)
    c: PointOnObject(g8,g9)
    c: Perpendicular(g9,g8)
    c: Tangent(g11,g13) = -1.5708
    c: Tangent(g13,g12) = -1.5708
    c: Tangent(g12,g14) = -1.5708
    c: Tangent(g14,g11) = -1.5708
    c: Equal(g11,g12)
    c: Tangent(g15,g0) = -1.5708
    c: Tangent(g16,g0) = -1.5708
    c: Tangent(g17,g16) = -1.5708
    c: Tangent(g17,g15) = -1.5708
    c: Parallel(g16,g9)
    c: Parallel(g16,g15)
    c: Tangent(g10,g2) = 1.5708
    c: Equal(g11,g17)
    c: Distance(g17,g11) = 10
    c: Equal(g15,g13)
    c: Tangent(g9,g7) = 1.5708
    c: Coincident(g18,g1)
    c: Tangent(g18,g1)
    c: Coincident(g19,g12)
    c: Coincident(g19,g18)
    c: Distance(g19) = 5
    c: Perpendicular(g18,g19)
    c: Radius(g0) = 2.1
    c: Distance(g0,g2) = 5
    c: Coincident(g20,g15)
    c: Tangent(g20,g17)
    c: Parallel(g13,g20)
    c: Coincident(g11,g20)
    c: Coincident(g8,g17)
    c: Distance(g0,g12) = 45
    c: Coincident(g21,g0)
    c: Coincident(g21,g7)
    c: Coincident(g22,g7)
    c: Coincident(g22,g17)
    c: Equal(g21,g22)
    c: Angle(g21,g22) = 3.14159
    c: DistanceX(g-1,g2) = 10
    c: PointOnObject(g2,g-1)
FEATURE [PartDesign::Pad] Pad039
  Direction = (0,-1,-2e-16)
  Length = 4
  Length2 = 10
  Placement = pos=(0,0,0) rot=(1,0,0;1.5708rad)
  Profile = -> Sketch060
  ReferenceAxis = -> Sketch060 [N_Axis]
  Type = 0
FEATURE [Sketcher::SketchObject] Sketch061
  ExternalGeometry = -> [Sketch060]
  FullyConstrained = true
  MapMode = 5
  Placement = pos=(0,0,0) rot=(1,0,0;1.5708rad)
  Support = -> [XZ_Plane016]
  sketch-geometry (4):
    g0: LineSegment StartX=5.11498 StartY=-51.4309 StartZ=0 EndX=-32.4727 EndY=-37.7501 EndZ=0
    g1: LineSegment StartX=-32.4727 StartY=-37.7501 StartZ=0 EndX=-34.1828 EndY=-42.4486 EndZ=0
    g2: LineSegment StartX=-34.1828 StartY=-42.4486 StartZ=0 EndX=3.40488 EndY=-56.1294 EndZ=0
    g3: LineSegment StartX=5.11498 StartY=-51.4309 StartZ=0 EndX=3.40488 EndY=-56.1294 EndZ=0
  constraints (9):
    c: Coincident(g0,g1)
    c: Coincident(g1,g2)
    c: Coincident(g1,g-3)
    c: Coincident(g0,g-3)
    c: Coincident(g3,g0)
    c: Coincident(g3,g2)
    c: PointOnObject(g-5,g0)
    c: Coincident(g2,g-4)
    c: PointOnObject(g0,g-4)
FEATURE [PartDesign::Pad] Pad040
  BaseFeature = -> Pad039
  Direction = (0,-1,-2e-16)
  Length = 20
  Length2 = 10
  Placement = pos=(0,0,0) rot=(1,0,0;1.5708rad)
  Profile = -> Sketch061
  ReferenceAxis = -> Sketch061 [N_Axis]
  Reversed = true
  Type = 0
FEATURE [PartDesign::Body] Body013  label="TentingFoot"
  Group = -> [Sketch060,Pad039,Sketch061,Pad040]
  Origin = -> Origin016
  Placement = pos=(140,55,0) rot=(0,0,1;0rad)
  Tip = -> Pad040
FEATURE [Part::Mirroring] Part__Mirroring001  label="TentingFoot (Mirror #2)"
  Base = (133.843,1.90735e-06,-12.4421)
  Normal = (0,1,-1.19209e-07)
  Source = -> Body013
FEATURE [Sketcher::SketchObject] Sketch062
  ExternalGeometry = -> [Sketch046]
  FullyConstrained = true
  MapMode = 5
  Placement = pos=(4.4e-15,-4.7e-15,21) rot=(0.743145,0,0.669131;3.14159rad)
  Support = -> [DatumPlane]
  sketch-geometry (11):
    g0: LineSegment StartX=-1.79725 StartY=-10.5427 StartZ=0 EndX=-2.97902 EndY=-10.3343 EndZ=0
    g1: LineSegment StartX=-2.97902 StartY=-10.3343 StartZ=0 EndX=-3.96383 EndY=-10.1606 EndZ=0
    g2: LineSegment StartX=-3.96383 StartY=-10.1606 StartZ=0 EndX=-5.73648 EndY=-9.84808 EndZ=0
    g3: LineSegment StartX=-4.19456 StartY=-17.2279 StartZ=0 EndX=-1.76348 EndY=-3.44064 EndZ=0
    g4: LineSegment StartX=-1.76348 StartY=-3.44064 StartZ=0 EndX=-1.96044 EndY=-3.40591 EndZ=0
    g5: LineSegment StartX=-1.96044 StartY=-3.40591 StartZ=0 EndX=-1.7347 EndY=-2.12566 EndZ=0
    g6: LineSegment StartX=-1.7347 StartY=-2.12566 StartZ=0 EndX=-2.52255 EndY=-1.98674 EndZ=0
    g7: LineSegment StartX=-2.52255 StartY=-1.98674 StartZ=0 EndX=-5.40511 EndY=-18.3345 EndZ=0
    g8: LineSegment StartX=-5.40511 StartY=-18.3345 StartZ=0 EndX=-4.61726 EndY=-18.4735 EndZ=0
    g9: LineSegment StartX=-4.61726 StartY=-18.4735 StartZ=0 EndX=-4.39152 EndY=-17.1932 EndZ=0
    g10: LineSegment StartX=-4.39152 StartY=-17.1932 StartZ=0 EndX=-4.19456 EndY=-17.2279 EndZ=0
  constraints (28):
    c: Coincident(g-3,g0)
    c: Coincident(g0,g1)
    c: Coincident(g1,g2)
    c: Coincident(g2,g-4)
    c: Angle(g1,g2) = 3.14159
    c: Angle(g1,g0) = 3.14159
    c: Distance(g0) = 1.2
    c: Distance(g1) = 1
    c: PointOnObject(g3,g-5)
    c: PointOnObject(g3,g-8)
    c: Coincident(g3,g4)
    c: Coincident(g4,g-8)
    c: Coincident(g4,g5)
    c: Coincident(g5,g-7)
    c: Coincident(g5,g6)
    c: PointOnObject(g6,g-7)
    c: Coincident(g6,g7)
    c: PointOnObject(g7,g-6)
    c: Coincident(g7,g8)
    c: Coincident(g8,g-6)
    c: Coincident(g8,g9)
    c: Coincident(g9,g-5)
    c: Coincident(g9,g10)
    c: Coincident(g10,g3)
    c: PointOnObject(g0,g3)
    c: PointOnObject(g1,g7)
    c: Perpendicular(g7,g1)
    c: Perpendicular(g0,g3)
FEATURE [PartDesign::Pocket] Pocket020
  BaseFeature = -> Pocket014
  Direction = (-0.994522,0,0.104528)
  Length = 14.6
  Length2 = 5
  Midplane = true
  Profile = -> Sketch062
  ReferenceAxis = -> Sketch062 [N_Axis]
  Type = 0
FEATURE [Sketcher::SketchObject] Sketch063
  ExternalGeometry = -> [Sketch045]
  FullyConstrained = true
  MapMode = 5
  Placement = pos=(-19.8904,-5.1e-15,23.0906) rot=(0.743145,0,0.669131;3.14159rad)
  Support = -> [DatumPlane001]
  sketch-geometry (11):
    g0: LineSegment StartX=-1.76348 StartY=-3.44064 StartZ=0 EndX=-4.19456 EndY=-17.2279 EndZ=0
    g1: LineSegment StartX=-4.19456 StartY=-17.2279 StartZ=0 EndX=-4.39152 EndY=-17.1932 EndZ=0
    g2: LineSegment StartX=-4.39152 StartY=-17.1932 StartZ=0 EndX=-4.61726 EndY=-18.4735 EndZ=0
    g3: LineSegment StartX=-4.61726 StartY=-18.4735 StartZ=0 EndX=-5.40511 EndY=-18.3345 EndZ=0
    g4: LineSegment StartX=-5.40511 StartY=-18.3345 StartZ=0 EndX=-2.52255 EndY=-1.98674 EndZ=0
    g5: LineSegment StartX=-2.52255 StartY=-1.98674 StartZ=0 EndX=-1.7347 EndY=-2.12566 EndZ=0
    g6: LineSegment StartX=-1.7347 StartY=-2.12566 StartZ=0 EndX=-1.96044 EndY=-3.40591 EndZ=0
    g7: LineSegment StartX=-1.96044 StartY=-3.40591 StartZ=0 EndX=-1.76348 EndY=-3.44064 EndZ=0
    g8: LineSegment StartX=-1.79725 StartY=-10.5427 StartZ=0 EndX=-2.97902 EndY=-10.3343 EndZ=0
    g9: LineSegment StartX=-2.97902 StartY=-10.3343 StartZ=0 EndX=-3.96383 EndY=-10.1606 EndZ=0
    g10: LineSegment StartX=-3.96383 StartY=-10.1606 StartZ=0 EndX=-5.73648 EndY=-9.84808 EndZ=0
  constraints (28):
    c: PointOnObject(g0,g-7)
    c: PointOnObject(g0,g-3)
    c: Coincident(g0,g1)
    c: Coincident(g1,g-3)
    c: Coincident(g1,g2)
    c: Coincident(g2,g-4)
    c: Coincident(g2,g3)
    c: PointOnObject(g3,g-4)
    c: Coincident(g3,g4)
    c: PointOnObject(g4,g-8)
    c: Coincident(g4,g5)
    c: Coincident(g5,g-8)
    c: Coincident(g5,g6)
    c: Coincident(g6,g-7)
    c: Coincident(g6,g7)
    c: Coincident(g7,g0)
    c: Coincident(g-6,g8)
    c: PointOnObject(g8,g0)
    c: Coincident(g8,g9)
    c: PointOnObject(g9,g4)
    c: Coincident(g9,g10)
    c: Coincident(g10,g-5)
    c: Angle(g9,g10) = 3.14159
    c: Angle(g9,g8) = 3.14159
    c: Distance(g8) = 1.2
    c: Distance(g9) = 1
    c: Perpendicular(g0,g8)
    c: Perpendicular(g4,g9)
FEATURE [PartDesign::Pocket] Pocket021
  BaseFeature = -> Pocket020
  Direction = (-0.994522,0,0.104528)
  Length = 14.6
  Length2 = 5
  Midplane = true
  Profile = -> Sketch063
  ReferenceAxis = -> Sketch063 [N_Axis]
  Type = 0
FEATURE [Sketcher::SketchObject] Sketch064
  ExternalGeometry = -> [Sketch047]
  FullyConstrained = true
  MapMode = 5
  Placement = pos=(19.8904,-4.2e-15,18.9094) rot=(0.743145,0,0.669131;3.14159rad)
  Support = -> [DatumPlane002]
  sketch-geometry (11):
    g0: LineSegment StartX=-1.76348 StartY=-3.44064 StartZ=0 EndX=-1.96044 EndY=-3.40591 EndZ=0
    g1: LineSegment StartX=-1.96044 StartY=-3.40591 StartZ=0 EndX=-1.7347 EndY=-2.12566 EndZ=0
    g2: LineSegment StartX=-1.7347 StartY=-2.12566 StartZ=0 EndX=-2.52255 EndY=-1.98674 EndZ=0
    g3: LineSegment StartX=-2.52255 StartY=-1.98674 StartZ=0 EndX=-5.40511 EndY=-18.3345 EndZ=0
    g4: LineSegment StartX=-5.40511 StartY=-18.3345 StartZ=0 EndX=-4.61726 EndY=-18.4735 EndZ=0
    g5: LineSegment StartX=-4.61726 StartY=-18.4735 StartZ=0 EndX=-4.39152 EndY=-17.1932 EndZ=0
    g6: LineSegment StartX=-4.39152 StartY=-17.1932 StartZ=0 EndX=-4.19456 EndY=-17.2279 EndZ=0
    g7: LineSegment StartX=-4.19456 StartY=-17.2279 StartZ=0 EndX=-1.76348 EndY=-3.44064 EndZ=0
    g8: LineSegment StartX=-1.79725 StartY=-10.5427 StartZ=0 EndX=-2.97902 EndY=-10.3343 EndZ=0
    g9: LineSegment StartX=-2.97902 StartY=-10.3343 StartZ=0 EndX=-3.96383 EndY=-10.1606 EndZ=0
    g10: LineSegment StartX=-3.96383 StartY=-10.1606 StartZ=0 EndX=-5.73648 EndY=-9.84808 EndZ=0
  constraints (28):
    c: PointOnObject(g0,g-3)
    c: Coincident(g0,g-3)
    c: Coincident(g0,g1)
    c: Coincident(g1,g-4)
    c: Coincident(g1,g2)
    c: PointOnObject(g2,g-4)
    c: Coincident(g2,g3)
    c: PointOnObject(g3,g-6)
    c: Coincident(g3,g4)
    c: Coincident(g4,g-6)
    c: Coincident(g4,g5)
    c: Coincident(g5,g-5)
    c: Coincident(g5,g6)
    c: PointOnObject(g6,g-5)
    c: Coincident(g6,g7)
    c: Coincident(g7,g0)
    c: Coincident(g-8,g8)
    c: PointOnObject(g8,g7)
    c: Coincident(g8,g9)
    c: PointOnObject(g9,g3)
    c: Coincident(g9,g10)
    c: Coincident(g10,g-7)
    c: Angle(g10,g9) = 3.14159
    c: Angle(g8,g9) = 3.14159
    c: Distance(g8) = 1.2
    c: Distance(g9) = 1
    c: Perpendicular(g3,g9)
    c: Perpendicular(g8,g7)
FEATURE [PartDesign::Pocket] Pocket022
  BaseFeature = -> Pocket021
  Direction = (-0.994522,0,0.104528)
  Length = 14.6
  Length2 = 5
  Midplane = true
  Profile = -> Sketch064
  ReferenceAxis = -> Sketch064 [N_Axis]
  Type = 0
FEATURE [PartDesign::Body] Body008  label="Thumb Cluster"
  Group = -> [Sketch040,Pad026,Sketch041,Pad027,DatumLine,DatumPlane,Sketch042,Pad028,Pad029,DatumPlane001,DatumPlane002,Sketch045,Pocket012,Sketch046,Pocket013,Sketch047,Pocket014,Sketch062,Pocket020,Sketch063,Pocket021,Sketch064,Pocket022]
  Origin = -> Origin010
  Placement = pos=(125,-61,5) rot=(0,0,-1;0.191986rad)
  Tip = -> Pocket022
  expr: .Placement.Base.z = <<InnerIndexArch>>.Placement.Base.z
FEATURE [Sketcher::SketchObject] Sketch065
  FullyConstrained = false
  MapMode = 5
  Placement = pos=(0,0,0) rot=(1,0,0;1.5708rad)
  Support = -> [XZ_Plane]
  sketch-geometry (8):
    g0: LineSegment StartX=0 StartY=12.3824 StartZ=0 EndX=0 EndY=-3.61756 EndZ=0
    g1: LineSegment StartX=20 StartY=7.42184 StartZ=0 EndX=20 EndY=-8.57816 EndZ=0
    g2: LineSegment StartX=40 StartY=2.69316 StartZ=0 EndX=40 EndY=-13.3068 EndZ=0
    g3: LineSegment StartX=60 StartY=0.676164 StartZ=0 EndX=60 EndY=-15.3238 EndZ=0
    g4: LineSegment StartX=80 StartY=-5.67319 StartZ=0 EndX=80 EndY=-21.6732 EndZ=0
    g5: LineSegment StartX=100 StartY=-1.47822 StartZ=0 EndX=100 EndY=-17.4782 EndZ=0
    g6: LineSegment StartX=120 StartY=-1.65596 StartZ=0 EndX=120 EndY=-17.656 EndZ=0
    g7: GeomPoint X=80 Y=-13.6732 Z=0
  constraints (23):
    c: Vertical(g0)
    c: DistanceY(g0,g0) = 16
    c: PointOnObject(g0,g-2)
    c: Vertical(g1)
    c: Vertical(g2)
    c: Vertical(g3)
    c: Vertical(g4)
    c: Vertical(g5)
    c: Vertical(g6)
    c: Equal(g6,g5)
    c: Equal(g5,g4)
    c: Equal(g4,g3)
    c: Equal(g3,g2)
    c: Equal(g2,g1)
    c: Equal(g1,g0)
    c: DistanceX(g0,g1) = 20
    c: DistanceX(g1,g2) = 20
    c: DistanceX(g2,g3) = 20
    c: DistanceX(g3,g4) = 20
    c: DistanceX(g4,g5) = 20
    c: DistanceX(g5,g6) = 20
    c: PointOnObject(g7,g4)
    c: DistanceY(g4,g7) = 8
FEATURE [PartDesign::Body] Body  label="OuterArch"
  Group = -> [Sketch,Pad,Sketch001,Pad001,Sketch002,Pad002,Sketch003,Pocket,Sketch004,Pocket001,Sketch065]
  Origin = -> Origin
  Placement = pos=(10,-10,15) rot=(0,0,1;0rad)
  Tip = -> Pocket001
FEATURE [Sketcher::SketchObject] Sketch056
  ExternalGeometry = -> [Pad038]
  FullyConstrained = true
  MapMode = 5
  Support = -> [XY_Plane015]
  expr: Constraints[18] = <<Spreadsheet>>.ScrewD
  expr: Constraints[42] = <<Spreadsheet>>.NutR
  sketch-geometry (18):
    g0: ArcOfCircle CenterX=-50 CenterY=-2 CenterZ=0 NormalX=0 NormalY=0 NormalZ=1 AngleXU=0 Radius=2.1 StartAngle=5.53e-14 EndAngle=3.14159
    g1: ArcOfCircle CenterX=-50 CenterY=-41 CenterZ=0 NormalX=0 NormalY=0 NormalZ=1 AngleXU=0 Radius=2.1 StartAngle=3.14159 EndAngle=6.28319
    g2: LineSegment StartX=-52.1 StartY=-2 StartZ=0 EndX=-52.1 EndY=-41 EndZ=0
    g3: LineSegment StartX=-47.9 StartY=-41 StartZ=0 EndX=-47.9 EndY=-2 EndZ=0
    g4: ArcOfCircle CenterX=-30 CenterY=-2 CenterZ=0 NormalX=0 NormalY=0 NormalZ=1 AngleXU=0 Radius=2.1 StartAngle=5.53e-14 EndAngle=3.14159
    g5: ArcOfCircle CenterX=-30 CenterY=-41 CenterZ=0 NormalX=0 NormalY=0 NormalZ=1 AngleXU=0 Radius=2.1 StartAngle=3.14159 EndAngle=6.28319
    g6: LineSegment StartX=-32.1 StartY=-2 StartZ=0 EndX=-32.1 EndY=-41 EndZ=0
    g7: LineSegment StartX=-27.9 StartY=-41 StartZ=0 EndX=-27.9 EndY=-2 EndZ=0
    g8: ArcOfCircle CenterX=-10 CenterY=-2 CenterZ=0 NormalX=0 NormalY=0 NormalZ=1 AngleXU=0 Radius=2.1 StartAngle=5.31e-14 EndAngle=3.14159
    g9: ArcOfCircle CenterX=-10 CenterY=-41 CenterZ=0 NormalX=0 NormalY=0 NormalZ=1 AngleXU=0 Radius=2.1 StartAngle=3.14159 EndAngle=6.28319
    g10: LineSegment StartX=-12.1 StartY=-2 StartZ=0 EndX=-12.1 EndY=-41 EndZ=0
    g11: LineSegment StartX=-7.9 StartY=-41 StartZ=0 EndX=-7.9 EndY=-2 EndZ=0
    g12: LineSegment StartX=-50 StartY=-2 StartZ=0 EndX=-30 EndY=-2 EndZ=0
    g13: LineSegment StartX=-30 StartY=-2 StartZ=0 EndX=-10 EndY=-2 EndZ=0
    g14: LineSegment StartX=-10 StartY=-41 StartZ=0 EndX=-30 EndY=-41 EndZ=0
    g15: LineSegment StartX=-30 StartY=-41 StartZ=0 EndX=-50 EndY=-41 EndZ=0
    g16: LineSegment StartX=-50 StartY=-41 StartZ=0 EndX=-50 EndY=-46 EndZ=0
    g17: LineSegment StartX=-50 StartY=-2 StartZ=0 EndX=-50 EndY=3 EndZ=0
  constraints (44):
    c: Tangent(g0,g2) = -1.5708
    c: Tangent(g2,g1) = -1.5708
    c: Tangent(g1,g3) = -1.5708
    c: Tangent(g3,g0) = -1.5708
    c: Equal(g0,g1)
    c: Vertical(g2)
    c: Tangent(g4,g6) = -1.5708
    c: Tangent(g6,g5) = -1.5708
    c: Tangent(g5,g7) = -1.5708
    c: Tangent(g7,g4) = -1.5708
    c: Equal(g4,g5)
    c: Vertical(g6)
    c: Tangent(g8,g10) = -1.5708
    c: Tangent(g10,g9) = -1.5708
    c: Tangent(g9,g11) = -1.5708
    c: Tangent(g11,g8) = -1.5708
    c: Equal(g8,g9)
    c: Vertical(g10)
    c: DistanceX(g9,g9) = 4.2
    c: Equal(g9,g5)
    c: Equal(g5,g1)
    c: Coincident(g12,g0)
    c: Coincident(g12,g4)
    c: Horizontal(g12)
    c: Coincident(g13,g4)
    c: Coincident(g13,g8)
    c: Horizontal(g13)
    c: Coincident(g14,g9)
    c: Coincident(g14,g5)
    c: Horizontal(g14)
    c: Coincident(g14,g15)
    c: Coincident(g15,g1)
    c: Horizontal(g15)
    c: Equal(g15,g14)
    c: DistanceX(g15,g15) = 20
    c: DistanceX(g8,g-1) = 10
    c: Coincident(g16,g1)
    c: Vertical(g16)
    c: Coincident(g17,g0)
    c: PointOnObject(g17,g-3)
    c: Vertical(g17)
    c: Equal(g17,g16)
    c: DistanceY(g16,g16) = 5
    c: PointOnObject(g16,g-4)
FEATURE [PartDesign::Pocket] Pocket016
  BaseFeature = -> Pad038
  Direction = (0,0,-1)
  Length = 20
  Length2 = 5
  Midplane = true
  Placement = pos=(0,0,0) rot=(1,0,0;1.5708rad)
  Profile = -> Sketch056
  ReferenceAxis = -> Sketch056 [N_Axis]
  Type = 0
FEATURE [Sketcher::SketchObject] Sketch066
  ExternalGeometry = -> [Pocket016]
  FullyConstrained = true
  MapMode = 5
  Placement = pos=(4,0,0) rot=(0.707107,0,0.707107;3.14159rad)
  Support = -> [Pocket016]
  expr: Constraints[17] = <<Spreadsheet>>.NutR * 2
  expr: Constraints[18] = <<Spreadsheet>>.NutR * 2
  expr: Constraints[19] = <<Spreadsheet>>.NutR * 6
  expr: Constraints[20] = <<Spreadsheet>>.NutR * 4
  expr: Constraints[21] = <<Spreadsheet>>.NutR * 2
  expr: Constraints[45] = <<Spreadsheet>>.ScrewD
  expr: Constraints[48] = <<Spreadsheet>>.NutR
  expr: Constraints[49] = <<Spreadsheet>>.NutR
  sketch-geometry (19):
    g0: LineSegment StartX=-26 StartY=41 StartZ=0 EndX=-26 EndY=11 EndZ=0
    g1: LineSegment StartX=-16 StartY=11 StartZ=0 EndX=-16 EndY=41 EndZ=0
    g2: LineSegment StartX=-6 StartY=41 StartZ=0 EndX=-6 EndY=11 EndZ=0
    g3: LineSegment StartX=-6 StartY=21 StartZ=0 EndX=-26 EndY=21 EndZ=0
    g4: LineSegment StartX=-26 StartY=31 StartZ=0 EndX=-6 EndY=31 EndZ=0
    g5: LineSegment StartX=-6 StartY=41 StartZ=0 EndX=-26 EndY=41 EndZ=0
    g6: LineSegment StartX=-26 StartY=11 StartZ=0 EndX=-6 EndY=11 EndZ=0
    g7: Circle CenterX=-26 CenterY=41 CenterZ=0 NormalX=0 NormalY=0 NormalZ=1 AngleXU=0 Radius=2.1
    g8: Circle CenterX=-16 CenterY=31 CenterZ=0 NormalX=0 NormalY=0 NormalZ=1 AngleXU=0 Radius=2.1
    g9: Circle CenterX=-16 CenterY=21 CenterZ=0 NormalX=0 NormalY=0 NormalZ=1 AngleXU=0 Radius=2.1
    g10: Circle CenterX=-16 CenterY=41 CenterZ=0 NormalX=0 NormalY=0 NormalZ=1 AngleXU=0 Radius=2.1
    g11: Circle CenterX=-6 CenterY=31 CenterZ=0 NormalX=0 NormalY=0 NormalZ=1 AngleXU=0 Radius=2.1
    g12: Circle CenterX=-6 CenterY=41 CenterZ=0 NormalX=0 NormalY=0 NormalZ=1 AngleXU=0 Radius=2.1
    g13: Circle CenterX=-26 CenterY=31 CenterZ=0 NormalX=0 NormalY=0 NormalZ=1 AngleXU=0 Radius=2.1
    g14: Circle CenterX=-26 CenterY=21 CenterZ=0 NormalX=0 NormalY=0 NormalZ=1 AngleXU=0 Radius=2.1
    g15: Circle CenterX=-26 CenterY=11 CenterZ=0 NormalX=0 NormalY=0 NormalZ=1 AngleXU=0 Radius=2.1
    g16: Circle CenterX=-16 CenterY=11 CenterZ=0 NormalX=0 NormalY=0 NormalZ=1 AngleXU=0 Radius=2.1
    g17: Circle CenterX=-6 CenterY=11 CenterZ=0 NormalX=0 NormalY=0 NormalZ=1 AngleXU=0 Radius=2.1
    g18: Circle CenterX=-6 CenterY=21 CenterZ=0 NormalX=0 NormalY=0 NormalZ=1 AngleXU=0 Radius=2.1
  constraints (50):
    c: Vertical(g0)
    c: Vertical(g1)
    c: Vertical(g2)
    c: PointOnObject(g3,g2)
    c: PointOnObject(g3,g0)
    c: Horizontal(g3)
    c: PointOnObject(g4,g0)
    c: PointOnObject(g4,g2)
    c: Horizontal(g4)
    c: Coincident(g5,g2)
    c: Coincident(g5,g0)
    c: Horizontal(g5)
    c: Coincident(g6,g0)
    c: Coincident(g6,g2)
    c: Horizontal(g6)
    c: PointOnObject(g1,g6)
    c: PointOnObject(g1,g5)
    c: DistanceY(g4,g0) = 10
    c: DistanceY(g3,g4) = 10
    c: DistanceY(g2,g2) = 30
    c: DistanceX(g6,g6) = 20
    c: DistanceX(g0,g1) = 10
    c: Coincident(g7,g0)
    c: PointOnObject(g8,g1)
    c: PointOnObject(g9,g1)
    c: Coincident(g10,g1)
    c: Coincident(g11,g4)
    c: Coincident(g12,g2)
    c: Coincident(g13,g4)
    c: Coincident(g14,g3)
    c: Coincident(g15,g0)
    c: Coincident(g16,g1)
    c: Coincident(g17,g2)
    c: Coincident(g18,g3)
    c: Equal(g13,g7)
    c: Equal(g7,g14)
    c: Equal(g14,g15)
    c: Equal(g15,g16)
    c: Equal(g16,g9)
    c: Equal(g9,g8)
    c: Equal(g8,g10)
    c: Equal(g10,g12)
    c: Equal(g12,g11)
    c: Equal(g11,g18)
    c: Equal(g18,g17)
    c: Diameter(g7) = 4.2
    c: PointOnObject(g8,g4)
    c: PointOnObject(g9,g3)
    c: DistanceX(g-3,g7) = 5
    c: DistanceY(g7,g-3) = 5
FEATURE [PartDesign::Pocket] Pocket023
  BaseFeature = -> Pocket016
  Direction = (-1,0,2e-16)
  Length = 5
  Length2 = 5
  Placement = pos=(0,0,0) rot=(1,0,0;1.5708rad)
  Profile = -> Sketch066
  ReferenceAxis = -> Sketch066 [N_Axis]
  Type = 0
FEATURE [PartDesign::Body] Body012  label="TentingLeg"
  Group = -> [Sketch054,Pad037,Sketch055,Pad038,Sketch056,Pocket016,Sketch066,Pocket023]
  Origin = -> Origin015
  Placement = pos=(140,47,0) rot=(0,0,1;0rad)
  Tip = -> Pocket023
FEATURE [Part::Mirroring] Part__Mirroring  label="TentingLeg (Mirror #1)"
  Base = (119.669,0,-14.4372)
  Normal = (0,1,-1.19209e-07)
  Source = -> Body012
FEATURE [App::Part] Part  label="Tenting Part"
  Group = -> [Body013,Body012,Part__Mirroring,Part__Mirroring001]
  Origin = -> Origin014
